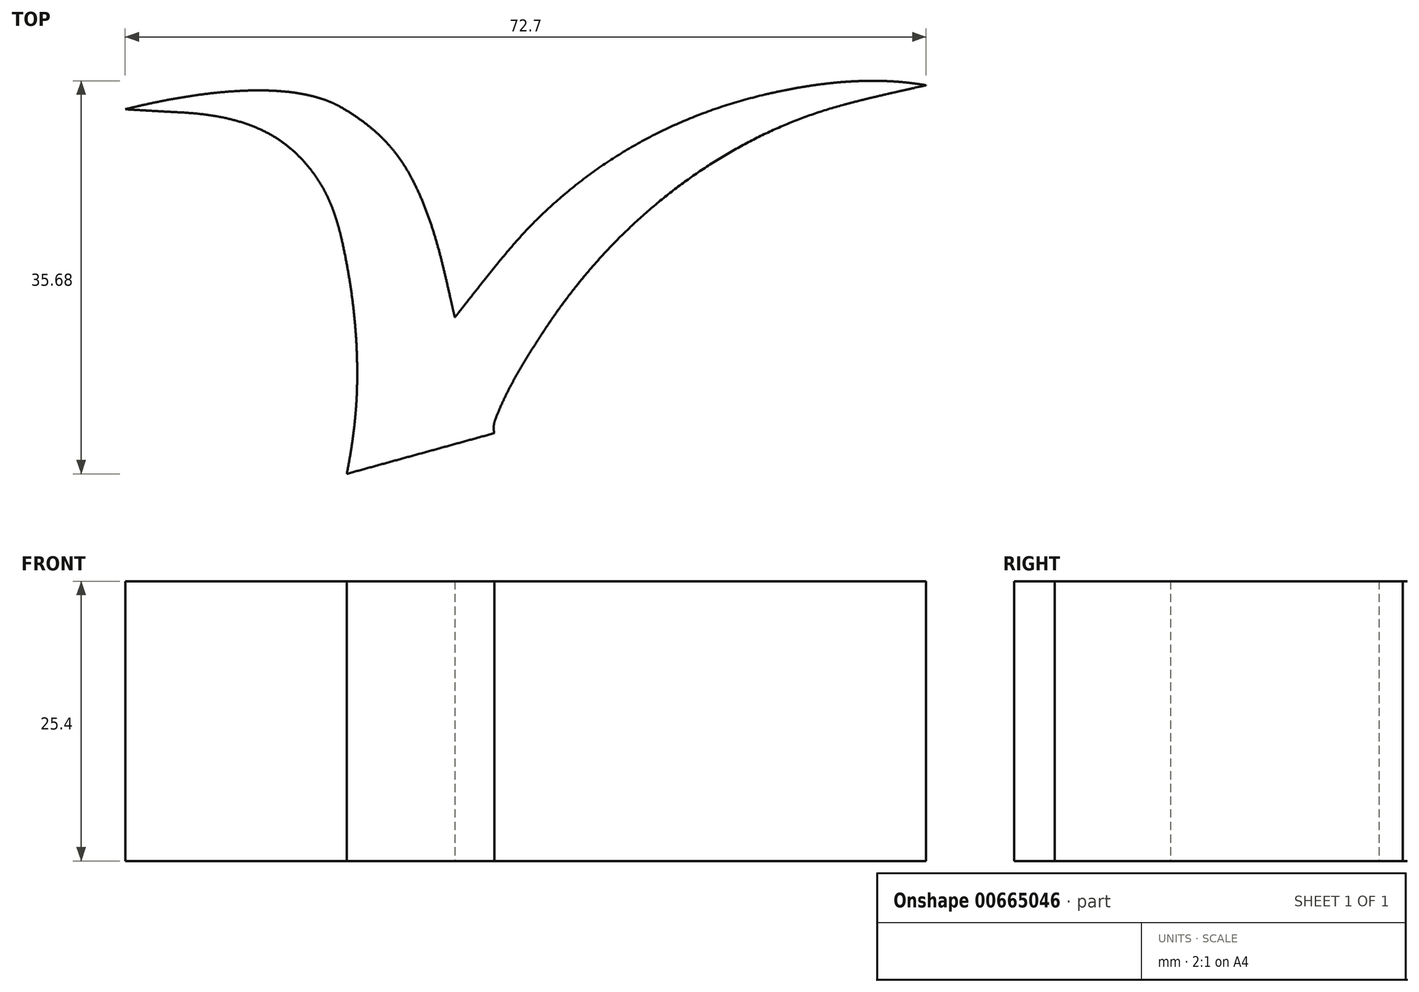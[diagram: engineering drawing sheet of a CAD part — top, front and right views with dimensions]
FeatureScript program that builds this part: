
annotation { "Feature Type Name" : "Feature", "Feature Type Description" : "" }
export const myFeature = defineFeature(function(context is Context, id is Id, definition is map)
    precondition{}
    {
        {
            var Q0;
            Q0=qCreatedBy(makeId("Top.planeOp"),FACE);
            var sketch = newSketch(context, id + "F0", { "sketchPlane" : qUnion([Q0])});
            skLineSegment(sketch, "E0", {"start": v(-36.35, 15.26) * mm, "end": v(-36.3, 15.26) * mm});
            skLineSegment(sketch, "E1", {"start": v(-36.3, 15.26) * mm, "end": v(-36.27, 15.26) * mm});
            skLineSegment(sketch, "E2", {"start": v(-36.27, 15.26) * mm, "end": v(-36.23, 15.25) * mm});
            skLineSegment(sketch, "E3", {"start": v(-36.23, 15.25) * mm, "end": v(-36.2, 15.25) * mm});
            skLineSegment(sketch, "E4", {"start": v(-36.2, 15.25) * mm, "end": v(-36.15, 15.25) * mm});
            skLineSegment(sketch, "E5", {"start": v(-36.15, 15.25) * mm, "end": v(-36.11, 15.25) * mm});
            skLineSegment(sketch, "E6", {"start": v(-36.11, 15.25) * mm, "end": v(-36.07, 15.24) * mm});
            skLineSegment(sketch, "E7", {"start": v(-36.07, 15.24) * mm, "end": v(-36.03, 15.24) * mm});
            skLineSegment(sketch, "E8", {"start": v(-36.03, 15.24) * mm, "end": v(-35.99, 15.24) * mm});
            skLineSegment(sketch, "E9", {"start": v(-35.99, 15.24) * mm, "end": v(-35.95, 15.24) * mm});
            skLineSegment(sketch, "E10", {"start": v(-35.95, 15.24) * mm, "end": v(-35.9, 15.23) * mm});
            skLineSegment(sketch, "E11", {"start": v(-35.9, 15.23) * mm, "end": v(-35.87, 15.23) * mm});
            skLineSegment(sketch, "E12", {"start": v(-35.87, 15.23) * mm, "end": v(-35.83, 15.23) * mm});
            skLineSegment(sketch, "E13", {"start": v(-35.83, 15.23) * mm, "end": v(-35.79, 15.23) * mm});
            skLineSegment(sketch, "E14", {"start": v(-35.79, 15.23) * mm, "end": v(-35.75, 15.22) * mm});
            skLineSegment(sketch, "E15", {"start": v(-35.75, 15.22) * mm, "end": v(-35.7, 15.22) * mm});
            skLineSegment(sketch, "E16", {"start": v(-35.7, 15.22) * mm, "end": v(-35.66, 15.22) * mm});
            skLineSegment(sketch, "E17", {"start": v(-35.66, 15.22) * mm, "end": v(-35.62, 15.22) * mm});
            skLineSegment(sketch, "E18", {"start": v(-35.62, 15.22) * mm, "end": v(-35.58, 15.21) * mm});
            skLineSegment(sketch, "E19", {"start": v(-35.58, 15.21) * mm, "end": v(-35.54, 15.21) * mm});
            skLineSegment(sketch, "E20", {"start": v(-35.54, 15.21) * mm, "end": v(-35.5, 15.2) * mm});
            skLineSegment(sketch, "E21", {"start": v(-35.5, 15.2) * mm, "end": v(-35.46, 15.2) * mm});
            skLineSegment(sketch, "E22", {"start": v(-35.46, 15.2) * mm, "end": v(-35.42, 15.2) * mm});
            skLineSegment(sketch, "E23", {"start": v(-35.42, 15.2) * mm, "end": v(-35.37, 15.2) * mm});
            skLineSegment(sketch, "E24", {"start": v(-35.37, 15.2) * mm, "end": v(-35.33, 15.2) * mm});
            skLineSegment(sketch, "E25", {"start": v(-35.33, 15.2) * mm, "end": v(-35.3, 15.2) * mm});
            skLineSegment(sketch, "E26", {"start": v(-35.3, 15.2) * mm, "end": v(-35.25, 15.2) * mm});
            skLineSegment(sketch, "E27", {"start": v(-35.25, 15.2) * mm, "end": v(-35.2, 15.2) * mm});
            skLineSegment(sketch, "E28", {"start": v(-35.2, 15.2) * mm, "end": v(-35.17, 15.2) * mm});
            skLineSegment(sketch, "E29", {"start": v(-35.17, 15.2) * mm, "end": v(-35.13, 15.19) * mm});
            skLineSegment(sketch, "E30", {"start": v(-35.13, 15.19) * mm, "end": v(-35.08, 15.19) * mm});
            skLineSegment(sketch, "E31", {"start": v(-35.08, 15.19) * mm, "end": v(-35.04, 15.18) * mm});
            skLineSegment(sketch, "E32", {"start": v(-35.04, 15.18) * mm, "end": v(-35, 15.18) * mm});
            skLineSegment(sketch, "E33", {"start": v(-35, 15.18) * mm, "end": v(-34.96, 15.18) * mm});
            skLineSegment(sketch, "E34", {"start": v(-34.96, 15.18) * mm, "end": v(-34.92, 15.18) * mm});
            skLineSegment(sketch, "E35", {"start": v(-34.92, 15.18) * mm, "end": v(-34.87, 15.17) * mm});
            skLineSegment(sketch, "E36", {"start": v(-34.87, 15.17) * mm, "end": v(-34.83, 15.17) * mm});
            skLineSegment(sketch, "E37", {"start": v(-34.83, 15.17) * mm, "end": v(-34.8, 15.17) * mm});
            skLineSegment(sketch, "E38", {"start": v(-34.8, 15.17) * mm, "end": v(-34.75, 15.17) * mm});
            skLineSegment(sketch, "E39", {"start": v(-34.75, 15.17) * mm, "end": v(-34.7, 15.16) * mm});
            skLineSegment(sketch, "E40", {"start": v(-34.7, 15.16) * mm, "end": v(-34.67, 15.16) * mm});
            skLineSegment(sketch, "E41", {"start": v(-34.67, 15.16) * mm, "end": v(-34.62, 15.16) * mm});
            skLineSegment(sketch, "E42", {"start": v(-34.62, 15.16) * mm, "end": v(-34.58, 15.16) * mm});
            skLineSegment(sketch, "E43", {"start": v(-34.58, 15.16) * mm, "end": v(-34.54, 15.15) * mm});
            skLineSegment(sketch, "E44", {"start": v(-34.54, 15.15) * mm, "end": v(-34.5, 15.15) * mm});
            skLineSegment(sketch, "E45", {"start": v(-34.5, 15.15) * mm, "end": v(-34.46, 15.15) * mm});
            skLineSegment(sketch, "E46", {"start": v(-34.46, 15.15) * mm, "end": v(-34.42, 15.15) * mm});
            skLineSegment(sketch, "E47", {"start": v(-34.42, 15.15) * mm, "end": v(-34.37, 15.14) * mm});
            skLineSegment(sketch, "E48", {"start": v(-34.37, 15.14) * mm, "end": v(-34.33, 15.14) * mm});
            skLineSegment(sketch, "E49", {"start": v(-34.33, 15.14) * mm, "end": v(-34.3, 15.14) * mm});
            skLineSegment(sketch, "E50", {"start": v(-34.3, 15.14) * mm, "end": v(-34.25, 15.14) * mm});
            skLineSegment(sketch, "E51", {"start": v(-34.25, 15.14) * mm, "end": v(-34.2, 15.13) * mm});
            skLineSegment(sketch, "E52", {"start": v(-34.2, 15.13) * mm, "end": v(-34.17, 15.13) * mm});
            skLineSegment(sketch, "E53", {"start": v(-34.17, 15.13) * mm, "end": v(-34.12, 15.13) * mm});
            skLineSegment(sketch, "E54", {"start": v(-34.12, 15.13) * mm, "end": v(-34.08, 15.13) * mm});
            skLineSegment(sketch, "E55", {"start": v(-34.08, 15.13) * mm, "end": v(-34.04, 15.12) * mm});
            skLineSegment(sketch, "E56", {"start": v(-34.04, 15.12) * mm, "end": v(-34, 15.12) * mm});
            skLineSegment(sketch, "E57", {"start": v(-34, 15.12) * mm, "end": v(-33.96, 15.12) * mm});
            skLineSegment(sketch, "E58", {"start": v(-33.96, 15.12) * mm, "end": v(-33.92, 15.12) * mm});
            skLineSegment(sketch, "E59", {"start": v(-33.92, 15.12) * mm, "end": v(-33.88, 15.11) * mm});
            skLineSegment(sketch, "E60", {"start": v(-33.88, 15.11) * mm, "end": v(-33.84, 15.11) * mm});
            skLineSegment(sketch, "E61", {"start": v(-33.84, 15.11) * mm, "end": v(-33.8, 15.1) * mm});
            skLineSegment(sketch, "E62", {"start": v(-33.8, 15.1) * mm, "end": v(-33.75, 15.1) * mm});
            skLineSegment(sketch, "E63", {"start": v(-33.75, 15.1) * mm, "end": v(-33.71, 15.1) * mm});
            skLineSegment(sketch, "E64", {"start": v(-33.71, 15.1) * mm, "end": v(-33.67, 15.1) * mm});
            skLineSegment(sketch, "E65", {"start": v(-33.67, 15.1) * mm, "end": v(-33.63, 15.1) * mm});
            skLineSegment(sketch, "E66", {"start": v(-33.63, 15.1) * mm, "end": v(-33.6, 15.1) * mm});
            skLineSegment(sketch, "E67", {"start": v(-33.6, 15.1) * mm, "end": v(-33.55, 15.1) * mm});
            skLineSegment(sketch, "E68", {"start": v(-33.55, 15.1) * mm, "end": v(-33.5, 15.1) * mm});
            skLineSegment(sketch, "E69", {"start": v(-33.5, 15.1) * mm, "end": v(-33.47, 15.1) * mm});
            skLineSegment(sketch, "E70", {"start": v(-33.47, 15.1) * mm, "end": v(-33.43, 15.09) * mm});
            skLineSegment(sketch, "E71", {"start": v(-33.43, 15.09) * mm, "end": v(-33.39, 15.09) * mm});
            skLineSegment(sketch, "E72", {"start": v(-33.39, 15.09) * mm, "end": v(-33.35, 15.08) * mm});
            skLineSegment(sketch, "E73", {"start": v(-33.35, 15.08) * mm, "end": v(-33.3, 15.08) * mm});
            skLineSegment(sketch, "E74", {"start": v(-33.3, 15.08) * mm, "end": v(-33.27, 15.08) * mm});
            skLineSegment(sketch, "E75", {"start": v(-33.27, 15.08) * mm, "end": v(-33.23, 15.08) * mm});
            skLineSegment(sketch, "E76", {"start": v(-33.23, 15.08) * mm, "end": v(-33.19, 15.08) * mm});
            skLineSegment(sketch, "E77", {"start": v(-33.19, 15.08) * mm, "end": v(-33.15, 15.07) * mm});
            skLineSegment(sketch, "E78", {"start": v(-33.15, 15.07) * mm, "end": v(-33.11, 15.07) * mm});
            skLineSegment(sketch, "E79", {"start": v(-33.11, 15.07) * mm, "end": v(-33.07, 15.07) * mm});
            skLineSegment(sketch, "E80", {"start": v(-33.07, 15.07) * mm, "end": v(-33.03, 15.07) * mm});
            skLineSegment(sketch, "E81", {"start": v(-33.03, 15.07) * mm, "end": v(-33, 15.06) * mm});
            skLineSegment(sketch, "E82", {"start": v(-33, 15.06) * mm, "end": v(-32.95, 15.06) * mm});
            skLineSegment(sketch, "E83", {"start": v(-32.95, 15.06) * mm, "end": v(-32.92, 15.06) * mm});
            skLineSegment(sketch, "E84", {"start": v(-32.92, 15.06) * mm, "end": v(-32.88, 15.06) * mm});
            skLineSegment(sketch, "E85", {"start": v(-32.88, 15.06) * mm, "end": v(-32.84, 15.06) * mm});
            skLineSegment(sketch, "E86", {"start": v(-32.84, 15.06) * mm, "end": v(-32.8, 15.05) * mm});
            skLineSegment(sketch, "E87", {"start": v(-32.8, 15.05) * mm, "end": v(-32.76, 15.05) * mm});
            skLineSegment(sketch, "E88", {"start": v(-32.76, 15.05) * mm, "end": v(-32.72, 15.05) * mm});
            skLineSegment(sketch, "E89", {"start": v(-32.72, 15.05) * mm, "end": v(-32.69, 15.05) * mm});
            skLineSegment(sketch, "E90", {"start": v(-32.69, 15.05) * mm, "end": v(-32.65, 15.05) * mm});
            skLineSegment(sketch, "E91", {"start": v(-32.65, 15.05) * mm, "end": v(-32.6, 15.04) * mm});
            skLineSegment(sketch, "E92", {"start": v(-32.6, 15.04) * mm, "end": v(-32.57, 15.04) * mm});
            skLineSegment(sketch, "E93", {"start": v(-32.57, 15.04) * mm, "end": v(-32.54, 15.04) * mm});
            skLineSegment(sketch, "E94", {"start": v(-32.54, 15.04) * mm, "end": v(-32.5, 15.04) * mm});
            skLineSegment(sketch, "E95", {"start": v(-32.5, 15.04) * mm, "end": v(-32.46, 15.04) * mm});
            skLineSegment(sketch, "E96", {"start": v(-32.46, 15.04) * mm, "end": v(-32.42, 15.03) * mm});
            skLineSegment(sketch, "E97", {"start": v(-32.42, 15.03) * mm, "end": v(-32.39, 15.03) * mm});
            skLineSegment(sketch, "E98", {"start": v(-32.39, 15.03) * mm, "end": v(-32.35, 15.03) * mm});
            skLineSegment(sketch, "E99", {"start": v(-32.35, 15.03) * mm, "end": v(-32.31, 15.03) * mm});
            skLineSegment(sketch, "E100", {"start": v(-32.31, 15.03) * mm, "end": v(-32.28, 15.03) * mm});
            skLineSegment(sketch, "E101", {"start": v(-32.28, 15.03) * mm, "end": v(-32.24, 15.02) * mm});
            skLineSegment(sketch, "E102", {"start": v(-32.24, 15.02) * mm, "end": v(-32.2, 15.02) * mm});
            skLineSegment(sketch, "E103", {"start": v(-32.2, 15.02) * mm, "end": v(-32.17, 15.02) * mm});
            skLineSegment(sketch, "E104", {"start": v(-32.17, 15.02) * mm, "end": v(-32.14, 15.02) * mm});
            skLineSegment(sketch, "E105", {"start": v(-32.14, 15.02) * mm, "end": v(-32.1, 15.02) * mm});
            skLineSegment(sketch, "E106", {"start": v(-32.1, 15.02) * mm, "end": v(-32.07, 15.01) * mm});
            skLineSegment(sketch, "E107", {"start": v(-32.07, 15.01) * mm, "end": v(-32.03, 15.01) * mm});
            skLineSegment(sketch, "E108", {"start": v(-32.03, 15.01) * mm, "end": v(-32, 15.01) * mm});
            skLineSegment(sketch, "E109", {"start": v(-32, 15.01) * mm, "end": v(-31.96, 15) * mm});
            skLineSegment(sketch, "E110", {"start": v(-31.96, 15) * mm, "end": v(-31.93, 15) * mm});
            skLineSegment(sketch, "E111", {"start": v(-31.93, 15) * mm, "end": v(-31.9, 15) * mm});
            skLineSegment(sketch, "E112", {"start": v(-31.9, 15) * mm, "end": v(-31.86, 15) * mm});
            skLineSegment(sketch, "E113", {"start": v(-31.86, 15) * mm, "end": v(-31.83, 15) * mm});
            skLineSegment(sketch, "E114", {"start": v(-31.83, 15) * mm, "end": v(-31.8, 15) * mm});
            skLineSegment(sketch, "E115", {"start": v(-31.8, 15) * mm, "end": v(-31.76, 15) * mm});
            skLineSegment(sketch, "E116", {"start": v(-31.76, 15) * mm, "end": v(-31.73, 15) * mm});
            skLineSegment(sketch, "E117", {"start": v(-31.73, 15) * mm, "end": v(-31.7, 15) * mm});
            skLineSegment(sketch, "E118", {"start": v(-31.7, 15) * mm, "end": v(-31.66, 15) * mm});
            skLineSegment(sketch, "E119", {"start": v(-31.66, 15) * mm, "end": v(-31.63, 15) * mm});
            skLineSegment(sketch, "E120", {"start": v(-31.63, 15) * mm, "end": v(-31.6, 14.99) * mm});
            skLineSegment(sketch, "E121", {"start": v(-31.6, 14.99) * mm, "end": v(-31.57, 14.99) * mm});
            skLineSegment(sketch, "E122", {"start": v(-31.57, 14.99) * mm, "end": v(-31.54, 14.99) * mm});
            skLineSegment(sketch, "E123", {"start": v(-31.54, 14.99) * mm, "end": v(-31.5, 14.98) * mm});
            skLineSegment(sketch, "E124", {"start": v(-31.5, 14.98) * mm, "end": v(-31.48, 14.98) * mm});
            skLineSegment(sketch, "E125", {"start": v(-31.48, 14.98) * mm, "end": v(-31.44, 14.98) * mm});
            skLineSegment(sketch, "E126", {"start": v(-31.44, 14.98) * mm, "end": v(-31.41, 14.98) * mm});
            skLineSegment(sketch, "E127", {"start": v(-31.41, 14.98) * mm, "end": v(-31.38, 14.98) * mm});
            skLineSegment(sketch, "E128", {"start": v(-31.38, 14.98) * mm, "end": v(-31.26, 14.97) * mm});
            skLineSegment(sketch, "E129", {"start": v(-31.26, 14.97) * mm, "end": v(-31.14, 14.97) * mm});
            skLineSegment(sketch, "E130", {"start": v(-31.14, 14.97) * mm, "end": v(-31.02, 14.96) * mm});
            skLineSegment(sketch, "E131", {"start": v(-31.02, 14.96) * mm, "end": v(-30.9, 14.95) * mm});
            skLineSegment(sketch, "E132", {"start": v(-30.9, 14.95) * mm, "end": v(-30.78, 14.94) * mm});
            skLineSegment(sketch, "E133", {"start": v(-30.78, 14.94) * mm, "end": v(-30.66, 14.94) * mm});
            skLineSegment(sketch, "E134", {"start": v(-30.66, 14.94) * mm, "end": v(-30.55, 14.93) * mm});
            skLineSegment(sketch, "E135", {"start": v(-30.55, 14.93) * mm, "end": v(-30.43, 14.92) * mm});
            skLineSegment(sketch, "E136", {"start": v(-30.43, 14.92) * mm, "end": v(-30.31, 14.9) * mm});
            skLineSegment(sketch, "E137", {"start": v(-30.31, 14.9) * mm, "end": v(-30.2, 14.9) * mm});
            skLineSegment(sketch, "E138", {"start": v(-30.2, 14.9) * mm, "end": v(-30.08, 14.89) * mm});
            skLineSegment(sketch, "E139", {"start": v(-30.08, 14.89) * mm, "end": v(-29.97, 14.88) * mm});
            skLineSegment(sketch, "E140", {"start": v(-29.97, 14.88) * mm, "end": v(-29.85, 14.87) * mm});
            skLineSegment(sketch, "E141", {"start": v(-29.85, 14.87) * mm, "end": v(-29.74, 14.85) * mm});
            skLineSegment(sketch, "E142", {"start": v(-29.74, 14.85) * mm, "end": v(-29.63, 14.84) * mm});
            skLineSegment(sketch, "E143", {"start": v(-29.63, 14.84) * mm, "end": v(-29.51, 14.83) * mm});
            skLineSegment(sketch, "E144", {"start": v(-29.51, 14.83) * mm, "end": v(-29.4, 14.82) * mm});
            skLineSegment(sketch, "E145", {"start": v(-29.4, 14.82) * mm, "end": v(-29.3, 14.8) * mm});
            skLineSegment(sketch, "E146", {"start": v(-29.3, 14.8) * mm, "end": v(-29.18, 14.8) * mm});
            skLineSegment(sketch, "E147", {"start": v(-29.18, 14.8) * mm, "end": v(-29.07, 14.78) * mm});
            skLineSegment(sketch, "E148", {"start": v(-29.07, 14.78) * mm, "end": v(-28.96, 14.76) * mm});
            skLineSegment(sketch, "E149", {"start": v(-28.96, 14.76) * mm, "end": v(-28.85, 14.75) * mm});
            skLineSegment(sketch, "E150", {"start": v(-28.85, 14.75) * mm, "end": v(-28.74, 14.73) * mm});
            skLineSegment(sketch, "E151", {"start": v(-28.74, 14.73) * mm, "end": v(-28.64, 14.72) * mm});
            skLineSegment(sketch, "E152", {"start": v(-28.64, 14.72) * mm, "end": v(-28.53, 14.7) * mm});
            skLineSegment(sketch, "E153", {"start": v(-28.53, 14.7) * mm, "end": v(-28.42, 14.68) * mm});
            skLineSegment(sketch, "E154", {"start": v(-28.42, 14.68) * mm, "end": v(-28.32, 14.67) * mm});
            skLineSegment(sketch, "E155", {"start": v(-28.32, 14.67) * mm, "end": v(-28.21, 14.65) * mm});
            skLineSegment(sketch, "E156", {"start": v(-28.21, 14.65) * mm, "end": v(-28.1, 14.63) * mm});
            skLineSegment(sketch, "E157", {"start": v(-28.1, 14.63) * mm, "end": v(-28, 14.61) * mm});
            skLineSegment(sketch, "E158", {"start": v(-28, 14.61) * mm, "end": v(-27.9, 14.6) * mm});
            skLineSegment(sketch, "E159", {"start": v(-27.9, 14.6) * mm, "end": v(-27.8, 14.58) * mm});
            skLineSegment(sketch, "E160", {"start": v(-27.8, 14.58) * mm, "end": v(-27.7, 14.56) * mm});
            skLineSegment(sketch, "E161", {"start": v(-27.7, 14.56) * mm, "end": v(-27.6, 14.54) * mm});
            skLineSegment(sketch, "E162", {"start": v(-27.6, 14.54) * mm, "end": v(-27.5, 14.52) * mm});
            skLineSegment(sketch, "E163", {"start": v(-27.5, 14.52) * mm, "end": v(-27.4, 14.5) * mm});
            skLineSegment(sketch, "E164", {"start": v(-27.4, 14.5) * mm, "end": v(-27.3, 14.47) * mm});
            skLineSegment(sketch, "E165", {"start": v(-27.3, 14.47) * mm, "end": v(-27.2, 14.45) * mm});
            skLineSegment(sketch, "E166", {"start": v(-27.2, 14.45) * mm, "end": v(-27.1, 14.43) * mm});
            skLineSegment(sketch, "E167", {"start": v(-27.1, 14.43) * mm, "end": v(-27, 14.4) * mm});
            skLineSegment(sketch, "E168", {"start": v(-27, 14.4) * mm, "end": v(-26.9, 14.38) * mm});
            skLineSegment(sketch, "E169", {"start": v(-26.9, 14.38) * mm, "end": v(-26.8, 14.36) * mm});
            skLineSegment(sketch, "E170", {"start": v(-26.8, 14.36) * mm, "end": v(-26.7, 14.34) * mm});
            skLineSegment(sketch, "E171", {"start": v(-26.7, 14.34) * mm, "end": v(-26.6, 14.31) * mm});
            skLineSegment(sketch, "E172", {"start": v(-26.6, 14.31) * mm, "end": v(-26.51, 14.29) * mm});
            skLineSegment(sketch, "E173", {"start": v(-26.51, 14.29) * mm, "end": v(-26.42, 14.26) * mm});
            skLineSegment(sketch, "E174", {"start": v(-26.42, 14.26) * mm, "end": v(-26.32, 14.24) * mm});
            skLineSegment(sketch, "E175", {"start": v(-26.32, 14.24) * mm, "end": v(-26.23, 14.21) * mm});
            skLineSegment(sketch, "E176", {"start": v(-26.23, 14.21) * mm, "end": v(-26.13, 14.18) * mm});
            skLineSegment(sketch, "E177", {"start": v(-26.13, 14.18) * mm, "end": v(-26.04, 14.16) * mm});
            skLineSegment(sketch, "E178", {"start": v(-26.04, 14.16) * mm, "end": v(-25.95, 14.13) * mm});
            skLineSegment(sketch, "E179", {"start": v(-25.95, 14.13) * mm, "end": v(-25.86, 14.1) * mm});
            skLineSegment(sketch, "E180", {"start": v(-25.86, 14.1) * mm, "end": v(-25.77, 14.07) * mm});
            skLineSegment(sketch, "E181", {"start": v(-25.77, 14.07) * mm, "end": v(-25.67, 14.05) * mm});
            skLineSegment(sketch, "E182", {"start": v(-25.67, 14.05) * mm, "end": v(-25.58, 14.02) * mm});
            skLineSegment(sketch, "E183", {"start": v(-25.58, 14.02) * mm, "end": v(-25.5, 13.99) * mm});
            skLineSegment(sketch, "E184", {"start": v(-25.5, 13.99) * mm, "end": v(-25.4, 13.96) * mm});
            skLineSegment(sketch, "E185", {"start": v(-25.4, 13.96) * mm, "end": v(-25.32, 13.93) * mm});
            skLineSegment(sketch, "E186", {"start": v(-25.32, 13.93) * mm, "end": v(-25.23, 13.9) * mm});
            skLineSegment(sketch, "E187", {"start": v(-25.23, 13.9) * mm, "end": v(-25.14, 13.86) * mm});
            skLineSegment(sketch, "E188", {"start": v(-25.14, 13.86) * mm, "end": v(-25.05, 13.83) * mm});
            skLineSegment(sketch, "E189", {"start": v(-25.05, 13.83) * mm, "end": v(-24.97, 13.8) * mm});
            skLineSegment(sketch, "E190", {"start": v(-24.97, 13.8) * mm, "end": v(-24.88, 13.77) * mm});
            skLineSegment(sketch, "E191", {"start": v(-24.88, 13.77) * mm, "end": v(-24.8, 13.73) * mm});
            skLineSegment(sketch, "E192", {"start": v(-24.8, 13.73) * mm, "end": v(-24.7, 13.7) * mm});
            skLineSegment(sketch, "E193", {"start": v(-24.7, 13.7) * mm, "end": v(-24.62, 13.67) * mm});
            skLineSegment(sketch, "E194", {"start": v(-24.62, 13.67) * mm, "end": v(-24.54, 13.63) * mm});
            skLineSegment(sketch, "E195", {"start": v(-24.54, 13.63) * mm, "end": v(-24.45, 13.6) * mm});
            skLineSegment(sketch, "E196", {"start": v(-24.45, 13.6) * mm, "end": v(-24.37, 13.56) * mm});
            skLineSegment(sketch, "E197", {"start": v(-24.37, 13.56) * mm, "end": v(-24.29, 13.52) * mm});
            skLineSegment(sketch, "E198", {"start": v(-24.29, 13.52) * mm, "end": v(-24.2, 13.49) * mm});
            skLineSegment(sketch, "E199", {"start": v(-24.2, 13.49) * mm, "end": v(-24.12, 13.45) * mm});
            skLineSegment(sketch, "E200", {"start": v(-24.12, 13.45) * mm, "end": v(-24.04, 13.41) * mm});
            skLineSegment(sketch, "E201", {"start": v(-24.04, 13.41) * mm, "end": v(-23.96, 13.38) * mm});
            skLineSegment(sketch, "E202", {"start": v(-23.96, 13.38) * mm, "end": v(-23.88, 13.34) * mm});
            skLineSegment(sketch, "E203", {"start": v(-23.88, 13.34) * mm, "end": v(-23.8, 13.3) * mm});
            skLineSegment(sketch, "E204", {"start": v(-23.8, 13.3) * mm, "end": v(-23.72, 13.26) * mm});
            skLineSegment(sketch, "E205", {"start": v(-23.72, 13.26) * mm, "end": v(-23.64, 13.22) * mm});
            skLineSegment(sketch, "E206", {"start": v(-23.64, 13.22) * mm, "end": v(-23.56, 13.18) * mm});
            skLineSegment(sketch, "E207", {"start": v(-23.56, 13.18) * mm, "end": v(-23.48, 13.14) * mm});
            skLineSegment(sketch, "E208", {"start": v(-23.48, 13.14) * mm, "end": v(-23.4, 13.1) * mm});
            skLineSegment(sketch, "E209", {"start": v(-23.4, 13.1) * mm, "end": v(-23.33, 13.06) * mm});
            skLineSegment(sketch, "E210", {"start": v(-23.33, 13.06) * mm, "end": v(-23.25, 13.01) * mm});
            skLineSegment(sketch, "E211", {"start": v(-23.25, 13.01) * mm, "end": v(-23.18, 12.97) * mm});
            skLineSegment(sketch, "E212", {"start": v(-23.18, 12.97) * mm, "end": v(-23.1, 12.93) * mm});
            skLineSegment(sketch, "E213", {"start": v(-23.1, 12.93) * mm, "end": v(-23.02, 12.88) * mm});
            skLineSegment(sketch, "E214", {"start": v(-23.02, 12.88) * mm, "end": v(-22.95, 12.84) * mm});
            skLineSegment(sketch, "E215", {"start": v(-22.95, 12.84) * mm, "end": v(-22.87, 12.8) * mm});
            skLineSegment(sketch, "E216", {"start": v(-22.87, 12.8) * mm, "end": v(-22.8, 12.75) * mm});
            skLineSegment(sketch, "E217", {"start": v(-22.8, 12.75) * mm, "end": v(-22.73, 12.7) * mm});
            skLineSegment(sketch, "E218", {"start": v(-22.73, 12.7) * mm, "end": v(-22.65, 12.66) * mm});
            skLineSegment(sketch, "E219", {"start": v(-22.65, 12.66) * mm, "end": v(-22.58, 12.61) * mm});
            skLineSegment(sketch, "E220", {"start": v(-22.58, 12.61) * mm, "end": v(-22.5, 12.57) * mm});
            skLineSegment(sketch, "E221", {"start": v(-22.5, 12.57) * mm, "end": v(-22.43, 12.52) * mm});
            skLineSegment(sketch, "E222", {"start": v(-22.43, 12.52) * mm, "end": v(-22.36, 12.47) * mm});
            skLineSegment(sketch, "E223", {"start": v(-22.36, 12.47) * mm, "end": v(-22.3, 12.42) * mm});
            skLineSegment(sketch, "E224", {"start": v(-22.3, 12.42) * mm, "end": v(-22.22, 12.37) * mm});
            skLineSegment(sketch, "E225", {"start": v(-22.22, 12.37) * mm, "end": v(-22.15, 12.32) * mm});
            skLineSegment(sketch, "E226", {"start": v(-22.15, 12.32) * mm, "end": v(-22.08, 12.27) * mm});
            skLineSegment(sketch, "E227", {"start": v(-22.08, 12.27) * mm, "end": v(-22, 12.22) * mm});
            skLineSegment(sketch, "E228", {"start": v(-22, 12.22) * mm, "end": v(-21.94, 12.17) * mm});
            skLineSegment(sketch, "E229", {"start": v(-21.94, 12.17) * mm, "end": v(-21.87, 12.12) * mm});
            skLineSegment(sketch, "E230", {"start": v(-21.87, 12.12) * mm, "end": v(-21.8, 12.07) * mm});
            skLineSegment(sketch, "E231", {"start": v(-21.8, 12.07) * mm, "end": v(-21.73, 12.02) * mm});
            skLineSegment(sketch, "E232", {"start": v(-21.73, 12.02) * mm, "end": v(-21.67, 11.96) * mm});
            skLineSegment(sketch, "E233", {"start": v(-21.67, 11.96) * mm, "end": v(-21.6, 11.91) * mm});
            skLineSegment(sketch, "E234", {"start": v(-21.6, 11.91) * mm, "end": v(-21.53, 11.86) * mm});
            skLineSegment(sketch, "E235", {"start": v(-21.53, 11.86) * mm, "end": v(-21.47, 11.8) * mm});
            skLineSegment(sketch, "E236", {"start": v(-21.47, 11.8) * mm, "end": v(-21.4, 11.75) * mm});
            skLineSegment(sketch, "E237", {"start": v(-21.4, 11.75) * mm, "end": v(-21.33, 11.7) * mm});
            skLineSegment(sketch, "E238", {"start": v(-21.33, 11.7) * mm, "end": v(-21.27, 11.64) * mm});
            skLineSegment(sketch, "E239", {"start": v(-21.27, 11.64) * mm, "end": v(-21.2, 11.58) * mm});
            skLineSegment(sketch, "E240", {"start": v(-21.2, 11.58) * mm, "end": v(-21.14, 11.52) * mm});
            skLineSegment(sketch, "E241", {"start": v(-21.14, 11.52) * mm, "end": v(-21.07, 11.47) * mm});
            skLineSegment(sketch, "E242", {"start": v(-21.07, 11.47) * mm, "end": v(-21.01, 11.4) * mm});
            skLineSegment(sketch, "E243", {"start": v(-21.01, 11.4) * mm, "end": v(-20.95, 11.35) * mm});
            skLineSegment(sketch, "E244", {"start": v(-20.95, 11.35) * mm, "end": v(-20.88, 11.3) * mm});
            skLineSegment(sketch, "E245", {"start": v(-20.88, 11.3) * mm, "end": v(-20.82, 11.23) * mm});
            skLineSegment(sketch, "E246", {"start": v(-20.82, 11.23) * mm, "end": v(-20.76, 11.17) * mm});
            skLineSegment(sketch, "E247", {"start": v(-20.76, 11.17) * mm, "end": v(-20.7, 11.11) * mm});
            skLineSegment(sketch, "E248", {"start": v(-20.7, 11.11) * mm, "end": v(-20.64, 11.05) * mm});
            skLineSegment(sketch, "E249", {"start": v(-20.64, 11.05) * mm, "end": v(-20.57, 10.99) * mm});
            skLineSegment(sketch, "E250", {"start": v(-20.57, 10.99) * mm, "end": v(-20.51, 10.93) * mm});
            skLineSegment(sketch, "E251", {"start": v(-20.51, 10.93) * mm, "end": v(-20.45, 10.86) * mm});
            skLineSegment(sketch, "E252", {"start": v(-20.45, 10.86) * mm, "end": v(-20.4, 10.8) * mm});
            skLineSegment(sketch, "E253", {"start": v(-20.4, 10.8) * mm, "end": v(-20.33, 10.74) * mm});
            skLineSegment(sketch, "E254", {"start": v(-20.33, 10.74) * mm, "end": v(-20.27, 10.67) * mm});
            skLineSegment(sketch, "E255", {"start": v(-20.27, 10.67) * mm, "end": v(-20.21, 10.6) * mm});
            skLineSegment(sketch, "E256", {"start": v(-20.21, 10.6) * mm, "end": v(-20.17, 10.56) * mm});
            skLineSegment(sketch, "E257", {"start": v(-20.17, 10.56) * mm, "end": v(-20.13, 10.52) * mm});
            skLineSegment(sketch, "E258", {"start": v(-20.13, 10.52) * mm, "end": v(-20.1, 10.47) * mm});
            skLineSegment(sketch, "E259", {"start": v(-20.1, 10.47) * mm, "end": v(-20.05, 10.43) * mm});
            skLineSegment(sketch, "E260", {"start": v(-20.05, 10.43) * mm, "end": v(-20.01, 10.38) * mm});
            skLineSegment(sketch, "E261", {"start": v(-20.01, 10.38) * mm, "end": v(-19.97, 10.34) * mm});
            skLineSegment(sketch, "E262", {"start": v(-19.97, 10.34) * mm, "end": v(-19.93, 10.3) * mm});
            skLineSegment(sketch, "E263", {"start": v(-19.93, 10.3) * mm, "end": v(-19.9, 10.25) * mm});
            skLineSegment(sketch, "E264", {"start": v(-19.9, 10.25) * mm, "end": v(-19.85, 10.2) * mm});
            skLineSegment(sketch, "E265", {"start": v(-19.85, 10.2) * mm, "end": v(-19.82, 10.16) * mm});
            skLineSegment(sketch, "E266", {"start": v(-19.82, 10.16) * mm, "end": v(-19.78, 10.11) * mm});
            skLineSegment(sketch, "E267", {"start": v(-19.78, 10.11) * mm, "end": v(-19.74, 10.06) * mm});
            skLineSegment(sketch, "E268", {"start": v(-19.74, 10.06) * mm, "end": v(-19.7, 10.02) * mm});
            skLineSegment(sketch, "E269", {"start": v(-19.7, 10.02) * mm, "end": v(-19.66, 9.97) * mm});
            skLineSegment(sketch, "E270", {"start": v(-19.66, 9.97) * mm, "end": v(-19.63, 9.93) * mm});
            skLineSegment(sketch, "E271", {"start": v(-19.63, 9.93) * mm, "end": v(-19.59, 9.88) * mm});
            skLineSegment(sketch, "E272", {"start": v(-19.59, 9.88) * mm, "end": v(-19.55, 9.83) * mm});
            skLineSegment(sketch, "E273", {"start": v(-19.55, 9.83) * mm, "end": v(-19.52, 9.79) * mm});
            skLineSegment(sketch, "E274", {"start": v(-19.52, 9.79) * mm, "end": v(-19.48, 9.74) * mm});
            skLineSegment(sketch, "E275", {"start": v(-19.48, 9.74) * mm, "end": v(-19.44, 9.7) * mm});
            skLineSegment(sketch, "E276", {"start": v(-19.44, 9.7) * mm, "end": v(-19.4, 9.65) * mm});
            skLineSegment(sketch, "E277", {"start": v(-19.4, 9.65) * mm, "end": v(-19.37, 9.6) * mm});
            skLineSegment(sketch, "E278", {"start": v(-19.37, 9.6) * mm, "end": v(-19.34, 9.55) * mm});
            skLineSegment(sketch, "E279", {"start": v(-19.34, 9.55) * mm, "end": v(-19.3, 9.5) * mm});
            skLineSegment(sketch, "E280", {"start": v(-19.3, 9.5) * mm, "end": v(-19.27, 9.46) * mm});
            skLineSegment(sketch, "E281", {"start": v(-19.27, 9.46) * mm, "end": v(-19.23, 9.4) * mm});
            skLineSegment(sketch, "E282", {"start": v(-19.23, 9.4) * mm, "end": v(-19.2, 9.36) * mm});
            skLineSegment(sketch, "E283", {"start": v(-19.2, 9.36) * mm, "end": v(-19.16, 9.31) * mm});
            skLineSegment(sketch, "E284", {"start": v(-19.16, 9.31) * mm, "end": v(-19.13, 9.27) * mm});
            skLineSegment(sketch, "E285", {"start": v(-19.13, 9.27) * mm, "end": v(-19.1, 9.22) * mm});
            skLineSegment(sketch, "E286", {"start": v(-19.1, 9.22) * mm, "end": v(-19.06, 9.17) * mm});
            skLineSegment(sketch, "E287", {"start": v(-19.06, 9.17) * mm, "end": v(-19.03, 9.12) * mm});
            skLineSegment(sketch, "E288", {"start": v(-19.03, 9.12) * mm, "end": v(-19, 9.07) * mm});
            skLineSegment(sketch, "E289", {"start": v(-19, 9.07) * mm, "end": v(-18.96, 9.02) * mm});
            skLineSegment(sketch, "E290", {"start": v(-18.96, 9.02) * mm, "end": v(-18.93, 8.98) * mm});
            skLineSegment(sketch, "E291", {"start": v(-18.93, 8.98) * mm, "end": v(-18.9, 8.93) * mm});
            skLineSegment(sketch, "E292", {"start": v(-18.9, 8.93) * mm, "end": v(-18.86, 8.88) * mm});
            skLineSegment(sketch, "E293", {"start": v(-18.86, 8.88) * mm, "end": v(-18.83, 8.83) * mm});
            skLineSegment(sketch, "E294", {"start": v(-18.83, 8.83) * mm, "end": v(-18.8, 8.78) * mm});
            skLineSegment(sketch, "E295", {"start": v(-18.8, 8.78) * mm, "end": v(-18.77, 8.73) * mm});
            skLineSegment(sketch, "E296", {"start": v(-18.77, 8.73) * mm, "end": v(-18.74, 8.68) * mm});
            skLineSegment(sketch, "E297", {"start": v(-18.74, 8.68) * mm, "end": v(-18.7, 8.63) * mm});
            skLineSegment(sketch, "E298", {"start": v(-18.7, 8.63) * mm, "end": v(-18.67, 8.58) * mm});
            skLineSegment(sketch, "E299", {"start": v(-18.67, 8.58) * mm, "end": v(-18.64, 8.53) * mm});
            skLineSegment(sketch, "E300", {"start": v(-18.64, 8.53) * mm, "end": v(-18.61, 8.48) * mm});
            skLineSegment(sketch, "E301", {"start": v(-18.61, 8.48) * mm, "end": v(-18.58, 8.43) * mm});
            skLineSegment(sketch, "E302", {"start": v(-18.58, 8.43) * mm, "end": v(-18.55, 8.38) * mm});
            skLineSegment(sketch, "E303", {"start": v(-18.55, 8.38) * mm, "end": v(-18.52, 8.33) * mm});
            skLineSegment(sketch, "E304", {"start": v(-18.52, 8.33) * mm, "end": v(-18.5, 8.28) * mm});
            skLineSegment(sketch, "E305", {"start": v(-18.5, 8.28) * mm, "end": v(-18.46, 8.23) * mm});
            skLineSegment(sketch, "E306", {"start": v(-18.46, 8.23) * mm, "end": v(-18.43, 8.17) * mm});
            skLineSegment(sketch, "E307", {"start": v(-18.43, 8.17) * mm, "end": v(-18.4, 8.12) * mm});
            skLineSegment(sketch, "E308", {"start": v(-18.4, 8.12) * mm, "end": v(-18.38, 8.07) * mm});
            skLineSegment(sketch, "E309", {"start": v(-18.38, 8.07) * mm, "end": v(-18.35, 8.02) * mm});
            skLineSegment(sketch, "E310", {"start": v(-18.35, 8.02) * mm, "end": v(-18.32, 7.97) * mm});
            skLineSegment(sketch, "E311", {"start": v(-18.32, 7.97) * mm, "end": v(-18.3, 7.91) * mm});
            skLineSegment(sketch, "E312", {"start": v(-18.3, 7.91) * mm, "end": v(-18.26, 7.86) * mm});
            skLineSegment(sketch, "E313", {"start": v(-18.26, 7.86) * mm, "end": v(-18.23, 7.8) * mm});
            skLineSegment(sketch, "E314", {"start": v(-18.23, 7.8) * mm, "end": v(-18.2, 7.76) * mm});
            skLineSegment(sketch, "E315", {"start": v(-18.2, 7.76) * mm, "end": v(-18.18, 7.7) * mm});
            skLineSegment(sketch, "E316", {"start": v(-18.18, 7.7) * mm, "end": v(-18.15, 7.65) * mm});
            skLineSegment(sketch, "E317", {"start": v(-18.15, 7.65) * mm, "end": v(-18.12, 7.6) * mm});
            skLineSegment(sketch, "E318", {"start": v(-18.12, 7.6) * mm, "end": v(-18.1, 7.54) * mm});
            skLineSegment(sketch, "E319", {"start": v(-18.1, 7.54) * mm, "end": v(-18.07, 7.49) * mm});
            skLineSegment(sketch, "E320", {"start": v(-18.07, 7.49) * mm, "end": v(-18.04, 7.44) * mm});
            skLineSegment(sketch, "E321", {"start": v(-18.04, 7.44) * mm, "end": v(-18.02, 7.38) * mm});
            skLineSegment(sketch, "E322", {"start": v(-18.02, 7.38) * mm, "end": v(-18, 7.33) * mm});
            skLineSegment(sketch, "E323", {"start": v(-18, 7.33) * mm, "end": v(-17.97, 7.27) * mm});
            skLineSegment(sketch, "E324", {"start": v(-17.97, 7.27) * mm, "end": v(-17.94, 7.22) * mm});
            skLineSegment(sketch, "E325", {"start": v(-17.94, 7.22) * mm, "end": v(-17.91, 7.16) * mm});
            skLineSegment(sketch, "E326", {"start": v(-17.91, 7.16) * mm, "end": v(-17.89, 7.1) * mm});
            skLineSegment(sketch, "E327", {"start": v(-17.89, 7.1) * mm, "end": v(-17.86, 7.05) * mm});
            skLineSegment(sketch, "E328", {"start": v(-17.86, 7.05) * mm, "end": v(-17.84, 7) * mm});
            skLineSegment(sketch, "E329", {"start": v(-17.84, 7) * mm, "end": v(-17.81, 6.94) * mm});
            skLineSegment(sketch, "E330", {"start": v(-17.81, 6.94) * mm, "end": v(-17.79, 6.88) * mm});
            skLineSegment(sketch, "E331", {"start": v(-17.79, 6.88) * mm, "end": v(-17.77, 6.83) * mm});
            skLineSegment(sketch, "E332", {"start": v(-17.77, 6.83) * mm, "end": v(-17.74, 6.77) * mm});
            skLineSegment(sketch, "E333", {"start": v(-17.74, 6.77) * mm, "end": v(-17.72, 6.71) * mm});
            skLineSegment(sketch, "E334", {"start": v(-17.72, 6.71) * mm, "end": v(-17.7, 6.66) * mm});
            skLineSegment(sketch, "E335", {"start": v(-17.7, 6.66) * mm, "end": v(-17.67, 6.6) * mm});
            skLineSegment(sketch, "E336", {"start": v(-17.67, 6.6) * mm, "end": v(-17.65, 6.54) * mm});
            skLineSegment(sketch, "E337", {"start": v(-17.65, 6.54) * mm, "end": v(-17.62, 6.48) * mm});
            skLineSegment(sketch, "E338", {"start": v(-17.62, 6.48) * mm, "end": v(-17.6, 6.42) * mm});
            skLineSegment(sketch, "E339", {"start": v(-17.6, 6.42) * mm, "end": v(-17.58, 6.37) * mm});
            skLineSegment(sketch, "E340", {"start": v(-17.58, 6.37) * mm, "end": v(-17.55, 6.3) * mm});
            skLineSegment(sketch, "E341", {"start": v(-17.55, 6.3) * mm, "end": v(-17.53, 6.25) * mm});
            skLineSegment(sketch, "E342", {"start": v(-17.53, 6.25) * mm, "end": v(-17.5, 6.19) * mm});
            skLineSegment(sketch, "E343", {"start": v(-17.5, 6.19) * mm, "end": v(-17.49, 6.13) * mm});
            skLineSegment(sketch, "E344", {"start": v(-17.49, 6.13) * mm, "end": v(-17.46, 6.07) * mm});
            skLineSegment(sketch, "E345", {"start": v(-17.46, 6.07) * mm, "end": v(-17.44, 6) * mm});
            skLineSegment(sketch, "E346", {"start": v(-17.44, 6) * mm, "end": v(-17.42, 5.95) * mm});
            skLineSegment(sketch, "E347", {"start": v(-17.42, 5.95) * mm, "end": v(-17.4, 5.89) * mm});
            skLineSegment(sketch, "E348", {"start": v(-17.4, 5.89) * mm, "end": v(-17.38, 5.83) * mm});
            skLineSegment(sketch, "E349", {"start": v(-17.38, 5.83) * mm, "end": v(-17.36, 5.77) * mm});
            skLineSegment(sketch, "E350", {"start": v(-17.36, 5.77) * mm, "end": v(-17.33, 5.7) * mm});
            skLineSegment(sketch, "E351", {"start": v(-17.33, 5.7) * mm, "end": v(-17.31, 5.64) * mm});
            skLineSegment(sketch, "E352", {"start": v(-17.31, 5.64) * mm, "end": v(-17.3, 5.58) * mm});
            skLineSegment(sketch, "E353", {"start": v(-17.3, 5.58) * mm, "end": v(-17.27, 5.52) * mm});
            skLineSegment(sketch, "E354", {"start": v(-17.27, 5.52) * mm, "end": v(-17.25, 5.46) * mm});
            skLineSegment(sketch, "E355", {"start": v(-17.25, 5.46) * mm, "end": v(-17.23, 5.4) * mm});
            skLineSegment(sketch, "E356", {"start": v(-17.23, 5.4) * mm, "end": v(-17.21, 5.33) * mm});
            skLineSegment(sketch, "E357", {"start": v(-17.21, 5.33) * mm, "end": v(-17.2, 5.27) * mm});
            skLineSegment(sketch, "E358", {"start": v(-17.2, 5.27) * mm, "end": v(-17.17, 5.2) * mm});
            skLineSegment(sketch, "E359", {"start": v(-17.17, 5.2) * mm, "end": v(-17.15, 5.14) * mm});
            skLineSegment(sketch, "E360", {"start": v(-17.15, 5.14) * mm, "end": v(-17.13, 5.08) * mm});
            skLineSegment(sketch, "E361", {"start": v(-17.13, 5.08) * mm, "end": v(-17.11, 5.01) * mm});
            skLineSegment(sketch, "E362", {"start": v(-17.11, 5.01) * mm, "end": v(-17.1, 4.95) * mm});
            skLineSegment(sketch, "E363", {"start": v(-17.1, 4.95) * mm, "end": v(-17.07, 4.88) * mm});
            skLineSegment(sketch, "E364", {"start": v(-17.07, 4.88) * mm, "end": v(-17.05, 4.82) * mm});
            skLineSegment(sketch, "E365", {"start": v(-17.05, 4.82) * mm, "end": v(-17.03, 4.75) * mm});
            skLineSegment(sketch, "E366", {"start": v(-17.03, 4.75) * mm, "end": v(-17.02, 4.69) * mm});
            skLineSegment(sketch, "E367", {"start": v(-17.02, 4.69) * mm, "end": v(-17, 4.62) * mm});
            skLineSegment(sketch, "E368", {"start": v(-17, 4.62) * mm, "end": v(-16.98, 4.55) * mm});
            skLineSegment(sketch, "E369", {"start": v(-16.98, 4.55) * mm, "end": v(-16.96, 4.49) * mm});
            skLineSegment(sketch, "E370", {"start": v(-16.96, 4.49) * mm, "end": v(-16.94, 4.42) * mm});
            skLineSegment(sketch, "E371", {"start": v(-16.94, 4.42) * mm, "end": v(-16.92, 4.35) * mm});
            skLineSegment(sketch, "E372", {"start": v(-16.92, 4.35) * mm, "end": v(-16.9, 4.29) * mm});
            skLineSegment(sketch, "E373", {"start": v(-16.9, 4.29) * mm, "end": v(-16.89, 4.22) * mm});
            skLineSegment(sketch, "E374", {"start": v(-16.89, 4.22) * mm, "end": v(-16.87, 4.15) * mm});
            skLineSegment(sketch, "E375", {"start": v(-16.87, 4.15) * mm, "end": v(-16.85, 4.08) * mm});
            skLineSegment(sketch, "E376", {"start": v(-16.85, 4.08) * mm, "end": v(-16.84, 4.01) * mm});
            skLineSegment(sketch, "E377", {"start": v(-16.84, 4.01) * mm, "end": v(-16.82, 3.94) * mm});
            skLineSegment(sketch, "E378", {"start": v(-16.82, 3.94) * mm, "end": v(-16.8, 3.87) * mm});
            skLineSegment(sketch, "E379", {"start": v(-16.8, 3.87) * mm, "end": v(-16.79, 3.8) * mm});
            skLineSegment(sketch, "E380", {"start": v(-16.79, 3.8) * mm, "end": v(-16.77, 3.73) * mm});
            skLineSegment(sketch, "E381", {"start": v(-16.77, 3.73) * mm, "end": v(-16.75, 3.66) * mm});
            skLineSegment(sketch, "E382", {"start": v(-16.75, 3.66) * mm, "end": v(-16.74, 3.6) * mm});
            skLineSegment(sketch, "E383", {"start": v(-16.74, 3.6) * mm, "end": v(-16.72, 3.52) * mm});
            skLineSegment(sketch, "E384", {"start": v(-16.72, 3.52) * mm, "end": v(-16.7, 3.41) * mm});
            skLineSegment(sketch, "E385", {"start": v(-16.7, 3.41) * mm, "end": v(-16.67, 3.3) * mm});
            skLineSegment(sketch, "E386", {"start": v(-16.67, 3.3) * mm, "end": v(-16.65, 3.2) * mm});
            skLineSegment(sketch, "E387", {"start": v(-16.65, 3.2) * mm, "end": v(-16.62, 3.1) * mm});
            skLineSegment(sketch, "E388", {"start": v(-16.62, 3.1) * mm, "end": v(-16.6, 2.99) * mm});
            skLineSegment(sketch, "E389", {"start": v(-16.6, 2.99) * mm, "end": v(-16.58, 2.88) * mm});
            skLineSegment(sketch, "E390", {"start": v(-16.58, 2.88) * mm, "end": v(-16.55, 2.78) * mm});
            skLineSegment(sketch, "E391", {"start": v(-16.55, 2.78) * mm, "end": v(-16.53, 2.67) * mm});
            skLineSegment(sketch, "E392", {"start": v(-16.53, 2.67) * mm, "end": v(-16.5, 2.57) * mm});
            skLineSegment(sketch, "E393", {"start": v(-16.5, 2.57) * mm, "end": v(-16.49, 2.46) * mm});
            skLineSegment(sketch, "E394", {"start": v(-16.49, 2.46) * mm, "end": v(-16.46, 2.35) * mm});
            skLineSegment(sketch, "E395", {"start": v(-16.46, 2.35) * mm, "end": v(-16.44, 2.25) * mm});
            skLineSegment(sketch, "E396", {"start": v(-16.44, 2.25) * mm, "end": v(-16.42, 2.14) * mm});
            skLineSegment(sketch, "E397", {"start": v(-16.42, 2.14) * mm, "end": v(-16.4, 2.04) * mm});
            skLineSegment(sketch, "E398", {"start": v(-16.4, 2.04) * mm, "end": v(-16.38, 1.93) * mm});
            skLineSegment(sketch, "E399", {"start": v(-16.38, 1.93) * mm, "end": v(-16.36, 1.83) * mm});
            skLineSegment(sketch, "E400", {"start": v(-16.36, 1.83) * mm, "end": v(-16.34, 1.72) * mm});
            skLineSegment(sketch, "E401", {"start": v(-16.34, 1.72) * mm, "end": v(-16.32, 1.61) * mm});
            skLineSegment(sketch, "E402", {"start": v(-16.32, 1.61) * mm, "end": v(-16.3, 1.5) * mm});
            skLineSegment(sketch, "E403", {"start": v(-16.3, 1.5) * mm, "end": v(-16.28, 1.4) * mm});
            skLineSegment(sketch, "E404", {"start": v(-16.28, 1.4) * mm, "end": v(-16.26, 1.3) * mm});
            skLineSegment(sketch, "E405", {"start": v(-16.26, 1.3) * mm, "end": v(-16.24, 1.2) * mm});
            skLineSegment(sketch, "E406", {"start": v(-16.24, 1.2) * mm, "end": v(-16.22, 1.09) * mm});
            skLineSegment(sketch, "E407", {"start": v(-16.22, 1.09) * mm, "end": v(-16.2, 0.98) * mm});
            skLineSegment(sketch, "E408", {"start": v(-16.2, 0.98) * mm, "end": v(-16.18, 0.88) * mm});
            skLineSegment(sketch, "E409", {"start": v(-16.18, 0.88) * mm, "end": v(-16.16, 0.77) * mm});
            skLineSegment(sketch, "E410", {"start": v(-16.16, 0.77) * mm, "end": v(-16.14, 0.66) * mm});
            skLineSegment(sketch, "E411", {"start": v(-16.14, 0.66) * mm, "end": v(-16.12, 0.56) * mm});
            skLineSegment(sketch, "E412", {"start": v(-16.12, 0.56) * mm, "end": v(-16.1, 0.45) * mm});
            skLineSegment(sketch, "E413", {"start": v(-16.1, 0.45) * mm, "end": v(-16.08, 0.35) * mm});
            skLineSegment(sketch, "E414", {"start": v(-16.08, 0.35) * mm, "end": v(-16.07, 0.24) * mm});
            skLineSegment(sketch, "E415", {"start": v(-16.07, 0.24) * mm, "end": v(-16.05, 0.14) * mm});
            skLineSegment(sketch, "E416", {"start": v(-16.05, 0.14) * mm, "end": v(-16.03, 0.03) * mm});
            skLineSegment(sketch, "E417", {"start": v(-16.03, 0.03) * mm, "end": v(-16.01, -0.07) * mm});
            skLineSegment(sketch, "E418", {"start": v(-16.01, -0.07) * mm, "end": v(-16, -0.18) * mm});
            skLineSegment(sketch, "E419", {"start": v(-16, -0.18) * mm, "end": v(-15.98, -0.28) * mm});
            skLineSegment(sketch, "E420", {"start": v(-15.98, -0.28) * mm, "end": v(-15.96, -0.39) * mm});
            skLineSegment(sketch, "E421", {"start": v(-15.96, -0.39) * mm, "end": v(-15.95, -0.5) * mm});
            skLineSegment(sketch, "E422", {"start": v(-15.95, -0.5) * mm, "end": v(-15.93, -0.6) * mm});
            skLineSegment(sketch, "E423", {"start": v(-15.93, -0.6) * mm, "end": v(-15.91, -0.7) * mm});
            skLineSegment(sketch, "E424", {"start": v(-15.91, -0.7) * mm, "end": v(-15.9, -0.8) * mm});
            skLineSegment(sketch, "E425", {"start": v(-15.9, -0.8) * mm, "end": v(-15.88, -0.91) * mm});
            skLineSegment(sketch, "E426", {"start": v(-15.88, -0.91) * mm, "end": v(-15.87, -1.02) * mm});
            skLineSegment(sketch, "E427", {"start": v(-15.87, -1.02) * mm, "end": v(-15.85, -1.12) * mm});
            skLineSegment(sketch, "E428", {"start": v(-15.85, -1.12) * mm, "end": v(-15.84, -1.23) * mm});
            skLineSegment(sketch, "E429", {"start": v(-15.84, -1.23) * mm, "end": v(-15.82, -1.33) * mm});
            skLineSegment(sketch, "E430", {"start": v(-15.82, -1.33) * mm, "end": v(-15.8, -1.44) * mm});
            skLineSegment(sketch, "E431", {"start": v(-15.8, -1.44) * mm, "end": v(-15.8, -1.54) * mm});
            skLineSegment(sketch, "E432", {"start": v(-15.8, -1.54) * mm, "end": v(-15.78, -1.65) * mm});
            skLineSegment(sketch, "E433", {"start": v(-15.78, -1.65) * mm, "end": v(-15.76, -1.75) * mm});
            skLineSegment(sketch, "E434", {"start": v(-15.76, -1.75) * mm, "end": v(-15.75, -1.86) * mm});
            skLineSegment(sketch, "E435", {"start": v(-15.75, -1.86) * mm, "end": v(-15.74, -1.96) * mm});
            skLineSegment(sketch, "E436", {"start": v(-15.74, -1.96) * mm, "end": v(-15.72, -2.07) * mm});
            skLineSegment(sketch, "E437", {"start": v(-15.72, -2.07) * mm, "end": v(-15.7, -2.17) * mm});
            skLineSegment(sketch, "E438", {"start": v(-15.7, -2.17) * mm, "end": v(-15.7, -2.28) * mm});
            skLineSegment(sketch, "E439", {"start": v(-15.7, -2.28) * mm, "end": v(-15.68, -2.38) * mm});
            skLineSegment(sketch, "E440", {"start": v(-15.68, -2.38) * mm, "end": v(-15.67, -2.49) * mm});
            skLineSegment(sketch, "E441", {"start": v(-15.67, -2.49) * mm, "end": v(-15.66, -2.6) * mm});
            skLineSegment(sketch, "E442", {"start": v(-15.66, -2.6) * mm, "end": v(-15.65, -2.7) * mm});
            skLineSegment(sketch, "E443", {"start": v(-15.65, -2.7) * mm, "end": v(-15.63, -2.8) * mm});
            skLineSegment(sketch, "E444", {"start": v(-15.63, -2.8) * mm, "end": v(-15.62, -2.9) * mm});
            skLineSegment(sketch, "E445", {"start": v(-15.62, -2.9) * mm, "end": v(-15.61, -3.01) * mm});
            skLineSegment(sketch, "E446", {"start": v(-15.61, -3.01) * mm, "end": v(-15.6, -3.11) * mm});
            skLineSegment(sketch, "E447", {"start": v(-15.6, -3.11) * mm, "end": v(-15.59, -3.22) * mm});
            skLineSegment(sketch, "E448", {"start": v(-15.59, -3.22) * mm, "end": v(-15.58, -3.32) * mm});
            skLineSegment(sketch, "E449", {"start": v(-15.58, -3.32) * mm, "end": v(-15.57, -3.43) * mm});
            skLineSegment(sketch, "E450", {"start": v(-15.57, -3.43) * mm, "end": v(-15.56, -3.53) * mm});
            skLineSegment(sketch, "E451", {"start": v(-15.56, -3.53) * mm, "end": v(-15.55, -3.64) * mm});
            skLineSegment(sketch, "E452", {"start": v(-15.55, -3.64) * mm, "end": v(-15.53, -3.74) * mm});
            skLineSegment(sketch, "E453", {"start": v(-15.53, -3.74) * mm, "end": v(-15.53, -3.85) * mm});
            skLineSegment(sketch, "E454", {"start": v(-15.53, -3.85) * mm, "end": v(-15.52, -3.95) * mm});
            skLineSegment(sketch, "E455", {"start": v(-15.52, -3.95) * mm, "end": v(-15.5, -4.05) * mm});
            skLineSegment(sketch, "E456", {"start": v(-15.5, -4.05) * mm, "end": v(-15.5, -4.16) * mm});
            skLineSegment(sketch, "E457", {"start": v(-15.5, -4.16) * mm, "end": v(-15.49, -4.26) * mm});
            skLineSegment(sketch, "E458", {"start": v(-15.49, -4.26) * mm, "end": v(-15.48, -4.37) * mm});
            skLineSegment(sketch, "E459", {"start": v(-15.48, -4.37) * mm, "end": v(-15.47, -4.47) * mm});
            skLineSegment(sketch, "E460", {"start": v(-15.47, -4.47) * mm, "end": v(-15.46, -4.57) * mm});
            skLineSegment(sketch, "E461", {"start": v(-15.46, -4.57) * mm, "end": v(-15.45, -4.68) * mm});
            skLineSegment(sketch, "E462", {"start": v(-15.45, -4.68) * mm, "end": v(-15.44, -4.78) * mm});
            skLineSegment(sketch, "E463", {"start": v(-15.44, -4.78) * mm, "end": v(-15.44, -4.88) * mm});
            skLineSegment(sketch, "E464", {"start": v(-15.44, -4.88) * mm, "end": v(-15.43, -4.99) * mm});
            skLineSegment(sketch, "E465", {"start": v(-15.43, -4.99) * mm, "end": v(-15.42, -5.1) * mm});
            skLineSegment(sketch, "E466", {"start": v(-15.42, -5.1) * mm, "end": v(-15.41, -5.2) * mm});
            skLineSegment(sketch, "E467", {"start": v(-15.41, -5.2) * mm, "end": v(-15.4, -5.3) * mm});
            skLineSegment(sketch, "E468", {"start": v(-15.4, -5.3) * mm, "end": v(-15.4, -5.4) * mm});
            skLineSegment(sketch, "E469", {"start": v(-15.4, -5.4) * mm, "end": v(-15.4, -5.5) * mm});
            skLineSegment(sketch, "E470", {"start": v(-15.4, -5.5) * mm, "end": v(-15.39, -5.61) * mm});
            skLineSegment(sketch, "E471", {"start": v(-15.39, -5.61) * mm, "end": v(-15.38, -5.71) * mm});
            skLineSegment(sketch, "E472", {"start": v(-15.38, -5.71) * mm, "end": v(-15.37, -5.82) * mm});
            skLineSegment(sketch, "E473", {"start": v(-15.37, -5.82) * mm, "end": v(-15.37, -5.92) * mm});
            skLineSegment(sketch, "E474", {"start": v(-15.37, -5.92) * mm, "end": v(-15.36, -6.02) * mm});
            skLineSegment(sketch, "E475", {"start": v(-15.36, -6.02) * mm, "end": v(-15.36, -6.13) * mm});
            skLineSegment(sketch, "E476", {"start": v(-15.36, -6.13) * mm, "end": v(-15.35, -6.23) * mm});
            skLineSegment(sketch, "E477", {"start": v(-15.35, -6.23) * mm, "end": v(-15.35, -6.33) * mm});
            skLineSegment(sketch, "E478", {"start": v(-15.35, -6.33) * mm, "end": v(-15.34, -6.44) * mm});
            skLineSegment(sketch, "E479", {"start": v(-15.34, -6.44) * mm, "end": v(-15.34, -6.54) * mm});
            skLineSegment(sketch, "E480", {"start": v(-15.34, -6.54) * mm, "end": v(-15.33, -6.64) * mm});
            skLineSegment(sketch, "E481", {"start": v(-15.33, -6.64) * mm, "end": v(-15.33, -6.75) * mm});
            skLineSegment(sketch, "E482", {"start": v(-15.33, -6.75) * mm, "end": v(-15.33, -6.85) * mm});
            skLineSegment(sketch, "E483", {"start": v(-15.33, -6.85) * mm, "end": v(-15.32, -6.95) * mm});
            skLineSegment(sketch, "E484", {"start": v(-15.32, -6.95) * mm, "end": v(-15.32, -7.05) * mm});
            skLineSegment(sketch, "E485", {"start": v(-15.32, -7.05) * mm, "end": v(-15.31, -7.16) * mm});
            skLineSegment(sketch, "E486", {"start": v(-15.31, -7.16) * mm, "end": v(-15.31, -7.26) * mm});
            skLineSegment(sketch, "E487", {"start": v(-15.31, -7.26) * mm, "end": v(-15.3, -7.36) * mm});
            skLineSegment(sketch, "E488", {"start": v(-15.3, -7.36) * mm, "end": v(-15.3, -7.47) * mm});
            skLineSegment(sketch, "E489", {"start": v(-15.3, -7.47) * mm, "end": v(-15.3, -7.57) * mm});
            skLineSegment(sketch, "E490", {"start": v(-15.3, -7.57) * mm, "end": v(-15.3, -7.67) * mm});
            skLineSegment(sketch, "E491", {"start": v(-15.3, -7.67) * mm, "end": v(-15.3, -7.77) * mm});
            skLineSegment(sketch, "E492", {"start": v(-15.3, -7.77) * mm, "end": v(-15.3, -7.88) * mm});
            skLineSegment(sketch, "E493", {"start": v(-15.3, -7.88) * mm, "end": v(-15.3, -7.98) * mm});
            skLineSegment(sketch, "E494", {"start": v(-15.3, -7.98) * mm, "end": v(-15.3, -8.08) * mm});
            skLineSegment(sketch, "E495", {"start": v(-15.3, -8.08) * mm, "end": v(-15.3, -8.18) * mm});
            skLineSegment(sketch, "E496", {"start": v(-15.3, -8.18) * mm, "end": v(-15.3, -8.28) * mm});
            skLineSegment(sketch, "E497", {"start": v(-15.3, -8.28) * mm, "end": v(-15.3, -8.39) * mm});
            skLineSegment(sketch, "E498", {"start": v(-15.3, -8.39) * mm, "end": v(-15.29, -8.49) * mm});
            skLineSegment(sketch, "E499", {"start": v(-15.29, -8.49) * mm, "end": v(-15.29, -8.6) * mm});
            skLineSegment(sketch, "E500", {"start": v(-15.29, -8.6) * mm, "end": v(-15.29, -8.7) * mm});
            skLineSegment(sketch, "E501", {"start": v(-15.29, -8.7) * mm, "end": v(-15.29, -8.8) * mm});
            skLineSegment(sketch, "E502", {"start": v(-15.29, -8.8) * mm, "end": v(-15.29, -8.9) * mm});
            skLineSegment(sketch, "E503", {"start": v(-15.29, -8.9) * mm, "end": v(-15.29, -9) * mm});
            skLineSegment(sketch, "E504", {"start": v(-15.29, -9) * mm, "end": v(-15.3, -9.1) * mm});
            skLineSegment(sketch, "E505", {"start": v(-15.3, -9.1) * mm, "end": v(-15.3, -9.2) * mm});
            skLineSegment(sketch, "E506", {"start": v(-15.3, -9.2) * mm, "end": v(-15.3, -9.3) * mm});
            skLineSegment(sketch, "E507", {"start": v(-15.3, -9.3) * mm, "end": v(-15.3, -9.4) * mm});
            skLineSegment(sketch, "E508", {"start": v(-15.3, -9.4) * mm, "end": v(-15.3, -9.5) * mm});
            skLineSegment(sketch, "E509", {"start": v(-15.3, -9.5) * mm, "end": v(-15.3, -9.6) * mm});
            skLineSegment(sketch, "E510", {"start": v(-15.3, -9.6) * mm, "end": v(-15.3, -9.7) * mm});
            skLineSegment(sketch, "E511", {"start": v(-15.3, -9.7) * mm, "end": v(-15.3, -9.81) * mm});
            skLineSegment(sketch, "E512", {"start": v(-15.3, -9.81) * mm, "end": v(-15.3, -9.87) * mm});
            skLineSegment(sketch, "E513", {"start": v(-15.3, -9.87) * mm, "end": v(-15.3, -9.93) * mm});
            skLineSegment(sketch, "E514", {"start": v(-15.3, -9.93) * mm, "end": v(-15.3, -9.98) * mm});
            skLineSegment(sketch, "E515", {"start": v(-15.3, -9.98) * mm, "end": v(-15.3, -10.04) * mm});
            skLineSegment(sketch, "E516", {"start": v(-15.3, -10.04) * mm, "end": v(-15.3, -10.1) * mm});
            skLineSegment(sketch, "E517", {"start": v(-15.3, -10.1) * mm, "end": v(-15.3, -10.16) * mm});
            skLineSegment(sketch, "E518", {"start": v(-15.3, -10.16) * mm, "end": v(-15.31, -10.22) * mm});
            skLineSegment(sketch, "E519", {"start": v(-15.31, -10.22) * mm, "end": v(-15.31, -10.27) * mm});
            skLineSegment(sketch, "E520", {"start": v(-15.31, -10.27) * mm, "end": v(-15.31, -10.33) * mm});
            skLineSegment(sketch, "E521", {"start": v(-15.31, -10.33) * mm, "end": v(-15.32, -10.39) * mm});
            skLineSegment(sketch, "E522", {"start": v(-15.32, -10.39) * mm, "end": v(-15.32, -10.45) * mm});
            skLineSegment(sketch, "E523", {"start": v(-15.32, -10.45) * mm, "end": v(-15.32, -10.5) * mm});
            skLineSegment(sketch, "E524", {"start": v(-15.32, -10.5) * mm, "end": v(-15.32, -10.56) * mm});
            skLineSegment(sketch, "E525", {"start": v(-15.32, -10.56) * mm, "end": v(-15.33, -10.62) * mm});
            skLineSegment(sketch, "E526", {"start": v(-15.33, -10.62) * mm, "end": v(-15.33, -10.68) * mm});
            skLineSegment(sketch, "E527", {"start": v(-15.33, -10.68) * mm, "end": v(-15.33, -10.74) * mm});
            skLineSegment(sketch, "E528", {"start": v(-15.33, -10.74) * mm, "end": v(-15.33, -10.8) * mm});
            skLineSegment(sketch, "E529", {"start": v(-15.33, -10.8) * mm, "end": v(-15.34, -10.86) * mm});
            skLineSegment(sketch, "E530", {"start": v(-15.34, -10.86) * mm, "end": v(-15.34, -10.91) * mm});
            skLineSegment(sketch, "E531", {"start": v(-15.34, -10.91) * mm, "end": v(-15.34, -10.97) * mm});
            skLineSegment(sketch, "E532", {"start": v(-15.34, -10.97) * mm, "end": v(-15.35, -11.03) * mm});
            skLineSegment(sketch, "E533", {"start": v(-15.35, -11.03) * mm, "end": v(-15.35, -11.1) * mm});
            skLineSegment(sketch, "E534", {"start": v(-15.35, -11.1) * mm, "end": v(-15.35, -11.15) * mm});
            skLineSegment(sketch, "E535", {"start": v(-15.35, -11.15) * mm, "end": v(-15.36, -11.2) * mm});
            skLineSegment(sketch, "E536", {"start": v(-15.36, -11.2) * mm, "end": v(-15.36, -11.27) * mm});
            skLineSegment(sketch, "E537", {"start": v(-15.36, -11.27) * mm, "end": v(-15.36, -11.33) * mm});
            skLineSegment(sketch, "E538", {"start": v(-15.36, -11.33) * mm, "end": v(-15.37, -11.38) * mm});
            skLineSegment(sketch, "E539", {"start": v(-15.37, -11.38) * mm, "end": v(-15.37, -11.44) * mm});
            skLineSegment(sketch, "E540", {"start": v(-15.37, -11.44) * mm, "end": v(-15.37, -11.5) * mm});
            skLineSegment(sketch, "E541", {"start": v(-15.37, -11.5) * mm, "end": v(-15.38, -11.56) * mm});
            skLineSegment(sketch, "E542", {"start": v(-15.38, -11.56) * mm, "end": v(-15.38, -11.62) * mm});
            skLineSegment(sketch, "E543", {"start": v(-15.38, -11.62) * mm, "end": v(-15.39, -11.68) * mm});
            skLineSegment(sketch, "E544", {"start": v(-15.39, -11.68) * mm, "end": v(-15.39, -11.74) * mm});
            skLineSegment(sketch, "E545", {"start": v(-15.39, -11.74) * mm, "end": v(-15.4, -11.8) * mm});
            skLineSegment(sketch, "E546", {"start": v(-15.4, -11.8) * mm, "end": v(-15.4, -11.86) * mm});
            skLineSegment(sketch, "E547", {"start": v(-15.4, -11.86) * mm, "end": v(-15.4, -11.92) * mm});
            skLineSegment(sketch, "E548", {"start": v(-15.4, -11.92) * mm, "end": v(-15.4, -11.98) * mm});
            skLineSegment(sketch, "E549", {"start": v(-15.4, -11.98) * mm, "end": v(-15.41, -12.04) * mm});
            skLineSegment(sketch, "E550", {"start": v(-15.41, -12.04) * mm, "end": v(-15.42, -12.1) * mm});
            skLineSegment(sketch, "E551", {"start": v(-15.42, -12.1) * mm, "end": v(-15.42, -12.16) * mm});
            skLineSegment(sketch, "E552", {"start": v(-15.42, -12.16) * mm, "end": v(-15.43, -12.22) * mm});
            skLineSegment(sketch, "E553", {"start": v(-15.43, -12.22) * mm, "end": v(-15.43, -12.28) * mm});
            skLineSegment(sketch, "E554", {"start": v(-15.43, -12.28) * mm, "end": v(-15.44, -12.34) * mm});
            skLineSegment(sketch, "E555", {"start": v(-15.44, -12.34) * mm, "end": v(-15.44, -12.4) * mm});
            skLineSegment(sketch, "E556", {"start": v(-15.44, -12.4) * mm, "end": v(-15.45, -12.46) * mm});
            skLineSegment(sketch, "E557", {"start": v(-15.45, -12.46) * mm, "end": v(-15.45, -12.52) * mm});
            skLineSegment(sketch, "E558", {"start": v(-15.45, -12.52) * mm, "end": v(-15.46, -12.58) * mm});
            skLineSegment(sketch, "E559", {"start": v(-15.46, -12.58) * mm, "end": v(-15.46, -12.64) * mm});
            skLineSegment(sketch, "E560", {"start": v(-15.46, -12.64) * mm, "end": v(-15.47, -12.7) * mm});
            skLineSegment(sketch, "E561", {"start": v(-15.47, -12.7) * mm, "end": v(-15.48, -12.76) * mm});
            skLineSegment(sketch, "E562", {"start": v(-15.48, -12.76) * mm, "end": v(-15.48, -12.82) * mm});
            skLineSegment(sketch, "E563", {"start": v(-15.48, -12.82) * mm, "end": v(-15.49, -12.88) * mm});
            skLineSegment(sketch, "E564", {"start": v(-15.49, -12.88) * mm, "end": v(-15.5, -12.95) * mm});
            skLineSegment(sketch, "E565", {"start": v(-15.5, -12.95) * mm, "end": v(-15.5, -13) * mm});
            skLineSegment(sketch, "E566", {"start": v(-15.5, -13) * mm, "end": v(-15.5, -13.07) * mm});
            skLineSegment(sketch, "E567", {"start": v(-15.5, -13.07) * mm, "end": v(-15.51, -13.13) * mm});
            skLineSegment(sketch, "E568", {"start": v(-15.51, -13.13) * mm, "end": v(-15.52, -13.2) * mm});
            skLineSegment(sketch, "E569", {"start": v(-15.52, -13.2) * mm, "end": v(-15.53, -13.25) * mm});
            skLineSegment(sketch, "E570", {"start": v(-15.53, -13.25) * mm, "end": v(-15.53, -13.31) * mm});
            skLineSegment(sketch, "E571", {"start": v(-15.53, -13.31) * mm, "end": v(-15.54, -13.37) * mm});
            skLineSegment(sketch, "E572", {"start": v(-15.54, -13.37) * mm, "end": v(-15.55, -13.44) * mm});
            skLineSegment(sketch, "E573", {"start": v(-15.55, -13.44) * mm, "end": v(-15.55, -13.5) * mm});
            skLineSegment(sketch, "E574", {"start": v(-15.55, -13.5) * mm, "end": v(-15.56, -13.56) * mm});
            skLineSegment(sketch, "E575", {"start": v(-15.56, -13.56) * mm, "end": v(-15.57, -13.62) * mm});
            skLineSegment(sketch, "E576", {"start": v(-15.57, -13.62) * mm, "end": v(-15.57, -13.68) * mm});
            skLineSegment(sketch, "E577", {"start": v(-15.57, -13.68) * mm, "end": v(-15.58, -13.75) * mm});
            skLineSegment(sketch, "E578", {"start": v(-15.58, -13.75) * mm, "end": v(-15.59, -13.8) * mm});
            skLineSegment(sketch, "E579", {"start": v(-15.59, -13.8) * mm, "end": v(-15.6, -13.87) * mm});
            skLineSegment(sketch, "E580", {"start": v(-15.6, -13.87) * mm, "end": v(-15.6, -13.93) * mm});
            skLineSegment(sketch, "E581", {"start": v(-15.6, -13.93) * mm, "end": v(-15.61, -14) * mm});
            skLineSegment(sketch, "E582", {"start": v(-15.61, -14) * mm, "end": v(-15.62, -14.06) * mm});
            skLineSegment(sketch, "E583", {"start": v(-15.62, -14.06) * mm, "end": v(-15.63, -14.12) * mm});
            skLineSegment(sketch, "E584", {"start": v(-15.63, -14.12) * mm, "end": v(-15.64, -14.19) * mm});
            skLineSegment(sketch, "E585", {"start": v(-15.64, -14.19) * mm, "end": v(-15.64, -14.25) * mm});
            skLineSegment(sketch, "E586", {"start": v(-15.64, -14.25) * mm, "end": v(-15.65, -14.31) * mm});
            skLineSegment(sketch, "E587", {"start": v(-15.65, -14.31) * mm, "end": v(-15.66, -14.38) * mm});
            skLineSegment(sketch, "E588", {"start": v(-15.66, -14.38) * mm, "end": v(-15.67, -14.44) * mm});
            skLineSegment(sketch, "E589", {"start": v(-15.67, -14.44) * mm, "end": v(-15.68, -14.5) * mm});
            skLineSegment(sketch, "E590", {"start": v(-15.68, -14.5) * mm, "end": v(-15.69, -14.57) * mm});
            skLineSegment(sketch, "E591", {"start": v(-15.69, -14.57) * mm, "end": v(-15.7, -14.63) * mm});
            skLineSegment(sketch, "E592", {"start": v(-15.7, -14.63) * mm, "end": v(-15.7, -14.7) * mm});
            skLineSegment(sketch, "E593", {"start": v(-15.7, -14.7) * mm, "end": v(-15.71, -14.76) * mm});
            skLineSegment(sketch, "E594", {"start": v(-15.71, -14.76) * mm, "end": v(-15.72, -14.82) * mm});
            skLineSegment(sketch, "E595", {"start": v(-15.72, -14.82) * mm, "end": v(-15.73, -14.89) * mm});
            skLineSegment(sketch, "E596", {"start": v(-15.73, -14.89) * mm, "end": v(-15.74, -14.95) * mm});
            skLineSegment(sketch, "E597", {"start": v(-15.74, -14.95) * mm, "end": v(-15.75, -15.01) * mm});
            skLineSegment(sketch, "E598", {"start": v(-15.75, -15.01) * mm, "end": v(-15.76, -15.08) * mm});
            skLineSegment(sketch, "E599", {"start": v(-15.76, -15.08) * mm, "end": v(-15.77, -15.14) * mm});
            skLineSegment(sketch, "E600", {"start": v(-15.77, -15.14) * mm, "end": v(-15.78, -15.2) * mm});
            skLineSegment(sketch, "E601", {"start": v(-15.78, -15.2) * mm, "end": v(-15.79, -15.27) * mm});
            skLineSegment(sketch, "E602", {"start": v(-15.79, -15.27) * mm, "end": v(-15.8, -15.34) * mm});
            skLineSegment(sketch, "E603", {"start": v(-15.8, -15.34) * mm, "end": v(-15.8, -15.4) * mm});
            skLineSegment(sketch, "E604", {"start": v(-15.8, -15.4) * mm, "end": v(-15.82, -15.47) * mm});
            skLineSegment(sketch, "E605", {"start": v(-15.82, -15.47) * mm, "end": v(-15.83, -15.54) * mm});
            skLineSegment(sketch, "E606", {"start": v(-15.83, -15.54) * mm, "end": v(-15.84, -15.6) * mm});
            skLineSegment(sketch, "E607", {"start": v(-15.84, -15.6) * mm, "end": v(-15.85, -15.67) * mm});
            skLineSegment(sketch, "E608", {"start": v(-15.85, -15.67) * mm, "end": v(-15.86, -15.73) * mm});
            skLineSegment(sketch, "E609", {"start": v(-15.86, -15.73) * mm, "end": v(-15.87, -15.8) * mm});
            skLineSegment(sketch, "E610", {"start": v(-15.87, -15.8) * mm, "end": v(-15.88, -15.86) * mm});
            skLineSegment(sketch, "E611", {"start": v(-15.88, -15.86) * mm, "end": v(-15.89, -15.93) * mm});
            skLineSegment(sketch, "E612", {"start": v(-15.89, -15.93) * mm, "end": v(-15.9, -16) * mm});
            skLineSegment(sketch, "E613", {"start": v(-15.9, -16) * mm, "end": v(-15.91, -16.06) * mm});
            skLineSegment(sketch, "E614", {"start": v(-15.91, -16.06) * mm, "end": v(-15.92, -16.13) * mm});
            skLineSegment(sketch, "E615", {"start": v(-15.92, -16.13) * mm, "end": v(-15.93, -16.2) * mm});
            skLineSegment(sketch, "E616", {"start": v(-15.93, -16.2) * mm, "end": v(-15.94, -16.26) * mm});
            skLineSegment(sketch, "E617", {"start": v(-15.94, -16.26) * mm, "end": v(-15.96, -16.33) * mm});
            skLineSegment(sketch, "E618", {"start": v(-15.96, -16.33) * mm, "end": v(-15.97, -16.4) * mm});
            skLineSegment(sketch, "E619", {"start": v(-15.97, -16.4) * mm, "end": v(-15.98, -16.47) * mm});
            skLineSegment(sketch, "E620", {"start": v(-15.98, -16.47) * mm, "end": v(-16, -16.53) * mm});
            skLineSegment(sketch, "E621", {"start": v(-16, -16.53) * mm, "end": v(-16, -16.6) * mm});
            skLineSegment(sketch, "E622", {"start": v(-16, -16.6) * mm, "end": v(-16.01, -16.67) * mm});
            skLineSegment(sketch, "E623", {"start": v(-16.01, -16.67) * mm, "end": v(-16.03, -16.74) * mm});
            skLineSegment(sketch, "E624", {"start": v(-16.03, -16.74) * mm, "end": v(-16.04, -16.8) * mm});
            skLineSegment(sketch, "E625", {"start": v(-16.04, -16.8) * mm, "end": v(-16.05, -16.87) * mm});
            skLineSegment(sketch, "E626", {"start": v(-16.05, -16.87) * mm, "end": v(-16.06, -16.94) * mm});
            skLineSegment(sketch, "E627", {"start": v(-16.06, -16.94) * mm, "end": v(-16.08, -17) * mm});
            skLineSegment(sketch, "E628", {"start": v(-16.08, -17) * mm, "end": v(-16.09, -17.08) * mm});
            skLineSegment(sketch, "E629", {"start": v(-16.09, -17.08) * mm, "end": v(-16.1, -17.15) * mm});
            skLineSegment(sketch, "E630", {"start": v(-16.1, -17.15) * mm, "end": v(-16.11, -17.21) * mm});
            skLineSegment(sketch, "E631", {"start": v(-16.11, -17.21) * mm, "end": v(-16.13, -17.28) * mm});
            skLineSegment(sketch, "E632", {"start": v(-16.13, -17.28) * mm, "end": v(-16.14, -17.35) * mm});
            skLineSegment(sketch, "E633", {"start": v(-16.14, -17.35) * mm, "end": v(-16.15, -17.42) * mm});
            skLineSegment(sketch, "E634", {"start": v(-16.15, -17.42) * mm, "end": v(-16.16, -17.5) * mm});
            skLineSegment(sketch, "E635", {"start": v(-16.16, -17.5) * mm, "end": v(-16.18, -17.56) * mm});
            skLineSegment(sketch, "E636", {"start": v(-16.18, -17.56) * mm, "end": v(-16.2, -17.63) * mm});
            skLineSegment(sketch, "E637", {"start": v(-16.2, -17.63) * mm, "end": v(-16.2, -17.7) * mm});
            skLineSegment(sketch, "E638", {"start": v(-16.2, -17.7) * mm, "end": v(-16.22, -17.77) * mm});
            skLineSegment(sketch, "E639", {"start": v(-16.22, -17.77) * mm, "end": v(-16.23, -17.84) * mm});
            skLineSegment(sketch, "E640", {"start": v(-16.23, -17.84) * mm, "end": v(-16.13, -17.81) * mm});
            skLineSegment(sketch, "E641", {"start": v(-16.13, -17.81) * mm, "end": v(-16.02, -17.78) * mm});
            skLineSegment(sketch, "E642", {"start": v(-16.02, -17.78) * mm, "end": v(-15.92, -17.76) * mm});
            skLineSegment(sketch, "E643", {"start": v(-15.92, -17.76) * mm, "end": v(-15.81, -17.73) * mm});
            skLineSegment(sketch, "E644", {"start": v(-15.81, -17.73) * mm, "end": v(-15.7, -17.7) * mm});
            skLineSegment(sketch, "E645", {"start": v(-15.7, -17.7) * mm, "end": v(-15.6, -17.67) * mm});
            skLineSegment(sketch, "E646", {"start": v(-15.6, -17.67) * mm, "end": v(-15.5, -17.64) * mm});
            skLineSegment(sketch, "E647", {"start": v(-15.5, -17.64) * mm, "end": v(-15.4, -17.61) * mm});
            skLineSegment(sketch, "E648", {"start": v(-15.4, -17.61) * mm, "end": v(-15.3, -17.58) * mm});
            skLineSegment(sketch, "E649", {"start": v(-15.3, -17.58) * mm, "end": v(-15.19, -17.55) * mm});
            skLineSegment(sketch, "E650", {"start": v(-15.19, -17.55) * mm, "end": v(-15.08, -17.52) * mm});
            skLineSegment(sketch, "E651", {"start": v(-15.08, -17.52) * mm, "end": v(-14.98, -17.5) * mm});
            skLineSegment(sketch, "E652", {"start": v(-14.98, -17.5) * mm, "end": v(-14.87, -17.47) * mm});
            skLineSegment(sketch, "E653", {"start": v(-14.87, -17.47) * mm, "end": v(-14.77, -17.44) * mm});
            skLineSegment(sketch, "E654", {"start": v(-14.77, -17.44) * mm, "end": v(-14.66, -17.4) * mm});
            skLineSegment(sketch, "E655", {"start": v(-14.66, -17.4) * mm, "end": v(-14.56, -17.38) * mm});
            skLineSegment(sketch, "E656", {"start": v(-14.56, -17.38) * mm, "end": v(-14.45, -17.35) * mm});
            skLineSegment(sketch, "E657", {"start": v(-14.45, -17.35) * mm, "end": v(-14.35, -17.32) * mm});
            skLineSegment(sketch, "E658", {"start": v(-14.35, -17.32) * mm, "end": v(-14.25, -17.3) * mm});
            skLineSegment(sketch, "E659", {"start": v(-14.25, -17.3) * mm, "end": v(-14.14, -17.27) * mm});
            skLineSegment(sketch, "E660", {"start": v(-14.14, -17.27) * mm, "end": v(-14.04, -17.24) * mm});
            skLineSegment(sketch, "E661", {"start": v(-14.04, -17.24) * mm, "end": v(-13.93, -17.2) * mm});
            skLineSegment(sketch, "E662", {"start": v(-13.93, -17.2) * mm, "end": v(-13.83, -17.18) * mm});
            skLineSegment(sketch, "E663", {"start": v(-13.83, -17.18) * mm, "end": v(-13.72, -17.15) * mm});
            skLineSegment(sketch, "E664", {"start": v(-13.72, -17.15) * mm, "end": v(-13.62, -17.12) * mm});
            skLineSegment(sketch, "E665", {"start": v(-13.62, -17.12) * mm, "end": v(-13.51, -17.1) * mm});
            skLineSegment(sketch, "E666", {"start": v(-13.51, -17.1) * mm, "end": v(-13.4, -17.06) * mm});
            skLineSegment(sketch, "E667", {"start": v(-13.4, -17.06) * mm, "end": v(-13.3, -17.03) * mm});
            skLineSegment(sketch, "E668", {"start": v(-13.3, -17.03) * mm, "end": v(-13.2, -17) * mm});
            skLineSegment(sketch, "E669", {"start": v(-13.2, -17) * mm, "end": v(-13.1, -16.98) * mm});
            skLineSegment(sketch, "E670", {"start": v(-13.1, -16.98) * mm, "end": v(-13, -16.95) * mm});
            skLineSegment(sketch, "E671", {"start": v(-13, -16.95) * mm, "end": v(-12.89, -16.92) * mm});
            skLineSegment(sketch, "E672", {"start": v(-12.89, -16.92) * mm, "end": v(-12.78, -16.9) * mm});
            skLineSegment(sketch, "E673", {"start": v(-12.78, -16.9) * mm, "end": v(-12.68, -16.86) * mm});
            skLineSegment(sketch, "E674", {"start": v(-12.68, -16.86) * mm, "end": v(-12.57, -16.83) * mm});
            skLineSegment(sketch, "E675", {"start": v(-12.57, -16.83) * mm, "end": v(-12.47, -16.8) * mm});
            skLineSegment(sketch, "E676", {"start": v(-12.47, -16.8) * mm, "end": v(-12.36, -16.78) * mm});
            skLineSegment(sketch, "E677", {"start": v(-12.36, -16.78) * mm, "end": v(-12.26, -16.75) * mm});
            skLineSegment(sketch, "E678", {"start": v(-12.26, -16.75) * mm, "end": v(-12.15, -16.72) * mm});
            skLineSegment(sketch, "E679", {"start": v(-12.15, -16.72) * mm, "end": v(-12.05, -16.69) * mm});
            skLineSegment(sketch, "E680", {"start": v(-12.05, -16.69) * mm, "end": v(-11.95, -16.66) * mm});
            skLineSegment(sketch, "E681", {"start": v(-11.95, -16.66) * mm, "end": v(-11.84, -16.63) * mm});
            skLineSegment(sketch, "E682", {"start": v(-11.84, -16.63) * mm, "end": v(-11.74, -16.6) * mm});
            skLineSegment(sketch, "E683", {"start": v(-11.74, -16.6) * mm, "end": v(-11.63, -16.57) * mm});
            skLineSegment(sketch, "E684", {"start": v(-11.63, -16.57) * mm, "end": v(-11.53, -16.55) * mm});
            skLineSegment(sketch, "E685", {"start": v(-11.53, -16.55) * mm, "end": v(-11.42, -16.52) * mm});
            skLineSegment(sketch, "E686", {"start": v(-11.42, -16.52) * mm, "end": v(-11.32, -16.49) * mm});
            skLineSegment(sketch, "E687", {"start": v(-11.32, -16.49) * mm, "end": v(-11.21, -16.46) * mm});
            skLineSegment(sketch, "E688", {"start": v(-11.21, -16.46) * mm, "end": v(-11.1, -16.43) * mm});
            skLineSegment(sketch, "E689", {"start": v(-11.1, -16.43) * mm, "end": v(-11, -16.4) * mm});
            skLineSegment(sketch, "E690", {"start": v(-11, -16.4) * mm, "end": v(-10.9, -16.37) * mm});
            skLineSegment(sketch, "E691", {"start": v(-10.9, -16.37) * mm, "end": v(-10.8, -16.34) * mm});
            skLineSegment(sketch, "E692", {"start": v(-10.8, -16.34) * mm, "end": v(-10.7, -16.31) * mm});
            skLineSegment(sketch, "E693", {"start": v(-10.7, -16.31) * mm, "end": v(-10.59, -16.29) * mm});
            skLineSegment(sketch, "E694", {"start": v(-10.59, -16.29) * mm, "end": v(-10.48, -16.26) * mm});
            skLineSegment(sketch, "E695", {"start": v(-10.48, -16.26) * mm, "end": v(-10.38, -16.23) * mm});
            skLineSegment(sketch, "E696", {"start": v(-10.38, -16.23) * mm, "end": v(-10.27, -16.2) * mm});
            skLineSegment(sketch, "E697", {"start": v(-10.27, -16.2) * mm, "end": v(-10.17, -16.17) * mm});
            skLineSegment(sketch, "E698", {"start": v(-10.17, -16.17) * mm, "end": v(-10.06, -16.14) * mm});
            skLineSegment(sketch, "E699", {"start": v(-10.06, -16.14) * mm, "end": v(-9.96, -16.11) * mm});
            skLineSegment(sketch, "E700", {"start": v(-9.96, -16.11) * mm, "end": v(-9.85, -16.08) * mm});
            skLineSegment(sketch, "E701", {"start": v(-9.85, -16.08) * mm, "end": v(-9.75, -16.06) * mm});
            skLineSegment(sketch, "E702", {"start": v(-9.75, -16.06) * mm, "end": v(-9.65, -16.03) * mm});
            skLineSegment(sketch, "E703", {"start": v(-9.65, -16.03) * mm, "end": v(-9.54, -16) * mm});
            skLineSegment(sketch, "E704", {"start": v(-9.54, -16) * mm, "end": v(-9.44, -15.97) * mm});
            skLineSegment(sketch, "E705", {"start": v(-9.44, -15.97) * mm, "end": v(-9.33, -15.94) * mm});
            skLineSegment(sketch, "E706", {"start": v(-9.33, -15.94) * mm, "end": v(-9.23, -15.91) * mm});
            skLineSegment(sketch, "E707", {"start": v(-9.23, -15.91) * mm, "end": v(-9.12, -15.88) * mm});
            skLineSegment(sketch, "E708", {"start": v(-9.12, -15.88) * mm, "end": v(-9.02, -15.85) * mm});
            skLineSegment(sketch, "E709", {"start": v(-9.02, -15.85) * mm, "end": v(-8.91, -15.82) * mm});
            skLineSegment(sketch, "E710", {"start": v(-8.91, -15.82) * mm, "end": v(-8.8, -15.8) * mm});
            skLineSegment(sketch, "E711", {"start": v(-8.8, -15.8) * mm, "end": v(-8.7, -15.77) * mm});
            skLineSegment(sketch, "E712", {"start": v(-8.7, -15.77) * mm, "end": v(-8.6, -15.74) * mm});
            skLineSegment(sketch, "E713", {"start": v(-8.6, -15.74) * mm, "end": v(-8.5, -15.7) * mm});
            skLineSegment(sketch, "E714", {"start": v(-8.5, -15.7) * mm, "end": v(-8.4, -15.68) * mm});
            skLineSegment(sketch, "E715", {"start": v(-8.4, -15.68) * mm, "end": v(-8.29, -15.65) * mm});
            skLineSegment(sketch, "E716", {"start": v(-8.29, -15.65) * mm, "end": v(-8.18, -15.62) * mm});
            skLineSegment(sketch, "E717", {"start": v(-8.18, -15.62) * mm, "end": v(-8.08, -15.6) * mm});
            skLineSegment(sketch, "E718", {"start": v(-8.08, -15.6) * mm, "end": v(-7.97, -15.57) * mm});
            skLineSegment(sketch, "E719", {"start": v(-7.97, -15.57) * mm, "end": v(-7.87, -15.54) * mm});
            skLineSegment(sketch, "E720", {"start": v(-7.87, -15.54) * mm, "end": v(-7.76, -15.5) * mm});
            skLineSegment(sketch, "E721", {"start": v(-7.76, -15.5) * mm, "end": v(-7.66, -15.48) * mm});
            skLineSegment(sketch, "E722", {"start": v(-7.66, -15.48) * mm, "end": v(-7.55, -15.45) * mm});
            skLineSegment(sketch, "E723", {"start": v(-7.55, -15.45) * mm, "end": v(-7.45, -15.42) * mm});
            skLineSegment(sketch, "E724", {"start": v(-7.45, -15.42) * mm, "end": v(-7.35, -15.4) * mm});
            skLineSegment(sketch, "E725", {"start": v(-7.35, -15.4) * mm, "end": v(-7.24, -15.36) * mm});
            skLineSegment(sketch, "E726", {"start": v(-7.24, -15.36) * mm, "end": v(-7.14, -15.33) * mm});
            skLineSegment(sketch, "E727", {"start": v(-7.14, -15.33) * mm, "end": v(-7.03, -15.3) * mm});
            skLineSegment(sketch, "E728", {"start": v(-7.03, -15.3) * mm, "end": v(-6.93, -15.28) * mm});
            skLineSegment(sketch, "E729", {"start": v(-6.93, -15.28) * mm, "end": v(-6.82, -15.25) * mm});
            skLineSegment(sketch, "E730", {"start": v(-6.82, -15.25) * mm, "end": v(-6.72, -15.22) * mm});
            skLineSegment(sketch, "E731", {"start": v(-6.72, -15.22) * mm, "end": v(-6.61, -15.2) * mm});
            skLineSegment(sketch, "E732", {"start": v(-6.61, -15.2) * mm, "end": v(-6.5, -15.16) * mm});
            skLineSegment(sketch, "E733", {"start": v(-6.5, -15.16) * mm, "end": v(-6.4, -15.13) * mm});
            skLineSegment(sketch, "E734", {"start": v(-6.4, -15.13) * mm, "end": v(-6.3, -15.1) * mm});
            skLineSegment(sketch, "E735", {"start": v(-6.3, -15.1) * mm, "end": v(-6.2, -15.08) * mm});
            skLineSegment(sketch, "E736", {"start": v(-6.2, -15.08) * mm, "end": v(-6.1, -15.05) * mm});
            skLineSegment(sketch, "E737", {"start": v(-6.1, -15.05) * mm, "end": v(-5.99, -15.02) * mm});
            skLineSegment(sketch, "E738", {"start": v(-5.99, -15.02) * mm, "end": v(-5.88, -14.99) * mm});
            skLineSegment(sketch, "E739", {"start": v(-5.88, -14.99) * mm, "end": v(-5.78, -14.96) * mm});
            skLineSegment(sketch, "E740", {"start": v(-5.78, -14.96) * mm, "end": v(-5.67, -14.93) * mm});
            skLineSegment(sketch, "E741", {"start": v(-5.67, -14.93) * mm, "end": v(-5.57, -14.9) * mm});
            skLineSegment(sketch, "E742", {"start": v(-5.57, -14.9) * mm, "end": v(-5.46, -14.87) * mm});
            skLineSegment(sketch, "E743", {"start": v(-5.46, -14.87) * mm, "end": v(-5.36, -14.84) * mm});
            skLineSegment(sketch, "E744", {"start": v(-5.36, -14.84) * mm, "end": v(-5.26, -14.82) * mm});
            skLineSegment(sketch, "E745", {"start": v(-5.26, -14.82) * mm, "end": v(-5.15, -14.79) * mm});
            skLineSegment(sketch, "E746", {"start": v(-5.15, -14.79) * mm, "end": v(-5.05, -14.76) * mm});
            skLineSegment(sketch, "E747", {"start": v(-5.05, -14.76) * mm, "end": v(-4.94, -14.73) * mm});
            skLineSegment(sketch, "E748", {"start": v(-4.94, -14.73) * mm, "end": v(-4.84, -14.7) * mm});
            skLineSegment(sketch, "E749", {"start": v(-4.84, -14.7) * mm, "end": v(-4.73, -14.67) * mm});
            skLineSegment(sketch, "E750", {"start": v(-4.73, -14.67) * mm, "end": v(-4.63, -14.64) * mm});
            skLineSegment(sketch, "E751", {"start": v(-4.63, -14.64) * mm, "end": v(-4.52, -14.61) * mm});
            skLineSegment(sketch, "E752", {"start": v(-4.52, -14.61) * mm, "end": v(-4.42, -14.59) * mm});
            skLineSegment(sketch, "E753", {"start": v(-4.42, -14.59) * mm, "end": v(-4.31, -14.56) * mm});
            skLineSegment(sketch, "E754", {"start": v(-4.31, -14.56) * mm, "end": v(-4.2, -14.53) * mm});
            skLineSegment(sketch, "E755", {"start": v(-4.2, -14.53) * mm, "end": v(-4.1, -14.5) * mm});
            skLineSegment(sketch, "E756", {"start": v(-4.1, -14.5) * mm, "end": v(-4, -14.47) * mm});
            skLineSegment(sketch, "E757", {"start": v(-4, -14.47) * mm, "end": v(-3.9, -14.44) * mm});
            skLineSegment(sketch, "E758", {"start": v(-3.9, -14.44) * mm, "end": v(-3.8, -14.41) * mm});
            skLineSegment(sketch, "E759", {"start": v(-3.8, -14.41) * mm, "end": v(-3.69, -14.38) * mm});
            skLineSegment(sketch, "E760", {"start": v(-3.69, -14.38) * mm, "end": v(-3.58, -14.35) * mm});
            skLineSegment(sketch, "E761", {"start": v(-3.58, -14.35) * mm, "end": v(-3.48, -14.33) * mm});
            skLineSegment(sketch, "E762", {"start": v(-3.48, -14.33) * mm, "end": v(-3.37, -14.3) * mm});
            skLineSegment(sketch, "E763", {"start": v(-3.37, -14.3) * mm, "end": v(-3.27, -14.27) * mm});
            skLineSegment(sketch, "E764", {"start": v(-3.27, -14.27) * mm, "end": v(-3.16, -14.24) * mm});
            skLineSegment(sketch, "E765", {"start": v(-3.16, -14.24) * mm, "end": v(-3.06, -14.21) * mm});
            skLineSegment(sketch, "E766", {"start": v(-3.06, -14.21) * mm, "end": v(-2.96, -14.18) * mm});
            skLineSegment(sketch, "E767", {"start": v(-2.96, -14.18) * mm, "end": v(-2.85, -14.15) * mm});
            skLineSegment(sketch, "E768", {"start": v(-2.85, -14.15) * mm, "end": v(-2.85, -14.15) * mm});
            skLineSegment(sketch, "E769", {"start": v(-2.85, -14.15) * mm, "end": v(-2.85, -14.14) * mm});
            skLineSegment(sketch, "E770", {"start": v(-2.85, -14.14) * mm, "end": v(-2.86, -14.13) * mm});
            skLineSegment(sketch, "E771", {"start": v(-2.86, -14.13) * mm, "end": v(-2.86, -14.12) * mm});
            skLineSegment(sketch, "E772", {"start": v(-2.86, -14.12) * mm, "end": v(-2.86, -14.11) * mm});
            skLineSegment(sketch, "E773", {"start": v(-2.86, -14.11) * mm, "end": v(-2.86, -14.1) * mm});
            skLineSegment(sketch, "E774", {"start": v(-2.86, -14.1) * mm, "end": v(-2.86, -14.1) * mm});
            skLineSegment(sketch, "E775", {"start": v(-2.86, -14.1) * mm, "end": v(-2.86, -14.08) * mm});
            skLineSegment(sketch, "E776", {"start": v(-2.86, -14.08) * mm, "end": v(-2.86, -14.07) * mm});
            skLineSegment(sketch, "E777", {"start": v(-2.86, -14.07) * mm, "end": v(-2.87, -14.07) * mm});
            skLineSegment(sketch, "E778", {"start": v(-2.87, -14.07) * mm, "end": v(-2.87, -14.06) * mm});
            skLineSegment(sketch, "E779", {"start": v(-2.87, -14.06) * mm, "end": v(-2.87, -14.05) * mm});
            skLineSegment(sketch, "E780", {"start": v(-2.87, -14.05) * mm, "end": v(-2.87, -14.04) * mm});
            skLineSegment(sketch, "E781", {"start": v(-2.87, -14.04) * mm, "end": v(-2.87, -14.03) * mm});
            skLineSegment(sketch, "E782", {"start": v(-2.87, -14.03) * mm, "end": v(-2.87, -14.03) * mm});
            skLineSegment(sketch, "E783", {"start": v(-2.87, -14.03) * mm, "end": v(-2.87, -14.02) * mm});
            skLineSegment(sketch, "E784", {"start": v(-2.87, -14.02) * mm, "end": v(-2.87, -14) * mm});
            skLineSegment(sketch, "E785", {"start": v(-2.87, -14) * mm, "end": v(-2.88, -14) * mm});
            skLineSegment(sketch, "E786", {"start": v(-2.88, -14) * mm, "end": v(-2.88, -14) * mm});
            skLineSegment(sketch, "E787", {"start": v(-2.88, -14) * mm, "end": v(-2.88, -13.98) * mm});
            skLineSegment(sketch, "E788", {"start": v(-2.88, -13.98) * mm, "end": v(-2.88, -13.98) * mm});
            skLineSegment(sketch, "E789", {"start": v(-2.88, -13.98) * mm, "end": v(-2.88, -13.97) * mm});
            skLineSegment(sketch, "E790", {"start": v(-2.88, -13.97) * mm, "end": v(-2.88, -13.96) * mm});
            skLineSegment(sketch, "E791", {"start": v(-2.88, -13.96) * mm, "end": v(-2.88, -13.95) * mm});
            skLineSegment(sketch, "E792", {"start": v(-2.88, -13.95) * mm, "end": v(-2.88, -13.94) * mm});
            skLineSegment(sketch, "E793", {"start": v(-2.88, -13.94) * mm, "end": v(-2.88, -13.93) * mm});
            skLineSegment(sketch, "E794", {"start": v(-2.88, -13.93) * mm, "end": v(-2.88, -13.92) * mm});
            skLineSegment(sketch, "E795", {"start": v(-2.88, -13.92) * mm, "end": v(-2.89, -13.92) * mm});
            skLineSegment(sketch, "E796", {"start": v(-2.89, -13.92) * mm, "end": v(-2.89, -13.9) * mm});
            skLineSegment(sketch, "E797", {"start": v(-2.89, -13.9) * mm, "end": v(-2.89, -13.9) * mm});
            skLineSegment(sketch, "E798", {"start": v(-2.89, -13.9) * mm, "end": v(-2.89, -13.88) * mm});
            skLineSegment(sketch, "E799", {"start": v(-2.89, -13.88) * mm, "end": v(-2.89, -13.87) * mm});
            skLineSegment(sketch, "E800", {"start": v(-2.89, -13.87) * mm, "end": v(-2.9, -13.86) * mm});
            skLineSegment(sketch, "E801", {"start": v(-2.9, -13.86) * mm, "end": v(-2.9, -13.86) * mm});
            skLineSegment(sketch, "E802", {"start": v(-2.9, -13.86) * mm, "end": v(-2.9, -13.85) * mm});
            skLineSegment(sketch, "E803", {"start": v(-2.9, -13.85) * mm, "end": v(-2.9, -13.84) * mm});
            skLineSegment(sketch, "E804", {"start": v(-2.9, -13.84) * mm, "end": v(-2.9, -13.83) * mm});
            skLineSegment(sketch, "E805", {"start": v(-2.9, -13.83) * mm, "end": v(-2.9, -13.82) * mm});
            skLineSegment(sketch, "E806", {"start": v(-2.9, -13.82) * mm, "end": v(-2.9, -13.81) * mm});
            skLineSegment(sketch, "E807", {"start": v(-2.9, -13.81) * mm, "end": v(-2.9, -13.8) * mm});
            skLineSegment(sketch, "E808", {"start": v(-2.9, -13.8) * mm, "end": v(-2.9, -13.8) * mm});
            skLineSegment(sketch, "E809", {"start": v(-2.9, -13.8) * mm, "end": v(-2.9, -13.78) * mm});
            skLineSegment(sketch, "E810", {"start": v(-2.9, -13.78) * mm, "end": v(-2.9, -13.77) * mm});
            skLineSegment(sketch, "E811", {"start": v(-2.9, -13.77) * mm, "end": v(-2.9, -13.77) * mm});
            skLineSegment(sketch, "E812", {"start": v(-2.9, -13.77) * mm, "end": v(-2.9, -13.76) * mm});
            skLineSegment(sketch, "E813", {"start": v(-2.9, -13.76) * mm, "end": v(-2.9, -13.75) * mm});
            skLineSegment(sketch, "E814", {"start": v(-2.9, -13.75) * mm, "end": v(-2.9, -13.74) * mm});
            skLineSegment(sketch, "E815", {"start": v(-2.9, -13.74) * mm, "end": v(-2.9, -13.73) * mm});
            skLineSegment(sketch, "E816", {"start": v(-2.9, -13.73) * mm, "end": v(-2.9, -13.72) * mm});
            skLineSegment(sketch, "E817", {"start": v(-2.9, -13.72) * mm, "end": v(-2.9, -13.71) * mm});
            skLineSegment(sketch, "E818", {"start": v(-2.9, -13.71) * mm, "end": v(-2.9, -13.7) * mm});
            skLineSegment(sketch, "E819", {"start": v(-2.9, -13.7) * mm, "end": v(-2.9, -13.7) * mm});
            skLineSegment(sketch, "E820", {"start": v(-2.9, -13.7) * mm, "end": v(-2.9, -13.68) * mm});
            skLineSegment(sketch, "E821", {"start": v(-2.9, -13.68) * mm, "end": v(-2.9, -13.67) * mm});
            skLineSegment(sketch, "E822", {"start": v(-2.9, -13.67) * mm, "end": v(-2.9, -13.66) * mm});
            skLineSegment(sketch, "E823", {"start": v(-2.9, -13.66) * mm, "end": v(-2.9, -13.66) * mm});
            skLineSegment(sketch, "E824", {"start": v(-2.9, -13.66) * mm, "end": v(-2.9, -13.65) * mm});
            skLineSegment(sketch, "E825", {"start": v(-2.9, -13.65) * mm, "end": v(-2.9, -13.64) * mm});
            skLineSegment(sketch, "E826", {"start": v(-2.9, -13.64) * mm, "end": v(-2.9, -13.63) * mm});
            skLineSegment(sketch, "E827", {"start": v(-2.9, -13.63) * mm, "end": v(-2.9, -13.62) * mm});
            skLineSegment(sketch, "E828", {"start": v(-2.9, -13.62) * mm, "end": v(-2.9, -13.6) * mm});
            skLineSegment(sketch, "E829", {"start": v(-2.9, -13.6) * mm, "end": v(-2.9, -13.6) * mm});
            skLineSegment(sketch, "E830", {"start": v(-2.9, -13.6) * mm, "end": v(-2.9, -13.59) * mm});
            skLineSegment(sketch, "E831", {"start": v(-2.9, -13.59) * mm, "end": v(-2.9, -13.58) * mm});
            skLineSegment(sketch, "E832", {"start": v(-2.9, -13.58) * mm, "end": v(-2.9, -13.57) * mm});
            skLineSegment(sketch, "E833", {"start": v(-2.9, -13.57) * mm, "end": v(-2.9, -13.56) * mm});
            skLineSegment(sketch, "E834", {"start": v(-2.9, -13.56) * mm, "end": v(-2.9, -13.55) * mm});
            skLineSegment(sketch, "E835", {"start": v(-2.9, -13.55) * mm, "end": v(-2.9, -13.54) * mm});
            skLineSegment(sketch, "E836", {"start": v(-2.9, -13.54) * mm, "end": v(-2.9, -13.53) * mm});
            skLineSegment(sketch, "E837", {"start": v(-2.9, -13.53) * mm, "end": v(-2.9, -13.52) * mm});
            skLineSegment(sketch, "E838", {"start": v(-2.9, -13.52) * mm, "end": v(-2.9, -13.51) * mm});
            skLineSegment(sketch, "E839", {"start": v(-2.9, -13.51) * mm, "end": v(-2.9, -13.5) * mm});
            skLineSegment(sketch, "E840", {"start": v(-2.9, -13.5) * mm, "end": v(-2.9, -13.5) * mm});
            skLineSegment(sketch, "E841", {"start": v(-2.9, -13.5) * mm, "end": v(-2.9, -13.49) * mm});
            skLineSegment(sketch, "E842", {"start": v(-2.9, -13.49) * mm, "end": v(-2.89, -13.48) * mm});
            skLineSegment(sketch, "E843", {"start": v(-2.89, -13.48) * mm, "end": v(-2.89, -13.47) * mm});
            skLineSegment(sketch, "E844", {"start": v(-2.89, -13.47) * mm, "end": v(-2.89, -13.46) * mm});
            skLineSegment(sketch, "E845", {"start": v(-2.89, -13.46) * mm, "end": v(-2.89, -13.45) * mm});
            skLineSegment(sketch, "E846", {"start": v(-2.89, -13.45) * mm, "end": v(-2.89, -13.44) * mm});
            skLineSegment(sketch, "E847", {"start": v(-2.89, -13.44) * mm, "end": v(-2.88, -13.43) * mm});
            skLineSegment(sketch, "E848", {"start": v(-2.88, -13.43) * mm, "end": v(-2.88, -13.42) * mm});
            skLineSegment(sketch, "E849", {"start": v(-2.88, -13.42) * mm, "end": v(-2.88, -13.4) * mm});
            skLineSegment(sketch, "E850", {"start": v(-2.88, -13.4) * mm, "end": v(-2.88, -13.4) * mm});
            skLineSegment(sketch, "E851", {"start": v(-2.88, -13.4) * mm, "end": v(-2.88, -13.39) * mm});
            skLineSegment(sketch, "E852", {"start": v(-2.88, -13.39) * mm, "end": v(-2.88, -13.38) * mm});
            skLineSegment(sketch, "E853", {"start": v(-2.88, -13.38) * mm, "end": v(-2.88, -13.37) * mm});
            skLineSegment(sketch, "E854", {"start": v(-2.88, -13.37) * mm, "end": v(-2.88, -13.36) * mm});
            skLineSegment(sketch, "E855", {"start": v(-2.88, -13.36) * mm, "end": v(-2.87, -13.35) * mm});
            skLineSegment(sketch, "E856", {"start": v(-2.87, -13.35) * mm, "end": v(-2.87, -13.34) * mm});
            skLineSegment(sketch, "E857", {"start": v(-2.87, -13.34) * mm, "end": v(-2.87, -13.33) * mm});
            skLineSegment(sketch, "E858", {"start": v(-2.87, -13.33) * mm, "end": v(-2.87, -13.32) * mm});
            skLineSegment(sketch, "E859", {"start": v(-2.87, -13.32) * mm, "end": v(-2.87, -13.31) * mm});
            skLineSegment(sketch, "E860", {"start": v(-2.87, -13.31) * mm, "end": v(-2.87, -13.3) * mm});
            skLineSegment(sketch, "E861", {"start": v(-2.87, -13.3) * mm, "end": v(-2.86, -13.3) * mm});
            skLineSegment(sketch, "E862", {"start": v(-2.86, -13.3) * mm, "end": v(-2.86, -13.28) * mm});
            skLineSegment(sketch, "E863", {"start": v(-2.86, -13.28) * mm, "end": v(-2.86, -13.27) * mm});
            skLineSegment(sketch, "E864", {"start": v(-2.86, -13.27) * mm, "end": v(-2.86, -13.26) * mm});
            skLineSegment(sketch, "E865", {"start": v(-2.86, -13.26) * mm, "end": v(-2.86, -13.25) * mm});
            skLineSegment(sketch, "E866", {"start": v(-2.86, -13.25) * mm, "end": v(-2.85, -13.24) * mm});
            skLineSegment(sketch, "E867", {"start": v(-2.85, -13.24) * mm, "end": v(-2.85, -13.23) * mm});
            skLineSegment(sketch, "E868", {"start": v(-2.85, -13.23) * mm, "end": v(-2.85, -13.22) * mm});
            skLineSegment(sketch, "E869", {"start": v(-2.85, -13.22) * mm, "end": v(-2.85, -13.21) * mm});
            skLineSegment(sketch, "E870", {"start": v(-2.85, -13.21) * mm, "end": v(-2.85, -13.2) * mm});
            skLineSegment(sketch, "E871", {"start": v(-2.85, -13.2) * mm, "end": v(-2.84, -13.2) * mm});
            skLineSegment(sketch, "E872", {"start": v(-2.84, -13.2) * mm, "end": v(-2.84, -13.18) * mm});
            skLineSegment(sketch, "E873", {"start": v(-2.84, -13.18) * mm, "end": v(-2.84, -13.17) * mm});
            skLineSegment(sketch, "E874", {"start": v(-2.84, -13.17) * mm, "end": v(-2.84, -13.16) * mm});
            skLineSegment(sketch, "E875", {"start": v(-2.84, -13.16) * mm, "end": v(-2.83, -13.15) * mm});
            skLineSegment(sketch, "E876", {"start": v(-2.83, -13.15) * mm, "end": v(-2.83, -13.14) * mm});
            skLineSegment(sketch, "E877", {"start": v(-2.83, -13.14) * mm, "end": v(-2.83, -13.13) * mm});
            skLineSegment(sketch, "E878", {"start": v(-2.83, -13.13) * mm, "end": v(-2.83, -13.12) * mm});
            skLineSegment(sketch, "E879", {"start": v(-2.83, -13.12) * mm, "end": v(-2.82, -13.11) * mm});
            skLineSegment(sketch, "E880", {"start": v(-2.82, -13.11) * mm, "end": v(-2.82, -13.1) * mm});
            skLineSegment(sketch, "E881", {"start": v(-2.82, -13.1) * mm, "end": v(-2.82, -13.1) * mm});
            skLineSegment(sketch, "E882", {"start": v(-2.82, -13.1) * mm, "end": v(-2.81, -13.08) * mm});
            skLineSegment(sketch, "E883", {"start": v(-2.81, -13.08) * mm, "end": v(-2.81, -13.07) * mm});
            skLineSegment(sketch, "E884", {"start": v(-2.81, -13.07) * mm, "end": v(-2.8, -13.06) * mm});
            skLineSegment(sketch, "E885", {"start": v(-2.8, -13.06) * mm, "end": v(-2.8, -13.05) * mm});
            skLineSegment(sketch, "E886", {"start": v(-2.8, -13.05) * mm, "end": v(-2.8, -13.04) * mm});
            skLineSegment(sketch, "E887", {"start": v(-2.8, -13.04) * mm, "end": v(-2.8, -13.03) * mm});
            skLineSegment(sketch, "E888", {"start": v(-2.8, -13.03) * mm, "end": v(-2.8, -13.02) * mm});
            skLineSegment(sketch, "E889", {"start": v(-2.8, -13.02) * mm, "end": v(-2.8, -13.01) * mm});
            skLineSegment(sketch, "E890", {"start": v(-2.8, -13.01) * mm, "end": v(-2.79, -13) * mm});
            skLineSegment(sketch, "E891", {"start": v(-2.79, -13) * mm, "end": v(-2.79, -13) * mm});
            skLineSegment(sketch, "E892", {"start": v(-2.79, -13) * mm, "end": v(-2.78, -12.98) * mm});
            skLineSegment(sketch, "E893", {"start": v(-2.78, -12.98) * mm, "end": v(-2.78, -12.97) * mm});
            skLineSegment(sketch, "E894", {"start": v(-2.78, -12.97) * mm, "end": v(-2.76, -12.92) * mm});
            skLineSegment(sketch, "E895", {"start": v(-2.76, -12.92) * mm, "end": v(-2.73, -12.86) * mm});
            skLineSegment(sketch, "E896", {"start": v(-2.73, -12.86) * mm, "end": v(-2.71, -12.8) * mm});
            skLineSegment(sketch, "E897", {"start": v(-2.71, -12.8) * mm, "end": v(-2.69, -12.74) * mm});
            skLineSegment(sketch, "E898", {"start": v(-2.69, -12.74) * mm, "end": v(-2.67, -12.68) * mm});
            skLineSegment(sketch, "E899", {"start": v(-2.67, -12.68) * mm, "end": v(-2.64, -12.62) * mm});
            skLineSegment(sketch, "E900", {"start": v(-2.64, -12.62) * mm, "end": v(-2.62, -12.57) * mm});
            skLineSegment(sketch, "E901", {"start": v(-2.62, -12.57) * mm, "end": v(-2.6, -12.5) * mm});
            skLineSegment(sketch, "E902", {"start": v(-2.6, -12.5) * mm, "end": v(-2.57, -12.45) * mm});
            skLineSegment(sketch, "E903", {"start": v(-2.57, -12.45) * mm, "end": v(-2.55, -12.4) * mm});
            skLineSegment(sketch, "E904", {"start": v(-2.55, -12.4) * mm, "end": v(-2.53, -12.33) * mm});
            skLineSegment(sketch, "E905", {"start": v(-2.53, -12.33) * mm, "end": v(-2.5, -12.28) * mm});
            skLineSegment(sketch, "E906", {"start": v(-2.5, -12.28) * mm, "end": v(-2.48, -12.22) * mm});
            skLineSegment(sketch, "E907", {"start": v(-2.48, -12.22) * mm, "end": v(-2.46, -12.16) * mm});
            skLineSegment(sketch, "E908", {"start": v(-2.46, -12.16) * mm, "end": v(-2.43, -12.1) * mm});
            skLineSegment(sketch, "E909", {"start": v(-2.43, -12.1) * mm, "end": v(-2.4, -12.04) * mm});
            skLineSegment(sketch, "E910", {"start": v(-2.4, -12.04) * mm, "end": v(-2.38, -11.99) * mm});
            skLineSegment(sketch, "E911", {"start": v(-2.38, -11.99) * mm, "end": v(-2.36, -11.93) * mm});
            skLineSegment(sketch, "E912", {"start": v(-2.36, -11.93) * mm, "end": v(-2.33, -11.87) * mm});
            skLineSegment(sketch, "E913", {"start": v(-2.33, -11.87) * mm, "end": v(-2.3, -11.81) * mm});
            skLineSegment(sketch, "E914", {"start": v(-2.3, -11.81) * mm, "end": v(-2.28, -11.76) * mm});
            skLineSegment(sketch, "E915", {"start": v(-2.28, -11.76) * mm, "end": v(-2.26, -11.7) * mm});
            skLineSegment(sketch, "E916", {"start": v(-2.26, -11.7) * mm, "end": v(-2.23, -11.64) * mm});
            skLineSegment(sketch, "E917", {"start": v(-2.23, -11.64) * mm, "end": v(-2.2, -11.58) * mm});
            skLineSegment(sketch, "E918", {"start": v(-2.2, -11.58) * mm, "end": v(-2.18, -11.53) * mm});
            skLineSegment(sketch, "E919", {"start": v(-2.18, -11.53) * mm, "end": v(-2.15, -11.47) * mm});
            skLineSegment(sketch, "E920", {"start": v(-2.15, -11.47) * mm, "end": v(-2.13, -11.41) * mm});
            skLineSegment(sketch, "E921", {"start": v(-2.13, -11.41) * mm, "end": v(-2.1, -11.35) * mm});
            skLineSegment(sketch, "E922", {"start": v(-2.1, -11.35) * mm, "end": v(-2.08, -11.3) * mm});
            skLineSegment(sketch, "E923", {"start": v(-2.08, -11.3) * mm, "end": v(-2.05, -11.24) * mm});
            skLineSegment(sketch, "E924", {"start": v(-2.05, -11.24) * mm, "end": v(-2.02, -11.18) * mm});
            skLineSegment(sketch, "E925", {"start": v(-2.02, -11.18) * mm, "end": v(-2, -11.13) * mm});
            skLineSegment(sketch, "E926", {"start": v(-2, -11.13) * mm, "end": v(-1.97, -11.07) * mm});
            skLineSegment(sketch, "E927", {"start": v(-1.97, -11.07) * mm, "end": v(-1.94, -11.01) * mm});
            skLineSegment(sketch, "E928", {"start": v(-1.94, -11.01) * mm, "end": v(-1.91, -10.95) * mm});
            skLineSegment(sketch, "E929", {"start": v(-1.91, -10.95) * mm, "end": v(-1.89, -10.9) * mm});
            skLineSegment(sketch, "E930", {"start": v(-1.89, -10.9) * mm, "end": v(-1.86, -10.84) * mm});
            skLineSegment(sketch, "E931", {"start": v(-1.86, -10.84) * mm, "end": v(-1.83, -10.78) * mm});
            skLineSegment(sketch, "E932", {"start": v(-1.83, -10.78) * mm, "end": v(-1.8, -10.73) * mm});
            skLineSegment(sketch, "E933", {"start": v(-1.8, -10.73) * mm, "end": v(-1.78, -10.67) * mm});
            skLineSegment(sketch, "E934", {"start": v(-1.78, -10.67) * mm, "end": v(-1.75, -10.61) * mm});
            skLineSegment(sketch, "E935", {"start": v(-1.75, -10.61) * mm, "end": v(-1.72, -10.56) * mm});
            skLineSegment(sketch, "E936", {"start": v(-1.72, -10.56) * mm, "end": v(-1.7, -10.5) * mm});
            skLineSegment(sketch, "E937", {"start": v(-1.7, -10.5) * mm, "end": v(-1.66, -10.44) * mm});
            skLineSegment(sketch, "E938", {"start": v(-1.66, -10.44) * mm, "end": v(-1.64, -10.39) * mm});
            skLineSegment(sketch, "E939", {"start": v(-1.64, -10.39) * mm, "end": v(-1.6, -10.33) * mm});
            skLineSegment(sketch, "E940", {"start": v(-1.6, -10.33) * mm, "end": v(-1.58, -10.27) * mm});
            skLineSegment(sketch, "E941", {"start": v(-1.58, -10.27) * mm, "end": v(-1.55, -10.22) * mm});
            skLineSegment(sketch, "E942", {"start": v(-1.55, -10.22) * mm, "end": v(-1.52, -10.16) * mm});
            skLineSegment(sketch, "E943", {"start": v(-1.52, -10.16) * mm, "end": v(-1.5, -10.1) * mm});
            skLineSegment(sketch, "E944", {"start": v(-1.5, -10.1) * mm, "end": v(-1.46, -10.05) * mm});
            skLineSegment(sketch, "E945", {"start": v(-1.46, -10.05) * mm, "end": v(-1.43, -10) * mm});
            skLineSegment(sketch, "E946", {"start": v(-1.43, -10) * mm, "end": v(-1.4, -9.94) * mm});
            skLineSegment(sketch, "E947", {"start": v(-1.4, -9.94) * mm, "end": v(-1.38, -9.88) * mm});
            skLineSegment(sketch, "E948", {"start": v(-1.38, -9.88) * mm, "end": v(-1.35, -9.83) * mm});
            skLineSegment(sketch, "E949", {"start": v(-1.35, -9.83) * mm, "end": v(-1.32, -9.77) * mm});
            skLineSegment(sketch, "E950", {"start": v(-1.32, -9.77) * mm, "end": v(-1.29, -9.71) * mm});
            skLineSegment(sketch, "E951", {"start": v(-1.29, -9.71) * mm, "end": v(-1.26, -9.66) * mm});
            skLineSegment(sketch, "E952", {"start": v(-1.26, -9.66) * mm, "end": v(-1.23, -9.6) * mm});
            skLineSegment(sketch, "E953", {"start": v(-1.23, -9.6) * mm, "end": v(-1.2, -9.55) * mm});
            skLineSegment(sketch, "E954", {"start": v(-1.2, -9.55) * mm, "end": v(-1.17, -9.5) * mm});
            skLineSegment(sketch, "E955", {"start": v(-1.17, -9.5) * mm, "end": v(-1.14, -9.44) * mm});
            skLineSegment(sketch, "E956", {"start": v(-1.14, -9.44) * mm, "end": v(-1.1, -9.38) * mm});
            skLineSegment(sketch, "E957", {"start": v(-1.1, -9.38) * mm, "end": v(-1.08, -9.33) * mm});
            skLineSegment(sketch, "E958", {"start": v(-1.08, -9.33) * mm, "end": v(-1.05, -9.27) * mm});
            skLineSegment(sketch, "E959", {"start": v(-1.05, -9.27) * mm, "end": v(-1.02, -9.21) * mm});
            skLineSegment(sketch, "E960", {"start": v(-1.02, -9.21) * mm, "end": v(-0.99, -9.16) * mm});
            skLineSegment(sketch, "E961", {"start": v(-0.99, -9.16) * mm, "end": v(-0.96, -9.1) * mm});
            skLineSegment(sketch, "E962", {"start": v(-0.96, -9.1) * mm, "end": v(-0.93, -9.05) * mm});
            skLineSegment(sketch, "E963", {"start": v(-0.93, -9.05) * mm, "end": v(-0.9, -9) * mm});
            skLineSegment(sketch, "E964", {"start": v(-0.9, -9) * mm, "end": v(-0.86, -8.94) * mm});
            skLineSegment(sketch, "E965", {"start": v(-0.86, -8.94) * mm, "end": v(-0.83, -8.88) * mm});
            skLineSegment(sketch, "E966", {"start": v(-0.83, -8.88) * mm, "end": v(-0.8, -8.83) * mm});
            skLineSegment(sketch, "E967", {"start": v(-0.8, -8.83) * mm, "end": v(-0.77, -8.78) * mm});
            skLineSegment(sketch, "E968", {"start": v(-0.77, -8.78) * mm, "end": v(-0.74, -8.72) * mm});
            skLineSegment(sketch, "E969", {"start": v(-0.74, -8.72) * mm, "end": v(-0.7, -8.67) * mm});
            skLineSegment(sketch, "E970", {"start": v(-0.7, -8.67) * mm, "end": v(-0.68, -8.61) * mm});
            skLineSegment(sketch, "E971", {"start": v(-0.68, -8.61) * mm, "end": v(-0.65, -8.56) * mm});
            skLineSegment(sketch, "E972", {"start": v(-0.65, -8.56) * mm, "end": v(-0.62, -8.5) * mm});
            skLineSegment(sketch, "E973", {"start": v(-0.62, -8.5) * mm, "end": v(-0.58, -8.45) * mm});
            skLineSegment(sketch, "E974", {"start": v(-0.58, -8.45) * mm, "end": v(-0.55, -8.4) * mm});
            skLineSegment(sketch, "E975", {"start": v(-0.55, -8.4) * mm, "end": v(-0.52, -8.34) * mm});
            skLineSegment(sketch, "E976", {"start": v(-0.52, -8.34) * mm, "end": v(-0.49, -8.29) * mm});
            skLineSegment(sketch, "E977", {"start": v(-0.49, -8.29) * mm, "end": v(-0.46, -8.23) * mm});
            skLineSegment(sketch, "E978", {"start": v(-0.46, -8.23) * mm, "end": v(-0.43, -8.18) * mm});
            skLineSegment(sketch, "E979", {"start": v(-0.43, -8.18) * mm, "end": v(-0.4, -8.12) * mm});
            skLineSegment(sketch, "E980", {"start": v(-0.4, -8.12) * mm, "end": v(-0.36, -8.07) * mm});
            skLineSegment(sketch, "E981", {"start": v(-0.36, -8.07) * mm, "end": v(-0.33, -8.02) * mm});
            skLineSegment(sketch, "E982", {"start": v(-0.33, -8.02) * mm, "end": v(-0.3, -7.96) * mm});
            skLineSegment(sketch, "E983", {"start": v(-0.3, -7.96) * mm, "end": v(-0.27, -7.9) * mm});
            skLineSegment(sketch, "E984", {"start": v(-0.27, -7.9) * mm, "end": v(-0.24, -7.86) * mm});
            skLineSegment(sketch, "E985", {"start": v(-0.24, -7.86) * mm, "end": v(-0.2, -7.8) * mm});
            skLineSegment(sketch, "E986", {"start": v(-0.2, -7.8) * mm, "end": v(-0.17, -7.75) * mm});
            skLineSegment(sketch, "E987", {"start": v(-0.17, -7.75) * mm, "end": v(-0.14, -7.7) * mm});
            skLineSegment(sketch, "E988", {"start": v(-0.14, -7.7) * mm, "end": v(-0.1, -7.64) * mm});
            skLineSegment(sketch, "E989", {"start": v(-0.1, -7.64) * mm, "end": v(-0.07, -7.59) * mm});
            skLineSegment(sketch, "E990", {"start": v(-0.07, -7.59) * mm, "end": v(-0.04, -7.54) * mm});
            skLineSegment(sketch, "E991", {"start": v(-0.04, -7.54) * mm, "end": v(-0.01, -7.48) * mm});
            skLineSegment(sketch, "E992", {"start": v(-0.01, -7.48) * mm, "end": v(0.02, -7.43) * mm});
            skLineSegment(sketch, "E993", {"start": v(0.02, -7.43) * mm, "end": v(0.05, -7.38) * mm});
            skLineSegment(sketch, "E994", {"start": v(0.05, -7.38) * mm, "end": v(0.09, -7.33) * mm});
            skLineSegment(sketch, "E995", {"start": v(0.09, -7.33) * mm, "end": v(0.12, -7.27) * mm});
            skLineSegment(sketch, "E996", {"start": v(0.12, -7.27) * mm, "end": v(0.15, -7.22) * mm});
            skLineSegment(sketch, "E997", {"start": v(0.15, -7.22) * mm, "end": v(0.18, -7.17) * mm});
            skLineSegment(sketch, "E998", {"start": v(0.18, -7.17) * mm, "end": v(0.22, -7.11) * mm});
            skLineSegment(sketch, "E999", {"start": v(0.22, -7.11) * mm, "end": v(0.25, -7.06) * mm});
            skLineSegment(sketch, "E1000", {"start": v(0.25, -7.06) * mm, "end": v(0.28, -7.01) * mm});
            skLineSegment(sketch, "E1001", {"start": v(0.28, -7.01) * mm, "end": v(0.31, -6.96) * mm});
            skLineSegment(sketch, "E1002", {"start": v(0.31, -6.96) * mm, "end": v(0.35, -6.9) * mm});
            skLineSegment(sketch, "E1003", {"start": v(0.35, -6.9) * mm, "end": v(0.38, -6.85) * mm});
            skLineSegment(sketch, "E1004", {"start": v(0.38, -6.85) * mm, "end": v(0.41, -6.8) * mm});
            skLineSegment(sketch, "E1005", {"start": v(0.41, -6.8) * mm, "end": v(0.44, -6.75) * mm});
            skLineSegment(sketch, "E1006", {"start": v(0.44, -6.75) * mm, "end": v(0.48, -6.7) * mm});
            skLineSegment(sketch, "E1007", {"start": v(0.48, -6.7) * mm, "end": v(0.5, -6.65) * mm});
            skLineSegment(sketch, "E1008", {"start": v(0.5, -6.65) * mm, "end": v(0.54, -6.6) * mm});
            skLineSegment(sketch, "E1009", {"start": v(0.54, -6.6) * mm, "end": v(0.57, -6.54) * mm});
            skLineSegment(sketch, "E1010", {"start": v(0.57, -6.54) * mm, "end": v(0.6, -6.5) * mm});
            skLineSegment(sketch, "E1011", {"start": v(0.6, -6.5) * mm, "end": v(0.64, -6.44) * mm});
            skLineSegment(sketch, "E1012", {"start": v(0.64, -6.44) * mm, "end": v(0.67, -6.4) * mm});
            skLineSegment(sketch, "E1013", {"start": v(0.67, -6.4) * mm, "end": v(0.7, -6.34) * mm});
            skLineSegment(sketch, "E1014", {"start": v(0.7, -6.34) * mm, "end": v(0.74, -6.29) * mm});
            skLineSegment(sketch, "E1015", {"start": v(0.74, -6.29) * mm, "end": v(0.77, -6.24) * mm});
            skLineSegment(sketch, "E1016", {"start": v(0.77, -6.24) * mm, "end": v(0.8, -6.19) * mm});
            skLineSegment(sketch, "E1017", {"start": v(0.8, -6.19) * mm, "end": v(0.83, -6.14) * mm});
            skLineSegment(sketch, "E1018", {"start": v(0.83, -6.14) * mm, "end": v(0.87, -6.08) * mm});
            skLineSegment(sketch, "E1019", {"start": v(0.87, -6.08) * mm, "end": v(0.9, -6.03) * mm});
            skLineSegment(sketch, "E1020", {"start": v(0.9, -6.03) * mm, "end": v(0.93, -5.98) * mm});
            skLineSegment(sketch, "E1021", {"start": v(0.93, -5.98) * mm, "end": v(0.96, -5.93) * mm});
            skLineSegment(sketch, "E1022", {"start": v(0.96, -5.93) * mm, "end": v(0.97, -5.93) * mm});
            skLineSegment(sketch, "E1023", {"start": v(0.97, -5.93) * mm, "end": v(0.97, -5.92) * mm});
            skLineSegment(sketch, "E1024", {"start": v(0.97, -5.92) * mm, "end": v(0.97, -5.92) * mm});
            skLineSegment(sketch, "E1025", {"start": v(0.97, -5.92) * mm, "end": v(0.98, -5.91) * mm});
            skLineSegment(sketch, "E1026", {"start": v(0.98, -5.91) * mm, "end": v(0.98, -5.9) * mm});
            skLineSegment(sketch, "E1027", {"start": v(0.98, -5.9) * mm, "end": v(0.98, -5.9) * mm});
            skLineSegment(sketch, "E1028", {"start": v(0.98, -5.9) * mm, "end": v(0.99, -5.9) * mm});
            skLineSegment(sketch, "E1029", {"start": v(0.99, -5.9) * mm, "end": v(0.99, -5.9) * mm});
            skLineSegment(sketch, "E1030", {"start": v(0.99, -5.9) * mm, "end": v(1, -5.89) * mm});
            skLineSegment(sketch, "E1031", {"start": v(1, -5.89) * mm, "end": v(1, -5.89) * mm});
            skLineSegment(sketch, "E1032", {"start": v(1, -5.89) * mm, "end": v(1, -5.88) * mm});
            skLineSegment(sketch, "E1033", {"start": v(1, -5.88) * mm, "end": v(1, -5.88) * mm});
            skLineSegment(sketch, "E1034", {"start": v(1, -5.88) * mm, "end": v(1, -5.87) * mm});
            skLineSegment(sketch, "E1035", {"start": v(1, -5.87) * mm, "end": v(1, -5.87) * mm});
            skLineSegment(sketch, "E1036", {"start": v(1, -5.87) * mm, "end": v(1, -5.86) * mm});
            skLineSegment(sketch, "E1037", {"start": v(1, -5.86) * mm, "end": v(1.01, -5.86) * mm});
            skLineSegment(sketch, "E1038", {"start": v(1.01, -5.86) * mm, "end": v(1.01, -5.85) * mm});
            skLineSegment(sketch, "E1039", {"start": v(1.01, -5.85) * mm, "end": v(1.02, -5.85) * mm});
            skLineSegment(sketch, "E1040", {"start": v(1.02, -5.85) * mm, "end": v(1.02, -5.85) * mm});
            skLineSegment(sketch, "E1041", {"start": v(1.02, -5.85) * mm, "end": v(1.02, -5.84) * mm});
            skLineSegment(sketch, "E1042", {"start": v(1.02, -5.84) * mm, "end": v(1.03, -5.84) * mm});
            skLineSegment(sketch, "E1043", {"start": v(1.03, -5.84) * mm, "end": v(1.03, -5.83) * mm});
            skLineSegment(sketch, "E1044", {"start": v(1.03, -5.83) * mm, "end": v(1.03, -5.83) * mm});
            skLineSegment(sketch, "E1045", {"start": v(1.03, -5.83) * mm, "end": v(1.03, -5.82) * mm});
            skLineSegment(sketch, "E1046", {"start": v(1.03, -5.82) * mm, "end": v(1.04, -5.82) * mm});
            skLineSegment(sketch, "E1047", {"start": v(1.04, -5.82) * mm, "end": v(1.04, -5.81) * mm});
            skLineSegment(sketch, "E1048", {"start": v(1.04, -5.81) * mm, "end": v(1.04, -5.81) * mm});
            skLineSegment(sketch, "E1049", {"start": v(1.04, -5.81) * mm, "end": v(1.04, -5.8) * mm});
            skLineSegment(sketch, "E1050", {"start": v(1.04, -5.8) * mm, "end": v(1.05, -5.8) * mm});
            skLineSegment(sketch, "E1051", {"start": v(1.05, -5.8) * mm, "end": v(1.05, -5.8) * mm});
            skLineSegment(sketch, "E1052", {"start": v(1.05, -5.8) * mm, "end": v(1.06, -5.79) * mm});
            skLineSegment(sketch, "E1053", {"start": v(1.06, -5.79) * mm, "end": v(1.06, -5.78) * mm});
            skLineSegment(sketch, "E1054", {"start": v(1.06, -5.78) * mm, "end": v(1.06, -5.78) * mm});
            skLineSegment(sketch, "E1055", {"start": v(1.06, -5.78) * mm, "end": v(1.07, -5.77) * mm});
            skLineSegment(sketch, "E1056", {"start": v(1.07, -5.77) * mm, "end": v(1.07, -5.77) * mm});
            skLineSegment(sketch, "E1057", {"start": v(1.07, -5.77) * mm, "end": v(1.07, -5.76) * mm});
            skLineSegment(sketch, "E1058", {"start": v(1.07, -5.76) * mm, "end": v(1.08, -5.76) * mm});
            skLineSegment(sketch, "E1059", {"start": v(1.08, -5.76) * mm, "end": v(1.08, -5.75) * mm});
            skLineSegment(sketch, "E1060", {"start": v(1.08, -5.75) * mm, "end": v(1.08, -5.75) * mm});
            skLineSegment(sketch, "E1061", {"start": v(1.08, -5.75) * mm, "end": v(1.08, -5.74) * mm});
            skLineSegment(sketch, "E1062", {"start": v(1.08, -5.74) * mm, "end": v(1.09, -5.74) * mm});
            skLineSegment(sketch, "E1063", {"start": v(1.09, -5.74) * mm, "end": v(1.09, -5.74) * mm});
            skLineSegment(sketch, "E1064", {"start": v(1.09, -5.74) * mm, "end": v(1.1, -5.73) * mm});
            skLineSegment(sketch, "E1065", {"start": v(1.1, -5.73) * mm, "end": v(1.1, -5.73) * mm});
            skLineSegment(sketch, "E1066", {"start": v(1.1, -5.73) * mm, "end": v(1.1, -5.72) * mm});
            skLineSegment(sketch, "E1067", {"start": v(1.1, -5.72) * mm, "end": v(1.1, -5.72) * mm});
            skLineSegment(sketch, "E1068", {"start": v(1.1, -5.72) * mm, "end": v(1.1, -5.71) * mm});
            skLineSegment(sketch, "E1069", {"start": v(1.1, -5.71) * mm, "end": v(1.1, -5.7) * mm});
            skLineSegment(sketch, "E1070", {"start": v(1.1, -5.7) * mm, "end": v(1.1, -5.7) * mm});
            skLineSegment(sketch, "E1071", {"start": v(1.1, -5.7) * mm, "end": v(1.11, -5.7) * mm});
            skLineSegment(sketch, "E1072", {"start": v(1.11, -5.7) * mm, "end": v(1.12, -5.7) * mm});
            skLineSegment(sketch, "E1073", {"start": v(1.12, -5.7) * mm, "end": v(1.12, -5.7) * mm});
            skLineSegment(sketch, "E1074", {"start": v(1.12, -5.7) * mm, "end": v(1.12, -5.69) * mm});
            skLineSegment(sketch, "E1075", {"start": v(1.12, -5.69) * mm, "end": v(1.12, -5.68) * mm});
            skLineSegment(sketch, "E1076", {"start": v(1.12, -5.68) * mm, "end": v(1.13, -5.68) * mm});
            skLineSegment(sketch, "E1077", {"start": v(1.13, -5.68) * mm, "end": v(1.13, -5.67) * mm});
            skLineSegment(sketch, "E1078", {"start": v(1.13, -5.67) * mm, "end": v(1.13, -5.67) * mm});
            skLineSegment(sketch, "E1079", {"start": v(1.13, -5.67) * mm, "end": v(1.14, -5.67) * mm});
            skLineSegment(sketch, "E1080", {"start": v(1.14, -5.67) * mm, "end": v(1.14, -5.66) * mm});
            skLineSegment(sketch, "E1081", {"start": v(1.14, -5.66) * mm, "end": v(1.14, -5.66) * mm});
            skLineSegment(sketch, "E1082", {"start": v(1.14, -5.66) * mm, "end": v(1.14, -5.65) * mm});
            skLineSegment(sketch, "E1083", {"start": v(1.14, -5.65) * mm, "end": v(1.15, -5.65) * mm});
            skLineSegment(sketch, "E1084", {"start": v(1.15, -5.65) * mm, "end": v(1.15, -5.64) * mm});
            skLineSegment(sketch, "E1085", {"start": v(1.15, -5.64) * mm, "end": v(1.15, -5.64) * mm});
            skLineSegment(sketch, "E1086", {"start": v(1.15, -5.64) * mm, "end": v(1.16, -5.63) * mm});
            skLineSegment(sketch, "E1087", {"start": v(1.16, -5.63) * mm, "end": v(1.16, -5.63) * mm});
            skLineSegment(sketch, "E1088", {"start": v(1.16, -5.63) * mm, "end": v(1.16, -5.62) * mm});
            skLineSegment(sketch, "E1089", {"start": v(1.16, -5.62) * mm, "end": v(1.17, -5.62) * mm});
            skLineSegment(sketch, "E1090", {"start": v(1.17, -5.62) * mm, "end": v(1.17, -5.61) * mm});
            skLineSegment(sketch, "E1091", {"start": v(1.17, -5.61) * mm, "end": v(1.17, -5.6) * mm});
            skLineSegment(sketch, "E1092", {"start": v(1.17, -5.6) * mm, "end": v(1.17, -5.6) * mm});
            skLineSegment(sketch, "E1093", {"start": v(1.17, -5.6) * mm, "end": v(1.18, -5.6) * mm});
            skLineSegment(sketch, "E1094", {"start": v(1.18, -5.6) * mm, "end": v(1.18, -5.6) * mm});
            skLineSegment(sketch, "E1095", {"start": v(1.18, -5.6) * mm, "end": v(1.19, -5.59) * mm});
            skLineSegment(sketch, "E1096", {"start": v(1.19, -5.59) * mm, "end": v(1.19, -5.58) * mm});
            skLineSegment(sketch, "E1097", {"start": v(1.19, -5.58) * mm, "end": v(1.2, -5.58) * mm});
            skLineSegment(sketch, "E1098", {"start": v(1.2, -5.58) * mm, "end": v(1.2, -5.57) * mm});
            skLineSegment(sketch, "E1099", {"start": v(1.2, -5.57) * mm, "end": v(1.2, -5.57) * mm});
            skLineSegment(sketch, "E1100", {"start": v(1.2, -5.57) * mm, "end": v(1.2, -5.56) * mm});
            skLineSegment(sketch, "E1101", {"start": v(1.2, -5.56) * mm, "end": v(1.2, -5.56) * mm});
            skLineSegment(sketch, "E1102", {"start": v(1.2, -5.56) * mm, "end": v(1.2, -5.55) * mm});
            skLineSegment(sketch, "E1103", {"start": v(1.2, -5.55) * mm, "end": v(1.21, -5.55) * mm});
            skLineSegment(sketch, "E1104", {"start": v(1.21, -5.55) * mm, "end": v(1.21, -5.54) * mm});
            skLineSegment(sketch, "E1105", {"start": v(1.21, -5.54) * mm, "end": v(1.22, -5.54) * mm});
            skLineSegment(sketch, "E1106", {"start": v(1.22, -5.54) * mm, "end": v(1.22, -5.53) * mm});
            skLineSegment(sketch, "E1107", {"start": v(1.22, -5.53) * mm, "end": v(1.22, -5.53) * mm});
            skLineSegment(sketch, "E1108", {"start": v(1.22, -5.53) * mm, "end": v(1.23, -5.53) * mm});
            skLineSegment(sketch, "E1109", {"start": v(1.23, -5.53) * mm, "end": v(1.23, -5.52) * mm});
            skLineSegment(sketch, "E1110", {"start": v(1.23, -5.52) * mm, "end": v(1.23, -5.52) * mm});
            skLineSegment(sketch, "E1111", {"start": v(1.23, -5.52) * mm, "end": v(1.23, -5.51) * mm});
            skLineSegment(sketch, "E1112", {"start": v(1.23, -5.51) * mm, "end": v(1.24, -5.5) * mm});
            skLineSegment(sketch, "E1113", {"start": v(1.24, -5.5) * mm, "end": v(1.24, -5.5) * mm});
            skLineSegment(sketch, "E1114", {"start": v(1.24, -5.5) * mm, "end": v(1.25, -5.5) * mm});
            skLineSegment(sketch, "E1115", {"start": v(1.25, -5.5) * mm, "end": v(1.25, -5.5) * mm});
            skLineSegment(sketch, "E1116", {"start": v(1.25, -5.5) * mm, "end": v(1.25, -5.49) * mm});
            skLineSegment(sketch, "E1117", {"start": v(1.25, -5.49) * mm, "end": v(1.25, -5.48) * mm});
            skLineSegment(sketch, "E1118", {"start": v(1.25, -5.48) * mm, "end": v(1.26, -5.48) * mm});
            skLineSegment(sketch, "E1119", {"start": v(1.26, -5.48) * mm, "end": v(1.26, -5.47) * mm});
            skLineSegment(sketch, "E1120", {"start": v(1.26, -5.47) * mm, "end": v(1.26, -5.47) * mm});
            skLineSegment(sketch, "E1121", {"start": v(1.26, -5.47) * mm, "end": v(1.26, -5.46) * mm});
            skLineSegment(sketch, "E1122", {"start": v(1.26, -5.46) * mm, "end": v(1.27, -5.46) * mm});
            skLineSegment(sketch, "E1123", {"start": v(1.27, -5.46) * mm, "end": v(1.27, -5.46) * mm});
            skLineSegment(sketch, "E1124", {"start": v(1.27, -5.46) * mm, "end": v(1.27, -5.45) * mm});
            skLineSegment(sketch, "E1125", {"start": v(1.27, -5.45) * mm, "end": v(1.28, -5.45) * mm});
            skLineSegment(sketch, "E1126", {"start": v(1.28, -5.45) * mm, "end": v(1.28, -5.44) * mm});
            skLineSegment(sketch, "E1127", {"start": v(1.28, -5.44) * mm, "end": v(1.28, -5.44) * mm});
            skLineSegment(sketch, "E1128", {"start": v(1.28, -5.44) * mm, "end": v(1.28, -5.43) * mm});
            skLineSegment(sketch, "E1129", {"start": v(1.28, -5.43) * mm, "end": v(1.29, -5.43) * mm});
            skLineSegment(sketch, "E1130", {"start": v(1.29, -5.43) * mm, "end": v(1.3, -5.42) * mm});
            skLineSegment(sketch, "E1131", {"start": v(1.3, -5.42) * mm, "end": v(1.3, -5.42) * mm});
            skLineSegment(sketch, "E1132", {"start": v(1.3, -5.42) * mm, "end": v(1.3, -5.41) * mm});
            skLineSegment(sketch, "E1133", {"start": v(1.3, -5.41) * mm, "end": v(1.3, -5.4) * mm});
            skLineSegment(sketch, "E1134", {"start": v(1.3, -5.4) * mm, "end": v(1.3, -5.4) * mm});
            skLineSegment(sketch, "E1135", {"start": v(1.3, -5.4) * mm, "end": v(1.31, -5.4) * mm});
            skLineSegment(sketch, "E1136", {"start": v(1.31, -5.4) * mm, "end": v(1.31, -5.39) * mm});
            skLineSegment(sketch, "E1137", {"start": v(1.31, -5.39) * mm, "end": v(1.32, -5.39) * mm});
            skLineSegment(sketch, "E1138", {"start": v(1.32, -5.39) * mm, "end": v(1.32, -5.38) * mm});
            skLineSegment(sketch, "E1139", {"start": v(1.32, -5.38) * mm, "end": v(1.32, -5.38) * mm});
            skLineSegment(sketch, "E1140", {"start": v(1.32, -5.38) * mm, "end": v(1.32, -5.37) * mm});
            skLineSegment(sketch, "E1141", {"start": v(1.32, -5.37) * mm, "end": v(1.38, -5.3) * mm});
            skLineSegment(sketch, "E1142", {"start": v(1.38, -5.3) * mm, "end": v(1.43, -5.21) * mm});
            skLineSegment(sketch, "E1143", {"start": v(1.43, -5.21) * mm, "end": v(1.48, -5.13) * mm});
            skLineSegment(sketch, "E1144", {"start": v(1.48, -5.13) * mm, "end": v(1.53, -5.05) * mm});
            skLineSegment(sketch, "E1145", {"start": v(1.53, -5.05) * mm, "end": v(1.58, -4.97) * mm});
            skLineSegment(sketch, "E1146", {"start": v(1.58, -4.97) * mm, "end": v(1.64, -4.9) * mm});
            skLineSegment(sketch, "E1147", {"start": v(1.64, -4.9) * mm, "end": v(1.69, -4.81) * mm});
            skLineSegment(sketch, "E1148", {"start": v(1.69, -4.81) * mm, "end": v(1.74, -4.73) * mm});
            skLineSegment(sketch, "E1149", {"start": v(1.74, -4.73) * mm, "end": v(1.8, -4.65) * mm});
            skLineSegment(sketch, "E1150", {"start": v(1.8, -4.65) * mm, "end": v(1.85, -4.57) * mm});
            skLineSegment(sketch, "E1151", {"start": v(1.85, -4.57) * mm, "end": v(1.9, -4.5) * mm});
            skLineSegment(sketch, "E1152", {"start": v(1.9, -4.5) * mm, "end": v(1.95, -4.42) * mm});
            skLineSegment(sketch, "E1153", {"start": v(1.95, -4.42) * mm, "end": v(2, -4.34) * mm});
            skLineSegment(sketch, "E1154", {"start": v(2, -4.34) * mm, "end": v(2.06, -4.26) * mm});
            skLineSegment(sketch, "E1155", {"start": v(2.06, -4.26) * mm, "end": v(2.11, -4.18) * mm});
            skLineSegment(sketch, "E1156", {"start": v(2.11, -4.18) * mm, "end": v(2.16, -4.1) * mm});
            skLineSegment(sketch, "E1157", {"start": v(2.16, -4.1) * mm, "end": v(2.22, -4.02) * mm});
            skLineSegment(sketch, "E1158", {"start": v(2.22, -4.02) * mm, "end": v(2.27, -3.94) * mm});
            skLineSegment(sketch, "E1159", {"start": v(2.27, -3.94) * mm, "end": v(2.33, -3.86) * mm});
            skLineSegment(sketch, "E1160", {"start": v(2.33, -3.86) * mm, "end": v(2.38, -3.79) * mm});
            skLineSegment(sketch, "E1161", {"start": v(2.38, -3.79) * mm, "end": v(2.43, -3.7) * mm});
            skLineSegment(sketch, "E1162", {"start": v(2.43, -3.7) * mm, "end": v(2.49, -3.63) * mm});
            skLineSegment(sketch, "E1163", {"start": v(2.49, -3.63) * mm, "end": v(2.54, -3.55) * mm});
            skLineSegment(sketch, "E1164", {"start": v(2.54, -3.55) * mm, "end": v(2.6, -3.48) * mm});
            skLineSegment(sketch, "E1165", {"start": v(2.6, -3.48) * mm, "end": v(2.65, -3.4) * mm});
            skLineSegment(sketch, "E1166", {"start": v(2.65, -3.4) * mm, "end": v(2.7, -3.32) * mm});
            skLineSegment(sketch, "E1167", {"start": v(2.7, -3.32) * mm, "end": v(2.76, -3.24) * mm});
            skLineSegment(sketch, "E1168", {"start": v(2.76, -3.24) * mm, "end": v(2.81, -3.17) * mm});
            skLineSegment(sketch, "E1169", {"start": v(2.81, -3.17) * mm, "end": v(2.87, -3.09) * mm});
            skLineSegment(sketch, "E1170", {"start": v(2.87, -3.09) * mm, "end": v(2.92, -3.01) * mm});
            skLineSegment(sketch, "E1171", {"start": v(2.92, -3.01) * mm, "end": v(2.98, -2.93) * mm});
            skLineSegment(sketch, "E1172", {"start": v(2.98, -2.93) * mm, "end": v(3.04, -2.86) * mm});
            skLineSegment(sketch, "E1173", {"start": v(3.04, -2.86) * mm, "end": v(3.1, -2.78) * mm});
            skLineSegment(sketch, "E1174", {"start": v(3.1, -2.78) * mm, "end": v(3.15, -2.7) * mm});
            skLineSegment(sketch, "E1175", {"start": v(3.15, -2.7) * mm, "end": v(3.2, -2.63) * mm});
            skLineSegment(sketch, "E1176", {"start": v(3.2, -2.63) * mm, "end": v(3.26, -2.55) * mm});
            skLineSegment(sketch, "E1177", {"start": v(3.26, -2.55) * mm, "end": v(3.31, -2.48) * mm});
            skLineSegment(sketch, "E1178", {"start": v(3.31, -2.48) * mm, "end": v(3.37, -2.4) * mm});
            skLineSegment(sketch, "E1179", {"start": v(3.37, -2.4) * mm, "end": v(3.42, -2.32) * mm});
            skLineSegment(sketch, "E1180", {"start": v(3.42, -2.32) * mm, "end": v(3.48, -2.25) * mm});
            skLineSegment(sketch, "E1181", {"start": v(3.48, -2.25) * mm, "end": v(3.54, -2.17) * mm});
            skLineSegment(sketch, "E1182", {"start": v(3.54, -2.17) * mm, "end": v(3.6, -2.1) * mm});
            skLineSegment(sketch, "E1183", {"start": v(3.6, -2.1) * mm, "end": v(3.65, -2.02) * mm});
            skLineSegment(sketch, "E1184", {"start": v(3.65, -2.02) * mm, "end": v(3.7, -1.95) * mm});
            skLineSegment(sketch, "E1185", {"start": v(3.7, -1.95) * mm, "end": v(3.76, -1.87) * mm});
            skLineSegment(sketch, "E1186", {"start": v(3.76, -1.87) * mm, "end": v(3.82, -1.8) * mm});
            skLineSegment(sketch, "E1187", {"start": v(3.82, -1.8) * mm, "end": v(3.88, -1.72) * mm});
            skLineSegment(sketch, "E1188", {"start": v(3.88, -1.72) * mm, "end": v(3.93, -1.65) * mm});
            skLineSegment(sketch, "E1189", {"start": v(3.93, -1.65) * mm, "end": v(4, -1.57) * mm});
            skLineSegment(sketch, "E1190", {"start": v(4, -1.57) * mm, "end": v(4.05, -1.5) * mm});
            skLineSegment(sketch, "E1191", {"start": v(4.05, -1.5) * mm, "end": v(4.1, -1.42) * mm});
            skLineSegment(sketch, "E1192", {"start": v(4.1, -1.42) * mm, "end": v(4.16, -1.35) * mm});
            skLineSegment(sketch, "E1193", {"start": v(4.16, -1.35) * mm, "end": v(4.22, -1.27) * mm});
            skLineSegment(sketch, "E1194", {"start": v(4.22, -1.27) * mm, "end": v(4.28, -1.2) * mm});
            skLineSegment(sketch, "E1195", {"start": v(4.28, -1.2) * mm, "end": v(4.34, -1.13) * mm});
            skLineSegment(sketch, "E1196", {"start": v(4.34, -1.13) * mm, "end": v(4.4, -1.05) * mm});
            skLineSegment(sketch, "E1197", {"start": v(4.4, -1.05) * mm, "end": v(4.45, -0.98) * mm});
            skLineSegment(sketch, "E1198", {"start": v(4.45, -0.98) * mm, "end": v(4.51, -0.9) * mm});
            skLineSegment(sketch, "E1199", {"start": v(4.51, -0.9) * mm, "end": v(4.57, -0.83) * mm});
            skLineSegment(sketch, "E1200", {"start": v(4.57, -0.83) * mm, "end": v(4.63, -0.76) * mm});
            skLineSegment(sketch, "E1201", {"start": v(4.63, -0.76) * mm, "end": v(4.69, -0.68) * mm});
            skLineSegment(sketch, "E1202", {"start": v(4.69, -0.68) * mm, "end": v(4.74, -0.61) * mm});
            skLineSegment(sketch, "E1203", {"start": v(4.74, -0.61) * mm, "end": v(4.8, -0.54) * mm});
            skLineSegment(sketch, "E1204", {"start": v(4.8, -0.54) * mm, "end": v(4.86, -0.47) * mm});
            skLineSegment(sketch, "E1205", {"start": v(4.86, -0.47) * mm, "end": v(4.92, -0.4) * mm});
            skLineSegment(sketch, "E1206", {"start": v(4.92, -0.4) * mm, "end": v(4.98, -0.32) * mm});
            skLineSegment(sketch, "E1207", {"start": v(4.98, -0.32) * mm, "end": v(5.04, -0.25) * mm});
            skLineSegment(sketch, "E1208", {"start": v(5.04, -0.25) * mm, "end": v(5.1, -0.18) * mm});
            skLineSegment(sketch, "E1209", {"start": v(5.1, -0.18) * mm, "end": v(5.16, -0.1) * mm});
            skLineSegment(sketch, "E1210", {"start": v(5.16, -0.1) * mm, "end": v(5.22, -0.03) * mm});
            skLineSegment(sketch, "E1211", {"start": v(5.22, -0.03) * mm, "end": v(5.28, 0.04) * mm});
            skLineSegment(sketch, "E1212", {"start": v(5.28, 0.04) * mm, "end": v(5.34, 0.11) * mm});
            skLineSegment(sketch, "E1213", {"start": v(5.34, 0.11) * mm, "end": v(5.4, 0.18) * mm});
            skLineSegment(sketch, "E1214", {"start": v(5.4, 0.18) * mm, "end": v(5.45, 0.25) * mm});
            skLineSegment(sketch, "E1215", {"start": v(5.45, 0.25) * mm, "end": v(5.51, 0.33) * mm});
            skLineSegment(sketch, "E1216", {"start": v(5.51, 0.33) * mm, "end": v(5.57, 0.4) * mm});
            skLineSegment(sketch, "E1217", {"start": v(5.57, 0.4) * mm, "end": v(5.63, 0.47) * mm});
            skLineSegment(sketch, "E1218", {"start": v(5.63, 0.47) * mm, "end": v(5.7, 0.54) * mm});
            skLineSegment(sketch, "E1219", {"start": v(5.7, 0.54) * mm, "end": v(5.76, 0.61) * mm});
            skLineSegment(sketch, "E1220", {"start": v(5.76, 0.61) * mm, "end": v(5.82, 0.68) * mm});
            skLineSegment(sketch, "E1221", {"start": v(5.82, 0.68) * mm, "end": v(5.88, 0.75) * mm});
            skLineSegment(sketch, "E1222", {"start": v(5.88, 0.75) * mm, "end": v(5.94, 0.82) * mm});
            skLineSegment(sketch, "E1223", {"start": v(5.94, 0.82) * mm, "end": v(6, 0.9) * mm});
            skLineSegment(sketch, "E1224", {"start": v(6, 0.9) * mm, "end": v(6.06, 0.96) * mm});
            skLineSegment(sketch, "E1225", {"start": v(6.06, 0.96) * mm, "end": v(6.12, 1.03) * mm});
            skLineSegment(sketch, "E1226", {"start": v(6.12, 1.03) * mm, "end": v(6.18, 1.1) * mm});
            skLineSegment(sketch, "E1227", {"start": v(6.18, 1.1) * mm, "end": v(6.24, 1.17) * mm});
            skLineSegment(sketch, "E1228", {"start": v(6.24, 1.17) * mm, "end": v(6.3, 1.24) * mm});
            skLineSegment(sketch, "E1229", {"start": v(6.3, 1.24) * mm, "end": v(6.36, 1.31) * mm});
            skLineSegment(sketch, "E1230", {"start": v(6.36, 1.31) * mm, "end": v(6.43, 1.38) * mm});
            skLineSegment(sketch, "E1231", {"start": v(6.43, 1.38) * mm, "end": v(6.49, 1.45) * mm});
            skLineSegment(sketch, "E1232", {"start": v(6.49, 1.45) * mm, "end": v(6.55, 1.52) * mm});
            skLineSegment(sketch, "E1233", {"start": v(6.55, 1.52) * mm, "end": v(6.61, 1.59) * mm});
            skLineSegment(sketch, "E1234", {"start": v(6.61, 1.59) * mm, "end": v(6.67, 1.66) * mm});
            skLineSegment(sketch, "E1235", {"start": v(6.67, 1.66) * mm, "end": v(6.73, 1.73) * mm});
            skLineSegment(sketch, "E1236", {"start": v(6.73, 1.73) * mm, "end": v(6.8, 1.8) * mm});
            skLineSegment(sketch, "E1237", {"start": v(6.8, 1.8) * mm, "end": v(6.86, 1.86) * mm});
            skLineSegment(sketch, "E1238", {"start": v(6.86, 1.86) * mm, "end": v(6.92, 1.93) * mm});
            skLineSegment(sketch, "E1239", {"start": v(6.92, 1.93) * mm, "end": v(6.98, 2) * mm});
            skLineSegment(sketch, "E1240", {"start": v(6.98, 2) * mm, "end": v(7.05, 2.07) * mm});
            skLineSegment(sketch, "E1241", {"start": v(7.05, 2.07) * mm, "end": v(7.1, 2.14) * mm});
            skLineSegment(sketch, "E1242", {"start": v(7.1, 2.14) * mm, "end": v(7.17, 2.2) * mm});
            skLineSegment(sketch, "E1243", {"start": v(7.17, 2.2) * mm, "end": v(7.23, 2.27) * mm});
            skLineSegment(sketch, "E1244", {"start": v(7.23, 2.27) * mm, "end": v(7.3, 2.34) * mm});
            skLineSegment(sketch, "E1245", {"start": v(7.3, 2.34) * mm, "end": v(7.36, 2.4) * mm});
            skLineSegment(sketch, "E1246", {"start": v(7.36, 2.4) * mm, "end": v(7.42, 2.47) * mm});
            skLineSegment(sketch, "E1247", {"start": v(7.42, 2.47) * mm, "end": v(7.49, 2.54) * mm});
            skLineSegment(sketch, "E1248", {"start": v(7.49, 2.54) * mm, "end": v(7.55, 2.6) * mm});
            skLineSegment(sketch, "E1249", {"start": v(7.55, 2.6) * mm, "end": v(7.61, 2.67) * mm});
            skLineSegment(sketch, "E1250", {"start": v(7.61, 2.67) * mm, "end": v(7.68, 2.74) * mm});
            skLineSegment(sketch, "E1251", {"start": v(7.68, 2.74) * mm, "end": v(7.74, 2.8) * mm});
            skLineSegment(sketch, "E1252", {"start": v(7.74, 2.8) * mm, "end": v(7.8, 2.87) * mm});
            skLineSegment(sketch, "E1253", {"start": v(7.8, 2.87) * mm, "end": v(7.87, 2.94) * mm});
            skLineSegment(sketch, "E1254", {"start": v(7.87, 2.94) * mm, "end": v(7.93, 3) * mm});
            skLineSegment(sketch, "E1255", {"start": v(7.93, 3) * mm, "end": v(8, 3.07) * mm});
            skLineSegment(sketch, "E1256", {"start": v(8, 3.07) * mm, "end": v(8.06, 3.14) * mm});
            skLineSegment(sketch, "E1257", {"start": v(8.06, 3.14) * mm, "end": v(8.12, 3.2) * mm});
            skLineSegment(sketch, "E1258", {"start": v(8.12, 3.2) * mm, "end": v(8.19, 3.27) * mm});
            skLineSegment(sketch, "E1259", {"start": v(8.19, 3.27) * mm, "end": v(8.25, 3.33) * mm});
            skLineSegment(sketch, "E1260", {"start": v(8.25, 3.33) * mm, "end": v(8.32, 3.4) * mm});
            skLineSegment(sketch, "E1261", {"start": v(8.32, 3.4) * mm, "end": v(8.38, 3.46) * mm});
            skLineSegment(sketch, "E1262", {"start": v(8.38, 3.46) * mm, "end": v(8.44, 3.53) * mm});
            skLineSegment(sketch, "E1263", {"start": v(8.44, 3.53) * mm, "end": v(8.5, 3.6) * mm});
            skLineSegment(sketch, "E1264", {"start": v(8.5, 3.6) * mm, "end": v(8.57, 3.66) * mm});
            skLineSegment(sketch, "E1265", {"start": v(8.57, 3.66) * mm, "end": v(8.64, 3.72) * mm});
            skLineSegment(sketch, "E1266", {"start": v(8.64, 3.72) * mm, "end": v(8.7, 3.79) * mm});
            skLineSegment(sketch, "E1267", {"start": v(8.7, 3.79) * mm, "end": v(8.77, 3.85) * mm});
            skLineSegment(sketch, "E1268", {"start": v(8.77, 3.85) * mm, "end": v(8.83, 3.92) * mm});
            skLineSegment(sketch, "E1269", {"start": v(8.83, 3.92) * mm, "end": v(8.97, 4.05) * mm});
            skLineSegment(sketch, "E1270", {"start": v(8.97, 4.05) * mm, "end": v(9.1, 4.18) * mm});
            skLineSegment(sketch, "E1271", {"start": v(9.1, 4.18) * mm, "end": v(9.25, 4.32) * mm});
            skLineSegment(sketch, "E1272", {"start": v(9.25, 4.32) * mm, "end": v(9.38, 4.45) * mm});
            skLineSegment(sketch, "E1273", {"start": v(9.38, 4.45) * mm, "end": v(9.52, 4.58) * mm});
            skLineSegment(sketch, "E1274", {"start": v(9.52, 4.58) * mm, "end": v(9.66, 4.71) * mm});
            skLineSegment(sketch, "E1275", {"start": v(9.66, 4.71) * mm, "end": v(9.8, 4.84) * mm});
            skLineSegment(sketch, "E1276", {"start": v(9.8, 4.84) * mm, "end": v(9.94, 4.97) * mm});
            skLineSegment(sketch, "E1277", {"start": v(9.94, 4.97) * mm, "end": v(10.08, 5.1) * mm});
            skLineSegment(sketch, "E1278", {"start": v(10.08, 5.1) * mm, "end": v(10.22, 5.23) * mm});
            skLineSegment(sketch, "E1279", {"start": v(10.22, 5.23) * mm, "end": v(10.36, 5.36) * mm});
            skLineSegment(sketch, "E1280", {"start": v(10.36, 5.36) * mm, "end": v(10.5, 5.48) * mm});
            skLineSegment(sketch, "E1281", {"start": v(10.5, 5.48) * mm, "end": v(10.64, 5.61) * mm});
            skLineSegment(sketch, "E1282", {"start": v(10.64, 5.61) * mm, "end": v(10.79, 5.74) * mm});
            skLineSegment(sketch, "E1283", {"start": v(10.79, 5.74) * mm, "end": v(10.93, 5.86) * mm});
            skLineSegment(sketch, "E1284", {"start": v(10.93, 5.86) * mm, "end": v(11.07, 5.99) * mm});
            skLineSegment(sketch, "E1285", {"start": v(11.07, 5.99) * mm, "end": v(11.21, 6.11) * mm});
            skLineSegment(sketch, "E1286", {"start": v(11.21, 6.11) * mm, "end": v(11.36, 6.23) * mm});
            skLineSegment(sketch, "E1287", {"start": v(11.36, 6.23) * mm, "end": v(11.5, 6.36) * mm});
            skLineSegment(sketch, "E1288", {"start": v(11.5, 6.36) * mm, "end": v(11.64, 6.48) * mm});
            skLineSegment(sketch, "E1289", {"start": v(11.64, 6.48) * mm, "end": v(11.79, 6.6) * mm});
            skLineSegment(sketch, "E1290", {"start": v(11.79, 6.6) * mm, "end": v(11.93, 6.72) * mm});
            skLineSegment(sketch, "E1291", {"start": v(11.93, 6.72) * mm, "end": v(12.08, 6.84) * mm});
            skLineSegment(sketch, "E1292", {"start": v(12.08, 6.84) * mm, "end": v(12.22, 6.96) * mm});
            skLineSegment(sketch, "E1293", {"start": v(12.22, 6.96) * mm, "end": v(12.37, 7.08) * mm});
            skLineSegment(sketch, "E1294", {"start": v(12.37, 7.08) * mm, "end": v(12.52, 7.2) * mm});
            skLineSegment(sketch, "E1295", {"start": v(12.52, 7.2) * mm, "end": v(12.66, 7.32) * mm});
            skLineSegment(sketch, "E1296", {"start": v(12.66, 7.32) * mm, "end": v(12.8, 7.43) * mm});
            skLineSegment(sketch, "E1297", {"start": v(12.8, 7.43) * mm, "end": v(12.96, 7.55) * mm});
            skLineSegment(sketch, "E1298", {"start": v(12.96, 7.55) * mm, "end": v(13.1, 7.66) * mm});
            skLineSegment(sketch, "E1299", {"start": v(13.1, 7.66) * mm, "end": v(13.25, 7.78) * mm});
            skLineSegment(sketch, "E1300", {"start": v(13.25, 7.78) * mm, "end": v(13.4, 7.9) * mm});
            skLineSegment(sketch, "E1301", {"start": v(13.4, 7.9) * mm, "end": v(13.55, 8) * mm});
            skLineSegment(sketch, "E1302", {"start": v(13.55, 8) * mm, "end": v(13.7, 8.12) * mm});
            skLineSegment(sketch, "E1303", {"start": v(13.7, 8.12) * mm, "end": v(13.84, 8.23) * mm});
            skLineSegment(sketch, "E1304", {"start": v(13.84, 8.23) * mm, "end": v(14, 8.34) * mm});
            skLineSegment(sketch, "E1305", {"start": v(14, 8.34) * mm, "end": v(14.14, 8.46) * mm});
            skLineSegment(sketch, "E1306", {"start": v(14.14, 8.46) * mm, "end": v(14.3, 8.57) * mm});
            skLineSegment(sketch, "E1307", {"start": v(14.3, 8.57) * mm, "end": v(14.44, 8.68) * mm});
            skLineSegment(sketch, "E1308", {"start": v(14.44, 8.68) * mm, "end": v(14.6, 8.79) * mm});
            skLineSegment(sketch, "E1309", {"start": v(14.6, 8.79) * mm, "end": v(14.75, 8.9) * mm});
            skLineSegment(sketch, "E1310", {"start": v(14.75, 8.9) * mm, "end": v(14.9, 9) * mm});
            skLineSegment(sketch, "E1311", {"start": v(14.9, 9) * mm, "end": v(15.05, 9.1) * mm});
            skLineSegment(sketch, "E1312", {"start": v(15.05, 9.1) * mm, "end": v(15.2, 9.22) * mm});
            skLineSegment(sketch, "E1313", {"start": v(15.2, 9.22) * mm, "end": v(15.35, 9.32) * mm});
            skLineSegment(sketch, "E1314", {"start": v(15.35, 9.32) * mm, "end": v(15.5, 9.43) * mm});
            skLineSegment(sketch, "E1315", {"start": v(15.5, 9.43) * mm, "end": v(15.66, 9.53) * mm});
            skLineSegment(sketch, "E1316", {"start": v(15.66, 9.53) * mm, "end": v(15.8, 9.63) * mm});
            skLineSegment(sketch, "E1317", {"start": v(15.8, 9.63) * mm, "end": v(15.96, 9.74) * mm});
            skLineSegment(sketch, "E1318", {"start": v(15.96, 9.74) * mm, "end": v(16.12, 9.84) * mm});
            skLineSegment(sketch, "E1319", {"start": v(16.12, 9.84) * mm, "end": v(16.27, 9.94) * mm});
            skLineSegment(sketch, "E1320", {"start": v(16.27, 9.94) * mm, "end": v(16.42, 10.04) * mm});
            skLineSegment(sketch, "E1321", {"start": v(16.42, 10.04) * mm, "end": v(16.58, 10.14) * mm});
            skLineSegment(sketch, "E1322", {"start": v(16.58, 10.14) * mm, "end": v(16.73, 10.24) * mm});
            skLineSegment(sketch, "E1323", {"start": v(16.73, 10.24) * mm, "end": v(16.89, 10.34) * mm});
            skLineSegment(sketch, "E1324", {"start": v(16.89, 10.34) * mm, "end": v(17.04, 10.44) * mm});
            skLineSegment(sketch, "E1325", {"start": v(17.04, 10.44) * mm, "end": v(17.2, 10.54) * mm});
            skLineSegment(sketch, "E1326", {"start": v(17.2, 10.54) * mm, "end": v(17.36, 10.64) * mm});
            skLineSegment(sketch, "E1327", {"start": v(17.36, 10.64) * mm, "end": v(17.51, 10.73) * mm});
            skLineSegment(sketch, "E1328", {"start": v(17.51, 10.73) * mm, "end": v(17.67, 10.83) * mm});
            skLineSegment(sketch, "E1329", {"start": v(17.67, 10.83) * mm, "end": v(17.82, 10.92) * mm});
            skLineSegment(sketch, "E1330", {"start": v(17.82, 10.92) * mm, "end": v(17.98, 11.02) * mm});
            skLineSegment(sketch, "E1331", {"start": v(17.98, 11.02) * mm, "end": v(18.14, 11.11) * mm});
            skLineSegment(sketch, "E1332", {"start": v(18.14, 11.11) * mm, "end": v(18.3, 11.2) * mm});
            skLineSegment(sketch, "E1333", {"start": v(18.3, 11.2) * mm, "end": v(18.45, 11.3) * mm});
            skLineSegment(sketch, "E1334", {"start": v(18.45, 11.3) * mm, "end": v(18.61, 11.39) * mm});
            skLineSegment(sketch, "E1335", {"start": v(18.61, 11.39) * mm, "end": v(18.77, 11.48) * mm});
            skLineSegment(sketch, "E1336", {"start": v(18.77, 11.48) * mm, "end": v(18.93, 11.57) * mm});
            skLineSegment(sketch, "E1337", {"start": v(18.93, 11.57) * mm, "end": v(19.09, 11.66) * mm});
            skLineSegment(sketch, "E1338", {"start": v(19.09, 11.66) * mm, "end": v(19.24, 11.75) * mm});
            skLineSegment(sketch, "E1339", {"start": v(19.24, 11.75) * mm, "end": v(19.4, 11.83) * mm});
            skLineSegment(sketch, "E1340", {"start": v(19.4, 11.83) * mm, "end": v(19.56, 11.92) * mm});
            skLineSegment(sketch, "E1341", {"start": v(19.56, 11.92) * mm, "end": v(19.72, 12) * mm});
            skLineSegment(sketch, "E1342", {"start": v(19.72, 12) * mm, "end": v(19.88, 12.1) * mm});
            skLineSegment(sketch, "E1343", {"start": v(19.88, 12.1) * mm, "end": v(20.04, 12.18) * mm});
            skLineSegment(sketch, "E1344", {"start": v(20.04, 12.18) * mm, "end": v(20.2, 12.26) * mm});
            skLineSegment(sketch, "E1345", {"start": v(20.2, 12.26) * mm, "end": v(20.36, 12.35) * mm});
            skLineSegment(sketch, "E1346", {"start": v(20.36, 12.35) * mm, "end": v(20.52, 12.43) * mm});
            skLineSegment(sketch, "E1347", {"start": v(20.52, 12.43) * mm, "end": v(20.69, 12.51) * mm});
            skLineSegment(sketch, "E1348", {"start": v(20.69, 12.51) * mm, "end": v(20.85, 12.6) * mm});
            skLineSegment(sketch, "E1349", {"start": v(20.85, 12.6) * mm, "end": v(21, 12.68) * mm});
            skLineSegment(sketch, "E1350", {"start": v(21, 12.68) * mm, "end": v(21.17, 12.76) * mm});
            skLineSegment(sketch, "E1351", {"start": v(21.17, 12.76) * mm, "end": v(21.33, 12.84) * mm});
            skLineSegment(sketch, "E1352", {"start": v(21.33, 12.84) * mm, "end": v(21.5, 12.91) * mm});
            skLineSegment(sketch, "E1353", {"start": v(21.5, 12.91) * mm, "end": v(21.66, 13) * mm});
            skLineSegment(sketch, "E1354", {"start": v(21.66, 13) * mm, "end": v(21.82, 13.07) * mm});
            skLineSegment(sketch, "E1355", {"start": v(21.82, 13.07) * mm, "end": v(21.98, 13.15) * mm});
            skLineSegment(sketch, "E1356", {"start": v(21.98, 13.15) * mm, "end": v(22.14, 13.22) * mm});
            skLineSegment(sketch, "E1357", {"start": v(22.14, 13.22) * mm, "end": v(22.3, 13.3) * mm});
            skLineSegment(sketch, "E1358", {"start": v(22.3, 13.3) * mm, "end": v(22.47, 13.37) * mm});
            skLineSegment(sketch, "E1359", {"start": v(22.47, 13.37) * mm, "end": v(22.63, 13.45) * mm});
            skLineSegment(sketch, "E1360", {"start": v(22.63, 13.45) * mm, "end": v(22.8, 13.52) * mm});
            skLineSegment(sketch, "E1361", {"start": v(22.8, 13.52) * mm, "end": v(22.96, 13.6) * mm});
            skLineSegment(sketch, "E1362", {"start": v(22.96, 13.6) * mm, "end": v(23.13, 13.66) * mm});
            skLineSegment(sketch, "E1363", {"start": v(23.13, 13.66) * mm, "end": v(23.29, 13.73) * mm});
            skLineSegment(sketch, "E1364", {"start": v(23.29, 13.73) * mm, "end": v(23.45, 13.8) * mm});
            skLineSegment(sketch, "E1365", {"start": v(23.45, 13.8) * mm, "end": v(23.62, 13.87) * mm});
            skLineSegment(sketch, "E1366", {"start": v(23.62, 13.87) * mm, "end": v(23.78, 13.94) * mm});
            skLineSegment(sketch, "E1367", {"start": v(23.78, 13.94) * mm, "end": v(23.95, 14) * mm});
            skLineSegment(sketch, "E1368", {"start": v(23.95, 14) * mm, "end": v(24.11, 14.08) * mm});
            skLineSegment(sketch, "E1369", {"start": v(24.11, 14.08) * mm, "end": v(24.28, 14.14) * mm});
            skLineSegment(sketch, "E1370", {"start": v(24.28, 14.14) * mm, "end": v(24.44, 14.2) * mm});
            skLineSegment(sketch, "E1371", {"start": v(24.44, 14.2) * mm, "end": v(24.61, 14.27) * mm});
            skLineSegment(sketch, "E1372", {"start": v(24.61, 14.27) * mm, "end": v(24.78, 14.34) * mm});
            skLineSegment(sketch, "E1373", {"start": v(24.78, 14.34) * mm, "end": v(24.94, 14.4) * mm});
            skLineSegment(sketch, "E1374", {"start": v(24.94, 14.4) * mm, "end": v(25.1, 14.46) * mm});
            skLineSegment(sketch, "E1375", {"start": v(25.1, 14.46) * mm, "end": v(25.28, 14.53) * mm});
            skLineSegment(sketch, "E1376", {"start": v(25.28, 14.53) * mm, "end": v(25.44, 14.59) * mm});
            skLineSegment(sketch, "E1377", {"start": v(25.44, 14.59) * mm, "end": v(25.6, 14.65) * mm});
            skLineSegment(sketch, "E1378", {"start": v(25.6, 14.65) * mm, "end": v(25.78, 14.7) * mm});
            skLineSegment(sketch, "E1379", {"start": v(25.78, 14.7) * mm, "end": v(25.94, 14.77) * mm});
            skLineSegment(sketch, "E1380", {"start": v(25.94, 14.77) * mm, "end": v(26.1, 14.83) * mm});
            skLineSegment(sketch, "E1381", {"start": v(26.1, 14.83) * mm, "end": v(26.28, 14.88) * mm});
            skLineSegment(sketch, "E1382", {"start": v(26.28, 14.88) * mm, "end": v(26.44, 14.94) * mm});
            skLineSegment(sketch, "E1383", {"start": v(26.44, 14.94) * mm, "end": v(26.61, 15) * mm});
            skLineSegment(sketch, "E1384", {"start": v(26.61, 15) * mm, "end": v(26.78, 15.05) * mm});
            skLineSegment(sketch, "E1385", {"start": v(26.78, 15.05) * mm, "end": v(26.95, 15.1) * mm});
            skLineSegment(sketch, "E1386", {"start": v(26.95, 15.1) * mm, "end": v(27.12, 15.16) * mm});
            skLineSegment(sketch, "E1387", {"start": v(27.12, 15.16) * mm, "end": v(27.28, 15.21) * mm});
            skLineSegment(sketch, "E1388", {"start": v(27.28, 15.21) * mm, "end": v(27.45, 15.26) * mm});
            skLineSegment(sketch, "E1389", {"start": v(27.45, 15.26) * mm, "end": v(27.62, 15.32) * mm});
            skLineSegment(sketch, "E1390", {"start": v(27.62, 15.32) * mm, "end": v(27.8, 15.37) * mm});
            skLineSegment(sketch, "E1391", {"start": v(27.8, 15.37) * mm, "end": v(27.96, 15.42) * mm});
            skLineSegment(sketch, "E1392", {"start": v(27.96, 15.42) * mm, "end": v(28.13, 15.46) * mm});
            skLineSegment(sketch, "E1393", {"start": v(28.13, 15.46) * mm, "end": v(28.3, 15.51) * mm});
            skLineSegment(sketch, "E1394", {"start": v(28.3, 15.51) * mm, "end": v(28.47, 15.56) * mm});
            skLineSegment(sketch, "E1395", {"start": v(28.47, 15.56) * mm, "end": v(28.64, 15.6) * mm});
            skLineSegment(sketch, "E1396", {"start": v(28.64, 15.6) * mm, "end": v(28.8, 15.65) * mm});
            skLineSegment(sketch, "E1397", {"start": v(28.8, 15.65) * mm, "end": v(28.85, 15.67) * mm});
            skLineSegment(sketch, "E1398", {"start": v(28.85, 15.67) * mm, "end": v(28.9, 15.68) * mm});
            skLineSegment(sketch, "E1399", {"start": v(28.9, 15.68) * mm, "end": v(28.95, 15.7) * mm});
            skLineSegment(sketch, "E1400", {"start": v(28.95, 15.7) * mm, "end": v(29, 15.7) * mm});
            skLineSegment(sketch, "E1401", {"start": v(29, 15.7) * mm, "end": v(29.05, 15.72) * mm});
            skLineSegment(sketch, "E1402", {"start": v(29.05, 15.72) * mm, "end": v(29.1, 15.73) * mm});
            skLineSegment(sketch, "E1403", {"start": v(29.1, 15.73) * mm, "end": v(29.14, 15.74) * mm});
            skLineSegment(sketch, "E1404", {"start": v(29.14, 15.74) * mm, "end": v(29.2, 15.76) * mm});
            skLineSegment(sketch, "E1405", {"start": v(29.2, 15.76) * mm, "end": v(29.24, 15.77) * mm});
            skLineSegment(sketch, "E1406", {"start": v(29.24, 15.77) * mm, "end": v(29.3, 15.78) * mm});
            skLineSegment(sketch, "E1407", {"start": v(29.3, 15.78) * mm, "end": v(29.34, 15.8) * mm});
            skLineSegment(sketch, "E1408", {"start": v(29.34, 15.8) * mm, "end": v(29.39, 15.8) * mm});
            skLineSegment(sketch, "E1409", {"start": v(29.39, 15.8) * mm, "end": v(29.44, 15.82) * mm});
            skLineSegment(sketch, "E1410", {"start": v(29.44, 15.82) * mm, "end": v(29.49, 15.83) * mm});
            skLineSegment(sketch, "E1411", {"start": v(29.49, 15.83) * mm, "end": v(29.53, 15.85) * mm});
            skLineSegment(sketch, "E1412", {"start": v(29.53, 15.85) * mm, "end": v(29.58, 15.86) * mm});
            skLineSegment(sketch, "E1413", {"start": v(29.58, 15.86) * mm, "end": v(29.63, 15.87) * mm});
            skLineSegment(sketch, "E1414", {"start": v(29.63, 15.87) * mm, "end": v(29.68, 15.88) * mm});
            skLineSegment(sketch, "E1415", {"start": v(29.68, 15.88) * mm, "end": v(29.73, 15.9) * mm});
            skLineSegment(sketch, "E1416", {"start": v(29.73, 15.9) * mm, "end": v(29.78, 15.9) * mm});
            skLineSegment(sketch, "E1417", {"start": v(29.78, 15.9) * mm, "end": v(29.83, 15.92) * mm});
            skLineSegment(sketch, "E1418", {"start": v(29.83, 15.92) * mm, "end": v(29.88, 15.93) * mm});
            skLineSegment(sketch, "E1419", {"start": v(29.88, 15.93) * mm, "end": v(29.93, 15.95) * mm});
            skLineSegment(sketch, "E1420", {"start": v(29.93, 15.95) * mm, "end": v(29.97, 15.96) * mm});
            skLineSegment(sketch, "E1421", {"start": v(29.97, 15.96) * mm, "end": v(30.02, 15.97) * mm});
            skLineSegment(sketch, "E1422", {"start": v(30.02, 15.97) * mm, "end": v(30.07, 15.98) * mm});
            skLineSegment(sketch, "E1423", {"start": v(30.07, 15.98) * mm, "end": v(30.12, 16) * mm});
            skLineSegment(sketch, "E1424", {"start": v(30.12, 16) * mm, "end": v(30.17, 16) * mm});
            skLineSegment(sketch, "E1425", {"start": v(30.17, 16) * mm, "end": v(30.22, 16.02) * mm});
            skLineSegment(sketch, "E1426", {"start": v(30.22, 16.02) * mm, "end": v(30.27, 16.03) * mm});
            skLineSegment(sketch, "E1427", {"start": v(30.27, 16.03) * mm, "end": v(30.32, 16.05) * mm});
            skLineSegment(sketch, "E1428", {"start": v(30.32, 16.05) * mm, "end": v(30.37, 16.06) * mm});
            skLineSegment(sketch, "E1429", {"start": v(30.37, 16.06) * mm, "end": v(30.42, 16.07) * mm});
            skLineSegment(sketch, "E1430", {"start": v(30.42, 16.07) * mm, "end": v(30.46, 16.08) * mm});
            skLineSegment(sketch, "E1431", {"start": v(30.46, 16.08) * mm, "end": v(30.51, 16.1) * mm});
            skLineSegment(sketch, "E1432", {"start": v(30.51, 16.1) * mm, "end": v(30.56, 16.1) * mm});
            skLineSegment(sketch, "E1433", {"start": v(30.56, 16.1) * mm, "end": v(30.61, 16.12) * mm});
            skLineSegment(sketch, "E1434", {"start": v(30.61, 16.12) * mm, "end": v(30.66, 16.13) * mm});
            skLineSegment(sketch, "E1435", {"start": v(30.66, 16.13) * mm, "end": v(30.7, 16.14) * mm});
            skLineSegment(sketch, "E1436", {"start": v(30.7, 16.14) * mm, "end": v(30.76, 16.16) * mm});
            skLineSegment(sketch, "E1437", {"start": v(30.76, 16.16) * mm, "end": v(30.8, 16.17) * mm});
            skLineSegment(sketch, "E1438", {"start": v(30.8, 16.17) * mm, "end": v(30.86, 16.18) * mm});
            skLineSegment(sketch, "E1439", {"start": v(30.86, 16.18) * mm, "end": v(30.9, 16.2) * mm});
            skLineSegment(sketch, "E1440", {"start": v(30.9, 16.2) * mm, "end": v(30.95, 16.2) * mm});
            skLineSegment(sketch, "E1441", {"start": v(30.95, 16.2) * mm, "end": v(31, 16.22) * mm});
            skLineSegment(sketch, "E1442", {"start": v(31, 16.22) * mm, "end": v(31.05, 16.23) * mm});
            skLineSegment(sketch, "E1443", {"start": v(31.05, 16.23) * mm, "end": v(31.1, 16.24) * mm});
            skLineSegment(sketch, "E1444", {"start": v(31.1, 16.24) * mm, "end": v(31.15, 16.25) * mm});
            skLineSegment(sketch, "E1445", {"start": v(31.15, 16.25) * mm, "end": v(31.2, 16.26) * mm});
            skLineSegment(sketch, "E1446", {"start": v(31.2, 16.26) * mm, "end": v(31.25, 16.27) * mm});
            skLineSegment(sketch, "E1447", {"start": v(31.25, 16.27) * mm, "end": v(31.3, 16.29) * mm});
            skLineSegment(sketch, "E1448", {"start": v(31.3, 16.29) * mm, "end": v(31.35, 16.3) * mm});
            skLineSegment(sketch, "E1449", {"start": v(31.35, 16.3) * mm, "end": v(31.4, 16.3) * mm});
            skLineSegment(sketch, "E1450", {"start": v(31.4, 16.3) * mm, "end": v(31.45, 16.32) * mm});
            skLineSegment(sketch, "E1451", {"start": v(31.45, 16.32) * mm, "end": v(31.5, 16.33) * mm});
            skLineSegment(sketch, "E1452", {"start": v(31.5, 16.33) * mm, "end": v(31.54, 16.35) * mm});
            skLineSegment(sketch, "E1453", {"start": v(31.54, 16.35) * mm, "end": v(31.6, 16.36) * mm});
            skLineSegment(sketch, "E1454", {"start": v(31.6, 16.36) * mm, "end": v(31.64, 16.37) * mm});
            skLineSegment(sketch, "E1455", {"start": v(31.64, 16.37) * mm, "end": v(31.7, 16.38) * mm});
            skLineSegment(sketch, "E1456", {"start": v(31.7, 16.38) * mm, "end": v(31.74, 16.4) * mm});
            skLineSegment(sketch, "E1457", {"start": v(31.74, 16.4) * mm, "end": v(31.79, 16.4) * mm});
            skLineSegment(sketch, "E1458", {"start": v(31.79, 16.4) * mm, "end": v(31.84, 16.42) * mm});
            skLineSegment(sketch, "E1459", {"start": v(31.84, 16.42) * mm, "end": v(31.89, 16.43) * mm});
            skLineSegment(sketch, "E1460", {"start": v(31.89, 16.43) * mm, "end": v(31.94, 16.44) * mm});
            skLineSegment(sketch, "E1461", {"start": v(31.94, 16.44) * mm, "end": v(31.99, 16.45) * mm});
            skLineSegment(sketch, "E1462", {"start": v(31.99, 16.45) * mm, "end": v(32.04, 16.46) * mm});
            skLineSegment(sketch, "E1463", {"start": v(32.04, 16.46) * mm, "end": v(32.08, 16.47) * mm});
            skLineSegment(sketch, "E1464", {"start": v(32.08, 16.47) * mm, "end": v(32.13, 16.48) * mm});
            skLineSegment(sketch, "E1465", {"start": v(32.13, 16.48) * mm, "end": v(32.18, 16.5) * mm});
            skLineSegment(sketch, "E1466", {"start": v(32.18, 16.5) * mm, "end": v(32.23, 16.5) * mm});
            skLineSegment(sketch, "E1467", {"start": v(32.23, 16.5) * mm, "end": v(32.28, 16.52) * mm});
            skLineSegment(sketch, "E1468", {"start": v(32.28, 16.52) * mm, "end": v(32.33, 16.53) * mm});
            skLineSegment(sketch, "E1469", {"start": v(32.33, 16.53) * mm, "end": v(32.38, 16.54) * mm});
            skLineSegment(sketch, "E1470", {"start": v(32.38, 16.54) * mm, "end": v(32.43, 16.55) * mm});
            skLineSegment(sketch, "E1471", {"start": v(32.43, 16.55) * mm, "end": v(32.48, 16.56) * mm});
            skLineSegment(sketch, "E1472", {"start": v(32.48, 16.56) * mm, "end": v(32.53, 16.58) * mm});
            skLineSegment(sketch, "E1473", {"start": v(32.53, 16.58) * mm, "end": v(32.57, 16.59) * mm});
            skLineSegment(sketch, "E1474", {"start": v(32.57, 16.59) * mm, "end": v(32.62, 16.6) * mm});
            skLineSegment(sketch, "E1475", {"start": v(32.62, 16.6) * mm, "end": v(32.67, 16.6) * mm});
            skLineSegment(sketch, "E1476", {"start": v(32.67, 16.6) * mm, "end": v(32.72, 16.62) * mm});
            skLineSegment(sketch, "E1477", {"start": v(32.72, 16.62) * mm, "end": v(32.77, 16.63) * mm});
            skLineSegment(sketch, "E1478", {"start": v(32.77, 16.63) * mm, "end": v(32.82, 16.64) * mm});
            skLineSegment(sketch, "E1479", {"start": v(32.82, 16.64) * mm, "end": v(32.87, 16.65) * mm});
            skLineSegment(sketch, "E1480", {"start": v(32.87, 16.65) * mm, "end": v(32.92, 16.67) * mm});
            skLineSegment(sketch, "E1481", {"start": v(32.92, 16.67) * mm, "end": v(32.97, 16.68) * mm});
            skLineSegment(sketch, "E1482", {"start": v(32.97, 16.68) * mm, "end": v(33.02, 16.69) * mm});
            skLineSegment(sketch, "E1483", {"start": v(33.02, 16.69) * mm, "end": v(33.06, 16.7) * mm});
            skLineSegment(sketch, "E1484", {"start": v(33.06, 16.7) * mm, "end": v(33.11, 16.71) * mm});
            skLineSegment(sketch, "E1485", {"start": v(33.11, 16.71) * mm, "end": v(33.16, 16.72) * mm});
            skLineSegment(sketch, "E1486", {"start": v(33.16, 16.72) * mm, "end": v(33.21, 16.73) * mm});
            skLineSegment(sketch, "E1487", {"start": v(33.21, 16.73) * mm, "end": v(33.26, 16.74) * mm});
            skLineSegment(sketch, "E1488", {"start": v(33.26, 16.74) * mm, "end": v(33.3, 16.76) * mm});
            skLineSegment(sketch, "E1489", {"start": v(33.3, 16.76) * mm, "end": v(33.36, 16.77) * mm});
            skLineSegment(sketch, "E1490", {"start": v(33.36, 16.77) * mm, "end": v(33.4, 16.78) * mm});
            skLineSegment(sketch, "E1491", {"start": v(33.4, 16.78) * mm, "end": v(33.46, 16.79) * mm});
            skLineSegment(sketch, "E1492", {"start": v(33.46, 16.79) * mm, "end": v(33.5, 16.8) * mm});
            skLineSegment(sketch, "E1493", {"start": v(33.5, 16.8) * mm, "end": v(33.55, 16.81) * mm});
            skLineSegment(sketch, "E1494", {"start": v(33.55, 16.81) * mm, "end": v(33.6, 16.82) * mm});
            skLineSegment(sketch, "E1495", {"start": v(33.6, 16.82) * mm, "end": v(33.65, 16.83) * mm});
            skLineSegment(sketch, "E1496", {"start": v(33.65, 16.83) * mm, "end": v(33.7, 16.84) * mm});
            skLineSegment(sketch, "E1497", {"start": v(33.7, 16.84) * mm, "end": v(33.75, 16.86) * mm});
            skLineSegment(sketch, "E1498", {"start": v(33.75, 16.86) * mm, "end": v(33.8, 16.87) * mm});
            skLineSegment(sketch, "E1499", {"start": v(33.8, 16.87) * mm, "end": v(33.85, 16.88) * mm});
            skLineSegment(sketch, "E1500", {"start": v(33.85, 16.88) * mm, "end": v(33.9, 16.89) * mm});
            skLineSegment(sketch, "E1501", {"start": v(33.9, 16.89) * mm, "end": v(33.94, 16.9) * mm});
            skLineSegment(sketch, "E1502", {"start": v(33.94, 16.9) * mm, "end": v(34, 16.91) * mm});
            skLineSegment(sketch, "E1503", {"start": v(34, 16.91) * mm, "end": v(34.04, 16.92) * mm});
            skLineSegment(sketch, "E1504", {"start": v(34.04, 16.92) * mm, "end": v(34.09, 16.93) * mm});
            skLineSegment(sketch, "E1505", {"start": v(34.09, 16.93) * mm, "end": v(34.14, 16.94) * mm});
            skLineSegment(sketch, "E1506", {"start": v(34.14, 16.94) * mm, "end": v(34.19, 16.95) * mm});
            skLineSegment(sketch, "E1507", {"start": v(34.19, 16.95) * mm, "end": v(34.24, 16.96) * mm});
            skLineSegment(sketch, "E1508", {"start": v(34.24, 16.96) * mm, "end": v(34.28, 16.98) * mm});
            skLineSegment(sketch, "E1509", {"start": v(34.28, 16.98) * mm, "end": v(34.33, 16.99) * mm});
            skLineSegment(sketch, "E1510", {"start": v(34.33, 16.99) * mm, "end": v(34.38, 17) * mm});
            skLineSegment(sketch, "E1511", {"start": v(34.38, 17) * mm, "end": v(34.43, 17) * mm});
            skLineSegment(sketch, "E1512", {"start": v(34.43, 17) * mm, "end": v(34.48, 17.02) * mm});
            skLineSegment(sketch, "E1513", {"start": v(34.48, 17.02) * mm, "end": v(34.53, 17.03) * mm});
            skLineSegment(sketch, "E1514", {"start": v(34.53, 17.03) * mm, "end": v(34.58, 17.04) * mm});
            skLineSegment(sketch, "E1515", {"start": v(34.58, 17.04) * mm, "end": v(34.62, 17.05) * mm});
            skLineSegment(sketch, "E1516", {"start": v(34.62, 17.05) * mm, "end": v(34.67, 17.06) * mm});
            skLineSegment(sketch, "E1517", {"start": v(34.67, 17.06) * mm, "end": v(34.72, 17.07) * mm});
            skLineSegment(sketch, "E1518", {"start": v(34.72, 17.07) * mm, "end": v(34.77, 17.08) * mm});
            skLineSegment(sketch, "E1519", {"start": v(34.77, 17.08) * mm, "end": v(34.82, 17.1) * mm});
            skLineSegment(sketch, "E1520", {"start": v(34.82, 17.1) * mm, "end": v(34.87, 17.1) * mm});
            skLineSegment(sketch, "E1521", {"start": v(34.87, 17.1) * mm, "end": v(34.91, 17.12) * mm});
            skLineSegment(sketch, "E1522", {"start": v(34.91, 17.12) * mm, "end": v(34.96, 17.13) * mm});
            skLineSegment(sketch, "E1523", {"start": v(34.96, 17.13) * mm, "end": v(35.01, 17.14) * mm});
            skLineSegment(sketch, "E1524", {"start": v(35.01, 17.14) * mm, "end": v(35.06, 17.15) * mm});
            skLineSegment(sketch, "E1525", {"start": v(35.06, 17.15) * mm, "end": v(35.07, 17.15) * mm});
            skLineSegment(sketch, "E1526", {"start": v(35.07, 17.15) * mm, "end": v(35.08, 17.15) * mm});
            skLineSegment(sketch, "E1527", {"start": v(35.08, 17.15) * mm, "end": v(35.09, 17.16) * mm});
            skLineSegment(sketch, "E1528", {"start": v(35.09, 17.16) * mm, "end": v(35.1, 17.16) * mm});
            skLineSegment(sketch, "E1529", {"start": v(35.1, 17.16) * mm, "end": v(35.1, 17.16) * mm});
            skLineSegment(sketch, "E1530", {"start": v(35.1, 17.16) * mm, "end": v(35.12, 17.16) * mm});
            skLineSegment(sketch, "E1531", {"start": v(35.12, 17.16) * mm, "end": v(35.13, 17.17) * mm});
            skLineSegment(sketch, "E1532", {"start": v(35.13, 17.17) * mm, "end": v(35.14, 17.17) * mm});
            skLineSegment(sketch, "E1533", {"start": v(35.14, 17.17) * mm, "end": v(35.15, 17.17) * mm});
            skLineSegment(sketch, "E1534", {"start": v(35.15, 17.17) * mm, "end": v(35.16, 17.17) * mm});
            skLineSegment(sketch, "E1535", {"start": v(35.16, 17.17) * mm, "end": v(35.17, 17.17) * mm});
            skLineSegment(sketch, "E1536", {"start": v(35.17, 17.17) * mm, "end": v(35.18, 17.18) * mm});
            skLineSegment(sketch, "E1537", {"start": v(35.18, 17.18) * mm, "end": v(35.19, 17.18) * mm});
            skLineSegment(sketch, "E1538", {"start": v(35.19, 17.18) * mm, "end": v(35.2, 17.18) * mm});
            skLineSegment(sketch, "E1539", {"start": v(35.2, 17.18) * mm, "end": v(35.2, 17.18) * mm});
            skLineSegment(sketch, "E1540", {"start": v(35.2, 17.18) * mm, "end": v(35.22, 17.19) * mm});
            skLineSegment(sketch, "E1541", {"start": v(35.22, 17.19) * mm, "end": v(35.23, 17.19) * mm});
            skLineSegment(sketch, "E1542", {"start": v(35.23, 17.19) * mm, "end": v(35.24, 17.2) * mm});
            skLineSegment(sketch, "E1543", {"start": v(35.24, 17.2) * mm, "end": v(35.25, 17.2) * mm});
            skLineSegment(sketch, "E1544", {"start": v(35.25, 17.2) * mm, "end": v(35.26, 17.2) * mm});
            skLineSegment(sketch, "E1545", {"start": v(35.26, 17.2) * mm, "end": v(35.27, 17.2) * mm});
            skLineSegment(sketch, "E1546", {"start": v(35.27, 17.2) * mm, "end": v(35.28, 17.2) * mm});
            skLineSegment(sketch, "E1547", {"start": v(35.28, 17.2) * mm, "end": v(35.3, 17.2) * mm});
            skLineSegment(sketch, "E1548", {"start": v(35.3, 17.2) * mm, "end": v(35.3, 17.2) * mm});
            skLineSegment(sketch, "E1549", {"start": v(35.3, 17.2) * mm, "end": v(35.31, 17.2) * mm});
            skLineSegment(sketch, "E1550", {"start": v(35.31, 17.2) * mm, "end": v(35.32, 17.2) * mm});
            skLineSegment(sketch, "E1551", {"start": v(35.32, 17.2) * mm, "end": v(35.33, 17.21) * mm});
            skLineSegment(sketch, "E1552", {"start": v(35.33, 17.21) * mm, "end": v(35.34, 17.21) * mm});
            skLineSegment(sketch, "E1553", {"start": v(35.34, 17.21) * mm, "end": v(35.35, 17.21) * mm});
            skLineSegment(sketch, "E1554", {"start": v(35.35, 17.21) * mm, "end": v(35.36, 17.22) * mm});
            skLineSegment(sketch, "E1555", {"start": v(35.36, 17.22) * mm, "end": v(35.37, 17.22) * mm});
            skLineSegment(sketch, "E1556", {"start": v(35.37, 17.22) * mm, "end": v(35.38, 17.22) * mm});
            skLineSegment(sketch, "E1557", {"start": v(35.38, 17.22) * mm, "end": v(35.4, 17.22) * mm});
            skLineSegment(sketch, "E1558", {"start": v(35.4, 17.22) * mm, "end": v(35.4, 17.23) * mm});
            skLineSegment(sketch, "E1559", {"start": v(35.4, 17.23) * mm, "end": v(35.41, 17.23) * mm});
            skLineSegment(sketch, "E1560", {"start": v(35.41, 17.23) * mm, "end": v(35.42, 17.23) * mm});
            skLineSegment(sketch, "E1561", {"start": v(35.42, 17.23) * mm, "end": v(35.43, 17.23) * mm});
            skLineSegment(sketch, "E1562", {"start": v(35.43, 17.23) * mm, "end": v(35.44, 17.24) * mm});
            skLineSegment(sketch, "E1563", {"start": v(35.44, 17.24) * mm, "end": v(35.45, 17.24) * mm});
            skLineSegment(sketch, "E1564", {"start": v(35.45, 17.24) * mm, "end": v(35.46, 17.24) * mm});
            skLineSegment(sketch, "E1565", {"start": v(35.46, 17.24) * mm, "end": v(35.47, 17.24) * mm});
            skLineSegment(sketch, "E1566", {"start": v(35.47, 17.24) * mm, "end": v(35.48, 17.24) * mm});
            skLineSegment(sketch, "E1567", {"start": v(35.48, 17.24) * mm, "end": v(35.5, 17.25) * mm});
            skLineSegment(sketch, "E1568", {"start": v(35.5, 17.25) * mm, "end": v(35.5, 17.25) * mm});
            skLineSegment(sketch, "E1569", {"start": v(35.5, 17.25) * mm, "end": v(35.51, 17.25) * mm});
            skLineSegment(sketch, "E1570", {"start": v(35.51, 17.25) * mm, "end": v(35.52, 17.25) * mm});
            skLineSegment(sketch, "E1571", {"start": v(35.52, 17.25) * mm, "end": v(35.53, 17.26) * mm});
            skLineSegment(sketch, "E1572", {"start": v(35.53, 17.26) * mm, "end": v(35.54, 17.26) * mm});
            skLineSegment(sketch, "E1573", {"start": v(35.54, 17.26) * mm, "end": v(35.55, 17.26) * mm});
            skLineSegment(sketch, "E1574", {"start": v(35.55, 17.26) * mm, "end": v(35.56, 17.26) * mm});
            skLineSegment(sketch, "E1575", {"start": v(35.56, 17.26) * mm, "end": v(35.57, 17.26) * mm});
            skLineSegment(sketch, "E1576", {"start": v(35.57, 17.26) * mm, "end": v(35.58, 17.27) * mm});
            skLineSegment(sketch, "E1577", {"start": v(35.58, 17.27) * mm, "end": v(35.6, 17.27) * mm});
            skLineSegment(sketch, "E1578", {"start": v(35.6, 17.27) * mm, "end": v(35.6, 17.27) * mm});
            skLineSegment(sketch, "E1579", {"start": v(35.6, 17.27) * mm, "end": v(35.61, 17.27) * mm});
            skLineSegment(sketch, "E1580", {"start": v(35.61, 17.27) * mm, "end": v(35.62, 17.28) * mm});
            skLineSegment(sketch, "E1581", {"start": v(35.62, 17.28) * mm, "end": v(35.63, 17.28) * mm});
            skLineSegment(sketch, "E1582", {"start": v(35.63, 17.28) * mm, "end": v(35.64, 17.28) * mm});
            skLineSegment(sketch, "E1583", {"start": v(35.64, 17.28) * mm, "end": v(35.65, 17.28) * mm});
            skLineSegment(sketch, "E1584", {"start": v(35.65, 17.28) * mm, "end": v(35.66, 17.29) * mm});
            skLineSegment(sketch, "E1585", {"start": v(35.66, 17.29) * mm, "end": v(35.67, 17.29) * mm});
            skLineSegment(sketch, "E1586", {"start": v(35.67, 17.29) * mm, "end": v(35.68, 17.29) * mm});
            skLineSegment(sketch, "E1587", {"start": v(35.68, 17.29) * mm, "end": v(35.7, 17.3) * mm});
            skLineSegment(sketch, "E1588", {"start": v(35.7, 17.3) * mm, "end": v(35.7, 17.3) * mm});
            skLineSegment(sketch, "E1589", {"start": v(35.7, 17.3) * mm, "end": v(35.71, 17.3) * mm});
            skLineSegment(sketch, "E1590", {"start": v(35.71, 17.3) * mm, "end": v(35.72, 17.3) * mm});
            skLineSegment(sketch, "E1591", {"start": v(35.72, 17.3) * mm, "end": v(35.73, 17.3) * mm});
            skLineSegment(sketch, "E1592", {"start": v(35.73, 17.3) * mm, "end": v(35.74, 17.3) * mm});
            skLineSegment(sketch, "E1593", {"start": v(35.74, 17.3) * mm, "end": v(35.75, 17.3) * mm});
            skLineSegment(sketch, "E1594", {"start": v(35.75, 17.3) * mm, "end": v(35.76, 17.3) * mm});
            skLineSegment(sketch, "E1595", {"start": v(35.76, 17.3) * mm, "end": v(35.77, 17.3) * mm});
            skLineSegment(sketch, "E1596", {"start": v(35.77, 17.3) * mm, "end": v(35.78, 17.31) * mm});
            skLineSegment(sketch, "E1597", {"start": v(35.78, 17.31) * mm, "end": v(35.8, 17.31) * mm});
            skLineSegment(sketch, "E1598", {"start": v(35.8, 17.31) * mm, "end": v(35.8, 17.32) * mm});
            skLineSegment(sketch, "E1599", {"start": v(35.8, 17.32) * mm, "end": v(35.81, 17.32) * mm});
            skLineSegment(sketch, "E1600", {"start": v(35.81, 17.32) * mm, "end": v(35.82, 17.32) * mm});
            skLineSegment(sketch, "E1601", {"start": v(35.82, 17.32) * mm, "end": v(35.83, 17.32) * mm});
            skLineSegment(sketch, "E1602", {"start": v(35.83, 17.32) * mm, "end": v(35.84, 17.33) * mm});
            skLineSegment(sketch, "E1603", {"start": v(35.84, 17.33) * mm, "end": v(35.85, 17.33) * mm});
            skLineSegment(sketch, "E1604", {"start": v(35.85, 17.33) * mm, "end": v(35.87, 17.33) * mm});
            skLineSegment(sketch, "E1605", {"start": v(35.87, 17.33) * mm, "end": v(35.88, 17.33) * mm});
            skLineSegment(sketch, "E1606", {"start": v(35.88, 17.33) * mm, "end": v(35.89, 17.33) * mm});
            skLineSegment(sketch, "E1607", {"start": v(35.89, 17.33) * mm, "end": v(35.9, 17.34) * mm});
            skLineSegment(sketch, "E1608", {"start": v(35.9, 17.34) * mm, "end": v(35.9, 17.34) * mm});
            skLineSegment(sketch, "E1609", {"start": v(35.9, 17.34) * mm, "end": v(35.92, 17.34) * mm});
            skLineSegment(sketch, "E1610", {"start": v(35.92, 17.34) * mm, "end": v(35.93, 17.34) * mm});
            skLineSegment(sketch, "E1611", {"start": v(35.93, 17.34) * mm, "end": v(35.94, 17.35) * mm});
            skLineSegment(sketch, "E1612", {"start": v(35.94, 17.35) * mm, "end": v(35.95, 17.35) * mm});
            skLineSegment(sketch, "E1613", {"start": v(35.95, 17.35) * mm, "end": v(35.96, 17.35) * mm});
            skLineSegment(sketch, "E1614", {"start": v(35.96, 17.35) * mm, "end": v(35.97, 17.35) * mm});
            skLineSegment(sketch, "E1615", {"start": v(35.97, 17.35) * mm, "end": v(35.98, 17.36) * mm});
            skLineSegment(sketch, "E1616", {"start": v(35.98, 17.36) * mm, "end": v(35.99, 17.36) * mm});
            skLineSegment(sketch, "E1617", {"start": v(35.99, 17.36) * mm, "end": v(36, 17.36) * mm});
            skLineSegment(sketch, "E1618", {"start": v(36, 17.36) * mm, "end": v(36, 17.36) * mm});
            skLineSegment(sketch, "E1619", {"start": v(36, 17.36) * mm, "end": v(36.02, 17.36) * mm});
            skLineSegment(sketch, "E1620", {"start": v(36.02, 17.36) * mm, "end": v(36.03, 17.37) * mm});
            skLineSegment(sketch, "E1621", {"start": v(36.03, 17.37) * mm, "end": v(36.04, 17.37) * mm});
            skLineSegment(sketch, "E1622", {"start": v(36.04, 17.37) * mm, "end": v(36.05, 17.37) * mm});
            skLineSegment(sketch, "E1623", {"start": v(36.05, 17.37) * mm, "end": v(36.06, 17.37) * mm});
            skLineSegment(sketch, "E1624", {"start": v(36.06, 17.37) * mm, "end": v(36.07, 17.38) * mm});
            skLineSegment(sketch, "E1625", {"start": v(36.07, 17.38) * mm, "end": v(36.08, 17.38) * mm});
            skLineSegment(sketch, "E1626", {"start": v(36.08, 17.38) * mm, "end": v(36.09, 17.38) * mm});
            skLineSegment(sketch, "E1627", {"start": v(36.09, 17.38) * mm, "end": v(36.1, 17.38) * mm});
            skLineSegment(sketch, "E1628", {"start": v(36.1, 17.38) * mm, "end": v(36.1, 17.38) * mm});
            skLineSegment(sketch, "E1629", {"start": v(36.1, 17.38) * mm, "end": v(36.12, 17.39) * mm});
            skLineSegment(sketch, "E1630", {"start": v(36.12, 17.39) * mm, "end": v(36.13, 17.39) * mm});
            skLineSegment(sketch, "E1631", {"start": v(36.13, 17.39) * mm, "end": v(36.14, 17.4) * mm});
            skLineSegment(sketch, "E1632", {"start": v(36.14, 17.4) * mm, "end": v(36.15, 17.4) * mm});
            skLineSegment(sketch, "E1633", {"start": v(36.15, 17.4) * mm, "end": v(36.16, 17.4) * mm});
            skLineSegment(sketch, "E1634", {"start": v(36.16, 17.4) * mm, "end": v(36.17, 17.4) * mm});
            skLineSegment(sketch, "E1635", {"start": v(36.17, 17.4) * mm, "end": v(36.18, 17.4) * mm});
            skLineSegment(sketch, "E1636", {"start": v(36.18, 17.4) * mm, "end": v(36.19, 17.4) * mm});
            skLineSegment(sketch, "E1637", {"start": v(36.19, 17.4) * mm, "end": v(36.2, 17.4) * mm});
            skLineSegment(sketch, "E1638", {"start": v(36.2, 17.4) * mm, "end": v(36.2, 17.4) * mm});
            skLineSegment(sketch, "E1639", {"start": v(36.2, 17.4) * mm, "end": v(36.22, 17.4) * mm});
            skLineSegment(sketch, "E1640", {"start": v(36.22, 17.4) * mm, "end": v(36.23, 17.41) * mm});
            skLineSegment(sketch, "E1641", {"start": v(36.23, 17.41) * mm, "end": v(36.24, 17.41) * mm});
            skLineSegment(sketch, "E1642", {"start": v(36.24, 17.41) * mm, "end": v(36.25, 17.42) * mm});
            skLineSegment(sketch, "E1643", {"start": v(36.25, 17.42) * mm, "end": v(36.26, 17.42) * mm});
            skLineSegment(sketch, "E1644", {"start": v(36.26, 17.42) * mm, "end": v(36.27, 17.42) * mm});
            skLineSegment(sketch, "E1645", {"start": v(36.27, 17.42) * mm, "end": v(36.28, 17.42) * mm});
            skLineSegment(sketch, "E1646", {"start": v(36.28, 17.42) * mm, "end": v(36.29, 17.43) * mm});
            skLineSegment(sketch, "E1647", {"start": v(36.29, 17.43) * mm, "end": v(36.3, 17.43) * mm});
            skLineSegment(sketch, "E1648", {"start": v(36.3, 17.43) * mm, "end": v(36.3, 17.43) * mm});
            skLineSegment(sketch, "E1649", {"start": v(36.3, 17.43) * mm, "end": v(36.32, 17.43) * mm});
            skLineSegment(sketch, "E1650", {"start": v(36.32, 17.43) * mm, "end": v(36.33, 17.43) * mm});
            skLineSegment(sketch, "E1651", {"start": v(36.33, 17.43) * mm, "end": v(36.34, 17.44) * mm});
            skLineSegment(sketch, "E1652", {"start": v(36.34, 17.44) * mm, "end": v(36.35, 17.44) * mm});
            skLineSegment(sketch, "E1653", {"start": v(36.35, 17.44) * mm, "end": v(36.31, 17.45) * mm});
            skLineSegment(sketch, "E1654", {"start": v(36.31, 17.45) * mm, "end": v(36.28, 17.45) * mm});
            skLineSegment(sketch, "E1655", {"start": v(36.28, 17.45) * mm, "end": v(36.24, 17.46) * mm});
            skLineSegment(sketch, "E1656", {"start": v(36.24, 17.46) * mm, "end": v(36.2, 17.46) * mm});
            skLineSegment(sketch, "E1657", {"start": v(36.2, 17.46) * mm, "end": v(36.17, 17.47) * mm});
            skLineSegment(sketch, "E1658", {"start": v(36.17, 17.47) * mm, "end": v(36.13, 17.48) * mm});
            skLineSegment(sketch, "E1659", {"start": v(36.13, 17.48) * mm, "end": v(36.1, 17.48) * mm});
            skLineSegment(sketch, "E1660", {"start": v(36.1, 17.48) * mm, "end": v(36.06, 17.49) * mm});
            skLineSegment(sketch, "E1661", {"start": v(36.06, 17.49) * mm, "end": v(36.03, 17.5) * mm});
            skLineSegment(sketch, "E1662", {"start": v(36.03, 17.5) * mm, "end": v(36, 17.5) * mm});
            skLineSegment(sketch, "E1663", {"start": v(36, 17.5) * mm, "end": v(35.95, 17.5) * mm});
            skLineSegment(sketch, "E1664", {"start": v(35.95, 17.5) * mm, "end": v(35.92, 17.51) * mm});
            skLineSegment(sketch, "E1665", {"start": v(35.92, 17.51) * mm, "end": v(35.88, 17.52) * mm});
            skLineSegment(sketch, "E1666", {"start": v(35.88, 17.52) * mm, "end": v(35.85, 17.52) * mm});
            skLineSegment(sketch, "E1667", {"start": v(35.85, 17.52) * mm, "end": v(35.8, 17.53) * mm});
            skLineSegment(sketch, "E1668", {"start": v(35.8, 17.53) * mm, "end": v(35.77, 17.53) * mm});
            skLineSegment(sketch, "E1669", {"start": v(35.77, 17.53) * mm, "end": v(35.74, 17.54) * mm});
            skLineSegment(sketch, "E1670", {"start": v(35.74, 17.54) * mm, "end": v(35.7, 17.54) * mm});
            skLineSegment(sketch, "E1671", {"start": v(35.7, 17.54) * mm, "end": v(35.66, 17.55) * mm});
            skLineSegment(sketch, "E1672", {"start": v(35.66, 17.55) * mm, "end": v(35.63, 17.55) * mm});
            skLineSegment(sketch, "E1673", {"start": v(35.63, 17.55) * mm, "end": v(35.6, 17.56) * mm});
            skLineSegment(sketch, "E1674", {"start": v(35.6, 17.56) * mm, "end": v(35.56, 17.57) * mm});
            skLineSegment(sketch, "E1675", {"start": v(35.56, 17.57) * mm, "end": v(35.52, 17.57) * mm});
            skLineSegment(sketch, "E1676", {"start": v(35.52, 17.57) * mm, "end": v(35.48, 17.58) * mm});
            skLineSegment(sketch, "E1677", {"start": v(35.48, 17.58) * mm, "end": v(35.45, 17.58) * mm});
            skLineSegment(sketch, "E1678", {"start": v(35.45, 17.58) * mm, "end": v(35.4, 17.59) * mm});
            skLineSegment(sketch, "E1679", {"start": v(35.4, 17.59) * mm, "end": v(35.37, 17.6) * mm});
            skLineSegment(sketch, "E1680", {"start": v(35.37, 17.6) * mm, "end": v(35.34, 17.6) * mm});
            skLineSegment(sketch, "E1681", {"start": v(35.34, 17.6) * mm, "end": v(35.3, 17.6) * mm});
            skLineSegment(sketch, "E1682", {"start": v(35.3, 17.6) * mm, "end": v(35.26, 17.6) * mm});
            skLineSegment(sketch, "E1683", {"start": v(35.26, 17.6) * mm, "end": v(35.23, 17.61) * mm});
            skLineSegment(sketch, "E1684", {"start": v(35.23, 17.61) * mm, "end": v(35.19, 17.61) * mm});
            skLineSegment(sketch, "E1685", {"start": v(35.19, 17.61) * mm, "end": v(35.15, 17.62) * mm});
            skLineSegment(sketch, "E1686", {"start": v(35.15, 17.62) * mm, "end": v(35.12, 17.62) * mm});
            skLineSegment(sketch, "E1687", {"start": v(35.12, 17.62) * mm, "end": v(35.08, 17.63) * mm});
            skLineSegment(sketch, "E1688", {"start": v(35.08, 17.63) * mm, "end": v(35.04, 17.63) * mm});
            skLineSegment(sketch, "E1689", {"start": v(35.04, 17.63) * mm, "end": v(35, 17.64) * mm});
            skLineSegment(sketch, "E1690", {"start": v(35, 17.64) * mm, "end": v(34.97, 17.64) * mm});
            skLineSegment(sketch, "E1691", {"start": v(34.97, 17.64) * mm, "end": v(34.93, 17.65) * mm});
            skLineSegment(sketch, "E1692", {"start": v(34.93, 17.65) * mm, "end": v(34.9, 17.65) * mm});
            skLineSegment(sketch, "E1693", {"start": v(34.9, 17.65) * mm, "end": v(34.86, 17.66) * mm});
            skLineSegment(sketch, "E1694", {"start": v(34.86, 17.66) * mm, "end": v(34.82, 17.66) * mm});
            skLineSegment(sketch, "E1695", {"start": v(34.82, 17.66) * mm, "end": v(34.78, 17.66) * mm});
            skLineSegment(sketch, "E1696", {"start": v(34.78, 17.66) * mm, "end": v(34.75, 17.67) * mm});
            skLineSegment(sketch, "E1697", {"start": v(34.75, 17.67) * mm, "end": v(34.7, 17.67) * mm});
            skLineSegment(sketch, "E1698", {"start": v(34.7, 17.67) * mm, "end": v(34.67, 17.68) * mm});
            skLineSegment(sketch, "E1699", {"start": v(34.67, 17.68) * mm, "end": v(34.63, 17.68) * mm});
            skLineSegment(sketch, "E1700", {"start": v(34.63, 17.68) * mm, "end": v(34.6, 17.68) * mm});
            skLineSegment(sketch, "E1701", {"start": v(34.6, 17.68) * mm, "end": v(34.56, 17.69) * mm});
            skLineSegment(sketch, "E1702", {"start": v(34.56, 17.69) * mm, "end": v(34.52, 17.7) * mm});
            skLineSegment(sketch, "E1703", {"start": v(34.52, 17.7) * mm, "end": v(34.49, 17.7) * mm});
            skLineSegment(sketch, "E1704", {"start": v(34.49, 17.7) * mm, "end": v(34.45, 17.7) * mm});
            skLineSegment(sketch, "E1705", {"start": v(34.45, 17.7) * mm, "end": v(34.41, 17.7) * mm});
            skLineSegment(sketch, "E1706", {"start": v(34.41, 17.7) * mm, "end": v(34.37, 17.7) * mm});
            skLineSegment(sketch, "E1707", {"start": v(34.37, 17.7) * mm, "end": v(34.34, 17.71) * mm});
            skLineSegment(sketch, "E1708", {"start": v(34.34, 17.71) * mm, "end": v(34.3, 17.71) * mm});
            skLineSegment(sketch, "E1709", {"start": v(34.3, 17.71) * mm, "end": v(34.26, 17.72) * mm});
            skLineSegment(sketch, "E1710", {"start": v(34.26, 17.72) * mm, "end": v(34.22, 17.72) * mm});
            skLineSegment(sketch, "E1711", {"start": v(34.22, 17.72) * mm, "end": v(34.19, 17.72) * mm});
            skLineSegment(sketch, "E1712", {"start": v(34.19, 17.72) * mm, "end": v(34.15, 17.73) * mm});
            skLineSegment(sketch, "E1713", {"start": v(34.15, 17.73) * mm, "end": v(34.1, 17.73) * mm});
            skLineSegment(sketch, "E1714", {"start": v(34.1, 17.73) * mm, "end": v(34.07, 17.73) * mm});
            skLineSegment(sketch, "E1715", {"start": v(34.07, 17.73) * mm, "end": v(34.03, 17.74) * mm});
            skLineSegment(sketch, "E1716", {"start": v(34.03, 17.74) * mm, "end": v(34, 17.74) * mm});
            skLineSegment(sketch, "E1717", {"start": v(34, 17.74) * mm, "end": v(33.96, 17.74) * mm});
            skLineSegment(sketch, "E1718", {"start": v(33.96, 17.74) * mm, "end": v(33.92, 17.75) * mm});
            skLineSegment(sketch, "E1719", {"start": v(33.92, 17.75) * mm, "end": v(33.88, 17.75) * mm});
            skLineSegment(sketch, "E1720", {"start": v(33.88, 17.75) * mm, "end": v(33.85, 17.75) * mm});
            skLineSegment(sketch, "E1721", {"start": v(33.85, 17.75) * mm, "end": v(33.8, 17.76) * mm});
            skLineSegment(sketch, "E1722", {"start": v(33.8, 17.76) * mm, "end": v(33.77, 17.76) * mm});
            skLineSegment(sketch, "E1723", {"start": v(33.77, 17.76) * mm, "end": v(33.73, 17.76) * mm});
            skLineSegment(sketch, "E1724", {"start": v(33.73, 17.76) * mm, "end": v(33.7, 17.76) * mm});
            skLineSegment(sketch, "E1725", {"start": v(33.7, 17.76) * mm, "end": v(33.66, 17.77) * mm});
            skLineSegment(sketch, "E1726", {"start": v(33.66, 17.77) * mm, "end": v(33.62, 17.77) * mm});
            skLineSegment(sketch, "E1727", {"start": v(33.62, 17.77) * mm, "end": v(33.58, 17.77) * mm});
            skLineSegment(sketch, "E1728", {"start": v(33.58, 17.77) * mm, "end": v(33.54, 17.78) * mm});
            skLineSegment(sketch, "E1729", {"start": v(33.54, 17.78) * mm, "end": v(33.5, 17.78) * mm});
            skLineSegment(sketch, "E1730", {"start": v(33.5, 17.78) * mm, "end": v(33.46, 17.78) * mm});
            skLineSegment(sketch, "E1731", {"start": v(33.46, 17.78) * mm, "end": v(33.43, 17.78) * mm});
            skLineSegment(sketch, "E1732", {"start": v(33.43, 17.78) * mm, "end": v(33.39, 17.79) * mm});
            skLineSegment(sketch, "E1733", {"start": v(33.39, 17.79) * mm, "end": v(33.35, 17.79) * mm});
            skLineSegment(sketch, "E1734", {"start": v(33.35, 17.79) * mm, "end": v(33.31, 17.79) * mm});
            skLineSegment(sketch, "E1735", {"start": v(33.31, 17.79) * mm, "end": v(33.27, 17.8) * mm});
            skLineSegment(sketch, "E1736", {"start": v(33.27, 17.8) * mm, "end": v(33.24, 17.8) * mm});
            skLineSegment(sketch, "E1737", {"start": v(33.24, 17.8) * mm, "end": v(33.2, 17.8) * mm});
            skLineSegment(sketch, "E1738", {"start": v(33.2, 17.8) * mm, "end": v(33.16, 17.8) * mm});
            skLineSegment(sketch, "E1739", {"start": v(33.16, 17.8) * mm, "end": v(33.12, 17.8) * mm});
            skLineSegment(sketch, "E1740", {"start": v(33.12, 17.8) * mm, "end": v(33.08, 17.8) * mm});
            skLineSegment(sketch, "E1741", {"start": v(33.08, 17.8) * mm, "end": v(33.04, 17.8) * mm});
            skLineSegment(sketch, "E1742", {"start": v(33.04, 17.8) * mm, "end": v(33, 17.8) * mm});
            skLineSegment(sketch, "E1743", {"start": v(33, 17.8) * mm, "end": v(32.97, 17.8) * mm});
            skLineSegment(sketch, "E1744", {"start": v(32.97, 17.8) * mm, "end": v(32.93, 17.8) * mm});
            skLineSegment(sketch, "E1745", {"start": v(32.93, 17.8) * mm, "end": v(32.89, 17.81) * mm});
            skLineSegment(sketch, "E1746", {"start": v(32.89, 17.81) * mm, "end": v(32.85, 17.81) * mm});
            skLineSegment(sketch, "E1747", {"start": v(32.85, 17.81) * mm, "end": v(32.81, 17.81) * mm});
            skLineSegment(sketch, "E1748", {"start": v(32.81, 17.81) * mm, "end": v(32.77, 17.82) * mm});
            skLineSegment(sketch, "E1749", {"start": v(32.77, 17.82) * mm, "end": v(32.73, 17.82) * mm});
            skLineSegment(sketch, "E1750", {"start": v(32.73, 17.82) * mm, "end": v(32.7, 17.82) * mm});
            skLineSegment(sketch, "E1751", {"start": v(32.7, 17.82) * mm, "end": v(32.66, 17.82) * mm});
            skLineSegment(sketch, "E1752", {"start": v(32.66, 17.82) * mm, "end": v(32.62, 17.82) * mm});
            skLineSegment(sketch, "E1753", {"start": v(32.62, 17.82) * mm, "end": v(32.58, 17.82) * mm});
            skLineSegment(sketch, "E1754", {"start": v(32.58, 17.82) * mm, "end": v(32.54, 17.83) * mm});
            skLineSegment(sketch, "E1755", {"start": v(32.54, 17.83) * mm, "end": v(32.5, 17.83) * mm});
            skLineSegment(sketch, "E1756", {"start": v(32.5, 17.83) * mm, "end": v(32.46, 17.83) * mm});
            skLineSegment(sketch, "E1757", {"start": v(32.46, 17.83) * mm, "end": v(32.42, 17.83) * mm});
            skLineSegment(sketch, "E1758", {"start": v(32.42, 17.83) * mm, "end": v(32.38, 17.83) * mm});
            skLineSegment(sketch, "E1759", {"start": v(32.38, 17.83) * mm, "end": v(32.35, 17.83) * mm});
            skLineSegment(sketch, "E1760", {"start": v(32.35, 17.83) * mm, "end": v(32.3, 17.83) * mm});
            skLineSegment(sketch, "E1761", {"start": v(32.3, 17.83) * mm, "end": v(32.27, 17.83) * mm});
            skLineSegment(sketch, "E1762", {"start": v(32.27, 17.83) * mm, "end": v(32.23, 17.83) * mm});
            skLineSegment(sketch, "E1763", {"start": v(32.23, 17.83) * mm, "end": v(32.19, 17.83) * mm});
            skLineSegment(sketch, "E1764", {"start": v(32.19, 17.83) * mm, "end": v(32.15, 17.84) * mm});
            skLineSegment(sketch, "E1765", {"start": v(32.15, 17.84) * mm, "end": v(32.11, 17.84) * mm});
            skLineSegment(sketch, "E1766", {"start": v(32.11, 17.84) * mm, "end": v(32.07, 17.84) * mm});
            skLineSegment(sketch, "E1767", {"start": v(32.07, 17.84) * mm, "end": v(32.03, 17.84) * mm});
            skLineSegment(sketch, "E1768", {"start": v(32.03, 17.84) * mm, "end": v(32, 17.84) * mm});
            skLineSegment(sketch, "E1769", {"start": v(32, 17.84) * mm, "end": v(31.95, 17.84) * mm});
            skLineSegment(sketch, "E1770", {"start": v(31.95, 17.84) * mm, "end": v(31.91, 17.84) * mm});
            skLineSegment(sketch, "E1771", {"start": v(31.91, 17.84) * mm, "end": v(31.88, 17.84) * mm});
            skLineSegment(sketch, "E1772", {"start": v(31.88, 17.84) * mm, "end": v(31.84, 17.84) * mm});
            skLineSegment(sketch, "E1773", {"start": v(31.84, 17.84) * mm, "end": v(31.8, 17.84) * mm});
            skLineSegment(sketch, "E1774", {"start": v(31.8, 17.84) * mm, "end": v(31.76, 17.84) * mm});
            skLineSegment(sketch, "E1775", {"start": v(31.76, 17.84) * mm, "end": v(31.72, 17.84) * mm});
            skLineSegment(sketch, "E1776", {"start": v(31.72, 17.84) * mm, "end": v(31.68, 17.84) * mm});
            skLineSegment(sketch, "E1777", {"start": v(31.68, 17.84) * mm, "end": v(31.64, 17.84) * mm});
            skLineSegment(sketch, "E1778", {"start": v(31.64, 17.84) * mm, "end": v(31.6, 17.84) * mm});
            skLineSegment(sketch, "E1779", {"start": v(31.6, 17.84) * mm, "end": v(31.56, 17.84) * mm});
            skLineSegment(sketch, "E1780", {"start": v(31.56, 17.84) * mm, "end": v(31.52, 17.84) * mm});
            skLineSegment(sketch, "E1781", {"start": v(31.52, 17.84) * mm, "end": v(31.45, 17.84) * mm});
            skLineSegment(sketch, "E1782", {"start": v(31.45, 17.84) * mm, "end": v(31.38, 17.84) * mm});
            skLineSegment(sketch, "E1783", {"start": v(31.38, 17.84) * mm, "end": v(31.3, 17.84) * mm});
            skLineSegment(sketch, "E1784", {"start": v(31.3, 17.84) * mm, "end": v(31.24, 17.84) * mm});
            skLineSegment(sketch, "E1785", {"start": v(31.24, 17.84) * mm, "end": v(31.17, 17.84) * mm});
            skLineSegment(sketch, "E1786", {"start": v(31.17, 17.84) * mm, "end": v(31.1, 17.84) * mm});
            skLineSegment(sketch, "E1787", {"start": v(31.1, 17.84) * mm, "end": v(31.03, 17.84) * mm});
            skLineSegment(sketch, "E1788", {"start": v(31.03, 17.84) * mm, "end": v(30.95, 17.84) * mm});
            skLineSegment(sketch, "E1789", {"start": v(30.95, 17.84) * mm, "end": v(30.88, 17.84) * mm});
            skLineSegment(sketch, "E1790", {"start": v(30.88, 17.84) * mm, "end": v(30.81, 17.83) * mm});
            skLineSegment(sketch, "E1791", {"start": v(30.81, 17.83) * mm, "end": v(30.74, 17.83) * mm});
            skLineSegment(sketch, "E1792", {"start": v(30.74, 17.83) * mm, "end": v(30.67, 17.83) * mm});
            skLineSegment(sketch, "E1793", {"start": v(30.67, 17.83) * mm, "end": v(30.6, 17.83) * mm});
            skLineSegment(sketch, "E1794", {"start": v(30.6, 17.83) * mm, "end": v(30.53, 17.83) * mm});
            skLineSegment(sketch, "E1795", {"start": v(30.53, 17.83) * mm, "end": v(30.46, 17.83) * mm});
            skLineSegment(sketch, "E1796", {"start": v(30.46, 17.83) * mm, "end": v(30.38, 17.82) * mm});
            skLineSegment(sketch, "E1797", {"start": v(30.38, 17.82) * mm, "end": v(30.31, 17.82) * mm});
            skLineSegment(sketch, "E1798", {"start": v(30.31, 17.82) * mm, "end": v(30.24, 17.82) * mm});
            skLineSegment(sketch, "E1799", {"start": v(30.24, 17.82) * mm, "end": v(30.17, 17.81) * mm});
            skLineSegment(sketch, "E1800", {"start": v(30.17, 17.81) * mm, "end": v(30.1, 17.81) * mm});
            skLineSegment(sketch, "E1801", {"start": v(30.1, 17.81) * mm, "end": v(30.02, 17.8) * mm});
            skLineSegment(sketch, "E1802", {"start": v(30.02, 17.8) * mm, "end": v(29.95, 17.8) * mm});
            skLineSegment(sketch, "E1803", {"start": v(29.95, 17.8) * mm, "end": v(29.88, 17.8) * mm});
            skLineSegment(sketch, "E1804", {"start": v(29.88, 17.8) * mm, "end": v(29.8, 17.8) * mm});
            skLineSegment(sketch, "E1805", {"start": v(29.8, 17.8) * mm, "end": v(29.73, 17.8) * mm});
            skLineSegment(sketch, "E1806", {"start": v(29.73, 17.8) * mm, "end": v(29.66, 17.8) * mm});
            skLineSegment(sketch, "E1807", {"start": v(29.66, 17.8) * mm, "end": v(29.59, 17.79) * mm});
            skLineSegment(sketch, "E1808", {"start": v(29.59, 17.79) * mm, "end": v(29.52, 17.78) * mm});
            skLineSegment(sketch, "E1809", {"start": v(29.52, 17.78) * mm, "end": v(29.44, 17.78) * mm});
            skLineSegment(sketch, "E1810", {"start": v(29.44, 17.78) * mm, "end": v(29.37, 17.77) * mm});
            skLineSegment(sketch, "E1811", {"start": v(29.37, 17.77) * mm, "end": v(29.3, 17.77) * mm});
            skLineSegment(sketch, "E1812", {"start": v(29.3, 17.77) * mm, "end": v(29.23, 17.76) * mm});
            skLineSegment(sketch, "E1813", {"start": v(29.23, 17.76) * mm, "end": v(29.15, 17.76) * mm});
            skLineSegment(sketch, "E1814", {"start": v(29.15, 17.76) * mm, "end": v(29.08, 17.75) * mm});
            skLineSegment(sketch, "E1815", {"start": v(29.08, 17.75) * mm, "end": v(29, 17.75) * mm});
            skLineSegment(sketch, "E1816", {"start": v(29, 17.75) * mm, "end": v(28.93, 17.74) * mm});
            skLineSegment(sketch, "E1817", {"start": v(28.93, 17.74) * mm, "end": v(28.86, 17.74) * mm});
            skLineSegment(sketch, "E1818", {"start": v(28.86, 17.74) * mm, "end": v(28.79, 17.73) * mm});
            skLineSegment(sketch, "E1819", {"start": v(28.79, 17.73) * mm, "end": v(28.71, 17.73) * mm});
            skLineSegment(sketch, "E1820", {"start": v(28.71, 17.73) * mm, "end": v(28.64, 17.72) * mm});
            skLineSegment(sketch, "E1821", {"start": v(28.64, 17.72) * mm, "end": v(28.56, 17.72) * mm});
            skLineSegment(sketch, "E1822", {"start": v(28.56, 17.72) * mm, "end": v(28.49, 17.7) * mm});
            skLineSegment(sketch, "E1823", {"start": v(28.49, 17.7) * mm, "end": v(28.42, 17.7) * mm});
            skLineSegment(sketch, "E1824", {"start": v(28.42, 17.7) * mm, "end": v(28.34, 17.7) * mm});
            skLineSegment(sketch, "E1825", {"start": v(28.34, 17.7) * mm, "end": v(28.27, 17.69) * mm});
            skLineSegment(sketch, "E1826", {"start": v(28.27, 17.69) * mm, "end": v(28.2, 17.68) * mm});
            skLineSegment(sketch, "E1827", {"start": v(28.2, 17.68) * mm, "end": v(28.12, 17.68) * mm});
            skLineSegment(sketch, "E1828", {"start": v(28.12, 17.68) * mm, "end": v(28.04, 17.67) * mm});
            skLineSegment(sketch, "E1829", {"start": v(28.04, 17.67) * mm, "end": v(27.97, 17.66) * mm});
            skLineSegment(sketch, "E1830", {"start": v(27.97, 17.66) * mm, "end": v(27.9, 17.65) * mm});
            skLineSegment(sketch, "E1831", {"start": v(27.9, 17.65) * mm, "end": v(27.82, 17.65) * mm});
            skLineSegment(sketch, "E1832", {"start": v(27.82, 17.65) * mm, "end": v(27.74, 17.64) * mm});
            skLineSegment(sketch, "E1833", {"start": v(27.74, 17.64) * mm, "end": v(27.67, 17.63) * mm});
            skLineSegment(sketch, "E1834", {"start": v(27.67, 17.63) * mm, "end": v(27.6, 17.62) * mm});
            skLineSegment(sketch, "E1835", {"start": v(27.6, 17.62) * mm, "end": v(27.52, 17.61) * mm});
            skLineSegment(sketch, "E1836", {"start": v(27.52, 17.61) * mm, "end": v(27.44, 17.6) * mm});
            skLineSegment(sketch, "E1837", {"start": v(27.44, 17.6) * mm, "end": v(27.37, 17.6) * mm});
            skLineSegment(sketch, "E1838", {"start": v(27.37, 17.6) * mm, "end": v(27.3, 17.59) * mm});
            skLineSegment(sketch, "E1839", {"start": v(27.3, 17.59) * mm, "end": v(27.22, 17.58) * mm});
            skLineSegment(sketch, "E1840", {"start": v(27.22, 17.58) * mm, "end": v(27.14, 17.57) * mm});
            skLineSegment(sketch, "E1841", {"start": v(27.14, 17.57) * mm, "end": v(27.07, 17.56) * mm});
            skLineSegment(sketch, "E1842", {"start": v(27.07, 17.56) * mm, "end": v(26.99, 17.55) * mm});
            skLineSegment(sketch, "E1843", {"start": v(26.99, 17.55) * mm, "end": v(26.91, 17.54) * mm});
            skLineSegment(sketch, "E1844", {"start": v(26.91, 17.54) * mm, "end": v(26.84, 17.53) * mm});
            skLineSegment(sketch, "E1845", {"start": v(26.84, 17.53) * mm, "end": v(26.76, 17.52) * mm});
            skLineSegment(sketch, "E1846", {"start": v(26.76, 17.52) * mm, "end": v(26.68, 17.51) * mm});
            skLineSegment(sketch, "E1847", {"start": v(26.68, 17.51) * mm, "end": v(26.6, 17.5) * mm});
            skLineSegment(sketch, "E1848", {"start": v(26.6, 17.5) * mm, "end": v(26.53, 17.5) * mm});
            skLineSegment(sketch, "E1849", {"start": v(26.53, 17.5) * mm, "end": v(26.45, 17.48) * mm});
            skLineSegment(sketch, "E1850", {"start": v(26.45, 17.48) * mm, "end": v(26.38, 17.47) * mm});
            skLineSegment(sketch, "E1851", {"start": v(26.38, 17.47) * mm, "end": v(26.3, 17.46) * mm});
            skLineSegment(sketch, "E1852", {"start": v(26.3, 17.46) * mm, "end": v(26.22, 17.45) * mm});
            skLineSegment(sketch, "E1853", {"start": v(26.22, 17.45) * mm, "end": v(26.15, 17.44) * mm});
            skLineSegment(sketch, "E1854", {"start": v(26.15, 17.44) * mm, "end": v(26.07, 17.43) * mm});
            skLineSegment(sketch, "E1855", {"start": v(26.07, 17.43) * mm, "end": v(26, 17.42) * mm});
            skLineSegment(sketch, "E1856", {"start": v(26, 17.42) * mm, "end": v(25.91, 17.4) * mm});
            skLineSegment(sketch, "E1857", {"start": v(25.91, 17.4) * mm, "end": v(25.84, 17.4) * mm});
            skLineSegment(sketch, "E1858", {"start": v(25.84, 17.4) * mm, "end": v(25.76, 17.38) * mm});
            skLineSegment(sketch, "E1859", {"start": v(25.76, 17.38) * mm, "end": v(25.68, 17.37) * mm});
            skLineSegment(sketch, "E1860", {"start": v(25.68, 17.37) * mm, "end": v(25.6, 17.36) * mm});
            skLineSegment(sketch, "E1861", {"start": v(25.6, 17.36) * mm, "end": v(25.52, 17.34) * mm});
            skLineSegment(sketch, "E1862", {"start": v(25.52, 17.34) * mm, "end": v(25.45, 17.33) * mm});
            skLineSegment(sketch, "E1863", {"start": v(25.45, 17.33) * mm, "end": v(25.37, 17.32) * mm});
            skLineSegment(sketch, "E1864", {"start": v(25.37, 17.32) * mm, "end": v(25.29, 17.3) * mm});
            skLineSegment(sketch, "E1865", {"start": v(25.29, 17.3) * mm, "end": v(25.21, 17.3) * mm});
            skLineSegment(sketch, "E1866", {"start": v(25.21, 17.3) * mm, "end": v(25.13, 17.28) * mm});
            skLineSegment(sketch, "E1867", {"start": v(25.13, 17.28) * mm, "end": v(25.05, 17.27) * mm});
            skLineSegment(sketch, "E1868", {"start": v(25.05, 17.27) * mm, "end": v(24.97, 17.25) * mm});
            skLineSegment(sketch, "E1869", {"start": v(24.97, 17.25) * mm, "end": v(24.9, 17.24) * mm});
            skLineSegment(sketch, "E1870", {"start": v(24.9, 17.24) * mm, "end": v(24.82, 17.23) * mm});
            skLineSegment(sketch, "E1871", {"start": v(24.82, 17.23) * mm, "end": v(24.74, 17.21) * mm});
            skLineSegment(sketch, "E1872", {"start": v(24.74, 17.21) * mm, "end": v(24.66, 17.2) * mm});
            skLineSegment(sketch, "E1873", {"start": v(24.66, 17.2) * mm, "end": v(24.58, 17.19) * mm});
            skLineSegment(sketch, "E1874", {"start": v(24.58, 17.19) * mm, "end": v(24.5, 17.17) * mm});
            skLineSegment(sketch, "E1875", {"start": v(24.5, 17.17) * mm, "end": v(24.42, 17.16) * mm});
            skLineSegment(sketch, "E1876", {"start": v(24.42, 17.16) * mm, "end": v(24.34, 17.14) * mm});
            skLineSegment(sketch, "E1877", {"start": v(24.34, 17.14) * mm, "end": v(24.26, 17.13) * mm});
            skLineSegment(sketch, "E1878", {"start": v(24.26, 17.13) * mm, "end": v(24.18, 17.11) * mm});
            skLineSegment(sketch, "E1879", {"start": v(24.18, 17.11) * mm, "end": v(24.1, 17.1) * mm});
            skLineSegment(sketch, "E1880", {"start": v(24.1, 17.1) * mm, "end": v(24.02, 17.08) * mm});
            skLineSegment(sketch, "E1881", {"start": v(24.02, 17.08) * mm, "end": v(23.94, 17.07) * mm});
            skLineSegment(sketch, "E1882", {"start": v(23.94, 17.07) * mm, "end": v(23.86, 17.05) * mm});
            skLineSegment(sketch, "E1883", {"start": v(23.86, 17.05) * mm, "end": v(23.77, 17.04) * mm});
            skLineSegment(sketch, "E1884", {"start": v(23.77, 17.04) * mm, "end": v(23.7, 17.02) * mm});
            skLineSegment(sketch, "E1885", {"start": v(23.7, 17.02) * mm, "end": v(23.61, 17) * mm});
            skLineSegment(sketch, "E1886", {"start": v(23.61, 17) * mm, "end": v(23.53, 16.99) * mm});
            skLineSegment(sketch, "E1887", {"start": v(23.53, 16.99) * mm, "end": v(23.45, 16.97) * mm});
            skLineSegment(sketch, "E1888", {"start": v(23.45, 16.97) * mm, "end": v(23.37, 16.96) * mm});
            skLineSegment(sketch, "E1889", {"start": v(23.37, 16.96) * mm, "end": v(23.29, 16.94) * mm});
            skLineSegment(sketch, "E1890", {"start": v(23.29, 16.94) * mm, "end": v(23.2, 16.92) * mm});
            skLineSegment(sketch, "E1891", {"start": v(23.2, 16.92) * mm, "end": v(23.12, 16.9) * mm});
            skLineSegment(sketch, "E1892", {"start": v(23.12, 16.9) * mm, "end": v(23.04, 16.89) * mm});
            skLineSegment(sketch, "E1893", {"start": v(23.04, 16.89) * mm, "end": v(22.96, 16.87) * mm});
            skLineSegment(sketch, "E1894", {"start": v(22.96, 16.87) * mm, "end": v(22.88, 16.85) * mm});
            skLineSegment(sketch, "E1895", {"start": v(22.88, 16.85) * mm, "end": v(22.8, 16.84) * mm});
            skLineSegment(sketch, "E1896", {"start": v(22.8, 16.84) * mm, "end": v(22.71, 16.82) * mm});
            skLineSegment(sketch, "E1897", {"start": v(22.71, 16.82) * mm, "end": v(22.63, 16.8) * mm});
            skLineSegment(sketch, "E1898", {"start": v(22.63, 16.8) * mm, "end": v(22.55, 16.78) * mm});
            skLineSegment(sketch, "E1899", {"start": v(22.55, 16.78) * mm, "end": v(22.46, 16.76) * mm});
            skLineSegment(sketch, "E1900", {"start": v(22.46, 16.76) * mm, "end": v(22.38, 16.75) * mm});
            skLineSegment(sketch, "E1901", {"start": v(22.38, 16.75) * mm, "end": v(22.3, 16.73) * mm});
            skLineSegment(sketch, "E1902", {"start": v(22.3, 16.73) * mm, "end": v(22.21, 16.7) * mm});
            skLineSegment(sketch, "E1903", {"start": v(22.21, 16.7) * mm, "end": v(22.13, 16.69) * mm});
            skLineSegment(sketch, "E1904", {"start": v(22.13, 16.69) * mm, "end": v(22.05, 16.67) * mm});
            skLineSegment(sketch, "E1905", {"start": v(22.05, 16.67) * mm, "end": v(21.96, 16.65) * mm});
            skLineSegment(sketch, "E1906", {"start": v(21.96, 16.65) * mm, "end": v(21.88, 16.63) * mm});
            skLineSegment(sketch, "E1907", {"start": v(21.88, 16.63) * mm, "end": v(21.8, 16.61) * mm});
            skLineSegment(sketch, "E1908", {"start": v(21.8, 16.61) * mm, "end": v(21.71, 16.6) * mm});
            skLineSegment(sketch, "E1909", {"start": v(21.71, 16.6) * mm, "end": v(21.5, 16.54) * mm});
            skLineSegment(sketch, "E1910", {"start": v(21.5, 16.54) * mm, "end": v(21.27, 16.49) * mm});
            skLineSegment(sketch, "E1911", {"start": v(21.27, 16.49) * mm, "end": v(21.05, 16.43) * mm});
            skLineSegment(sketch, "E1912", {"start": v(21.05, 16.43) * mm, "end": v(20.83, 16.38) * mm});
            skLineSegment(sketch, "E1913", {"start": v(20.83, 16.38) * mm, "end": v(20.62, 16.32) * mm});
            skLineSegment(sketch, "E1914", {"start": v(20.62, 16.32) * mm, "end": v(20.4, 16.27) * mm});
            skLineSegment(sketch, "E1915", {"start": v(20.4, 16.27) * mm, "end": v(20.18, 16.2) * mm});
            skLineSegment(sketch, "E1916", {"start": v(20.18, 16.2) * mm, "end": v(19.97, 16.15) * mm});
            skLineSegment(sketch, "E1917", {"start": v(19.97, 16.15) * mm, "end": v(19.75, 16.09) * mm});
            skLineSegment(sketch, "E1918", {"start": v(19.75, 16.09) * mm, "end": v(19.53, 16.03) * mm});
            skLineSegment(sketch, "E1919", {"start": v(19.53, 16.03) * mm, "end": v(19.32, 15.97) * mm});
            skLineSegment(sketch, "E1920", {"start": v(19.32, 15.97) * mm, "end": v(19.1, 15.9) * mm});
            skLineSegment(sketch, "E1921", {"start": v(19.1, 15.9) * mm, "end": v(18.9, 15.84) * mm});
            skLineSegment(sketch, "E1922", {"start": v(18.9, 15.84) * mm, "end": v(18.68, 15.77) * mm});
            skLineSegment(sketch, "E1923", {"start": v(18.68, 15.77) * mm, "end": v(18.46, 15.7) * mm});
            skLineSegment(sketch, "E1924", {"start": v(18.46, 15.7) * mm, "end": v(18.25, 15.64) * mm});
            skLineSegment(sketch, "E1925", {"start": v(18.25, 15.64) * mm, "end": v(18.04, 15.57) * mm});
            skLineSegment(sketch, "E1926", {"start": v(18.04, 15.57) * mm, "end": v(17.83, 15.5) * mm});
            skLineSegment(sketch, "E1927", {"start": v(17.83, 15.5) * mm, "end": v(17.62, 15.43) * mm});
            skLineSegment(sketch, "E1928", {"start": v(17.62, 15.43) * mm, "end": v(17.4, 15.36) * mm});
            skLineSegment(sketch, "E1929", {"start": v(17.4, 15.36) * mm, "end": v(17.2, 15.29) * mm});
            skLineSegment(sketch, "E1930", {"start": v(17.2, 15.29) * mm, "end": v(16.99, 15.22) * mm});
            skLineSegment(sketch, "E1931", {"start": v(16.99, 15.22) * mm, "end": v(16.78, 15.14) * mm});
            skLineSegment(sketch, "E1932", {"start": v(16.78, 15.14) * mm, "end": v(16.57, 15.07) * mm});
            skLineSegment(sketch, "E1933", {"start": v(16.57, 15.07) * mm, "end": v(16.36, 14.99) * mm});
            skLineSegment(sketch, "E1934", {"start": v(16.36, 14.99) * mm, "end": v(16.15, 14.91) * mm});
            skLineSegment(sketch, "E1935", {"start": v(16.15, 14.91) * mm, "end": v(15.95, 14.83) * mm});
            skLineSegment(sketch, "E1936", {"start": v(15.95, 14.83) * mm, "end": v(15.74, 14.76) * mm});
            skLineSegment(sketch, "E1937", {"start": v(15.74, 14.76) * mm, "end": v(15.53, 14.67) * mm});
            skLineSegment(sketch, "E1938", {"start": v(15.53, 14.67) * mm, "end": v(15.33, 14.6) * mm});
            skLineSegment(sketch, "E1939", {"start": v(15.33, 14.6) * mm, "end": v(15.12, 14.51) * mm});
            skLineSegment(sketch, "E1940", {"start": v(15.12, 14.51) * mm, "end": v(14.92, 14.43) * mm});
            skLineSegment(sketch, "E1941", {"start": v(14.92, 14.43) * mm, "end": v(14.71, 14.34) * mm});
            skLineSegment(sketch, "E1942", {"start": v(14.71, 14.34) * mm, "end": v(14.51, 14.26) * mm});
            skLineSegment(sketch, "E1943", {"start": v(14.51, 14.26) * mm, "end": v(14.3, 14.17) * mm});
            skLineSegment(sketch, "E1944", {"start": v(14.3, 14.17) * mm, "end": v(14.1, 14.09) * mm});
            skLineSegment(sketch, "E1945", {"start": v(14.1, 14.09) * mm, "end": v(13.9, 14) * mm});
            skLineSegment(sketch, "E1946", {"start": v(13.9, 14) * mm, "end": v(13.7, 13.9) * mm});
            skLineSegment(sketch, "E1947", {"start": v(13.7, 13.9) * mm, "end": v(13.5, 13.82) * mm});
            skLineSegment(sketch, "E1948", {"start": v(13.5, 13.82) * mm, "end": v(13.3, 13.73) * mm});
            skLineSegment(sketch, "E1949", {"start": v(13.3, 13.73) * mm, "end": v(13.1, 13.64) * mm});
            skLineSegment(sketch, "E1950", {"start": v(13.1, 13.64) * mm, "end": v(12.9, 13.54) * mm});
            skLineSegment(sketch, "E1951", {"start": v(12.9, 13.54) * mm, "end": v(12.7, 13.45) * mm});
            skLineSegment(sketch, "E1952", {"start": v(12.7, 13.45) * mm, "end": v(12.5, 13.36) * mm});
            skLineSegment(sketch, "E1953", {"start": v(12.5, 13.36) * mm, "end": v(12.31, 13.26) * mm});
            skLineSegment(sketch, "E1954", {"start": v(12.31, 13.26) * mm, "end": v(12.11, 13.16) * mm});
            skLineSegment(sketch, "E1955", {"start": v(12.11, 13.16) * mm, "end": v(11.92, 13.07) * mm});
            skLineSegment(sketch, "E1956", {"start": v(11.92, 13.07) * mm, "end": v(11.72, 12.97) * mm});
            skLineSegment(sketch, "E1957", {"start": v(11.72, 12.97) * mm, "end": v(11.53, 12.87) * mm});
            skLineSegment(sketch, "E1958", {"start": v(11.53, 12.87) * mm, "end": v(11.33, 12.77) * mm});
            skLineSegment(sketch, "E1959", {"start": v(11.33, 12.77) * mm, "end": v(11.14, 12.67) * mm});
            skLineSegment(sketch, "E1960", {"start": v(11.14, 12.67) * mm, "end": v(10.95, 12.56) * mm});
            skLineSegment(sketch, "E1961", {"start": v(10.95, 12.56) * mm, "end": v(10.75, 12.46) * mm});
            skLineSegment(sketch, "E1962", {"start": v(10.75, 12.46) * mm, "end": v(10.56, 12.36) * mm});
            skLineSegment(sketch, "E1963", {"start": v(10.56, 12.36) * mm, "end": v(10.37, 12.25) * mm});
            skLineSegment(sketch, "E1964", {"start": v(10.37, 12.25) * mm, "end": v(10.18, 12.14) * mm});
            skLineSegment(sketch, "E1965", {"start": v(10.18, 12.14) * mm, "end": v(10, 12.04) * mm});
            skLineSegment(sketch, "E1966", {"start": v(10, 12.04) * mm, "end": v(9.8, 11.93) * mm});
            skLineSegment(sketch, "E1967", {"start": v(9.8, 11.93) * mm, "end": v(9.61, 11.82) * mm});
            skLineSegment(sketch, "E1968", {"start": v(9.61, 11.82) * mm, "end": v(9.42, 11.71) * mm});
            skLineSegment(sketch, "E1969", {"start": v(9.42, 11.71) * mm, "end": v(9.24, 11.6) * mm});
            skLineSegment(sketch, "E1970", {"start": v(9.24, 11.6) * mm, "end": v(9.05, 11.49) * mm});
            skLineSegment(sketch, "E1971", {"start": v(9.05, 11.49) * mm, "end": v(8.86, 11.38) * mm});
            skLineSegment(sketch, "E1972", {"start": v(8.86, 11.38) * mm, "end": v(8.68, 11.26) * mm});
            skLineSegment(sketch, "E1973", {"start": v(8.68, 11.26) * mm, "end": v(8.5, 11.15) * mm});
            skLineSegment(sketch, "E1974", {"start": v(8.5, 11.15) * mm, "end": v(8.3, 11.03) * mm});
            skLineSegment(sketch, "E1975", {"start": v(8.3, 11.03) * mm, "end": v(8.12, 10.91) * mm});
            skLineSegment(sketch, "E1976", {"start": v(8.12, 10.91) * mm, "end": v(7.94, 10.8) * mm});
            skLineSegment(sketch, "E1977", {"start": v(7.94, 10.8) * mm, "end": v(7.76, 10.68) * mm});
            skLineSegment(sketch, "E1978", {"start": v(7.76, 10.68) * mm, "end": v(7.57, 10.56) * mm});
            skLineSegment(sketch, "E1979", {"start": v(7.57, 10.56) * mm, "end": v(7.4, 10.44) * mm});
            skLineSegment(sketch, "E1980", {"start": v(7.4, 10.44) * mm, "end": v(7.21, 10.32) * mm});
            skLineSegment(sketch, "E1981", {"start": v(7.21, 10.32) * mm, "end": v(7.03, 10.2) * mm});
            skLineSegment(sketch, "E1982", {"start": v(7.03, 10.2) * mm, "end": v(6.85, 10.07) * mm});
            skLineSegment(sketch, "E1983", {"start": v(6.85, 10.07) * mm, "end": v(6.67, 9.95) * mm});
            skLineSegment(sketch, "E1984", {"start": v(6.67, 9.95) * mm, "end": v(6.5, 9.83) * mm});
            skLineSegment(sketch, "E1985", {"start": v(6.5, 9.83) * mm, "end": v(6.32, 9.7) * mm});
            skLineSegment(sketch, "E1986", {"start": v(6.32, 9.7) * mm, "end": v(6.14, 9.57) * mm});
            skLineSegment(sketch, "E1987", {"start": v(6.14, 9.57) * mm, "end": v(5.96, 9.45) * mm});
            skLineSegment(sketch, "E1988", {"start": v(5.96, 9.45) * mm, "end": v(5.79, 9.32) * mm});
            skLineSegment(sketch, "E1989", {"start": v(5.79, 9.32) * mm, "end": v(5.61, 9.19) * mm});
            skLineSegment(sketch, "E1990", {"start": v(5.61, 9.19) * mm, "end": v(5.44, 9.06) * mm});
            skLineSegment(sketch, "E1991", {"start": v(5.44, 9.06) * mm, "end": v(5.26, 8.93) * mm});
            skLineSegment(sketch, "E1992", {"start": v(5.26, 8.93) * mm, "end": v(5.09, 8.8) * mm});
            skLineSegment(sketch, "E1993", {"start": v(5.09, 8.8) * mm, "end": v(4.92, 8.66) * mm});
            skLineSegment(sketch, "E1994", {"start": v(4.92, 8.66) * mm, "end": v(4.75, 8.53) * mm});
            skLineSegment(sketch, "E1995", {"start": v(4.75, 8.53) * mm, "end": v(4.57, 8.4) * mm});
            skLineSegment(sketch, "E1996", {"start": v(4.57, 8.4) * mm, "end": v(4.4, 8.26) * mm});
            skLineSegment(sketch, "E1997", {"start": v(4.4, 8.26) * mm, "end": v(4.23, 8.12) * mm});
            skLineSegment(sketch, "E1998", {"start": v(4.23, 8.12) * mm, "end": v(4.06, 7.98) * mm});
            skLineSegment(sketch, "E1999", {"start": v(4.06, 7.98) * mm, "end": v(3.9, 7.85) * mm});
            skLineSegment(sketch, "E2000", {"start": v(3.9, 7.85) * mm, "end": v(3.73, 7.7) * mm});
            skLineSegment(sketch, "E2001", {"start": v(3.73, 7.7) * mm, "end": v(3.56, 7.57) * mm});
            skLineSegment(sketch, "E2002", {"start": v(3.56, 7.57) * mm, "end": v(3.4, 7.43) * mm});
            skLineSegment(sketch, "E2003", {"start": v(3.4, 7.43) * mm, "end": v(3.23, 7.28) * mm});
            skLineSegment(sketch, "E2004", {"start": v(3.23, 7.28) * mm, "end": v(3.06, 7.14) * mm});
            skLineSegment(sketch, "E2005", {"start": v(3.06, 7.14) * mm, "end": v(2.9, 7) * mm});
            skLineSegment(sketch, "E2006", {"start": v(2.9, 7) * mm, "end": v(2.74, 6.85) * mm});
            skLineSegment(sketch, "E2007", {"start": v(2.74, 6.85) * mm, "end": v(2.57, 6.7) * mm});
            skLineSegment(sketch, "E2008", {"start": v(2.57, 6.7) * mm, "end": v(2.41, 6.56) * mm});
            skLineSegment(sketch, "E2009", {"start": v(2.41, 6.56) * mm, "end": v(2.25, 6.42) * mm});
            skLineSegment(sketch, "E2010", {"start": v(2.25, 6.42) * mm, "end": v(2.09, 6.27) * mm});
            skLineSegment(sketch, "E2011", {"start": v(2.09, 6.27) * mm, "end": v(1.93, 6.12) * mm});
            skLineSegment(sketch, "E2012", {"start": v(1.93, 6.12) * mm, "end": v(1.77, 5.97) * mm});
            skLineSegment(sketch, "E2013", {"start": v(1.77, 5.97) * mm, "end": v(1.61, 5.82) * mm});
            skLineSegment(sketch, "E2014", {"start": v(1.61, 5.82) * mm, "end": v(1.45, 5.67) * mm});
            skLineSegment(sketch, "E2015", {"start": v(1.45, 5.67) * mm, "end": v(1.3, 5.51) * mm});
            skLineSegment(sketch, "E2016", {"start": v(1.3, 5.51) * mm, "end": v(1.14, 5.36) * mm});
            skLineSegment(sketch, "E2017", {"start": v(1.14, 5.36) * mm, "end": v(0.98, 5.2) * mm});
            skLineSegment(sketch, "E2018", {"start": v(0.98, 5.2) * mm, "end": v(0.83, 5.05) * mm});
            skLineSegment(sketch, "E2019", {"start": v(0.83, 5.05) * mm, "end": v(0.68, 4.9) * mm});
            skLineSegment(sketch, "E2020", {"start": v(0.68, 4.9) * mm, "end": v(0.52, 4.74) * mm});
            skLineSegment(sketch, "E2021", {"start": v(0.52, 4.74) * mm, "end": v(0.37, 4.58) * mm});
            skLineSegment(sketch, "E2022", {"start": v(0.37, 4.58) * mm, "end": v(0.22, 4.42) * mm});
            skLineSegment(sketch, "E2023", {"start": v(0.22, 4.42) * mm, "end": v(0.07, 4.27) * mm});
            skLineSegment(sketch, "E2024", {"start": v(0.07, 4.27) * mm, "end": v(-0.08, 4.1) * mm});
            skLineSegment(sketch, "E2025", {"start": v(-0.08, 4.1) * mm, "end": v(-0.23, 3.95) * mm});
            skLineSegment(sketch, "E2026", {"start": v(-0.23, 3.95) * mm, "end": v(-0.38, 3.78) * mm});
            skLineSegment(sketch, "E2027", {"start": v(-0.38, 3.78) * mm, "end": v(-0.53, 3.62) * mm});
            skLineSegment(sketch, "E2028", {"start": v(-0.53, 3.62) * mm, "end": v(-0.68, 3.46) * mm});
            skLineSegment(sketch, "E2029", {"start": v(-0.68, 3.46) * mm, "end": v(-0.83, 3.3) * mm});
            skLineSegment(sketch, "E2030", {"start": v(-0.83, 3.3) * mm, "end": v(-0.97, 3.13) * mm});
            skLineSegment(sketch, "E2031", {"start": v(-0.97, 3.13) * mm, "end": v(-1.12, 2.96) * mm});
            skLineSegment(sketch, "E2032", {"start": v(-1.12, 2.96) * mm, "end": v(-1.26, 2.8) * mm});
            skLineSegment(sketch, "E2033", {"start": v(-1.26, 2.8) * mm, "end": v(-1.4, 2.63) * mm});
            skLineSegment(sketch, "E2034", {"start": v(-1.4, 2.63) * mm, "end": v(-1.55, 2.46) * mm});
            skLineSegment(sketch, "E2035", {"start": v(-1.55, 2.46) * mm, "end": v(-1.7, 2.3) * mm});
            skLineSegment(sketch, "E2036", {"start": v(-1.7, 2.3) * mm, "end": v(-1.83, 2.12) * mm});
            skLineSegment(sketch, "E2037", {"start": v(-1.83, 2.12) * mm, "end": v(-1.86, 2.08) * mm});
            skLineSegment(sketch, "E2038", {"start": v(-1.86, 2.08) * mm, "end": v(-1.9, 2.04) * mm});
            skLineSegment(sketch, "E2039", {"start": v(-1.9, 2.04) * mm, "end": v(-1.93, 2) * mm});
            skLineSegment(sketch, "E2040", {"start": v(-1.93, 2) * mm, "end": v(-1.96, 1.96) * mm});
            skLineSegment(sketch, "E2041", {"start": v(-1.96, 1.96) * mm, "end": v(-2, 1.92) * mm});
            skLineSegment(sketch, "E2042", {"start": v(-2, 1.92) * mm, "end": v(-2.03, 1.88) * mm});
            skLineSegment(sketch, "E2043", {"start": v(-2.03, 1.88) * mm, "end": v(-2.06, 1.84) * mm});
            skLineSegment(sketch, "E2044", {"start": v(-2.06, 1.84) * mm, "end": v(-2.1, 1.8) * mm});
            skLineSegment(sketch, "E2045", {"start": v(-2.1, 1.8) * mm, "end": v(-2.12, 1.77) * mm});
            skLineSegment(sketch, "E2046", {"start": v(-2.12, 1.77) * mm, "end": v(-2.16, 1.73) * mm});
            skLineSegment(sketch, "E2047", {"start": v(-2.16, 1.73) * mm, "end": v(-2.19, 1.69) * mm});
            skLineSegment(sketch, "E2048", {"start": v(-2.19, 1.69) * mm, "end": v(-2.22, 1.65) * mm});
            skLineSegment(sketch, "E2049", {"start": v(-2.22, 1.65) * mm, "end": v(-2.25, 1.6) * mm});
            skLineSegment(sketch, "E2050", {"start": v(-2.25, 1.6) * mm, "end": v(-2.29, 1.57) * mm});
            skLineSegment(sketch, "E2051", {"start": v(-2.29, 1.57) * mm, "end": v(-2.32, 1.53) * mm});
            skLineSegment(sketch, "E2052", {"start": v(-2.32, 1.53) * mm, "end": v(-2.35, 1.49) * mm});
            skLineSegment(sketch, "E2053", {"start": v(-2.35, 1.49) * mm, "end": v(-2.38, 1.45) * mm});
            skLineSegment(sketch, "E2054", {"start": v(-2.38, 1.45) * mm, "end": v(-2.42, 1.4) * mm});
            skLineSegment(sketch, "E2055", {"start": v(-2.42, 1.4) * mm, "end": v(-2.45, 1.37) * mm});
            skLineSegment(sketch, "E2056", {"start": v(-2.45, 1.37) * mm, "end": v(-2.48, 1.33) * mm});
            skLineSegment(sketch, "E2057", {"start": v(-2.48, 1.33) * mm, "end": v(-2.51, 1.3) * mm});
            skLineSegment(sketch, "E2058", {"start": v(-2.51, 1.3) * mm, "end": v(-2.55, 1.25) * mm});
            skLineSegment(sketch, "E2059", {"start": v(-2.55, 1.25) * mm, "end": v(-2.58, 1.21) * mm});
            skLineSegment(sketch, "E2060", {"start": v(-2.58, 1.21) * mm, "end": v(-2.61, 1.17) * mm});
            skLineSegment(sketch, "E2061", {"start": v(-2.61, 1.17) * mm, "end": v(-2.64, 1.13) * mm});
            skLineSegment(sketch, "E2062", {"start": v(-2.64, 1.13) * mm, "end": v(-2.67, 1.1) * mm});
            skLineSegment(sketch, "E2063", {"start": v(-2.67, 1.1) * mm, "end": v(-2.7, 1.05) * mm});
            skLineSegment(sketch, "E2064", {"start": v(-2.7, 1.05) * mm, "end": v(-2.74, 1.01) * mm});
            skLineSegment(sketch, "E2065", {"start": v(-2.74, 1.01) * mm, "end": v(-2.77, 0.97) * mm});
            skLineSegment(sketch, "E2066", {"start": v(-2.77, 0.97) * mm, "end": v(-2.8, 0.93) * mm});
            skLineSegment(sketch, "E2067", {"start": v(-2.8, 0.93) * mm, "end": v(-2.84, 0.9) * mm});
            skLineSegment(sketch, "E2068", {"start": v(-2.84, 0.9) * mm, "end": v(-2.87, 0.85) * mm});
            skLineSegment(sketch, "E2069", {"start": v(-2.87, 0.85) * mm, "end": v(-2.9, 0.81) * mm});
            skLineSegment(sketch, "E2070", {"start": v(-2.9, 0.81) * mm, "end": v(-2.93, 0.78) * mm});
            skLineSegment(sketch, "E2071", {"start": v(-2.93, 0.78) * mm, "end": v(-2.96, 0.74) * mm});
            skLineSegment(sketch, "E2072", {"start": v(-2.96, 0.74) * mm, "end": v(-3, 0.7) * mm});
            skLineSegment(sketch, "E2073", {"start": v(-3, 0.7) * mm, "end": v(-3.03, 0.66) * mm});
            skLineSegment(sketch, "E2074", {"start": v(-3.03, 0.66) * mm, "end": v(-3.06, 0.62) * mm});
            skLineSegment(sketch, "E2075", {"start": v(-3.06, 0.62) * mm, "end": v(-3.1, 0.58) * mm});
            skLineSegment(sketch, "E2076", {"start": v(-3.1, 0.58) * mm, "end": v(-3.12, 0.54) * mm});
            skLineSegment(sketch, "E2077", {"start": v(-3.12, 0.54) * mm, "end": v(-3.16, 0.5) * mm});
            skLineSegment(sketch, "E2078", {"start": v(-3.16, 0.5) * mm, "end": v(-3.19, 0.46) * mm});
            skLineSegment(sketch, "E2079", {"start": v(-3.19, 0.46) * mm, "end": v(-3.22, 0.42) * mm});
            skLineSegment(sketch, "E2080", {"start": v(-3.22, 0.42) * mm, "end": v(-3.25, 0.38) * mm});
            skLineSegment(sketch, "E2081", {"start": v(-3.25, 0.38) * mm, "end": v(-3.28, 0.34) * mm});
            skLineSegment(sketch, "E2082", {"start": v(-3.28, 0.34) * mm, "end": v(-3.31, 0.3) * mm});
            skLineSegment(sketch, "E2083", {"start": v(-3.31, 0.3) * mm, "end": v(-3.35, 0.26) * mm});
            skLineSegment(sketch, "E2084", {"start": v(-3.35, 0.26) * mm, "end": v(-3.38, 0.22) * mm});
            skLineSegment(sketch, "E2085", {"start": v(-3.38, 0.22) * mm, "end": v(-3.4, 0.18) * mm});
            skLineSegment(sketch, "E2086", {"start": v(-3.4, 0.18) * mm, "end": v(-3.44, 0.14) * mm});
            skLineSegment(sketch, "E2087", {"start": v(-3.44, 0.14) * mm, "end": v(-3.47, 0.1) * mm});
            skLineSegment(sketch, "E2088", {"start": v(-3.47, 0.1) * mm, "end": v(-3.5, 0.06) * mm});
            skLineSegment(sketch, "E2089", {"start": v(-3.5, 0.06) * mm, "end": v(-3.54, 0.02) * mm});
            skLineSegment(sketch, "E2090", {"start": v(-3.54, 0.02) * mm, "end": v(-3.57, -0.02) * mm});
            skLineSegment(sketch, "E2091", {"start": v(-3.57, -0.02) * mm, "end": v(-3.6, -0.05) * mm});
            skLineSegment(sketch, "E2092", {"start": v(-3.6, -0.05) * mm, "end": v(-3.63, -0.1) * mm});
            skLineSegment(sketch, "E2093", {"start": v(-3.63, -0.1) * mm, "end": v(-3.66, -0.13) * mm});
            skLineSegment(sketch, "E2094", {"start": v(-3.66, -0.13) * mm, "end": v(-3.7, -0.17) * mm});
            skLineSegment(sketch, "E2095", {"start": v(-3.7, -0.17) * mm, "end": v(-3.72, -0.21) * mm});
            skLineSegment(sketch, "E2096", {"start": v(-3.72, -0.21) * mm, "end": v(-3.76, -0.25) * mm});
            skLineSegment(sketch, "E2097", {"start": v(-3.76, -0.25) * mm, "end": v(-3.79, -0.3) * mm});
            skLineSegment(sketch, "E2098", {"start": v(-3.79, -0.3) * mm, "end": v(-3.82, -0.33) * mm});
            skLineSegment(sketch, "E2099", {"start": v(-3.82, -0.33) * mm, "end": v(-3.85, -0.37) * mm});
            skLineSegment(sketch, "E2100", {"start": v(-3.85, -0.37) * mm, "end": v(-3.88, -0.4) * mm});
            skLineSegment(sketch, "E2101", {"start": v(-3.88, -0.4) * mm, "end": v(-3.91, -0.45) * mm});
            skLineSegment(sketch, "E2102", {"start": v(-3.91, -0.45) * mm, "end": v(-3.94, -0.49) * mm});
            skLineSegment(sketch, "E2103", {"start": v(-3.94, -0.49) * mm, "end": v(-3.97, -0.52) * mm});
            skLineSegment(sketch, "E2104", {"start": v(-3.97, -0.52) * mm, "end": v(-4, -0.56) * mm});
            skLineSegment(sketch, "E2105", {"start": v(-4, -0.56) * mm, "end": v(-4.04, -0.6) * mm});
            skLineSegment(sketch, "E2106", {"start": v(-4.04, -0.6) * mm, "end": v(-4.07, -0.64) * mm});
            skLineSegment(sketch, "E2107", {"start": v(-4.07, -0.64) * mm, "end": v(-4.1, -0.68) * mm});
            skLineSegment(sketch, "E2108", {"start": v(-4.1, -0.68) * mm, "end": v(-4.13, -0.72) * mm});
            skLineSegment(sketch, "E2109", {"start": v(-4.13, -0.72) * mm, "end": v(-4.16, -0.76) * mm});
            skLineSegment(sketch, "E2110", {"start": v(-4.16, -0.76) * mm, "end": v(-4.2, -0.8) * mm});
            skLineSegment(sketch, "E2111", {"start": v(-4.2, -0.8) * mm, "end": v(-4.22, -0.84) * mm});
            skLineSegment(sketch, "E2112", {"start": v(-4.22, -0.84) * mm, "end": v(-4.25, -0.87) * mm});
            skLineSegment(sketch, "E2113", {"start": v(-4.25, -0.87) * mm, "end": v(-4.28, -0.91) * mm});
            skLineSegment(sketch, "E2114", {"start": v(-4.28, -0.91) * mm, "end": v(-4.31, -0.95) * mm});
            skLineSegment(sketch, "E2115", {"start": v(-4.31, -0.95) * mm, "end": v(-4.34, -1) * mm});
            skLineSegment(sketch, "E2116", {"start": v(-4.34, -1) * mm, "end": v(-4.37, -1.03) * mm});
            skLineSegment(sketch, "E2117", {"start": v(-4.37, -1.03) * mm, "end": v(-4.4, -1.07) * mm});
            skLineSegment(sketch, "E2118", {"start": v(-4.4, -1.07) * mm, "end": v(-4.43, -1.1) * mm});
            skLineSegment(sketch, "E2119", {"start": v(-4.43, -1.1) * mm, "end": v(-4.47, -1.14) * mm});
            skLineSegment(sketch, "E2120", {"start": v(-4.47, -1.14) * mm, "end": v(-4.5, -1.18) * mm});
            skLineSegment(sketch, "E2121", {"start": v(-4.5, -1.18) * mm, "end": v(-4.53, -1.22) * mm});
            skLineSegment(sketch, "E2122", {"start": v(-4.53, -1.22) * mm, "end": v(-4.56, -1.26) * mm});
            skLineSegment(sketch, "E2123", {"start": v(-4.56, -1.26) * mm, "end": v(-4.59, -1.3) * mm});
            skLineSegment(sketch, "E2124", {"start": v(-4.59, -1.3) * mm, "end": v(-4.62, -1.33) * mm});
            skLineSegment(sketch, "E2125", {"start": v(-4.62, -1.33) * mm, "end": v(-4.65, -1.37) * mm});
            skLineSegment(sketch, "E2126", {"start": v(-4.65, -1.37) * mm, "end": v(-4.68, -1.41) * mm});
            skLineSegment(sketch, "E2127", {"start": v(-4.68, -1.41) * mm, "end": v(-4.7, -1.45) * mm});
            skLineSegment(sketch, "E2128", {"start": v(-4.7, -1.45) * mm, "end": v(-4.74, -1.49) * mm});
            skLineSegment(sketch, "E2129", {"start": v(-4.74, -1.49) * mm, "end": v(-4.77, -1.52) * mm});
            skLineSegment(sketch, "E2130", {"start": v(-4.77, -1.52) * mm, "end": v(-4.8, -1.56) * mm});
            skLineSegment(sketch, "E2131", {"start": v(-4.8, -1.56) * mm, "end": v(-4.83, -1.6) * mm});
            skLineSegment(sketch, "E2132", {"start": v(-4.83, -1.6) * mm, "end": v(-4.85, -1.64) * mm});
            skLineSegment(sketch, "E2133", {"start": v(-4.85, -1.64) * mm, "end": v(-4.88, -1.68) * mm});
            skLineSegment(sketch, "E2134", {"start": v(-4.88, -1.68) * mm, "end": v(-4.91, -1.71) * mm});
            skLineSegment(sketch, "E2135", {"start": v(-4.91, -1.71) * mm, "end": v(-4.94, -1.75) * mm});
            skLineSegment(sketch, "E2136", {"start": v(-4.94, -1.75) * mm, "end": v(-4.97, -1.79) * mm});
            skLineSegment(sketch, "E2137", {"start": v(-4.97, -1.79) * mm, "end": v(-5, -1.83) * mm});
            skLineSegment(sketch, "E2138", {"start": v(-5, -1.83) * mm, "end": v(-5.03, -1.86) * mm});
            skLineSegment(sketch, "E2139", {"start": v(-5.03, -1.86) * mm, "end": v(-5.06, -1.9) * mm});
            skLineSegment(sketch, "E2140", {"start": v(-5.06, -1.9) * mm, "end": v(-5.1, -1.94) * mm});
            skLineSegment(sketch, "E2141", {"start": v(-5.1, -1.94) * mm, "end": v(-5.12, -1.97) * mm});
            skLineSegment(sketch, "E2142", {"start": v(-5.12, -1.97) * mm, "end": v(-5.15, -2.01) * mm});
            skLineSegment(sketch, "E2143", {"start": v(-5.15, -2.01) * mm, "end": v(-5.18, -2.05) * mm});
            skLineSegment(sketch, "E2144", {"start": v(-5.18, -2.05) * mm, "end": v(-5.2, -2.08) * mm});
            skLineSegment(sketch, "E2145", {"start": v(-5.2, -2.08) * mm, "end": v(-5.24, -2.12) * mm});
            skLineSegment(sketch, "E2146", {"start": v(-5.24, -2.12) * mm, "end": v(-5.26, -2.16) * mm});
            skLineSegment(sketch, "E2147", {"start": v(-5.26, -2.16) * mm, "end": v(-5.3, -2.2) * mm});
            skLineSegment(sketch, "E2148", {"start": v(-5.3, -2.2) * mm, "end": v(-5.32, -2.23) * mm});
            skLineSegment(sketch, "E2149", {"start": v(-5.32, -2.23) * mm, "end": v(-5.35, -2.27) * mm});
            skLineSegment(sketch, "E2150", {"start": v(-5.35, -2.27) * mm, "end": v(-5.38, -2.3) * mm});
            skLineSegment(sketch, "E2151", {"start": v(-5.38, -2.3) * mm, "end": v(-5.4, -2.34) * mm});
            skLineSegment(sketch, "E2152", {"start": v(-5.4, -2.34) * mm, "end": v(-5.44, -2.38) * mm});
            skLineSegment(sketch, "E2153", {"start": v(-5.44, -2.38) * mm, "end": v(-5.46, -2.41) * mm});
            skLineSegment(sketch, "E2154", {"start": v(-5.46, -2.41) * mm, "end": v(-5.5, -2.45) * mm});
            skLineSegment(sketch, "E2155", {"start": v(-5.5, -2.45) * mm, "end": v(-5.52, -2.49) * mm});
            skLineSegment(sketch, "E2156", {"start": v(-5.52, -2.49) * mm, "end": v(-5.55, -2.52) * mm});
            skLineSegment(sketch, "E2157", {"start": v(-5.55, -2.52) * mm, "end": v(-5.58, -2.56) * mm});
            skLineSegment(sketch, "E2158", {"start": v(-5.58, -2.56) * mm, "end": v(-5.6, -2.6) * mm});
            skLineSegment(sketch, "E2159", {"start": v(-5.6, -2.6) * mm, "end": v(-5.63, -2.63) * mm});
            skLineSegment(sketch, "E2160", {"start": v(-5.63, -2.63) * mm, "end": v(-5.66, -2.66) * mm});
            skLineSegment(sketch, "E2161", {"start": v(-5.66, -2.66) * mm, "end": v(-5.69, -2.7) * mm});
            skLineSegment(sketch, "E2162", {"start": v(-5.69, -2.7) * mm, "end": v(-5.72, -2.74) * mm});
            skLineSegment(sketch, "E2163", {"start": v(-5.72, -2.74) * mm, "end": v(-5.75, -2.77) * mm});
            skLineSegment(sketch, "E2164", {"start": v(-5.75, -2.77) * mm, "end": v(-5.77, -2.8) * mm});
            skLineSegment(sketch, "E2165", {"start": v(-5.77, -2.8) * mm, "end": v(-5.78, -2.81) * mm});
            skLineSegment(sketch, "E2166", {"start": v(-5.78, -2.81) * mm, "end": v(-5.78, -2.82) * mm});
            skLineSegment(sketch, "E2167", {"start": v(-5.78, -2.82) * mm, "end": v(-5.79, -2.83) * mm});
            skLineSegment(sketch, "E2168", {"start": v(-5.79, -2.83) * mm, "end": v(-5.8, -2.83) * mm});
            skLineSegment(sketch, "E2169", {"start": v(-5.8, -2.83) * mm, "end": v(-5.8, -2.84) * mm});
            skLineSegment(sketch, "E2170", {"start": v(-5.8, -2.84) * mm, "end": v(-5.8, -2.85) * mm});
            skLineSegment(sketch, "E2171", {"start": v(-5.8, -2.85) * mm, "end": v(-5.8, -2.85) * mm});
            skLineSegment(sketch, "E2172", {"start": v(-5.8, -2.85) * mm, "end": v(-5.81, -2.86) * mm});
            skLineSegment(sketch, "E2173", {"start": v(-5.81, -2.86) * mm, "end": v(-5.82, -2.87) * mm});
            skLineSegment(sketch, "E2174", {"start": v(-5.82, -2.87) * mm, "end": v(-5.82, -2.87) * mm});
            skLineSegment(sketch, "E2175", {"start": v(-5.82, -2.87) * mm, "end": v(-5.83, -2.88) * mm});
            skLineSegment(sketch, "E2176", {"start": v(-5.83, -2.88) * mm, "end": v(-5.83, -2.88) * mm});
            skLineSegment(sketch, "E2177", {"start": v(-5.83, -2.88) * mm, "end": v(-5.84, -2.9) * mm});
            skLineSegment(sketch, "E2178", {"start": v(-5.84, -2.9) * mm, "end": v(-5.84, -2.9) * mm});
            skLineSegment(sketch, "E2179", {"start": v(-5.84, -2.9) * mm, "end": v(-5.85, -2.9) * mm});
            skLineSegment(sketch, "E2180", {"start": v(-5.85, -2.9) * mm, "end": v(-5.85, -2.91) * mm});
            skLineSegment(sketch, "E2181", {"start": v(-5.85, -2.91) * mm, "end": v(-5.86, -2.92) * mm});
            skLineSegment(sketch, "E2182", {"start": v(-5.86, -2.92) * mm, "end": v(-5.87, -2.92) * mm});
            skLineSegment(sketch, "E2183", {"start": v(-5.87, -2.92) * mm, "end": v(-5.87, -2.93) * mm});
            skLineSegment(sketch, "E2184", {"start": v(-5.87, -2.93) * mm, "end": v(-5.88, -2.94) * mm});
            skLineSegment(sketch, "E2185", {"start": v(-5.88, -2.94) * mm, "end": v(-5.88, -2.94) * mm});
            skLineSegment(sketch, "E2186", {"start": v(-5.88, -2.94) * mm, "end": v(-5.89, -2.95) * mm});
            skLineSegment(sketch, "E2187", {"start": v(-5.89, -2.95) * mm, "end": v(-5.9, -2.96) * mm});
            skLineSegment(sketch, "E2188", {"start": v(-5.9, -2.96) * mm, "end": v(-5.9, -2.96) * mm});
            skLineSegment(sketch, "E2189", {"start": v(-5.9, -2.96) * mm, "end": v(-5.9, -2.97) * mm});
            skLineSegment(sketch, "E2190", {"start": v(-5.9, -2.97) * mm, "end": v(-5.9, -2.98) * mm});
            skLineSegment(sketch, "E2191", {"start": v(-5.9, -2.98) * mm, "end": v(-5.91, -2.98) * mm});
            skLineSegment(sketch, "E2192", {"start": v(-5.91, -2.98) * mm, "end": v(-5.92, -2.99) * mm});
            skLineSegment(sketch, "E2193", {"start": v(-5.92, -2.99) * mm, "end": v(-5.92, -3) * mm});
            skLineSegment(sketch, "E2194", {"start": v(-5.92, -3) * mm, "end": v(-5.93, -3) * mm});
            skLineSegment(sketch, "E2195", {"start": v(-5.93, -3) * mm, "end": v(-5.93, -3) * mm});
            skLineSegment(sketch, "E2196", {"start": v(-5.93, -3) * mm, "end": v(-5.94, -3.02) * mm});
            skLineSegment(sketch, "E2197", {"start": v(-5.94, -3.02) * mm, "end": v(-5.94, -3.02) * mm});
            skLineSegment(sketch, "E2198", {"start": v(-5.94, -3.02) * mm, "end": v(-5.95, -3.03) * mm});
            skLineSegment(sketch, "E2199", {"start": v(-5.95, -3.03) * mm, "end": v(-5.95, -3.04) * mm});
            skLineSegment(sketch, "E2200", {"start": v(-5.95, -3.04) * mm, "end": v(-5.96, -3.04) * mm});
            skLineSegment(sketch, "E2201", {"start": v(-5.96, -3.04) * mm, "end": v(-5.96, -3.05) * mm});
            skLineSegment(sketch, "E2202", {"start": v(-5.96, -3.05) * mm, "end": v(-5.97, -3.06) * mm});
            skLineSegment(sketch, "E2203", {"start": v(-5.97, -3.06) * mm, "end": v(-5.97, -3.06) * mm});
            skLineSegment(sketch, "E2204", {"start": v(-5.97, -3.06) * mm, "end": v(-5.98, -3.07) * mm});
            skLineSegment(sketch, "E2205", {"start": v(-5.98, -3.07) * mm, "end": v(-5.98, -3.07) * mm});
            skLineSegment(sketch, "E2206", {"start": v(-5.98, -3.07) * mm, "end": v(-5.99, -3.08) * mm});
            skLineSegment(sketch, "E2207", {"start": v(-5.99, -3.08) * mm, "end": v(-6, -3.09) * mm});
            skLineSegment(sketch, "E2208", {"start": v(-6, -3.09) * mm, "end": v(-6, -3.1) * mm});
            skLineSegment(sketch, "E2209", {"start": v(-6, -3.1) * mm, "end": v(-6, -3.1) * mm});
            skLineSegment(sketch, "E2210", {"start": v(-6, -3.1) * mm, "end": v(-6.01, -3.11) * mm});
            skLineSegment(sketch, "E2211", {"start": v(-6.01, -3.11) * mm, "end": v(-6.02, -3.12) * mm});
            skLineSegment(sketch, "E2212", {"start": v(-6.02, -3.12) * mm, "end": v(-6.02, -3.13) * mm});
            skLineSegment(sketch, "E2213", {"start": v(-6.02, -3.13) * mm, "end": v(-6.03, -3.13) * mm});
            skLineSegment(sketch, "E2214", {"start": v(-6.03, -3.13) * mm, "end": v(-6.03, -3.14) * mm});
            skLineSegment(sketch, "E2215", {"start": v(-6.03, -3.14) * mm, "end": v(-6.04, -3.15) * mm});
            skLineSegment(sketch, "E2216", {"start": v(-6.04, -3.15) * mm, "end": v(-6.04, -3.15) * mm});
            skLineSegment(sketch, "E2217", {"start": v(-6.04, -3.15) * mm, "end": v(-6.05, -3.16) * mm});
            skLineSegment(sketch, "E2218", {"start": v(-6.05, -3.16) * mm, "end": v(-6.06, -3.17) * mm});
            skLineSegment(sketch, "E2219", {"start": v(-6.06, -3.17) * mm, "end": v(-6.06, -3.17) * mm});
            skLineSegment(sketch, "E2220", {"start": v(-6.06, -3.17) * mm, "end": v(-6.07, -3.18) * mm});
            skLineSegment(sketch, "E2221", {"start": v(-6.07, -3.18) * mm, "end": v(-6.07, -3.19) * mm});
            skLineSegment(sketch, "E2222", {"start": v(-6.07, -3.19) * mm, "end": v(-6.08, -3.2) * mm});
            skLineSegment(sketch, "E2223", {"start": v(-6.08, -3.2) * mm, "end": v(-6.08, -3.2) * mm});
            skLineSegment(sketch, "E2224", {"start": v(-6.08, -3.2) * mm, "end": v(-6.09, -3.2) * mm});
            skLineSegment(sketch, "E2225", {"start": v(-6.09, -3.2) * mm, "end": v(-6.1, -3.21) * mm});
            skLineSegment(sketch, "E2226", {"start": v(-6.1, -3.21) * mm, "end": v(-6.1, -3.22) * mm});
            skLineSegment(sketch, "E2227", {"start": v(-6.1, -3.22) * mm, "end": v(-6.1, -3.23) * mm});
            skLineSegment(sketch, "E2228", {"start": v(-6.1, -3.23) * mm, "end": v(-6.1, -3.23) * mm});
            skLineSegment(sketch, "E2229", {"start": v(-6.1, -3.23) * mm, "end": v(-6.11, -3.24) * mm});
            skLineSegment(sketch, "E2230", {"start": v(-6.11, -3.24) * mm, "end": v(-6.12, -3.25) * mm});
            skLineSegment(sketch, "E2231", {"start": v(-6.12, -3.25) * mm, "end": v(-6.12, -3.25) * mm});
            skLineSegment(sketch, "E2232", {"start": v(-6.12, -3.25) * mm, "end": v(-6.13, -3.26) * mm});
            skLineSegment(sketch, "E2233", {"start": v(-6.13, -3.26) * mm, "end": v(-6.13, -3.26) * mm});
            skLineSegment(sketch, "E2234", {"start": v(-6.13, -3.26) * mm, "end": v(-6.14, -3.27) * mm});
            skLineSegment(sketch, "E2235", {"start": v(-6.14, -3.27) * mm, "end": v(-6.14, -3.28) * mm});
            skLineSegment(sketch, "E2236", {"start": v(-6.14, -3.28) * mm, "end": v(-6.15, -3.28) * mm});
            skLineSegment(sketch, "E2237", {"start": v(-6.15, -3.28) * mm, "end": v(-6.15, -3.3) * mm});
            skLineSegment(sketch, "E2238", {"start": v(-6.15, -3.3) * mm, "end": v(-6.16, -3.3) * mm});
            skLineSegment(sketch, "E2239", {"start": v(-6.16, -3.3) * mm, "end": v(-6.16, -3.3) * mm});
            skLineSegment(sketch, "E2240", {"start": v(-6.16, -3.3) * mm, "end": v(-6.17, -3.31) * mm});
            skLineSegment(sketch, "E2241", {"start": v(-6.17, -3.31) * mm, "end": v(-6.17, -3.32) * mm});
            skLineSegment(sketch, "E2242", {"start": v(-6.17, -3.32) * mm, "end": v(-6.18, -3.32) * mm});
            skLineSegment(sketch, "E2243", {"start": v(-6.18, -3.32) * mm, "end": v(-6.18, -3.33) * mm});
            skLineSegment(sketch, "E2244", {"start": v(-6.18, -3.33) * mm, "end": v(-6.19, -3.34) * mm});
            skLineSegment(sketch, "E2245", {"start": v(-6.19, -3.34) * mm, "end": v(-6.2, -3.34) * mm});
            skLineSegment(sketch, "E2246", {"start": v(-6.2, -3.34) * mm, "end": v(-6.2, -3.35) * mm});
            skLineSegment(sketch, "E2247", {"start": v(-6.2, -3.35) * mm, "end": v(-6.2, -3.36) * mm});
            skLineSegment(sketch, "E2248", {"start": v(-6.2, -3.36) * mm, "end": v(-6.2, -3.36) * mm});
            skLineSegment(sketch, "E2249", {"start": v(-6.2, -3.36) * mm, "end": v(-6.21, -3.37) * mm});
            skLineSegment(sketch, "E2250", {"start": v(-6.21, -3.37) * mm, "end": v(-6.22, -3.38) * mm});
            skLineSegment(sketch, "E2251", {"start": v(-6.22, -3.38) * mm, "end": v(-6.22, -3.38) * mm});
            skLineSegment(sketch, "E2252", {"start": v(-6.22, -3.38) * mm, "end": v(-6.23, -3.39) * mm});
            skLineSegment(sketch, "E2253", {"start": v(-6.23, -3.39) * mm, "end": v(-6.23, -3.4) * mm});
            skLineSegment(sketch, "E2254", {"start": v(-6.23, -3.4) * mm, "end": v(-6.24, -3.4) * mm});
            skLineSegment(sketch, "E2255", {"start": v(-6.24, -3.4) * mm, "end": v(-6.25, -3.4) * mm});
            skLineSegment(sketch, "E2256", {"start": v(-6.25, -3.4) * mm, "end": v(-6.25, -3.42) * mm});
            skLineSegment(sketch, "E2257", {"start": v(-6.25, -3.42) * mm, "end": v(-6.26, -3.42) * mm});
            skLineSegment(sketch, "E2258", {"start": v(-6.26, -3.42) * mm, "end": v(-6.26, -3.43) * mm});
            skLineSegment(sketch, "E2259", {"start": v(-6.26, -3.43) * mm, "end": v(-6.27, -3.44) * mm});
            skLineSegment(sketch, "E2260", {"start": v(-6.27, -3.44) * mm, "end": v(-6.27, -3.44) * mm});
            skLineSegment(sketch, "E2261", {"start": v(-6.27, -3.44) * mm, "end": v(-6.28, -3.45) * mm});
            skLineSegment(sketch, "E2262", {"start": v(-6.28, -3.45) * mm, "end": v(-6.28, -3.45) * mm});
            skLineSegment(sketch, "E2263", {"start": v(-6.28, -3.45) * mm, "end": v(-6.29, -3.46) * mm});
            skLineSegment(sketch, "E2264", {"start": v(-6.29, -3.46) * mm, "end": v(-6.3, -3.47) * mm});
            skLineSegment(sketch, "E2265", {"start": v(-6.3, -3.47) * mm, "end": v(-6.3, -3.47) * mm});
            skLineSegment(sketch, "E2266", {"start": v(-6.3, -3.47) * mm, "end": v(-6.3, -3.48) * mm});
            skLineSegment(sketch, "E2267", {"start": v(-6.3, -3.48) * mm, "end": v(-6.3, -3.49) * mm});
            skLineSegment(sketch, "E2268", {"start": v(-6.3, -3.49) * mm, "end": v(-6.31, -3.5) * mm});
            skLineSegment(sketch, "E2269", {"start": v(-6.31, -3.5) * mm, "end": v(-6.32, -3.5) * mm});
            skLineSegment(sketch, "E2270", {"start": v(-6.32, -3.5) * mm, "end": v(-6.32, -3.5) * mm});
            skLineSegment(sketch, "E2271", {"start": v(-6.32, -3.5) * mm, "end": v(-6.33, -3.51) * mm});
            skLineSegment(sketch, "E2272", {"start": v(-6.33, -3.51) * mm, "end": v(-6.33, -3.52) * mm});
            skLineSegment(sketch, "E2273", {"start": v(-6.33, -3.52) * mm, "end": v(-6.34, -3.53) * mm});
            skLineSegment(sketch, "E2274", {"start": v(-6.34, -3.53) * mm, "end": v(-6.34, -3.53) * mm});
            skLineSegment(sketch, "E2275", {"start": v(-6.34, -3.53) * mm, "end": v(-6.35, -3.54) * mm});
            skLineSegment(sketch, "E2276", {"start": v(-6.35, -3.54) * mm, "end": v(-6.35, -3.55) * mm});
            skLineSegment(sketch, "E2277", {"start": v(-6.35, -3.55) * mm, "end": v(-6.36, -3.55) * mm});
            skLineSegment(sketch, "E2278", {"start": v(-6.36, -3.55) * mm, "end": v(-6.36, -3.56) * mm});
            skLineSegment(sketch, "E2279", {"start": v(-6.36, -3.56) * mm, "end": v(-6.37, -3.57) * mm});
            skLineSegment(sketch, "E2280", {"start": v(-6.37, -3.57) * mm, "end": v(-6.37, -3.57) * mm});
            skLineSegment(sketch, "E2281", {"start": v(-6.37, -3.57) * mm, "end": v(-6.38, -3.58) * mm});
            skLineSegment(sketch, "E2282", {"start": v(-6.38, -3.58) * mm, "end": v(-6.38, -3.59) * mm});
            skLineSegment(sketch, "E2283", {"start": v(-6.38, -3.59) * mm, "end": v(-6.39, -3.6) * mm});
            skLineSegment(sketch, "E2284", {"start": v(-6.39, -3.6) * mm, "end": v(-6.4, -3.6) * mm});
            skLineSegment(sketch, "E2285", {"start": v(-6.4, -3.6) * mm, "end": v(-6.4, -3.6) * mm});
            skLineSegment(sketch, "E2286", {"start": v(-6.4, -3.6) * mm, "end": v(-6.4, -3.61) * mm});
            skLineSegment(sketch, "E2287", {"start": v(-6.4, -3.61) * mm, "end": v(-6.4, -3.62) * mm});
            skLineSegment(sketch, "E2288", {"start": v(-6.4, -3.62) * mm, "end": v(-6.41, -3.63) * mm});
            skLineSegment(sketch, "E2289", {"start": v(-6.41, -3.63) * mm, "end": v(-6.42, -3.63) * mm});
            skLineSegment(sketch, "E2290", {"start": v(-6.42, -3.63) * mm, "end": v(-6.42, -3.64) * mm});
            skLineSegment(sketch, "E2291", {"start": v(-6.42, -3.64) * mm, "end": v(-6.43, -3.65) * mm});
            skLineSegment(sketch, "E2292", {"start": v(-6.43, -3.65) * mm, "end": v(-6.43, -3.64) * mm});
            skLineSegment(sketch, "E2293", {"start": v(-6.43, -3.64) * mm, "end": v(-6.43, -3.63) * mm});
            skLineSegment(sketch, "E2294", {"start": v(-6.43, -3.63) * mm, "end": v(-6.44, -3.62) * mm});
            skLineSegment(sketch, "E2295", {"start": v(-6.44, -3.62) * mm, "end": v(-6.44, -3.61) * mm});
            skLineSegment(sketch, "E2296", {"start": v(-6.44, -3.61) * mm, "end": v(-6.44, -3.6) * mm});
            skLineSegment(sketch, "E2297", {"start": v(-6.44, -3.6) * mm, "end": v(-6.44, -3.6) * mm});
            skLineSegment(sketch, "E2298", {"start": v(-6.44, -3.6) * mm, "end": v(-6.44, -3.59) * mm});
            skLineSegment(sketch, "E2299", {"start": v(-6.44, -3.59) * mm, "end": v(-6.44, -3.58) * mm});
            skLineSegment(sketch, "E2300", {"start": v(-6.44, -3.58) * mm, "end": v(-6.45, -3.57) * mm});
            skLineSegment(sketch, "E2301", {"start": v(-6.45, -3.57) * mm, "end": v(-6.45, -3.56) * mm});
            skLineSegment(sketch, "E2302", {"start": v(-6.45, -3.56) * mm, "end": v(-6.45, -3.56) * mm});
            skLineSegment(sketch, "E2303", {"start": v(-6.45, -3.56) * mm, "end": v(-6.45, -3.55) * mm});
            skLineSegment(sketch, "E2304", {"start": v(-6.45, -3.55) * mm, "end": v(-6.45, -3.54) * mm});
            skLineSegment(sketch, "E2305", {"start": v(-6.45, -3.54) * mm, "end": v(-6.46, -3.53) * mm});
            skLineSegment(sketch, "E2306", {"start": v(-6.46, -3.53) * mm, "end": v(-6.46, -3.52) * mm});
            skLineSegment(sketch, "E2307", {"start": v(-6.46, -3.52) * mm, "end": v(-6.46, -3.52) * mm});
            skLineSegment(sketch, "E2308", {"start": v(-6.46, -3.52) * mm, "end": v(-6.46, -3.5) * mm});
            skLineSegment(sketch, "E2309", {"start": v(-6.46, -3.5) * mm, "end": v(-6.46, -3.5) * mm});
            skLineSegment(sketch, "E2310", {"start": v(-6.46, -3.5) * mm, "end": v(-6.47, -3.5) * mm});
            skLineSegment(sketch, "E2311", {"start": v(-6.47, -3.5) * mm, "end": v(-6.47, -3.48) * mm});
            skLineSegment(sketch, "E2312", {"start": v(-6.47, -3.48) * mm, "end": v(-6.47, -3.47) * mm});
            skLineSegment(sketch, "E2313", {"start": v(-6.47, -3.47) * mm, "end": v(-6.47, -3.47) * mm});
            skLineSegment(sketch, "E2314", {"start": v(-6.47, -3.47) * mm, "end": v(-6.47, -3.46) * mm});
            skLineSegment(sketch, "E2315", {"start": v(-6.47, -3.46) * mm, "end": v(-6.47, -3.45) * mm});
            skLineSegment(sketch, "E2316", {"start": v(-6.47, -3.45) * mm, "end": v(-6.48, -3.44) * mm});
            skLineSegment(sketch, "E2317", {"start": v(-6.48, -3.44) * mm, "end": v(-6.48, -3.43) * mm});
            skLineSegment(sketch, "E2318", {"start": v(-6.48, -3.43) * mm, "end": v(-6.48, -3.43) * mm});
            skLineSegment(sketch, "E2319", {"start": v(-6.48, -3.43) * mm, "end": v(-6.48, -3.42) * mm});
            skLineSegment(sketch, "E2320", {"start": v(-6.48, -3.42) * mm, "end": v(-6.48, -3.4) * mm});
            skLineSegment(sketch, "E2321", {"start": v(-6.48, -3.4) * mm, "end": v(-6.49, -3.4) * mm});
            skLineSegment(sketch, "E2322", {"start": v(-6.49, -3.4) * mm, "end": v(-6.49, -3.4) * mm});
            skLineSegment(sketch, "E2323", {"start": v(-6.49, -3.4) * mm, "end": v(-6.49, -3.39) * mm});
            skLineSegment(sketch, "E2324", {"start": v(-6.49, -3.39) * mm, "end": v(-6.5, -3.38) * mm});
            skLineSegment(sketch, "E2325", {"start": v(-6.5, -3.38) * mm, "end": v(-6.5, -3.37) * mm});
            skLineSegment(sketch, "E2326", {"start": v(-6.5, -3.37) * mm, "end": v(-6.5, -3.36) * mm});
            skLineSegment(sketch, "E2327", {"start": v(-6.5, -3.36) * mm, "end": v(-6.5, -3.35) * mm});
            skLineSegment(sketch, "E2328", {"start": v(-6.5, -3.35) * mm, "end": v(-6.5, -3.34) * mm});
            skLineSegment(sketch, "E2329", {"start": v(-6.5, -3.34) * mm, "end": v(-6.5, -3.34) * mm});
            skLineSegment(sketch, "E2330", {"start": v(-6.5, -3.34) * mm, "end": v(-6.5, -3.33) * mm});
            skLineSegment(sketch, "E2331", {"start": v(-6.5, -3.33) * mm, "end": v(-6.5, -3.32) * mm});
            skLineSegment(sketch, "E2332", {"start": v(-6.5, -3.32) * mm, "end": v(-6.5, -3.31) * mm});
            skLineSegment(sketch, "E2333", {"start": v(-6.5, -3.31) * mm, "end": v(-6.5, -3.3) * mm});
            skLineSegment(sketch, "E2334", {"start": v(-6.5, -3.3) * mm, "end": v(-6.5, -3.3) * mm});
            skLineSegment(sketch, "E2335", {"start": v(-6.5, -3.3) * mm, "end": v(-6.51, -3.29) * mm});
            skLineSegment(sketch, "E2336", {"start": v(-6.51, -3.29) * mm, "end": v(-6.51, -3.28) * mm});
            skLineSegment(sketch, "E2337", {"start": v(-6.51, -3.28) * mm, "end": v(-6.52, -3.27) * mm});
            skLineSegment(sketch, "E2338", {"start": v(-6.52, -3.27) * mm, "end": v(-6.52, -3.26) * mm});
            skLineSegment(sketch, "E2339", {"start": v(-6.52, -3.26) * mm, "end": v(-6.52, -3.26) * mm});
            skLineSegment(sketch, "E2340", {"start": v(-6.52, -3.26) * mm, "end": v(-6.52, -3.25) * mm});
            skLineSegment(sketch, "E2341", {"start": v(-6.52, -3.25) * mm, "end": v(-6.52, -3.24) * mm});
            skLineSegment(sketch, "E2342", {"start": v(-6.52, -3.24) * mm, "end": v(-6.52, -3.23) * mm});
            skLineSegment(sketch, "E2343", {"start": v(-6.52, -3.23) * mm, "end": v(-6.53, -3.22) * mm});
            skLineSegment(sketch, "E2344", {"start": v(-6.53, -3.22) * mm, "end": v(-6.53, -3.21) * mm});
            skLineSegment(sketch, "E2345", {"start": v(-6.53, -3.21) * mm, "end": v(-6.53, -3.2) * mm});
            skLineSegment(sketch, "E2346", {"start": v(-6.53, -3.2) * mm, "end": v(-6.53, -3.2) * mm});
            skLineSegment(sketch, "E2347", {"start": v(-6.53, -3.2) * mm, "end": v(-6.54, -3.18) * mm});
            skLineSegment(sketch, "E2348", {"start": v(-6.54, -3.18) * mm, "end": v(-6.54, -3.17) * mm});
            skLineSegment(sketch, "E2349", {"start": v(-6.54, -3.17) * mm, "end": v(-6.54, -3.17) * mm});
            skLineSegment(sketch, "E2350", {"start": v(-6.54, -3.17) * mm, "end": v(-6.54, -3.16) * mm});
            skLineSegment(sketch, "E2351", {"start": v(-6.54, -3.16) * mm, "end": v(-6.54, -3.15) * mm});
            skLineSegment(sketch, "E2352", {"start": v(-6.54, -3.15) * mm, "end": v(-6.54, -3.14) * mm});
            skLineSegment(sketch, "E2353", {"start": v(-6.54, -3.14) * mm, "end": v(-6.55, -3.13) * mm});
            skLineSegment(sketch, "E2354", {"start": v(-6.55, -3.13) * mm, "end": v(-6.55, -3.13) * mm});
            skLineSegment(sketch, "E2355", {"start": v(-6.55, -3.13) * mm, "end": v(-6.55, -3.12) * mm});
            skLineSegment(sketch, "E2356", {"start": v(-6.55, -3.12) * mm, "end": v(-6.55, -3.1) * mm});
            skLineSegment(sketch, "E2357", {"start": v(-6.55, -3.1) * mm, "end": v(-6.55, -3.1) * mm});
            skLineSegment(sketch, "E2358", {"start": v(-6.55, -3.1) * mm, "end": v(-6.56, -3.1) * mm});
            skLineSegment(sketch, "E2359", {"start": v(-6.56, -3.1) * mm, "end": v(-6.56, -3.08) * mm});
            skLineSegment(sketch, "E2360", {"start": v(-6.56, -3.08) * mm, "end": v(-6.56, -3.08) * mm});
            skLineSegment(sketch, "E2361", {"start": v(-6.56, -3.08) * mm, "end": v(-6.56, -3.07) * mm});
            skLineSegment(sketch, "E2362", {"start": v(-6.56, -3.07) * mm, "end": v(-6.56, -3.06) * mm});
            skLineSegment(sketch, "E2363", {"start": v(-6.56, -3.06) * mm, "end": v(-6.57, -3.05) * mm});
            skLineSegment(sketch, "E2364", {"start": v(-6.57, -3.05) * mm, "end": v(-6.57, -3.04) * mm});
            skLineSegment(sketch, "E2365", {"start": v(-6.57, -3.04) * mm, "end": v(-6.57, -3.04) * mm});
            skLineSegment(sketch, "E2366", {"start": v(-6.57, -3.04) * mm, "end": v(-6.57, -3.03) * mm});
            skLineSegment(sketch, "E2367", {"start": v(-6.57, -3.03) * mm, "end": v(-6.57, -3.02) * mm});
            skLineSegment(sketch, "E2368", {"start": v(-6.57, -3.02) * mm, "end": v(-6.57, -3.01) * mm});
            skLineSegment(sketch, "E2369", {"start": v(-6.57, -3.01) * mm, "end": v(-6.58, -3) * mm});
            skLineSegment(sketch, "E2370", {"start": v(-6.58, -3) * mm, "end": v(-6.58, -3) * mm});
            skLineSegment(sketch, "E2371", {"start": v(-6.58, -3) * mm, "end": v(-6.58, -2.99) * mm});
            skLineSegment(sketch, "E2372", {"start": v(-6.58, -2.99) * mm, "end": v(-6.58, -2.98) * mm});
            skLineSegment(sketch, "E2373", {"start": v(-6.58, -2.98) * mm, "end": v(-6.58, -2.97) * mm});
            skLineSegment(sketch, "E2374", {"start": v(-6.58, -2.97) * mm, "end": v(-6.59, -2.96) * mm});
            skLineSegment(sketch, "E2375", {"start": v(-6.59, -2.96) * mm, "end": v(-6.59, -2.95) * mm});
            skLineSegment(sketch, "E2376", {"start": v(-6.59, -2.95) * mm, "end": v(-6.59, -2.95) * mm});
            skLineSegment(sketch, "E2377", {"start": v(-6.59, -2.95) * mm, "end": v(-6.6, -2.94) * mm});
            skLineSegment(sketch, "E2378", {"start": v(-6.6, -2.94) * mm, "end": v(-6.6, -2.93) * mm});
            skLineSegment(sketch, "E2379", {"start": v(-6.6, -2.93) * mm, "end": v(-6.6, -2.92) * mm});
            skLineSegment(sketch, "E2380", {"start": v(-6.6, -2.92) * mm, "end": v(-6.6, -2.91) * mm});
            skLineSegment(sketch, "E2381", {"start": v(-6.6, -2.91) * mm, "end": v(-6.6, -2.9) * mm});
            skLineSegment(sketch, "E2382", {"start": v(-6.6, -2.9) * mm, "end": v(-6.6, -2.9) * mm});
            skLineSegment(sketch, "E2383", {"start": v(-6.6, -2.9) * mm, "end": v(-6.6, -2.89) * mm});
            skLineSegment(sketch, "E2384", {"start": v(-6.6, -2.89) * mm, "end": v(-6.6, -2.88) * mm});
            skLineSegment(sketch, "E2385", {"start": v(-6.6, -2.88) * mm, "end": v(-6.6, -2.87) * mm});
            skLineSegment(sketch, "E2386", {"start": v(-6.6, -2.87) * mm, "end": v(-6.6, -2.87) * mm});
            skLineSegment(sketch, "E2387", {"start": v(-6.6, -2.87) * mm, "end": v(-6.6, -2.86) * mm});
            skLineSegment(sketch, "E2388", {"start": v(-6.6, -2.86) * mm, "end": v(-6.61, -2.85) * mm});
            skLineSegment(sketch, "E2389", {"start": v(-6.61, -2.85) * mm, "end": v(-6.61, -2.84) * mm});
            skLineSegment(sketch, "E2390", {"start": v(-6.61, -2.84) * mm, "end": v(-6.62, -2.83) * mm});
            skLineSegment(sketch, "E2391", {"start": v(-6.62, -2.83) * mm, "end": v(-6.62, -2.82) * mm});
            skLineSegment(sketch, "E2392", {"start": v(-6.62, -2.82) * mm, "end": v(-6.62, -2.82) * mm});
            skLineSegment(sketch, "E2393", {"start": v(-6.62, -2.82) * mm, "end": v(-6.62, -2.8) * mm});
            skLineSegment(sketch, "E2394", {"start": v(-6.62, -2.8) * mm, "end": v(-6.62, -2.8) * mm});
            skLineSegment(sketch, "E2395", {"start": v(-6.62, -2.8) * mm, "end": v(-6.63, -2.78) * mm});
            skLineSegment(sketch, "E2396", {"start": v(-6.63, -2.78) * mm, "end": v(-6.63, -2.78) * mm});
            skLineSegment(sketch, "E2397", {"start": v(-6.63, -2.78) * mm, "end": v(-6.63, -2.77) * mm});
            skLineSegment(sketch, "E2398", {"start": v(-6.63, -2.77) * mm, "end": v(-6.63, -2.76) * mm});
            skLineSegment(sketch, "E2399", {"start": v(-6.63, -2.76) * mm, "end": v(-6.63, -2.75) * mm});
            skLineSegment(sketch, "E2400", {"start": v(-6.63, -2.75) * mm, "end": v(-6.64, -2.74) * mm});
            skLineSegment(sketch, "E2401", {"start": v(-6.64, -2.74) * mm, "end": v(-6.64, -2.74) * mm});
            skLineSegment(sketch, "E2402", {"start": v(-6.64, -2.74) * mm, "end": v(-6.64, -2.73) * mm});
            skLineSegment(sketch, "E2403", {"start": v(-6.64, -2.73) * mm, "end": v(-6.64, -2.72) * mm});
            skLineSegment(sketch, "E2404", {"start": v(-6.64, -2.72) * mm, "end": v(-6.64, -2.71) * mm});
            skLineSegment(sketch, "E2405", {"start": v(-6.64, -2.71) * mm, "end": v(-6.64, -2.7) * mm});
            skLineSegment(sketch, "E2406", {"start": v(-6.64, -2.7) * mm, "end": v(-6.65, -2.7) * mm});
            skLineSegment(sketch, "E2407", {"start": v(-6.65, -2.7) * mm, "end": v(-6.65, -2.69) * mm});
            skLineSegment(sketch, "E2408", {"start": v(-6.65, -2.69) * mm, "end": v(-6.65, -2.68) * mm});
            skLineSegment(sketch, "E2409", {"start": v(-6.65, -2.68) * mm, "end": v(-6.65, -2.67) * mm});
            skLineSegment(sketch, "E2410", {"start": v(-6.65, -2.67) * mm, "end": v(-6.65, -2.66) * mm});
            skLineSegment(sketch, "E2411", {"start": v(-6.65, -2.66) * mm, "end": v(-6.66, -2.65) * mm});
            skLineSegment(sketch, "E2412", {"start": v(-6.66, -2.65) * mm, "end": v(-6.66, -2.65) * mm});
            skLineSegment(sketch, "E2413", {"start": v(-6.66, -2.65) * mm, "end": v(-6.66, -2.64) * mm});
            skLineSegment(sketch, "E2414", {"start": v(-6.66, -2.64) * mm, "end": v(-6.66, -2.63) * mm});
            skLineSegment(sketch, "E2415", {"start": v(-6.66, -2.63) * mm, "end": v(-6.66, -2.62) * mm});
            skLineSegment(sketch, "E2416", {"start": v(-6.66, -2.62) * mm, "end": v(-6.67, -2.61) * mm});
            skLineSegment(sketch, "E2417", {"start": v(-6.67, -2.61) * mm, "end": v(-6.67, -2.6) * mm});
            skLineSegment(sketch, "E2418", {"start": v(-6.67, -2.6) * mm, "end": v(-6.67, -2.6) * mm});
            skLineSegment(sketch, "E2419", {"start": v(-6.67, -2.6) * mm, "end": v(-6.67, -2.59) * mm});
            skLineSegment(sketch, "E2420", {"start": v(-6.67, -2.59) * mm, "end": v(-6.67, -2.58) * mm});
            skLineSegment(sketch, "E2421", {"start": v(-6.67, -2.58) * mm, "end": v(-6.67, -2.58) * mm});
            skLineSegment(sketch, "E2422", {"start": v(-6.67, -2.58) * mm, "end": v(-6.67, -2.57) * mm});
            skLineSegment(sketch, "E2423", {"start": v(-6.67, -2.57) * mm, "end": v(-6.68, -2.57) * mm});
            skLineSegment(sketch, "E2424", {"start": v(-6.68, -2.57) * mm, "end": v(-6.68, -2.56) * mm});
            skLineSegment(sketch, "E2425", {"start": v(-6.68, -2.56) * mm, "end": v(-6.68, -2.55) * mm});
            skLineSegment(sketch, "E2426", {"start": v(-6.68, -2.55) * mm, "end": v(-6.68, -2.55) * mm});
            skLineSegment(sketch, "E2427", {"start": v(-6.68, -2.55) * mm, "end": v(-6.68, -2.54) * mm});
            skLineSegment(sketch, "E2428", {"start": v(-6.68, -2.54) * mm, "end": v(-6.68, -2.54) * mm});
            skLineSegment(sketch, "E2429", {"start": v(-6.68, -2.54) * mm, "end": v(-6.68, -2.53) * mm});
            skLineSegment(sketch, "E2430", {"start": v(-6.68, -2.53) * mm, "end": v(-6.69, -2.52) * mm});
            skLineSegment(sketch, "E2431", {"start": v(-6.69, -2.52) * mm, "end": v(-6.69, -2.52) * mm});
            skLineSegment(sketch, "E2432", {"start": v(-6.69, -2.52) * mm, "end": v(-6.69, -2.51) * mm});
            skLineSegment(sketch, "E2433", {"start": v(-6.69, -2.51) * mm, "end": v(-6.69, -2.5) * mm});
            skLineSegment(sketch, "E2434", {"start": v(-6.69, -2.5) * mm, "end": v(-6.7, -2.5) * mm});
            skLineSegment(sketch, "E2435", {"start": v(-6.7, -2.5) * mm, "end": v(-6.7, -2.5) * mm});
            skLineSegment(sketch, "E2436", {"start": v(-6.7, -2.5) * mm, "end": v(-6.7, -2.48) * mm});
            skLineSegment(sketch, "E2437", {"start": v(-6.7, -2.48) * mm, "end": v(-6.7, -2.48) * mm});
            skLineSegment(sketch, "E2438", {"start": v(-6.7, -2.48) * mm, "end": v(-6.7, -2.47) * mm});
            skLineSegment(sketch, "E2439", {"start": v(-6.7, -2.47) * mm, "end": v(-6.7, -2.47) * mm});
            skLineSegment(sketch, "E2440", {"start": v(-6.7, -2.47) * mm, "end": v(-6.7, -2.46) * mm});
            skLineSegment(sketch, "E2441", {"start": v(-6.7, -2.46) * mm, "end": v(-6.7, -2.46) * mm});
            skLineSegment(sketch, "E2442", {"start": v(-6.7, -2.46) * mm, "end": v(-6.7, -2.45) * mm});
            skLineSegment(sketch, "E2443", {"start": v(-6.7, -2.45) * mm, "end": v(-6.7, -2.44) * mm});
            skLineSegment(sketch, "E2444", {"start": v(-6.7, -2.44) * mm, "end": v(-6.7, -2.44) * mm});
            skLineSegment(sketch, "E2445", {"start": v(-6.7, -2.44) * mm, "end": v(-6.7, -2.43) * mm});
            skLineSegment(sketch, "E2446", {"start": v(-6.7, -2.43) * mm, "end": v(-6.7, -2.43) * mm});
            skLineSegment(sketch, "E2447", {"start": v(-6.7, -2.43) * mm, "end": v(-6.7, -2.42) * mm});
            skLineSegment(sketch, "E2448", {"start": v(-6.7, -2.42) * mm, "end": v(-6.7, -2.42) * mm});
            skLineSegment(sketch, "E2449", {"start": v(-6.7, -2.42) * mm, "end": v(-6.71, -2.4) * mm});
            skLineSegment(sketch, "E2450", {"start": v(-6.71, -2.4) * mm, "end": v(-6.71, -2.4) * mm});
            skLineSegment(sketch, "E2451", {"start": v(-6.71, -2.4) * mm, "end": v(-6.72, -2.4) * mm});
            skLineSegment(sketch, "E2452", {"start": v(-6.72, -2.4) * mm, "end": v(-6.72, -2.39) * mm});
            skLineSegment(sketch, "E2453", {"start": v(-6.72, -2.39) * mm, "end": v(-6.72, -2.38) * mm});
            skLineSegment(sketch, "E2454", {"start": v(-6.72, -2.38) * mm, "end": v(-6.72, -2.37) * mm});
            skLineSegment(sketch, "E2455", {"start": v(-6.72, -2.37) * mm, "end": v(-6.72, -2.37) * mm});
            skLineSegment(sketch, "E2456", {"start": v(-6.72, -2.37) * mm, "end": v(-6.72, -2.36) * mm});
            skLineSegment(sketch, "E2457", {"start": v(-6.72, -2.36) * mm, "end": v(-6.72, -2.36) * mm});
            skLineSegment(sketch, "E2458", {"start": v(-6.72, -2.36) * mm, "end": v(-6.72, -2.35) * mm});
            skLineSegment(sketch, "E2459", {"start": v(-6.72, -2.35) * mm, "end": v(-6.73, -2.35) * mm});
            skLineSegment(sketch, "E2460", {"start": v(-6.73, -2.35) * mm, "end": v(-6.73, -2.34) * mm});
            skLineSegment(sketch, "E2461", {"start": v(-6.73, -2.34) * mm, "end": v(-6.73, -2.33) * mm});
            skLineSegment(sketch, "E2462", {"start": v(-6.73, -2.33) * mm, "end": v(-6.73, -2.33) * mm});
            skLineSegment(sketch, "E2463", {"start": v(-6.73, -2.33) * mm, "end": v(-6.73, -2.32) * mm});
            skLineSegment(sketch, "E2464", {"start": v(-6.73, -2.32) * mm, "end": v(-6.73, -2.32) * mm});
            skLineSegment(sketch, "E2465", {"start": v(-6.73, -2.32) * mm, "end": v(-6.73, -2.31) * mm});
            skLineSegment(sketch, "E2466", {"start": v(-6.73, -2.31) * mm, "end": v(-6.73, -2.3) * mm});
            skLineSegment(sketch, "E2467", {"start": v(-6.73, -2.3) * mm, "end": v(-6.74, -2.3) * mm});
            skLineSegment(sketch, "E2468", {"start": v(-6.74, -2.3) * mm, "end": v(-6.74, -2.3) * mm});
            skLineSegment(sketch, "E2469", {"start": v(-6.74, -2.3) * mm, "end": v(-6.74, -2.29) * mm});
            skLineSegment(sketch, "E2470", {"start": v(-6.74, -2.29) * mm, "end": v(-6.74, -2.28) * mm});
            skLineSegment(sketch, "E2471", {"start": v(-6.74, -2.28) * mm, "end": v(-6.74, -2.28) * mm});
            skLineSegment(sketch, "E2472", {"start": v(-6.74, -2.28) * mm, "end": v(-6.74, -2.27) * mm});
            skLineSegment(sketch, "E2473", {"start": v(-6.74, -2.27) * mm, "end": v(-6.74, -2.27) * mm});
            skLineSegment(sketch, "E2474", {"start": v(-6.74, -2.27) * mm, "end": v(-6.75, -2.26) * mm});
            skLineSegment(sketch, "E2475", {"start": v(-6.75, -2.26) * mm, "end": v(-6.75, -2.25) * mm});
            skLineSegment(sketch, "E2476", {"start": v(-6.75, -2.25) * mm, "end": v(-6.75, -2.25) * mm});
            skLineSegment(sketch, "E2477", {"start": v(-6.75, -2.25) * mm, "end": v(-6.75, -2.24) * mm});
            skLineSegment(sketch, "E2478", {"start": v(-6.75, -2.24) * mm, "end": v(-6.75, -2.24) * mm});
            skLineSegment(sketch, "E2479", {"start": v(-6.75, -2.24) * mm, "end": v(-6.75, -2.23) * mm});
            skLineSegment(sketch, "E2480", {"start": v(-6.75, -2.23) * mm, "end": v(-6.75, -2.23) * mm});
            skLineSegment(sketch, "E2481", {"start": v(-6.75, -2.23) * mm, "end": v(-6.75, -2.22) * mm});
            skLineSegment(sketch, "E2482", {"start": v(-6.75, -2.22) * mm, "end": v(-6.76, -2.21) * mm});
            skLineSegment(sketch, "E2483", {"start": v(-6.76, -2.21) * mm, "end": v(-6.76, -2.2) * mm});
            skLineSegment(sketch, "E2484", {"start": v(-6.76, -2.2) * mm, "end": v(-6.76, -2.2) * mm});
            skLineSegment(sketch, "E2485", {"start": v(-6.76, -2.2) * mm, "end": v(-6.76, -2.18) * mm});
            skLineSegment(sketch, "E2486", {"start": v(-6.76, -2.18) * mm, "end": v(-6.76, -2.18) * mm});
            skLineSegment(sketch, "E2487", {"start": v(-6.76, -2.18) * mm, "end": v(-6.76, -2.17) * mm});
            skLineSegment(sketch, "E2488", {"start": v(-6.76, -2.17) * mm, "end": v(-6.77, -2.17) * mm});
            skLineSegment(sketch, "E2489", {"start": v(-6.77, -2.17) * mm, "end": v(-6.77, -2.16) * mm});
            skLineSegment(sketch, "E2490", {"start": v(-6.77, -2.16) * mm, "end": v(-6.77, -2.16) * mm});
            skLineSegment(sketch, "E2491", {"start": v(-6.77, -2.16) * mm, "end": v(-6.77, -2.15) * mm});
            skLineSegment(sketch, "E2492", {"start": v(-6.77, -2.15) * mm, "end": v(-6.77, -2.14) * mm});
            skLineSegment(sketch, "E2493", {"start": v(-6.77, -2.14) * mm, "end": v(-6.77, -2.14) * mm});
            skLineSegment(sketch, "E2494", {"start": v(-6.77, -2.14) * mm, "end": v(-6.77, -2.13) * mm});
            skLineSegment(sketch, "E2495", {"start": v(-6.77, -2.13) * mm, "end": v(-6.78, -2.13) * mm});
            skLineSegment(sketch, "E2496", {"start": v(-6.78, -2.13) * mm, "end": v(-6.78, -2.12) * mm});
            skLineSegment(sketch, "E2497", {"start": v(-6.78, -2.12) * mm, "end": v(-6.78, -2.12) * mm});
            skLineSegment(sketch, "E2498", {"start": v(-6.78, -2.12) * mm, "end": v(-6.78, -2.1) * mm});
            skLineSegment(sketch, "E2499", {"start": v(-6.78, -2.1) * mm, "end": v(-6.78, -2.1) * mm});
            skLineSegment(sketch, "E2500", {"start": v(-6.78, -2.1) * mm, "end": v(-6.78, -2.09) * mm});
            skLineSegment(sketch, "E2501", {"start": v(-6.78, -2.09) * mm, "end": v(-6.79, -2.08) * mm});
            skLineSegment(sketch, "E2502", {"start": v(-6.79, -2.08) * mm, "end": v(-6.79, -2.08) * mm});
            skLineSegment(sketch, "E2503", {"start": v(-6.79, -2.08) * mm, "end": v(-6.79, -2.07) * mm});
            skLineSegment(sketch, "E2504", {"start": v(-6.79, -2.07) * mm, "end": v(-6.79, -2.06) * mm});
            skLineSegment(sketch, "E2505", {"start": v(-6.79, -2.06) * mm, "end": v(-6.8, -2.06) * mm});
            skLineSegment(sketch, "E2506", {"start": v(-6.8, -2.06) * mm, "end": v(-6.8, -2.05) * mm});
            skLineSegment(sketch, "E2507", {"start": v(-6.8, -2.05) * mm, "end": v(-6.8, -2.05) * mm});
            skLineSegment(sketch, "E2508", {"start": v(-6.8, -2.05) * mm, "end": v(-6.8, -2.04) * mm});
            skLineSegment(sketch, "E2509", {"start": v(-6.8, -2.04) * mm, "end": v(-6.8, -2.03) * mm});
            skLineSegment(sketch, "E2510", {"start": v(-6.8, -2.03) * mm, "end": v(-6.8, -2.03) * mm});
            skLineSegment(sketch, "E2511", {"start": v(-6.8, -2.03) * mm, "end": v(-6.8, -2.02) * mm});
            skLineSegment(sketch, "E2512", {"start": v(-6.8, -2.02) * mm, "end": v(-6.8, -2.02) * mm});
            skLineSegment(sketch, "E2513", {"start": v(-6.8, -2.02) * mm, "end": v(-6.8, -2.01) * mm});
            skLineSegment(sketch, "E2514", {"start": v(-6.8, -2.01) * mm, "end": v(-6.8, -2) * mm});
            skLineSegment(sketch, "E2515", {"start": v(-6.8, -2) * mm, "end": v(-6.8, -2) * mm});
            skLineSegment(sketch, "E2516", {"start": v(-6.8, -2) * mm, "end": v(-6.8, -1.99) * mm});
            skLineSegment(sketch, "E2517", {"start": v(-6.8, -1.99) * mm, "end": v(-6.8, -1.98) * mm});
            skLineSegment(sketch, "E2518", {"start": v(-6.8, -1.98) * mm, "end": v(-6.8, -1.98) * mm});
            skLineSegment(sketch, "E2519", {"start": v(-6.8, -1.98) * mm, "end": v(-6.81, -1.97) * mm});
            skLineSegment(sketch, "E2520", {"start": v(-6.81, -1.97) * mm, "end": v(-6.81, -1.97) * mm});
            skLineSegment(sketch, "E2521", {"start": v(-6.81, -1.97) * mm, "end": v(-6.81, -1.96) * mm});
            skLineSegment(sketch, "E2522", {"start": v(-6.81, -1.96) * mm, "end": v(-6.81, -1.95) * mm});
            skLineSegment(sketch, "E2523", {"start": v(-6.81, -1.95) * mm, "end": v(-6.82, -1.95) * mm});
            skLineSegment(sketch, "E2524", {"start": v(-6.82, -1.95) * mm, "end": v(-6.82, -1.94) * mm});
            skLineSegment(sketch, "E2525", {"start": v(-6.82, -1.94) * mm, "end": v(-6.82, -1.94) * mm});
            skLineSegment(sketch, "E2526", {"start": v(-6.82, -1.94) * mm, "end": v(-6.82, -1.93) * mm});
            skLineSegment(sketch, "E2527", {"start": v(-6.82, -1.93) * mm, "end": v(-6.82, -1.93) * mm});
            skLineSegment(sketch, "E2528", {"start": v(-6.82, -1.93) * mm, "end": v(-6.82, -1.92) * mm});
            skLineSegment(sketch, "E2529", {"start": v(-6.82, -1.92) * mm, "end": v(-6.82, -1.91) * mm});
            skLineSegment(sketch, "E2530", {"start": v(-6.82, -1.91) * mm, "end": v(-6.82, -1.9) * mm});
            skLineSegment(sketch, "E2531", {"start": v(-6.82, -1.9) * mm, "end": v(-6.83, -1.9) * mm});
            skLineSegment(sketch, "E2532", {"start": v(-6.83, -1.9) * mm, "end": v(-6.83, -1.9) * mm});
            skLineSegment(sketch, "E2533", {"start": v(-6.83, -1.9) * mm, "end": v(-6.83, -1.89) * mm});
            skLineSegment(sketch, "E2534", {"start": v(-6.83, -1.89) * mm, "end": v(-6.83, -1.88) * mm});
            skLineSegment(sketch, "E2535", {"start": v(-6.83, -1.88) * mm, "end": v(-6.83, -1.87) * mm});
            skLineSegment(sketch, "E2536", {"start": v(-6.83, -1.87) * mm, "end": v(-6.83, -1.87) * mm});
            skLineSegment(sketch, "E2537", {"start": v(-6.83, -1.87) * mm, "end": v(-6.85, -1.78) * mm});
            skLineSegment(sketch, "E2538", {"start": v(-6.85, -1.78) * mm, "end": v(-6.87, -1.69) * mm});
            skLineSegment(sketch, "E2539", {"start": v(-6.87, -1.69) * mm, "end": v(-6.9, -1.6) * mm});
            skLineSegment(sketch, "E2540", {"start": v(-6.9, -1.6) * mm, "end": v(-6.92, -1.51) * mm});
            skLineSegment(sketch, "E2541", {"start": v(-6.92, -1.51) * mm, "end": v(-6.94, -1.42) * mm});
            skLineSegment(sketch, "E2542", {"start": v(-6.94, -1.42) * mm, "end": v(-6.96, -1.33) * mm});
            skLineSegment(sketch, "E2543", {"start": v(-6.96, -1.33) * mm, "end": v(-6.98, -1.24) * mm});
            skLineSegment(sketch, "E2544", {"start": v(-6.98, -1.24) * mm, "end": v(-7, -1.15) * mm});
            skLineSegment(sketch, "E2545", {"start": v(-7, -1.15) * mm, "end": v(-7.02, -1.07) * mm});
            skLineSegment(sketch, "E2546", {"start": v(-7.02, -1.07) * mm, "end": v(-7.04, -0.98) * mm});
            skLineSegment(sketch, "E2547", {"start": v(-7.04, -0.98) * mm, "end": v(-7.06, -0.89) * mm});
            skLineSegment(sketch, "E2548", {"start": v(-7.06, -0.89) * mm, "end": v(-7.08, -0.8) * mm});
            skLineSegment(sketch, "E2549", {"start": v(-7.08, -0.8) * mm, "end": v(-7.1, -0.71) * mm});
            skLineSegment(sketch, "E2550", {"start": v(-7.1, -0.71) * mm, "end": v(-7.12, -0.62) * mm});
            skLineSegment(sketch, "E2551", {"start": v(-7.12, -0.62) * mm, "end": v(-7.14, -0.53) * mm});
            skLineSegment(sketch, "E2552", {"start": v(-7.14, -0.53) * mm, "end": v(-7.16, -0.45) * mm});
            skLineSegment(sketch, "E2553", {"start": v(-7.16, -0.45) * mm, "end": v(-7.18, -0.36) * mm});
            skLineSegment(sketch, "E2554", {"start": v(-7.18, -0.36) * mm, "end": v(-7.2, -0.27) * mm});
            skLineSegment(sketch, "E2555", {"start": v(-7.2, -0.27) * mm, "end": v(-7.22, -0.18) * mm});
            skLineSegment(sketch, "E2556", {"start": v(-7.22, -0.18) * mm, "end": v(-7.24, -0.1) * mm});
            skLineSegment(sketch, "E2557", {"start": v(-7.24, -0.1) * mm, "end": v(-7.26, 0) * mm});
            skLineSegment(sketch, "E2558", {"start": v(-7.26, 0) * mm, "end": v(-7.28, 0.08) * mm});
            skLineSegment(sketch, "E2559", {"start": v(-7.28, 0.08) * mm, "end": v(-7.3, 0.17) * mm});
            skLineSegment(sketch, "E2560", {"start": v(-7.3, 0.17) * mm, "end": v(-7.32, 0.26) * mm});
            skLineSegment(sketch, "E2561", {"start": v(-7.32, 0.26) * mm, "end": v(-7.34, 0.35) * mm});
            skLineSegment(sketch, "E2562", {"start": v(-7.34, 0.35) * mm, "end": v(-7.36, 0.44) * mm});
            skLineSegment(sketch, "E2563", {"start": v(-7.36, 0.44) * mm, "end": v(-7.39, 0.52) * mm});
            skLineSegment(sketch, "E2564", {"start": v(-7.39, 0.52) * mm, "end": v(-7.4, 0.61) * mm});
            skLineSegment(sketch, "E2565", {"start": v(-7.4, 0.61) * mm, "end": v(-7.43, 0.7) * mm});
            skLineSegment(sketch, "E2566", {"start": v(-7.43, 0.7) * mm, "end": v(-7.45, 0.79) * mm});
            skLineSegment(sketch, "E2567", {"start": v(-7.45, 0.79) * mm, "end": v(-7.47, 0.87) * mm});
            skLineSegment(sketch, "E2568", {"start": v(-7.47, 0.87) * mm, "end": v(-7.5, 0.96) * mm});
            skLineSegment(sketch, "E2569", {"start": v(-7.5, 0.96) * mm, "end": v(-7.51, 1.05) * mm});
            skLineSegment(sketch, "E2570", {"start": v(-7.51, 1.05) * mm, "end": v(-7.53, 1.13) * mm});
            skLineSegment(sketch, "E2571", {"start": v(-7.53, 1.13) * mm, "end": v(-7.56, 1.22) * mm});
            skLineSegment(sketch, "E2572", {"start": v(-7.56, 1.22) * mm, "end": v(-7.58, 1.3) * mm});
            skLineSegment(sketch, "E2573", {"start": v(-7.58, 1.3) * mm, "end": v(-7.6, 1.4) * mm});
            skLineSegment(sketch, "E2574", {"start": v(-7.6, 1.4) * mm, "end": v(-7.62, 1.48) * mm});
            skLineSegment(sketch, "E2575", {"start": v(-7.62, 1.48) * mm, "end": v(-7.64, 1.57) * mm});
            skLineSegment(sketch, "E2576", {"start": v(-7.64, 1.57) * mm, "end": v(-7.67, 1.66) * mm});
            skLineSegment(sketch, "E2577", {"start": v(-7.67, 1.66) * mm, "end": v(-7.69, 1.74) * mm});
            skLineSegment(sketch, "E2578", {"start": v(-7.69, 1.74) * mm, "end": v(-7.7, 1.83) * mm});
            skLineSegment(sketch, "E2579", {"start": v(-7.7, 1.83) * mm, "end": v(-7.73, 1.92) * mm});
            skLineSegment(sketch, "E2580", {"start": v(-7.73, 1.92) * mm, "end": v(-7.76, 2) * mm});
            skLineSegment(sketch, "E2581", {"start": v(-7.76, 2) * mm, "end": v(-7.78, 2.1) * mm});
            skLineSegment(sketch, "E2582", {"start": v(-7.78, 2.1) * mm, "end": v(-7.8, 2.18) * mm});
            skLineSegment(sketch, "E2583", {"start": v(-7.8, 2.18) * mm, "end": v(-7.82, 2.26) * mm});
            skLineSegment(sketch, "E2584", {"start": v(-7.82, 2.26) * mm, "end": v(-7.85, 2.35) * mm});
            skLineSegment(sketch, "E2585", {"start": v(-7.85, 2.35) * mm, "end": v(-7.87, 2.44) * mm});
            skLineSegment(sketch, "E2586", {"start": v(-7.87, 2.44) * mm, "end": v(-7.9, 2.52) * mm});
            skLineSegment(sketch, "E2587", {"start": v(-7.9, 2.52) * mm, "end": v(-7.92, 2.6) * mm});
            skLineSegment(sketch, "E2588", {"start": v(-7.92, 2.6) * mm, "end": v(-7.94, 2.7) * mm});
            skLineSegment(sketch, "E2589", {"start": v(-7.94, 2.7) * mm, "end": v(-7.96, 2.78) * mm});
            skLineSegment(sketch, "E2590", {"start": v(-7.96, 2.78) * mm, "end": v(-7.99, 2.87) * mm});
            skLineSegment(sketch, "E2591", {"start": v(-7.99, 2.87) * mm, "end": v(-8.01, 2.95) * mm});
            skLineSegment(sketch, "E2592", {"start": v(-8.01, 2.95) * mm, "end": v(-8.04, 3.04) * mm});
            skLineSegment(sketch, "E2593", {"start": v(-8.04, 3.04) * mm, "end": v(-8.06, 3.12) * mm});
            skLineSegment(sketch, "E2594", {"start": v(-8.06, 3.12) * mm, "end": v(-8.09, 3.21) * mm});
            skLineSegment(sketch, "E2595", {"start": v(-8.09, 3.21) * mm, "end": v(-8.11, 3.3) * mm});
            skLineSegment(sketch, "E2596", {"start": v(-8.11, 3.3) * mm, "end": v(-8.14, 3.38) * mm});
            skLineSegment(sketch, "E2597", {"start": v(-8.14, 3.38) * mm, "end": v(-8.16, 3.47) * mm});
            skLineSegment(sketch, "E2598", {"start": v(-8.16, 3.47) * mm, "end": v(-8.19, 3.55) * mm});
            skLineSegment(sketch, "E2599", {"start": v(-8.19, 3.55) * mm, "end": v(-8.21, 3.64) * mm});
            skLineSegment(sketch, "E2600", {"start": v(-8.21, 3.64) * mm, "end": v(-8.24, 3.73) * mm});
            skLineSegment(sketch, "E2601", {"start": v(-8.24, 3.73) * mm, "end": v(-8.26, 3.81) * mm});
            skLineSegment(sketch, "E2602", {"start": v(-8.26, 3.81) * mm, "end": v(-8.29, 3.9) * mm});
            skLineSegment(sketch, "E2603", {"start": v(-8.29, 3.9) * mm, "end": v(-8.32, 3.98) * mm});
            skLineSegment(sketch, "E2604", {"start": v(-8.32, 3.98) * mm, "end": v(-8.34, 4.07) * mm});
            skLineSegment(sketch, "E2605", {"start": v(-8.34, 4.07) * mm, "end": v(-8.37, 4.15) * mm});
            skLineSegment(sketch, "E2606", {"start": v(-8.37, 4.15) * mm, "end": v(-8.4, 4.24) * mm});
            skLineSegment(sketch, "E2607", {"start": v(-8.4, 4.24) * mm, "end": v(-8.42, 4.32) * mm});
            skLineSegment(sketch, "E2608", {"start": v(-8.42, 4.32) * mm, "end": v(-8.45, 4.4) * mm});
            skLineSegment(sketch, "E2609", {"start": v(-8.45, 4.4) * mm, "end": v(-8.48, 4.5) * mm});
            skLineSegment(sketch, "E2610", {"start": v(-8.48, 4.5) * mm, "end": v(-8.5, 4.58) * mm});
            skLineSegment(sketch, "E2611", {"start": v(-8.5, 4.58) * mm, "end": v(-8.53, 4.66) * mm});
            skLineSegment(sketch, "E2612", {"start": v(-8.53, 4.66) * mm, "end": v(-8.56, 4.75) * mm});
            skLineSegment(sketch, "E2613", {"start": v(-8.56, 4.75) * mm, "end": v(-8.6, 4.84) * mm});
            skLineSegment(sketch, "E2614", {"start": v(-8.6, 4.84) * mm, "end": v(-8.62, 4.92) * mm});
            skLineSegment(sketch, "E2615", {"start": v(-8.62, 4.92) * mm, "end": v(-8.65, 5) * mm});
            skLineSegment(sketch, "E2616", {"start": v(-8.65, 5) * mm, "end": v(-8.68, 5.1) * mm});
            skLineSegment(sketch, "E2617", {"start": v(-8.68, 5.1) * mm, "end": v(-8.7, 5.18) * mm});
            skLineSegment(sketch, "E2618", {"start": v(-8.7, 5.18) * mm, "end": v(-8.74, 5.26) * mm});
            skLineSegment(sketch, "E2619", {"start": v(-8.74, 5.26) * mm, "end": v(-8.77, 5.35) * mm});
            skLineSegment(sketch, "E2620", {"start": v(-8.77, 5.35) * mm, "end": v(-8.8, 5.43) * mm});
            skLineSegment(sketch, "E2621", {"start": v(-8.8, 5.43) * mm, "end": v(-8.83, 5.51) * mm});
            skLineSegment(sketch, "E2622", {"start": v(-8.83, 5.51) * mm, "end": v(-8.86, 5.6) * mm});
            skLineSegment(sketch, "E2623", {"start": v(-8.86, 5.6) * mm, "end": v(-8.89, 5.68) * mm});
            skLineSegment(sketch, "E2624", {"start": v(-8.89, 5.68) * mm, "end": v(-8.92, 5.77) * mm});
            skLineSegment(sketch, "E2625", {"start": v(-8.92, 5.77) * mm, "end": v(-8.95, 5.85) * mm});
            skLineSegment(sketch, "E2626", {"start": v(-8.95, 5.85) * mm, "end": v(-8.98, 5.94) * mm});
            skLineSegment(sketch, "E2627", {"start": v(-8.98, 5.94) * mm, "end": v(-9.01, 6.02) * mm});
            skLineSegment(sketch, "E2628", {"start": v(-9.01, 6.02) * mm, "end": v(-9.05, 6.1) * mm});
            skLineSegment(sketch, "E2629", {"start": v(-9.05, 6.1) * mm, "end": v(-9.08, 6.2) * mm});
            skLineSegment(sketch, "E2630", {"start": v(-9.08, 6.2) * mm, "end": v(-9.11, 6.28) * mm});
            skLineSegment(sketch, "E2631", {"start": v(-9.11, 6.28) * mm, "end": v(-9.15, 6.36) * mm});
            skLineSegment(sketch, "E2632", {"start": v(-9.15, 6.36) * mm, "end": v(-9.18, 6.45) * mm});
            skLineSegment(sketch, "E2633", {"start": v(-9.18, 6.45) * mm, "end": v(-9.21, 6.53) * mm});
            skLineSegment(sketch, "E2634", {"start": v(-9.21, 6.53) * mm, "end": v(-9.25, 6.61) * mm});
            skLineSegment(sketch, "E2635", {"start": v(-9.25, 6.61) * mm, "end": v(-9.28, 6.7) * mm});
            skLineSegment(sketch, "E2636", {"start": v(-9.28, 6.7) * mm, "end": v(-9.32, 6.78) * mm});
            skLineSegment(sketch, "E2637", {"start": v(-9.32, 6.78) * mm, "end": v(-9.35, 6.87) * mm});
            skLineSegment(sketch, "E2638", {"start": v(-9.35, 6.87) * mm, "end": v(-9.39, 6.95) * mm});
            skLineSegment(sketch, "E2639", {"start": v(-9.39, 6.95) * mm, "end": v(-9.42, 7.04) * mm});
            skLineSegment(sketch, "E2640", {"start": v(-9.42, 7.04) * mm, "end": v(-9.46, 7.12) * mm});
            skLineSegment(sketch, "E2641", {"start": v(-9.46, 7.12) * mm, "end": v(-9.5, 7.2) * mm});
            skLineSegment(sketch, "E2642", {"start": v(-9.5, 7.2) * mm, "end": v(-9.53, 7.29) * mm});
            skLineSegment(sketch, "E2643", {"start": v(-9.53, 7.29) * mm, "end": v(-9.57, 7.37) * mm});
            skLineSegment(sketch, "E2644", {"start": v(-9.57, 7.37) * mm, "end": v(-9.6, 7.46) * mm});
            skLineSegment(sketch, "E2645", {"start": v(-9.6, 7.46) * mm, "end": v(-9.64, 7.54) * mm});
            skLineSegment(sketch, "E2646", {"start": v(-9.64, 7.54) * mm, "end": v(-9.68, 7.63) * mm});
            skLineSegment(sketch, "E2647", {"start": v(-9.68, 7.63) * mm, "end": v(-9.72, 7.71) * mm});
            skLineSegment(sketch, "E2648", {"start": v(-9.72, 7.71) * mm, "end": v(-9.76, 7.8) * mm});
            skLineSegment(sketch, "E2649", {"start": v(-9.76, 7.8) * mm, "end": v(-9.8, 7.88) * mm});
            skLineSegment(sketch, "E2650", {"start": v(-9.8, 7.88) * mm, "end": v(-9.83, 7.96) * mm});
            skLineSegment(sketch, "E2651", {"start": v(-9.83, 7.96) * mm, "end": v(-9.87, 8.05) * mm});
            skLineSegment(sketch, "E2652", {"start": v(-9.87, 8.05) * mm, "end": v(-9.91, 8.13) * mm});
            skLineSegment(sketch, "E2653", {"start": v(-9.91, 8.13) * mm, "end": v(-9.95, 8.22) * mm});
            skLineSegment(sketch, "E2654", {"start": v(-9.95, 8.22) * mm, "end": v(-10, 8.3) * mm});
            skLineSegment(sketch, "E2655", {"start": v(-10, 8.3) * mm, "end": v(-10.04, 8.38) * mm});
            skLineSegment(sketch, "E2656", {"start": v(-10.04, 8.38) * mm, "end": v(-10.08, 8.47) * mm});
            skLineSegment(sketch, "E2657", {"start": v(-10.08, 8.47) * mm, "end": v(-10.12, 8.55) * mm});
            skLineSegment(sketch, "E2658", {"start": v(-10.12, 8.55) * mm, "end": v(-10.16, 8.64) * mm});
            skLineSegment(sketch, "E2659", {"start": v(-10.16, 8.64) * mm, "end": v(-10.2, 8.72) * mm});
            skLineSegment(sketch, "E2660", {"start": v(-10.2, 8.72) * mm, "end": v(-10.25, 8.8) * mm});
            skLineSegment(sketch, "E2661", {"start": v(-10.25, 8.8) * mm, "end": v(-10.3, 8.89) * mm});
            skLineSegment(sketch, "E2662", {"start": v(-10.3, 8.89) * mm, "end": v(-10.33, 8.97) * mm});
            skLineSegment(sketch, "E2663", {"start": v(-10.33, 8.97) * mm, "end": v(-10.38, 9.05) * mm});
            skLineSegment(sketch, "E2664", {"start": v(-10.38, 9.05) * mm, "end": v(-10.42, 9.14) * mm});
            skLineSegment(sketch, "E2665", {"start": v(-10.42, 9.14) * mm, "end": v(-10.46, 9.2) * mm});
            skLineSegment(sketch, "E2666", {"start": v(-10.46, 9.2) * mm, "end": v(-10.49, 9.26) * mm});
            skLineSegment(sketch, "E2667", {"start": v(-10.49, 9.26) * mm, "end": v(-10.52, 9.32) * mm});
            skLineSegment(sketch, "E2668", {"start": v(-10.52, 9.32) * mm, "end": v(-10.56, 9.38) * mm});
            skLineSegment(sketch, "E2669", {"start": v(-10.56, 9.38) * mm, "end": v(-10.6, 9.44) * mm});
            skLineSegment(sketch, "E2670", {"start": v(-10.6, 9.44) * mm, "end": v(-10.62, 9.5) * mm});
            skLineSegment(sketch, "E2671", {"start": v(-10.62, 9.5) * mm, "end": v(-10.66, 9.57) * mm});
            skLineSegment(sketch, "E2672", {"start": v(-10.66, 9.57) * mm, "end": v(-10.7, 9.63) * mm});
            skLineSegment(sketch, "E2673", {"start": v(-10.7, 9.63) * mm, "end": v(-10.73, 9.69) * mm});
            skLineSegment(sketch, "E2674", {"start": v(-10.73, 9.69) * mm, "end": v(-10.76, 9.75) * mm});
            skLineSegment(sketch, "E2675", {"start": v(-10.76, 9.75) * mm, "end": v(-10.8, 9.8) * mm});
            skLineSegment(sketch, "E2676", {"start": v(-10.8, 9.8) * mm, "end": v(-10.83, 9.86) * mm});
            skLineSegment(sketch, "E2677", {"start": v(-10.83, 9.86) * mm, "end": v(-10.87, 9.92) * mm});
            skLineSegment(sketch, "E2678", {"start": v(-10.87, 9.92) * mm, "end": v(-10.9, 9.98) * mm});
            skLineSegment(sketch, "E2679", {"start": v(-10.9, 9.98) * mm, "end": v(-10.94, 10.04) * mm});
            skLineSegment(sketch, "E2680", {"start": v(-10.94, 10.04) * mm, "end": v(-10.98, 10.1) * mm});
            skLineSegment(sketch, "E2681", {"start": v(-10.98, 10.1) * mm, "end": v(-11.02, 10.16) * mm});
            skLineSegment(sketch, "E2682", {"start": v(-11.02, 10.16) * mm, "end": v(-11.05, 10.21) * mm});
            skLineSegment(sketch, "E2683", {"start": v(-11.05, 10.21) * mm, "end": v(-11.09, 10.27) * mm});
            skLineSegment(sketch, "E2684", {"start": v(-11.09, 10.27) * mm, "end": v(-11.13, 10.33) * mm});
            skLineSegment(sketch, "E2685", {"start": v(-11.13, 10.33) * mm, "end": v(-11.16, 10.39) * mm});
            skLineSegment(sketch, "E2686", {"start": v(-11.16, 10.39) * mm, "end": v(-11.2, 10.44) * mm});
            skLineSegment(sketch, "E2687", {"start": v(-11.2, 10.44) * mm, "end": v(-11.24, 10.5) * mm});
            skLineSegment(sketch, "E2688", {"start": v(-11.24, 10.5) * mm, "end": v(-11.28, 10.56) * mm});
            skLineSegment(sketch, "E2689", {"start": v(-11.28, 10.56) * mm, "end": v(-11.32, 10.61) * mm});
            skLineSegment(sketch, "E2690", {"start": v(-11.32, 10.61) * mm, "end": v(-11.36, 10.67) * mm});
            skLineSegment(sketch, "E2691", {"start": v(-11.36, 10.67) * mm, "end": v(-11.4, 10.73) * mm});
            skLineSegment(sketch, "E2692", {"start": v(-11.4, 10.73) * mm, "end": v(-11.44, 10.78) * mm});
            skLineSegment(sketch, "E2693", {"start": v(-11.44, 10.78) * mm, "end": v(-11.48, 10.84) * mm});
            skLineSegment(sketch, "E2694", {"start": v(-11.48, 10.84) * mm, "end": v(-11.52, 10.9) * mm});
            skLineSegment(sketch, "E2695", {"start": v(-11.52, 10.9) * mm, "end": v(-11.56, 10.95) * mm});
            skLineSegment(sketch, "E2696", {"start": v(-11.56, 10.95) * mm, "end": v(-11.6, 11) * mm});
            skLineSegment(sketch, "E2697", {"start": v(-11.6, 11) * mm, "end": v(-11.64, 11.06) * mm});
            skLineSegment(sketch, "E2698", {"start": v(-11.64, 11.06) * mm, "end": v(-11.68, 11.11) * mm});
            skLineSegment(sketch, "E2699", {"start": v(-11.68, 11.11) * mm, "end": v(-11.72, 11.17) * mm});
            skLineSegment(sketch, "E2700", {"start": v(-11.72, 11.17) * mm, "end": v(-11.76, 11.22) * mm});
            skLineSegment(sketch, "E2701", {"start": v(-11.76, 11.22) * mm, "end": v(-11.8, 11.27) * mm});
            skLineSegment(sketch, "E2702", {"start": v(-11.8, 11.27) * mm, "end": v(-11.84, 11.33) * mm});
            skLineSegment(sketch, "E2703", {"start": v(-11.84, 11.33) * mm, "end": v(-11.89, 11.38) * mm});
            skLineSegment(sketch, "E2704", {"start": v(-11.89, 11.38) * mm, "end": v(-11.93, 11.44) * mm});
            skLineSegment(sketch, "E2705", {"start": v(-11.93, 11.44) * mm, "end": v(-11.97, 11.49) * mm});
            skLineSegment(sketch, "E2706", {"start": v(-11.97, 11.49) * mm, "end": v(-12.01, 11.54) * mm});
            skLineSegment(sketch, "E2707", {"start": v(-12.01, 11.54) * mm, "end": v(-12.06, 11.6) * mm});
            skLineSegment(sketch, "E2708", {"start": v(-12.06, 11.6) * mm, "end": v(-12.1, 11.65) * mm});
            skLineSegment(sketch, "E2709", {"start": v(-12.1, 11.65) * mm, "end": v(-12.15, 11.7) * mm});
            skLineSegment(sketch, "E2710", {"start": v(-12.15, 11.7) * mm, "end": v(-12.19, 11.75) * mm});
            skLineSegment(sketch, "E2711", {"start": v(-12.19, 11.75) * mm, "end": v(-12.23, 11.8) * mm});
            skLineSegment(sketch, "E2712", {"start": v(-12.23, 11.8) * mm, "end": v(-12.28, 11.86) * mm});
            skLineSegment(sketch, "E2713", {"start": v(-12.28, 11.86) * mm, "end": v(-12.32, 11.9) * mm});
            skLineSegment(sketch, "E2714", {"start": v(-12.32, 11.9) * mm, "end": v(-12.37, 11.96) * mm});
            skLineSegment(sketch, "E2715", {"start": v(-12.37, 11.96) * mm, "end": v(-12.41, 12) * mm});
            skLineSegment(sketch, "E2716", {"start": v(-12.41, 12) * mm, "end": v(-12.46, 12.06) * mm});
            skLineSegment(sketch, "E2717", {"start": v(-12.46, 12.06) * mm, "end": v(-12.5, 12.11) * mm});
            skLineSegment(sketch, "E2718", {"start": v(-12.5, 12.11) * mm, "end": v(-12.55, 12.16) * mm});
            skLineSegment(sketch, "E2719", {"start": v(-12.55, 12.16) * mm, "end": v(-12.6, 12.21) * mm});
            skLineSegment(sketch, "E2720", {"start": v(-12.6, 12.21) * mm, "end": v(-12.65, 12.26) * mm});
            skLineSegment(sketch, "E2721", {"start": v(-12.65, 12.26) * mm, "end": v(-12.7, 12.31) * mm});
            skLineSegment(sketch, "E2722", {"start": v(-12.7, 12.31) * mm, "end": v(-12.74, 12.36) * mm});
            skLineSegment(sketch, "E2723", {"start": v(-12.74, 12.36) * mm, "end": v(-12.79, 12.41) * mm});
            skLineSegment(sketch, "E2724", {"start": v(-12.79, 12.41) * mm, "end": v(-12.84, 12.46) * mm});
            skLineSegment(sketch, "E2725", {"start": v(-12.84, 12.46) * mm, "end": v(-12.88, 12.51) * mm});
            skLineSegment(sketch, "E2726", {"start": v(-12.88, 12.51) * mm, "end": v(-12.93, 12.56) * mm});
            skLineSegment(sketch, "E2727", {"start": v(-12.93, 12.56) * mm, "end": v(-12.98, 12.61) * mm});
            skLineSegment(sketch, "E2728", {"start": v(-12.98, 12.61) * mm, "end": v(-13.03, 12.66) * mm});
            skLineSegment(sketch, "E2729", {"start": v(-13.03, 12.66) * mm, "end": v(-13.08, 12.7) * mm});
            skLineSegment(sketch, "E2730", {"start": v(-13.08, 12.7) * mm, "end": v(-13.13, 12.76) * mm});
            skLineSegment(sketch, "E2731", {"start": v(-13.13, 12.76) * mm, "end": v(-13.18, 12.8) * mm});
            skLineSegment(sketch, "E2732", {"start": v(-13.18, 12.8) * mm, "end": v(-13.23, 12.85) * mm});
            skLineSegment(sketch, "E2733", {"start": v(-13.23, 12.85) * mm, "end": v(-13.28, 12.9) * mm});
            skLineSegment(sketch, "E2734", {"start": v(-13.28, 12.9) * mm, "end": v(-13.33, 12.95) * mm});
            skLineSegment(sketch, "E2735", {"start": v(-13.33, 12.95) * mm, "end": v(-13.38, 13) * mm});
            skLineSegment(sketch, "E2736", {"start": v(-13.38, 13) * mm, "end": v(-13.43, 13.04) * mm});
            skLineSegment(sketch, "E2737", {"start": v(-13.43, 13.04) * mm, "end": v(-13.48, 13.1) * mm});
            skLineSegment(sketch, "E2738", {"start": v(-13.48, 13.1) * mm, "end": v(-13.54, 13.14) * mm});
            skLineSegment(sketch, "E2739", {"start": v(-13.54, 13.14) * mm, "end": v(-13.59, 13.19) * mm});
            skLineSegment(sketch, "E2740", {"start": v(-13.59, 13.19) * mm, "end": v(-13.64, 13.23) * mm});
            skLineSegment(sketch, "E2741", {"start": v(-13.64, 13.23) * mm, "end": v(-13.7, 13.28) * mm});
            skLineSegment(sketch, "E2742", {"start": v(-13.7, 13.28) * mm, "end": v(-13.75, 13.33) * mm});
            skLineSegment(sketch, "E2743", {"start": v(-13.75, 13.33) * mm, "end": v(-13.8, 13.37) * mm});
            skLineSegment(sketch, "E2744", {"start": v(-13.8, 13.37) * mm, "end": v(-13.85, 13.42) * mm});
            skLineSegment(sketch, "E2745", {"start": v(-13.85, 13.42) * mm, "end": v(-13.9, 13.47) * mm});
            skLineSegment(sketch, "E2746", {"start": v(-13.9, 13.47) * mm, "end": v(-13.96, 13.51) * mm});
            skLineSegment(sketch, "E2747", {"start": v(-13.96, 13.51) * mm, "end": v(-14.02, 13.56) * mm});
            skLineSegment(sketch, "E2748", {"start": v(-14.02, 13.56) * mm, "end": v(-14.07, 13.6) * mm});
            skLineSegment(sketch, "E2749", {"start": v(-14.07, 13.6) * mm, "end": v(-14.13, 13.65) * mm});
            skLineSegment(sketch, "E2750", {"start": v(-14.13, 13.65) * mm, "end": v(-14.18, 13.7) * mm});
            skLineSegment(sketch, "E2751", {"start": v(-14.18, 13.7) * mm, "end": v(-14.24, 13.74) * mm});
            skLineSegment(sketch, "E2752", {"start": v(-14.24, 13.74) * mm, "end": v(-14.3, 13.78) * mm});
            skLineSegment(sketch, "E2753", {"start": v(-14.3, 13.78) * mm, "end": v(-14.35, 13.83) * mm});
            skLineSegment(sketch, "E2754", {"start": v(-14.35, 13.83) * mm, "end": v(-14.4, 13.87) * mm});
            skLineSegment(sketch, "E2755", {"start": v(-14.4, 13.87) * mm, "end": v(-14.46, 13.92) * mm});
            skLineSegment(sketch, "E2756", {"start": v(-14.46, 13.92) * mm, "end": v(-14.52, 13.96) * mm});
            skLineSegment(sketch, "E2757", {"start": v(-14.52, 13.96) * mm, "end": v(-14.58, 14) * mm});
            skLineSegment(sketch, "E2758", {"start": v(-14.58, 14) * mm, "end": v(-14.64, 14.05) * mm});
            skLineSegment(sketch, "E2759", {"start": v(-14.64, 14.05) * mm, "end": v(-14.7, 14.1) * mm});
            skLineSegment(sketch, "E2760", {"start": v(-14.7, 14.1) * mm, "end": v(-14.75, 14.14) * mm});
            skLineSegment(sketch, "E2761", {"start": v(-14.75, 14.14) * mm, "end": v(-14.81, 14.18) * mm});
            skLineSegment(sketch, "E2762", {"start": v(-14.81, 14.18) * mm, "end": v(-14.87, 14.22) * mm});
            skLineSegment(sketch, "E2763", {"start": v(-14.87, 14.22) * mm, "end": v(-14.93, 14.27) * mm});
            skLineSegment(sketch, "E2764", {"start": v(-14.93, 14.27) * mm, "end": v(-15, 14.31) * mm});
            skLineSegment(sketch, "E2765", {"start": v(-15, 14.31) * mm, "end": v(-15.05, 14.35) * mm});
            skLineSegment(sketch, "E2766", {"start": v(-15.05, 14.35) * mm, "end": v(-15.11, 14.4) * mm});
            skLineSegment(sketch, "E2767", {"start": v(-15.11, 14.4) * mm, "end": v(-15.17, 14.44) * mm});
            skLineSegment(sketch, "E2768", {"start": v(-15.17, 14.44) * mm, "end": v(-15.23, 14.48) * mm});
            skLineSegment(sketch, "E2769", {"start": v(-15.23, 14.48) * mm, "end": v(-15.3, 14.52) * mm});
            skLineSegment(sketch, "E2770", {"start": v(-15.3, 14.52) * mm, "end": v(-15.36, 14.57) * mm});
            skLineSegment(sketch, "E2771", {"start": v(-15.36, 14.57) * mm, "end": v(-15.42, 14.6) * mm});
            skLineSegment(sketch, "E2772", {"start": v(-15.42, 14.6) * mm, "end": v(-15.48, 14.65) * mm});
            skLineSegment(sketch, "E2773", {"start": v(-15.48, 14.65) * mm, "end": v(-15.54, 14.7) * mm});
            skLineSegment(sketch, "E2774", {"start": v(-15.54, 14.7) * mm, "end": v(-15.6, 14.73) * mm});
            skLineSegment(sketch, "E2775", {"start": v(-15.6, 14.73) * mm, "end": v(-15.67, 14.78) * mm});
            skLineSegment(sketch, "E2776", {"start": v(-15.67, 14.78) * mm, "end": v(-15.73, 14.82) * mm});
            skLineSegment(sketch, "E2777", {"start": v(-15.73, 14.82) * mm, "end": v(-15.8, 14.86) * mm});
            skLineSegment(sketch, "E2778", {"start": v(-15.8, 14.86) * mm, "end": v(-15.86, 14.9) * mm});
            skLineSegment(sketch, "E2779", {"start": v(-15.86, 14.9) * mm, "end": v(-15.93, 14.94) * mm});
            skLineSegment(sketch, "E2780", {"start": v(-15.93, 14.94) * mm, "end": v(-16, 14.98) * mm});
            skLineSegment(sketch, "E2781", {"start": v(-16, 14.98) * mm, "end": v(-16.06, 15.02) * mm});
            skLineSegment(sketch, "E2782", {"start": v(-16.06, 15.02) * mm, "end": v(-16.12, 15.06) * mm});
            skLineSegment(sketch, "E2783", {"start": v(-16.12, 15.06) * mm, "end": v(-16.19, 15.1) * mm});
            skLineSegment(sketch, "E2784", {"start": v(-16.19, 15.1) * mm, "end": v(-16.25, 15.14) * mm});
            skLineSegment(sketch, "E2785", {"start": v(-16.25, 15.14) * mm, "end": v(-16.32, 15.19) * mm});
            skLineSegment(sketch, "E2786", {"start": v(-16.32, 15.19) * mm, "end": v(-16.39, 15.23) * mm});
            skLineSegment(sketch, "E2787", {"start": v(-16.39, 15.23) * mm, "end": v(-16.45, 15.27) * mm});
            skLineSegment(sketch, "E2788", {"start": v(-16.45, 15.27) * mm, "end": v(-16.52, 15.3) * mm});
            skLineSegment(sketch, "E2789", {"start": v(-16.52, 15.3) * mm, "end": v(-16.59, 15.35) * mm});
            skLineSegment(sketch, "E2790", {"start": v(-16.59, 15.35) * mm, "end": v(-16.66, 15.38) * mm});
            skLineSegment(sketch, "E2791", {"start": v(-16.66, 15.38) * mm, "end": v(-16.73, 15.42) * mm});
            skLineSegment(sketch, "E2792", {"start": v(-16.73, 15.42) * mm, "end": v(-16.8, 15.46) * mm});
            skLineSegment(sketch, "E2793", {"start": v(-16.8, 15.46) * mm, "end": v(-16.84, 15.49) * mm});
            skLineSegment(sketch, "E2794", {"start": v(-16.84, 15.49) * mm, "end": v(-16.88, 15.51) * mm});
            skLineSegment(sketch, "E2795", {"start": v(-16.88, 15.51) * mm, "end": v(-16.92, 15.53) * mm});
            skLineSegment(sketch, "E2796", {"start": v(-16.92, 15.53) * mm, "end": v(-16.96, 15.56) * mm});
            skLineSegment(sketch, "E2797", {"start": v(-16.96, 15.56) * mm, "end": v(-17, 15.58) * mm});
            skLineSegment(sketch, "E2798", {"start": v(-17, 15.58) * mm, "end": v(-17.05, 15.6) * mm});
            skLineSegment(sketch, "E2799", {"start": v(-17.05, 15.6) * mm, "end": v(-17.1, 15.62) * mm});
            skLineSegment(sketch, "E2800", {"start": v(-17.1, 15.62) * mm, "end": v(-17.13, 15.65) * mm});
            skLineSegment(sketch, "E2801", {"start": v(-17.13, 15.65) * mm, "end": v(-17.18, 15.67) * mm});
            skLineSegment(sketch, "E2802", {"start": v(-17.18, 15.67) * mm, "end": v(-17.22, 15.69) * mm});
            skLineSegment(sketch, "E2803", {"start": v(-17.22, 15.69) * mm, "end": v(-17.26, 15.71) * mm});
            skLineSegment(sketch, "E2804", {"start": v(-17.26, 15.71) * mm, "end": v(-17.3, 15.73) * mm});
            skLineSegment(sketch, "E2805", {"start": v(-17.3, 15.73) * mm, "end": v(-17.35, 15.75) * mm});
            skLineSegment(sketch, "E2806", {"start": v(-17.35, 15.75) * mm, "end": v(-17.4, 15.77) * mm});
            skLineSegment(sketch, "E2807", {"start": v(-17.4, 15.77) * mm, "end": v(-17.44, 15.8) * mm});
            skLineSegment(sketch, "E2808", {"start": v(-17.44, 15.8) * mm, "end": v(-17.49, 15.82) * mm});
            skLineSegment(sketch, "E2809", {"start": v(-17.49, 15.82) * mm, "end": v(-17.53, 15.84) * mm});
            skLineSegment(sketch, "E2810", {"start": v(-17.53, 15.84) * mm, "end": v(-17.58, 15.86) * mm});
            skLineSegment(sketch, "E2811", {"start": v(-17.58, 15.86) * mm, "end": v(-17.63, 15.88) * mm});
            skLineSegment(sketch, "E2812", {"start": v(-17.63, 15.88) * mm, "end": v(-17.67, 15.9) * mm});
            skLineSegment(sketch, "E2813", {"start": v(-17.67, 15.9) * mm, "end": v(-17.72, 15.92) * mm});
            skLineSegment(sketch, "E2814", {"start": v(-17.72, 15.92) * mm, "end": v(-17.77, 15.94) * mm});
            skLineSegment(sketch, "E2815", {"start": v(-17.77, 15.94) * mm, "end": v(-17.81, 15.96) * mm});
            skLineSegment(sketch, "E2816", {"start": v(-17.81, 15.96) * mm, "end": v(-17.86, 15.97) * mm});
            skLineSegment(sketch, "E2817", {"start": v(-17.86, 15.97) * mm, "end": v(-17.9, 16) * mm});
            skLineSegment(sketch, "E2818", {"start": v(-17.9, 16) * mm, "end": v(-17.96, 16.01) * mm});
            skLineSegment(sketch, "E2819", {"start": v(-17.96, 16.01) * mm, "end": v(-18, 16.03) * mm});
            skLineSegment(sketch, "E2820", {"start": v(-18, 16.03) * mm, "end": v(-18.05, 16.05) * mm});
            skLineSegment(sketch, "E2821", {"start": v(-18.05, 16.05) * mm, "end": v(-18.1, 16.07) * mm});
            skLineSegment(sketch, "E2822", {"start": v(-18.1, 16.07) * mm, "end": v(-18.15, 16.09) * mm});
            skLineSegment(sketch, "E2823", {"start": v(-18.15, 16.09) * mm, "end": v(-18.2, 16.1) * mm});
            skLineSegment(sketch, "E2824", {"start": v(-18.2, 16.1) * mm, "end": v(-18.25, 16.12) * mm});
            skLineSegment(sketch, "E2825", {"start": v(-18.25, 16.12) * mm, "end": v(-18.3, 16.14) * mm});
            skLineSegment(sketch, "E2826", {"start": v(-18.3, 16.14) * mm, "end": v(-18.35, 16.16) * mm});
            skLineSegment(sketch, "E2827", {"start": v(-18.35, 16.16) * mm, "end": v(-18.4, 16.17) * mm});
            skLineSegment(sketch, "E2828", {"start": v(-18.4, 16.17) * mm, "end": v(-18.45, 16.2) * mm});
            skLineSegment(sketch, "E2829", {"start": v(-18.45, 16.2) * mm, "end": v(-18.5, 16.2) * mm});
            skLineSegment(sketch, "E2830", {"start": v(-18.5, 16.2) * mm, "end": v(-18.56, 16.22) * mm});
            skLineSegment(sketch, "E2831", {"start": v(-18.56, 16.22) * mm, "end": v(-18.6, 16.24) * mm});
            skLineSegment(sketch, "E2832", {"start": v(-18.6, 16.24) * mm, "end": v(-18.66, 16.26) * mm});
            skLineSegment(sketch, "E2833", {"start": v(-18.66, 16.26) * mm, "end": v(-18.71, 16.27) * mm});
            skLineSegment(sketch, "E2834", {"start": v(-18.71, 16.27) * mm, "end": v(-18.76, 16.29) * mm});
            skLineSegment(sketch, "E2835", {"start": v(-18.76, 16.29) * mm, "end": v(-18.82, 16.3) * mm});
            skLineSegment(sketch, "E2836", {"start": v(-18.82, 16.3) * mm, "end": v(-18.87, 16.32) * mm});
            skLineSegment(sketch, "E2837", {"start": v(-18.87, 16.32) * mm, "end": v(-18.92, 16.34) * mm});
            skLineSegment(sketch, "E2838", {"start": v(-18.92, 16.34) * mm, "end": v(-18.97, 16.35) * mm});
            skLineSegment(sketch, "E2839", {"start": v(-18.97, 16.35) * mm, "end": v(-19.03, 16.37) * mm});
            skLineSegment(sketch, "E2840", {"start": v(-19.03, 16.37) * mm, "end": v(-19.08, 16.38) * mm});
            skLineSegment(sketch, "E2841", {"start": v(-19.08, 16.38) * mm, "end": v(-19.14, 16.4) * mm});
            skLineSegment(sketch, "E2842", {"start": v(-19.14, 16.4) * mm, "end": v(-19.2, 16.41) * mm});
            skLineSegment(sketch, "E2843", {"start": v(-19.2, 16.41) * mm, "end": v(-19.25, 16.42) * mm});
            skLineSegment(sketch, "E2844", {"start": v(-19.25, 16.42) * mm, "end": v(-19.3, 16.44) * mm});
            skLineSegment(sketch, "E2845", {"start": v(-19.3, 16.44) * mm, "end": v(-19.36, 16.45) * mm});
            skLineSegment(sketch, "E2846", {"start": v(-19.36, 16.45) * mm, "end": v(-19.41, 16.47) * mm});
            skLineSegment(sketch, "E2847", {"start": v(-19.41, 16.47) * mm, "end": v(-19.47, 16.48) * mm});
            skLineSegment(sketch, "E2848", {"start": v(-19.47, 16.48) * mm, "end": v(-19.52, 16.5) * mm});
            skLineSegment(sketch, "E2849", {"start": v(-19.52, 16.5) * mm, "end": v(-19.58, 16.5) * mm});
            skLineSegment(sketch, "E2850", {"start": v(-19.58, 16.5) * mm, "end": v(-19.64, 16.52) * mm});
            skLineSegment(sketch, "E2851", {"start": v(-19.64, 16.52) * mm, "end": v(-19.7, 16.53) * mm});
            skLineSegment(sketch, "E2852", {"start": v(-19.7, 16.53) * mm, "end": v(-19.75, 16.55) * mm});
            skLineSegment(sketch, "E2853", {"start": v(-19.75, 16.55) * mm, "end": v(-19.8, 16.56) * mm});
            skLineSegment(sketch, "E2854", {"start": v(-19.8, 16.56) * mm, "end": v(-19.86, 16.57) * mm});
            skLineSegment(sketch, "E2855", {"start": v(-19.86, 16.57) * mm, "end": v(-19.92, 16.58) * mm});
            skLineSegment(sketch, "E2856", {"start": v(-19.92, 16.58) * mm, "end": v(-19.98, 16.6) * mm});
            skLineSegment(sketch, "E2857", {"start": v(-19.98, 16.6) * mm, "end": v(-20.04, 16.6) * mm});
            skLineSegment(sketch, "E2858", {"start": v(-20.04, 16.6) * mm, "end": v(-20.1, 16.62) * mm});
            skLineSegment(sketch, "E2859", {"start": v(-20.1, 16.62) * mm, "end": v(-20.16, 16.63) * mm});
            skLineSegment(sketch, "E2860", {"start": v(-20.16, 16.63) * mm, "end": v(-20.22, 16.64) * mm});
            skLineSegment(sketch, "E2861", {"start": v(-20.22, 16.64) * mm, "end": v(-20.28, 16.65) * mm});
            skLineSegment(sketch, "E2862", {"start": v(-20.28, 16.65) * mm, "end": v(-20.34, 16.66) * mm});
            skLineSegment(sketch, "E2863", {"start": v(-20.34, 16.66) * mm, "end": v(-20.4, 16.67) * mm});
            skLineSegment(sketch, "E2864", {"start": v(-20.4, 16.67) * mm, "end": v(-20.46, 16.68) * mm});
            skLineSegment(sketch, "E2865", {"start": v(-20.46, 16.68) * mm, "end": v(-20.52, 16.7) * mm});
            skLineSegment(sketch, "E2866", {"start": v(-20.52, 16.7) * mm, "end": v(-20.58, 16.7) * mm});
            skLineSegment(sketch, "E2867", {"start": v(-20.58, 16.7) * mm, "end": v(-20.64, 16.71) * mm});
            skLineSegment(sketch, "E2868", {"start": v(-20.64, 16.71) * mm, "end": v(-20.7, 16.72) * mm});
            skLineSegment(sketch, "E2869", {"start": v(-20.7, 16.72) * mm, "end": v(-20.76, 16.73) * mm});
            skLineSegment(sketch, "E2870", {"start": v(-20.76, 16.73) * mm, "end": v(-20.82, 16.74) * mm});
            skLineSegment(sketch, "E2871", {"start": v(-20.82, 16.74) * mm, "end": v(-20.88, 16.75) * mm});
            skLineSegment(sketch, "E2872", {"start": v(-20.88, 16.75) * mm, "end": v(-20.95, 16.76) * mm});
            skLineSegment(sketch, "E2873", {"start": v(-20.95, 16.76) * mm, "end": v(-21, 16.77) * mm});
            skLineSegment(sketch, "E2874", {"start": v(-21, 16.77) * mm, "end": v(-21.07, 16.78) * mm});
            skLineSegment(sketch, "E2875", {"start": v(-21.07, 16.78) * mm, "end": v(-21.13, 16.79) * mm});
            skLineSegment(sketch, "E2876", {"start": v(-21.13, 16.79) * mm, "end": v(-21.2, 16.8) * mm});
            skLineSegment(sketch, "E2877", {"start": v(-21.2, 16.8) * mm, "end": v(-21.26, 16.8) * mm});
            skLineSegment(sketch, "E2878", {"start": v(-21.26, 16.8) * mm, "end": v(-21.33, 16.8) * mm});
            skLineSegment(sketch, "E2879", {"start": v(-21.33, 16.8) * mm, "end": v(-21.39, 16.82) * mm});
            skLineSegment(sketch, "E2880", {"start": v(-21.39, 16.82) * mm, "end": v(-21.45, 16.82) * mm});
            skLineSegment(sketch, "E2881", {"start": v(-21.45, 16.82) * mm, "end": v(-21.52, 16.83) * mm});
            skLineSegment(sketch, "E2882", {"start": v(-21.52, 16.83) * mm, "end": v(-21.58, 16.84) * mm});
            skLineSegment(sketch, "E2883", {"start": v(-21.58, 16.84) * mm, "end": v(-21.65, 16.85) * mm});
            skLineSegment(sketch, "E2884", {"start": v(-21.65, 16.85) * mm, "end": v(-21.71, 16.85) * mm});
            skLineSegment(sketch, "E2885", {"start": v(-21.71, 16.85) * mm, "end": v(-21.78, 16.86) * mm});
            skLineSegment(sketch, "E2886", {"start": v(-21.78, 16.86) * mm, "end": v(-21.84, 16.87) * mm});
            skLineSegment(sketch, "E2887", {"start": v(-21.84, 16.87) * mm, "end": v(-21.91, 16.87) * mm});
            skLineSegment(sketch, "E2888", {"start": v(-21.91, 16.87) * mm, "end": v(-21.98, 16.88) * mm});
            skLineSegment(sketch, "E2889", {"start": v(-21.98, 16.88) * mm, "end": v(-22.04, 16.88) * mm});
            skLineSegment(sketch, "E2890", {"start": v(-22.04, 16.88) * mm, "end": v(-22.11, 16.89) * mm});
            skLineSegment(sketch, "E2891", {"start": v(-22.11, 16.89) * mm, "end": v(-22.18, 16.9) * mm});
            skLineSegment(sketch, "E2892", {"start": v(-22.18, 16.9) * mm, "end": v(-22.25, 16.9) * mm});
            skLineSegment(sketch, "E2893", {"start": v(-22.25, 16.9) * mm, "end": v(-22.31, 16.9) * mm});
            skLineSegment(sketch, "E2894", {"start": v(-22.31, 16.9) * mm, "end": v(-22.38, 16.91) * mm});
            skLineSegment(sketch, "E2895", {"start": v(-22.38, 16.91) * mm, "end": v(-22.45, 16.92) * mm});
            skLineSegment(sketch, "E2896", {"start": v(-22.45, 16.92) * mm, "end": v(-22.52, 16.92) * mm});
            skLineSegment(sketch, "E2897", {"start": v(-22.52, 16.92) * mm, "end": v(-22.59, 16.92) * mm});
            skLineSegment(sketch, "E2898", {"start": v(-22.59, 16.92) * mm, "end": v(-22.66, 16.93) * mm});
            skLineSegment(sketch, "E2899", {"start": v(-22.66, 16.93) * mm, "end": v(-22.72, 16.93) * mm});
            skLineSegment(sketch, "E2900", {"start": v(-22.72, 16.93) * mm, "end": v(-22.8, 16.94) * mm});
            skLineSegment(sketch, "E2901", {"start": v(-22.8, 16.94) * mm, "end": v(-22.86, 16.94) * mm});
            skLineSegment(sketch, "E2902", {"start": v(-22.86, 16.94) * mm, "end": v(-22.93, 16.94) * mm});
            skLineSegment(sketch, "E2903", {"start": v(-22.93, 16.94) * mm, "end": v(-23, 16.95) * mm});
            skLineSegment(sketch, "E2904", {"start": v(-23, 16.95) * mm, "end": v(-23.07, 16.95) * mm});
            skLineSegment(sketch, "E2905", {"start": v(-23.07, 16.95) * mm, "end": v(-23.14, 16.95) * mm});
            skLineSegment(sketch, "E2906", {"start": v(-23.14, 16.95) * mm, "end": v(-23.22, 16.96) * mm});
            skLineSegment(sketch, "E2907", {"start": v(-23.22, 16.96) * mm, "end": v(-23.29, 16.96) * mm});
            skLineSegment(sketch, "E2908", {"start": v(-23.29, 16.96) * mm, "end": v(-23.36, 16.96) * mm});
            skLineSegment(sketch, "E2909", {"start": v(-23.36, 16.96) * mm, "end": v(-23.43, 16.96) * mm});
            skLineSegment(sketch, "E2910", {"start": v(-23.43, 16.96) * mm, "end": v(-23.5, 16.96) * mm});
            skLineSegment(sketch, "E2911", {"start": v(-23.5, 16.96) * mm, "end": v(-23.57, 16.97) * mm});
            skLineSegment(sketch, "E2912", {"start": v(-23.57, 16.97) * mm, "end": v(-23.65, 16.97) * mm});
            skLineSegment(sketch, "E2913", {"start": v(-23.65, 16.97) * mm, "end": v(-23.72, 16.97) * mm});
            skLineSegment(sketch, "E2914", {"start": v(-23.72, 16.97) * mm, "end": v(-23.8, 16.97) * mm});
            skLineSegment(sketch, "E2915", {"start": v(-23.8, 16.97) * mm, "end": v(-23.86, 16.97) * mm});
            skLineSegment(sketch, "E2916", {"start": v(-23.86, 16.97) * mm, "end": v(-23.94, 16.97) * mm});
            skLineSegment(sketch, "E2917", {"start": v(-23.94, 16.97) * mm, "end": v(-24.01, 16.97) * mm});
            skLineSegment(sketch, "E2918", {"start": v(-24.01, 16.97) * mm, "end": v(-24.09, 16.97) * mm});
            skLineSegment(sketch, "E2919", {"start": v(-24.09, 16.97) * mm, "end": v(-24.16, 16.97) * mm});
            skLineSegment(sketch, "E2920", {"start": v(-24.16, 16.97) * mm, "end": v(-24.23, 16.97) * mm});
            skLineSegment(sketch, "E2921", {"start": v(-24.23, 16.97) * mm, "end": v(-24.34, 16.97) * mm});
            skLineSegment(sketch, "E2922", {"start": v(-24.34, 16.97) * mm, "end": v(-24.44, 16.97) * mm});
            skLineSegment(sketch, "E2923", {"start": v(-24.44, 16.97) * mm, "end": v(-24.54, 16.97) * mm});
            skLineSegment(sketch, "E2924", {"start": v(-24.54, 16.97) * mm, "end": v(-24.65, 16.97) * mm});
            skLineSegment(sketch, "E2925", {"start": v(-24.65, 16.97) * mm, "end": v(-24.75, 16.97) * mm});
            skLineSegment(sketch, "E2926", {"start": v(-24.75, 16.97) * mm, "end": v(-24.85, 16.97) * mm});
            skLineSegment(sketch, "E2927", {"start": v(-24.85, 16.97) * mm, "end": v(-24.96, 16.96) * mm});
            skLineSegment(sketch, "E2928", {"start": v(-24.96, 16.96) * mm, "end": v(-25.06, 16.96) * mm});
            skLineSegment(sketch, "E2929", {"start": v(-25.06, 16.96) * mm, "end": v(-25.16, 16.96) * mm});
            skLineSegment(sketch, "E2930", {"start": v(-25.16, 16.96) * mm, "end": v(-25.27, 16.96) * mm});
            skLineSegment(sketch, "E2931", {"start": v(-25.27, 16.96) * mm, "end": v(-25.37, 16.95) * mm});
            skLineSegment(sketch, "E2932", {"start": v(-25.37, 16.95) * mm, "end": v(-25.47, 16.95) * mm});
            skLineSegment(sketch, "E2933", {"start": v(-25.47, 16.95) * mm, "end": v(-25.58, 16.95) * mm});
            skLineSegment(sketch, "E2934", {"start": v(-25.58, 16.95) * mm, "end": v(-25.68, 16.94) * mm});
            skLineSegment(sketch, "E2935", {"start": v(-25.68, 16.94) * mm, "end": v(-25.79, 16.94) * mm});
            skLineSegment(sketch, "E2936", {"start": v(-25.79, 16.94) * mm, "end": v(-25.89, 16.93) * mm});
            skLineSegment(sketch, "E2937", {"start": v(-25.89, 16.93) * mm, "end": v(-26, 16.93) * mm});
            skLineSegment(sketch, "E2938", {"start": v(-26, 16.93) * mm, "end": v(-26.1, 16.92) * mm});
            skLineSegment(sketch, "E2939", {"start": v(-26.1, 16.92) * mm, "end": v(-26.2, 16.91) * mm});
            skLineSegment(sketch, "E2940", {"start": v(-26.2, 16.91) * mm, "end": v(-26.3, 16.9) * mm});
            skLineSegment(sketch, "E2941", {"start": v(-26.3, 16.9) * mm, "end": v(-26.4, 16.9) * mm});
            skLineSegment(sketch, "E2942", {"start": v(-26.4, 16.9) * mm, "end": v(-26.51, 16.9) * mm});
            skLineSegment(sketch, "E2943", {"start": v(-26.51, 16.9) * mm, "end": v(-26.62, 16.89) * mm});
            skLineSegment(sketch, "E2944", {"start": v(-26.62, 16.89) * mm, "end": v(-26.72, 16.88) * mm});
            skLineSegment(sketch, "E2945", {"start": v(-26.72, 16.88) * mm, "end": v(-26.82, 16.87) * mm});
            skLineSegment(sketch, "E2946", {"start": v(-26.82, 16.87) * mm, "end": v(-26.93, 16.87) * mm});
            skLineSegment(sketch, "E2947", {"start": v(-26.93, 16.87) * mm, "end": v(-27.03, 16.86) * mm});
            skLineSegment(sketch, "E2948", {"start": v(-27.03, 16.86) * mm, "end": v(-27.13, 16.85) * mm});
            skLineSegment(sketch, "E2949", {"start": v(-27.13, 16.85) * mm, "end": v(-27.24, 16.84) * mm});
            skLineSegment(sketch, "E2950", {"start": v(-27.24, 16.84) * mm, "end": v(-27.34, 16.83) * mm});
            skLineSegment(sketch, "E2951", {"start": v(-27.34, 16.83) * mm, "end": v(-27.45, 16.82) * mm});
            skLineSegment(sketch, "E2952", {"start": v(-27.45, 16.82) * mm, "end": v(-27.55, 16.81) * mm});
            skLineSegment(sketch, "E2953", {"start": v(-27.55, 16.81) * mm, "end": v(-27.65, 16.8) * mm});
            skLineSegment(sketch, "E2954", {"start": v(-27.65, 16.8) * mm, "end": v(-27.76, 16.8) * mm});
            skLineSegment(sketch, "E2955", {"start": v(-27.76, 16.8) * mm, "end": v(-27.86, 16.78) * mm});
            skLineSegment(sketch, "E2956", {"start": v(-27.86, 16.78) * mm, "end": v(-27.96, 16.77) * mm});
            skLineSegment(sketch, "E2957", {"start": v(-27.96, 16.77) * mm, "end": v(-28.07, 16.76) * mm});
            skLineSegment(sketch, "E2958", {"start": v(-28.07, 16.76) * mm, "end": v(-28.17, 16.75) * mm});
            skLineSegment(sketch, "E2959", {"start": v(-28.17, 16.75) * mm, "end": v(-28.27, 16.74) * mm});
            skLineSegment(sketch, "E2960", {"start": v(-28.27, 16.74) * mm, "end": v(-28.37, 16.73) * mm});
            skLineSegment(sketch, "E2961", {"start": v(-28.37, 16.73) * mm, "end": v(-28.48, 16.72) * mm});
            skLineSegment(sketch, "E2962", {"start": v(-28.48, 16.72) * mm, "end": v(-28.58, 16.7) * mm});
            skLineSegment(sketch, "E2963", {"start": v(-28.58, 16.7) * mm, "end": v(-28.68, 16.7) * mm});
            skLineSegment(sketch, "E2964", {"start": v(-28.68, 16.7) * mm, "end": v(-28.78, 16.68) * mm});
            skLineSegment(sketch, "E2965", {"start": v(-28.78, 16.68) * mm, "end": v(-28.89, 16.67) * mm});
            skLineSegment(sketch, "E2966", {"start": v(-28.89, 16.67) * mm, "end": v(-28.99, 16.66) * mm});
            skLineSegment(sketch, "E2967", {"start": v(-28.99, 16.66) * mm, "end": v(-29.09, 16.64) * mm});
            skLineSegment(sketch, "E2968", {"start": v(-29.09, 16.64) * mm, "end": v(-29.2, 16.63) * mm});
            skLineSegment(sketch, "E2969", {"start": v(-29.2, 16.63) * mm, "end": v(-29.3, 16.62) * mm});
            skLineSegment(sketch, "E2970", {"start": v(-29.3, 16.62) * mm, "end": v(-29.4, 16.6) * mm});
            skLineSegment(sketch, "E2971", {"start": v(-29.4, 16.6) * mm, "end": v(-29.5, 16.6) * mm});
            skLineSegment(sketch, "E2972", {"start": v(-29.5, 16.6) * mm, "end": v(-29.6, 16.58) * mm});
            skLineSegment(sketch, "E2973", {"start": v(-29.6, 16.58) * mm, "end": v(-29.7, 16.56) * mm});
            skLineSegment(sketch, "E2974", {"start": v(-29.7, 16.56) * mm, "end": v(-29.8, 16.55) * mm});
            skLineSegment(sketch, "E2975", {"start": v(-29.8, 16.55) * mm, "end": v(-29.9, 16.54) * mm});
            skLineSegment(sketch, "E2976", {"start": v(-29.9, 16.54) * mm, "end": v(-30, 16.52) * mm});
            skLineSegment(sketch, "E2977", {"start": v(-30, 16.52) * mm, "end": v(-30.1, 16.5) * mm});
            skLineSegment(sketch, "E2978", {"start": v(-30.1, 16.5) * mm, "end": v(-30.2, 16.5) * mm});
            skLineSegment(sketch, "E2979", {"start": v(-30.2, 16.5) * mm, "end": v(-30.3, 16.48) * mm});
            skLineSegment(sketch, "E2980", {"start": v(-30.3, 16.48) * mm, "end": v(-30.4, 16.46) * mm});
            skLineSegment(sketch, "E2981", {"start": v(-30.4, 16.46) * mm, "end": v(-30.5, 16.45) * mm});
            skLineSegment(sketch, "E2982", {"start": v(-30.5, 16.45) * mm, "end": v(-30.6, 16.43) * mm});
            skLineSegment(sketch, "E2983", {"start": v(-30.6, 16.43) * mm, "end": v(-30.7, 16.42) * mm});
            skLineSegment(sketch, "E2984", {"start": v(-30.7, 16.42) * mm, "end": v(-30.8, 16.4) * mm});
            skLineSegment(sketch, "E2985", {"start": v(-30.8, 16.4) * mm, "end": v(-30.9, 16.39) * mm});
            skLineSegment(sketch, "E2986", {"start": v(-30.9, 16.39) * mm, "end": v(-31, 16.37) * mm});
            skLineSegment(sketch, "E2987", {"start": v(-31, 16.37) * mm, "end": v(-31.09, 16.35) * mm});
            skLineSegment(sketch, "E2988", {"start": v(-31.09, 16.35) * mm, "end": v(-31.19, 16.34) * mm});
            skLineSegment(sketch, "E2989", {"start": v(-31.19, 16.34) * mm, "end": v(-31.28, 16.32) * mm});
            skLineSegment(sketch, "E2990", {"start": v(-31.28, 16.32) * mm, "end": v(-31.38, 16.3) * mm});
            skLineSegment(sketch, "E2991", {"start": v(-31.38, 16.3) * mm, "end": v(-31.48, 16.29) * mm});
            skLineSegment(sketch, "E2992", {"start": v(-31.48, 16.29) * mm, "end": v(-31.57, 16.27) * mm});
            skLineSegment(sketch, "E2993", {"start": v(-31.57, 16.27) * mm, "end": v(-31.67, 16.26) * mm});
            skLineSegment(sketch, "E2994", {"start": v(-31.67, 16.26) * mm, "end": v(-31.77, 16.24) * mm});
            skLineSegment(sketch, "E2995", {"start": v(-31.77, 16.24) * mm, "end": v(-31.86, 16.22) * mm});
            skLineSegment(sketch, "E2996", {"start": v(-31.86, 16.22) * mm, "end": v(-31.96, 16.2) * mm});
            skLineSegment(sketch, "E2997", {"start": v(-31.96, 16.2) * mm, "end": v(-32.05, 16.19) * mm});
            skLineSegment(sketch, "E2998", {"start": v(-32.05, 16.19) * mm, "end": v(-32.15, 16.17) * mm});
            skLineSegment(sketch, "E2999", {"start": v(-32.15, 16.17) * mm, "end": v(-32.24, 16.15) * mm});
            skLineSegment(sketch, "E3000", {"start": v(-32.24, 16.15) * mm, "end": v(-32.33, 16.14) * mm});
            skLineSegment(sketch, "E3001", {"start": v(-32.33, 16.14) * mm, "end": v(-32.43, 16.12) * mm});
            skLineSegment(sketch, "E3002", {"start": v(-32.43, 16.12) * mm, "end": v(-32.52, 16.1) * mm});
            skLineSegment(sketch, "E3003", {"start": v(-32.52, 16.1) * mm, "end": v(-32.61, 16.08) * mm});
            skLineSegment(sketch, "E3004", {"start": v(-32.61, 16.08) * mm, "end": v(-32.7, 16.07) * mm});
            skLineSegment(sketch, "E3005", {"start": v(-32.7, 16.07) * mm, "end": v(-32.8, 16.05) * mm});
            skLineSegment(sketch, "E3006", {"start": v(-32.8, 16.05) * mm, "end": v(-32.9, 16.03) * mm});
            skLineSegment(sketch, "E3007", {"start": v(-32.9, 16.03) * mm, "end": v(-32.98, 16.01) * mm});
            skLineSegment(sketch, "E3008", {"start": v(-32.98, 16.01) * mm, "end": v(-33.07, 16) * mm});
            skLineSegment(sketch, "E3009", {"start": v(-33.07, 16) * mm, "end": v(-33.16, 15.98) * mm});
            skLineSegment(sketch, "E3010", {"start": v(-33.16, 15.98) * mm, "end": v(-33.25, 15.96) * mm});
            skLineSegment(sketch, "E3011", {"start": v(-33.25, 15.96) * mm, "end": v(-33.34, 15.94) * mm});
            skLineSegment(sketch, "E3012", {"start": v(-33.34, 15.94) * mm, "end": v(-33.43, 15.92) * mm});
            skLineSegment(sketch, "E3013", {"start": v(-33.43, 15.92) * mm, "end": v(-33.52, 15.9) * mm});
            skLineSegment(sketch, "E3014", {"start": v(-33.52, 15.9) * mm, "end": v(-33.61, 15.89) * mm});
            skLineSegment(sketch, "E3015", {"start": v(-33.61, 15.89) * mm, "end": v(-33.7, 15.87) * mm});
            skLineSegment(sketch, "E3016", {"start": v(-33.7, 15.87) * mm, "end": v(-33.79, 15.85) * mm});
            skLineSegment(sketch, "E3017", {"start": v(-33.79, 15.85) * mm, "end": v(-33.88, 15.83) * mm});
            skLineSegment(sketch, "E3018", {"start": v(-33.88, 15.83) * mm, "end": v(-33.96, 15.81) * mm});
            skLineSegment(sketch, "E3019", {"start": v(-33.96, 15.81) * mm, "end": v(-34.05, 15.8) * mm});
            skLineSegment(sketch, "E3020", {"start": v(-34.05, 15.8) * mm, "end": v(-34.14, 15.78) * mm});
            skLineSegment(sketch, "E3021", {"start": v(-34.14, 15.78) * mm, "end": v(-34.22, 15.76) * mm});
            skLineSegment(sketch, "E3022", {"start": v(-34.22, 15.76) * mm, "end": v(-34.3, 15.74) * mm});
            skLineSegment(sketch, "E3023", {"start": v(-34.3, 15.74) * mm, "end": v(-34.4, 15.72) * mm});
            skLineSegment(sketch, "E3024", {"start": v(-34.4, 15.72) * mm, "end": v(-34.48, 15.7) * mm});
            skLineSegment(sketch, "E3025", {"start": v(-34.48, 15.7) * mm, "end": v(-34.56, 15.68) * mm});
            skLineSegment(sketch, "E3026", {"start": v(-34.56, 15.68) * mm, "end": v(-34.64, 15.66) * mm});
            skLineSegment(sketch, "E3027", {"start": v(-34.64, 15.66) * mm, "end": v(-34.73, 15.65) * mm});
            skLineSegment(sketch, "E3028", {"start": v(-34.73, 15.65) * mm, "end": v(-34.8, 15.63) * mm});
            skLineSegment(sketch, "E3029", {"start": v(-34.8, 15.63) * mm, "end": v(-34.9, 15.6) * mm});
            skLineSegment(sketch, "E3030", {"start": v(-34.9, 15.6) * mm, "end": v(-34.97, 15.59) * mm});
            skLineSegment(sketch, "E3031", {"start": v(-34.97, 15.59) * mm, "end": v(-35.05, 15.57) * mm});
            skLineSegment(sketch, "E3032", {"start": v(-35.05, 15.57) * mm, "end": v(-35.13, 15.55) * mm});
            skLineSegment(sketch, "E3033", {"start": v(-35.13, 15.55) * mm, "end": v(-35.21, 15.53) * mm});
            skLineSegment(sketch, "E3034", {"start": v(-35.21, 15.53) * mm, "end": v(-35.3, 15.52) * mm});
            skLineSegment(sketch, "E3035", {"start": v(-35.3, 15.52) * mm, "end": v(-35.37, 15.5) * mm});
            skLineSegment(sketch, "E3036", {"start": v(-35.37, 15.5) * mm, "end": v(-35.45, 15.48) * mm});
            skLineSegment(sketch, "E3037", {"start": v(-35.45, 15.48) * mm, "end": v(-35.53, 15.46) * mm});
            skLineSegment(sketch, "E3038", {"start": v(-35.53, 15.46) * mm, "end": v(-35.6, 15.44) * mm});
            skLineSegment(sketch, "E3039", {"start": v(-35.6, 15.44) * mm, "end": v(-35.68, 15.42) * mm});
            skLineSegment(sketch, "E3040", {"start": v(-35.68, 15.42) * mm, "end": v(-35.76, 15.4) * mm});
            skLineSegment(sketch, "E3041", {"start": v(-35.76, 15.4) * mm, "end": v(-35.84, 15.39) * mm});
            skLineSegment(sketch, "E3042", {"start": v(-35.84, 15.39) * mm, "end": v(-35.91, 15.37) * mm});
            skLineSegment(sketch, "E3043", {"start": v(-35.91, 15.37) * mm, "end": v(-35.98, 15.35) * mm});
            skLineSegment(sketch, "E3044", {"start": v(-35.98, 15.35) * mm, "end": v(-36.06, 15.33) * mm});
            skLineSegment(sketch, "E3045", {"start": v(-36.06, 15.33) * mm, "end": v(-36.13, 15.31) * mm});
            skLineSegment(sketch, "E3046", {"start": v(-36.13, 15.31) * mm, "end": v(-36.2, 15.3) * mm});
            skLineSegment(sketch, "E3047", {"start": v(-36.2, 15.3) * mm, "end": v(-36.28, 15.28) * mm});
            skLineSegment(sketch, "E3048", {"start": v(-36.28, 15.28) * mm, "end": v(-36.35, 15.26) * mm});
            skSolve(sketch);
        }
        {
            var Q0;
            Q0=makeQuery(id+"F0.imprint","IMPRINT",FACE,{"disambiguationData":[TD([[makeQuery(id+"F0.imprint","IMPRINT",EDGE,{"derivedFrom":sQuery(id+"F0.wireOp",EDGE,"E0")}),1.0]])]});
            extrude(context, id + "F1", {"entities" : qUnion([Q0]), "depth" : 25.4 * mm, "offsetDistance" : 25.4 * mm});
        }
    });
